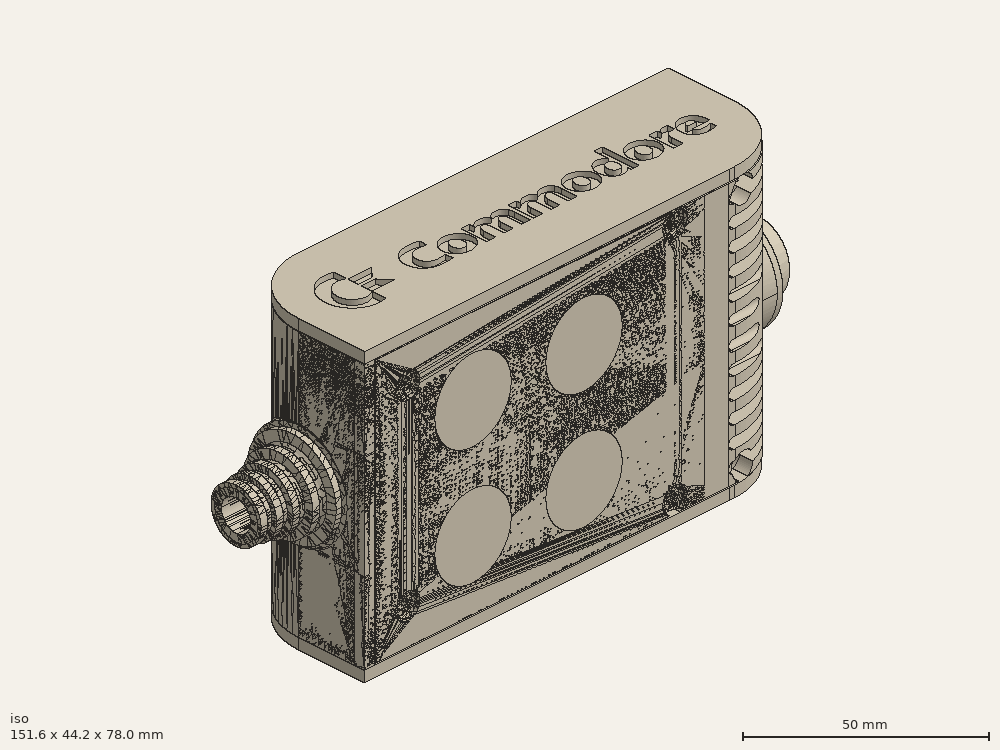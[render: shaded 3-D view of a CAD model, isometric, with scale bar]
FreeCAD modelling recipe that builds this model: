
FCSTD DOCUMENT  (FreeCAD 0.19R0.19.2)
Label: enclosure_220FCStd
License: All rights reserved
LicenseURL: http://en.wikipedia.org/wiki/All_rights_reserved
objects: Part::Revolution×152, Part::MultiFuse×146, Part::Feature×146, Sketcher::SketchObject×90, Part::Extrusion×74, Part::Cut×72, Part::Cylinder×70, Part::Fillet×58, Part::Box×36, App::MeasureDistance×4, Part::Chamfer×4, Part::FeaturePython×2, Image::ImagePlane×1, PartDesign::Body×1, Part::Mirroring×1
note: 852 computed .brp shape members not serialized (recipe doc carries the construction recipe); baked Part::Feature solids carry a one-line shape summary decoded from their .brp

FEATURE [Sketcher::SketchObject] Sketch  label="topSketch"
  FullyConstrained = true
  sketch-geometry (20):
    g0: LineSegment StartX=5.21097e-06 StartY=3 StartZ=0 EndX=5.21097e-06 EndY=19 EndZ=0
    g1: ArcOfCircle CenterX=19 CenterY=19 CenterZ=0 NormalX=0 NormalY=0 NormalZ=1 AngleXU=0 Radius=19 StartAngle=1.5708 EndAngle=3.14159
    g2: ArcOfCircle CenterX=19 CenterY=19 CenterZ=0 NormalX=0 NormalY=0 NormalZ=1 AngleXU=0 Radius=16 StartAngle=1.5708 EndAngle=3.14159
    g3: LineSegment StartX=114 StartY=35 StartZ=0 EndX=19 EndY=35 EndZ=0
    g4: LineSegment StartX=5.21097e-06 StartY=3 StartZ=0 EndX=5.21097e-06 EndY=0 EndZ=0
    g5: LineSegment StartX=3 StartY=0 StartZ=0 EndX=5.21097e-06 EndY=0 EndZ=0
    g6: LineSegment StartX=3 StartY=19 StartZ=0 EndX=3 EndY=0 EndZ=0
    g7: LineSegment StartX=19 StartY=38 StartZ=0 EndX=124 EndY=38 EndZ=0
    g8: Circle CenterX=119 CenterY=35 CenterZ=0 NormalX=0 NormalY=0 NormalZ=1 AngleXU=0 Radius=1
    g9: Circle CenterX=121 CenterY=35 CenterZ=0 NormalX=0 NormalY=0 NormalZ=1 AngleXU=0 Radius=1
    g10: Circle CenterX=121 CenterY=33 CenterZ=0 NormalX=0 NormalY=0 NormalZ=1 AngleXU=0 Radius=1
    g11: BSplineCurve PolesCount=3 KnotsCount=2 Degree=2 IsPeriodic=0
    g12: GeomPoint X=119 Y=35 Z=0
    g13: GeomPoint X=121 Y=33 Z=0
    g14: LineSegment StartX=119 StartY=35 StartZ=0 EndX=114 EndY=35 EndZ=0
    g15: ArcOfCircle CenterX=105 CenterY=19 CenterZ=0 NormalX=0 NormalY=0 NormalZ=1 AngleXU=0 Radius=19 StartAngle=5.7297 EndAngle=6.28319
    g16: ArcOfCircle CenterX=105 CenterY=19 CenterZ=0 NormalX=0 NormalY=0 NormalZ=1 AngleXU=0 Radius=16 StartAngle=5.60905 EndAngle=6.28319
    g17: LineSegment StartX=121 StartY=33 StartZ=0 EndX=121 EndY=19 EndZ=0
    g18: LineSegment StartX=124 StartY=38 StartZ=0 EndX=124 EndY=19 EndZ=0
    g19: LineSegment StartX=117.5 StartY=9.01251 StartZ=0 EndX=121.163 EndY=9.0125 EndZ=0
  constraints (46):
    c: Vertical(g0)
    c: Block(g0)
    c: Coincident(g1,g0)
    c: Block(g1)
    c: Coincident(g2,g1)
    c: Block(g2)
    c: Coincident(g3,g2)
    c: Horizontal(g3)
    c: Tangent(g3,g2)
    c: Coincident(g4,g0)
    c: Distance(g4) = 3
    c: Vertical(g4)
    c: Coincident(g5,g4)
    c: Horizontal(g5)
    c: Coincident(g6,g2)
    c: Coincident(g6,g5)
    c: Vertical(g6)
    c: Horizontal(g7)
    c: Distance(g7) = 105
    c: Coincident(g7,g1)
    c: Block(g3)
    c: Weight(g8) = 1
    c: Equal(g8,g9)
    c: Equal(g8,g10)
    c: InternalAlignment(g8,g11)
    c: InternalAlignment(g9,g11)
    c: InternalAlignment(g10,g11)
    c: InternalAlignment(g12,g11)
    c: InternalAlignment(g13,g11)
    c: Block(g11)
    c: Coincident(g14,g11)
    c: Coincident(g14,g3)
    c: Horizontal(g14)
    c: Block(g15)
    c: Coincident(g16,g15)
    c: Block(g16)
    c: Coincident(g17,g11)
    c: Coincident(g17,g16)
    c: Vertical(g17)
    c: Distance(g17) = 14
    c: Coincident(g18,g7)
    c: Coincident(g18,g15)
    c: Vertical(g18)
    c: Distance(g18) = 19
    c: Coincident(g19,g16)
    c: Coincident(g19,g15)
FEATURE [Sketcher::SketchObject] Sketch001  label="bottomSketch"
  FullyConstrained = true
  sketch-geometry (32):
    g0: LineSegment StartX=3.3 StartY=-6.03275e-07 StartZ=0 EndX=98 EndY=-6.03275e-07 EndZ=0
    g1: ArcOfCircle CenterX=98 CenterY=19 CenterZ=0 NormalX=0 NormalY=0 NormalZ=1 AngleXU=0 Radius=19 StartAngle=4.71239 EndAngle=5.71103
    g2: LineSegment StartX=6.3 StartY=8 StartZ=0 EndX=3.3 EndY=8 EndZ=0
    g3: LineSegment StartX=3.3 StartY=8 StartZ=0 EndX=3.3 EndY=-6.03275e-07 EndZ=0
    g4: ArcOfCircle CenterX=8.3 CenterY=5 CenterZ=0 NormalX=0 NormalY=0 NormalZ=1 AngleXU=0 Radius=2 StartAngle=3.14159 EndAngle=4.71239
    g5: LineSegment StartX=6.3 StartY=8 StartZ=0 EndX=6.3 EndY=5 EndZ=0
    g6: ArcOfCircle CenterX=98 CenterY=19 CenterZ=0 NormalX=0 NormalY=0 NormalZ=1 AngleXU=0 Radius=12.7 StartAngle=4.71239 EndAngle=6.28319
    g7: LineSegment StartX=94.7 StartY=3 StartZ=0 EndX=8.3 EndY=3 EndZ=0
    g8-g12: Circle x5 (B-spline internal-alignment scaffolding for g13; pole/knot coordinates omitted)
    g13: BSplineCurve PolesCount=5 KnotsCount=3 Degree=3 IsPeriodic=0
    g14: GeomPoint X=98 Y=6.3 Z=0
    g15: GeomPoint X=96.3938 Y=4.71946 Z=0
    g16: GeomPoint X=94.7 Y=3 Z=0
    g17-g23: Circle x7 (B-spline internal-alignment scaffolding for g24; pole/knot coordinates omitted)
    g24: BSplineCurve PolesCount=7 KnotsCount=5 Degree=3 IsPeriodic=0
    g25-g29: GeomPoint x5 (B-spline internal-alignment scaffolding for g24; pole/knot coordinates omitted)
    g30: ArcOfCircle CenterX=98 CenterY=19 CenterZ=0 NormalX=0 NormalY=0 NormalZ=1 AngleXU=0 Radius=15.7 StartAngle=5.81226 EndAngle=6.28319
    g31: LineSegment StartX=110.7 StartY=19 StartZ=0 EndX=113.7 EndY=19 EndZ=0
  constraints (41):
    c: Horizontal(g0)
    c: Coincident(g1,g0)
    c: Block(g1)
    c: Horizontal(g2)
    c: Distance(g2) = 3
    c: Coincident(g3,g2)
    c: Vertical(g3)
    c: Coincident(g3,g0)
    c: Block(g4)
    c: Block(g2)
    c: Coincident(g5,g2)
    c: Coincident(g5,g4)
    c: Vertical(g5)
    c: Coincident(g6,g1)
    c: Block(g6)
    c: Coincident(g7,g4)
    c: Horizontal(g7)
    c: Block(g0)
    c: Block(g7)
    c: Block(g3)
    c: Coincident(g13,g6)
    c: Weight(g8) = 1
    c: Equal(g8, g9-g12) x4
    c: Coincident(g13,g7)
    c: InternalAlignment(g8-g12 -> g13) x5
    c: InternalAlignment(g14,g13)
    c: InternalAlignment(g15,g13)
    c: InternalAlignment(g16,g13)
    c: Block(g13)
    c: Weight(g17) = 1
    c: Equal(g17, g18-g23) x6
    c: Coincident(g24,g1)
    c: InternalAlignment(g17-g23 -> g24) x7
    c: InternalAlignment(g25-g29 -> g24) x5
    c: Block(g24)
    c: Coincident(g30,g24)
    c: Coincident(g31,g6)
    c: Coincident(g31,g30)
    c: Horizontal(g31)
    c: Block(g31)
    c: Block(g30)
FEATURE [Part::Extrusion] Extrude  label="top"
  Base = -> Sketch
  Dir = (0,0,1)
  DirMode = 2
  FaceMakerClass = Part::FaceMakerBullseye
  LengthFwd = 72
  LengthRev = 0
  Solid = true
  Symmetric = false
FEATURE [Part::Extrusion] Extrude001  label="bottom"
  Base = -> Sketch001
  Dir = (0,0,1)
  DirMode = 2
  FaceMakerClass = Part::FaceMakerBullseye
  LengthFwd = 71.4
  LengthRev = 0
  Placement = pos=(0,0,0.3) rot=(0,0,1;0rad)
  Solid = true
  Symmetric = false
FEATURE [Sketcher::SketchObject] Sketch002  label="topSketch001"
  FullyConstrained = true
  sketch-geometry (8):
    g0: ArcOfCircle CenterX=19 CenterY=19.0975 CenterZ=0 NormalX=0 NormalY=0 NormalZ=1 AngleXU=0 Radius=18.9025 StartAngle=1.5708 EndAngle=3.14674
    g1: LineSegment StartX=0.0977805 StartY=19.0003 StartZ=0 EndX=0.0977805 EndY=0.000251602 EndZ=0
    g2: LineSegment StartX=19 StartY=38 StartZ=0 EndX=124 EndY=38 EndZ=0
    g3: LineSegment StartX=0.0977805 StartY=0.000251602 StartZ=0 EndX=105.098 EndY=0.000251602 EndZ=0
    g4: LineSegment StartX=124 StartY=38 StartZ=0 EndX=125.616 EndY=38 EndZ=0
    g5: LineSegment StartX=105.098 StartY=0.000251602 StartZ=0 EndX=106.713 EndY=0.000251602 EndZ=0
    g6: ArcOfCircle CenterX=106.616 CenterY=19 CenterZ=0 NormalX=0 NormalY=0 NormalZ=1 AngleXU=0 Radius=19 StartAngle=4.71754 EndAngle=6.28319
    g7: LineSegment StartX=125.616 StartY=38 StartZ=0 EndX=125.616 EndY=19 EndZ=0
  constraints (21):
    c: Block(g0)
    c: Coincident(g1,g0)
    c: Vertical(g1)
    c: Horizontal(g2)
    c: Distance(g2) = 105
    c: Coincident(g2,g0)
    c: Distance(g1) = 19
    c: Coincident(g3,g1)
    c: Horizontal(g3)
    c: Distance(g3) = 105
    c: Coincident(g4,g2)
    c: Horizontal(g4)
    c: Distance(g4) = 1.61553
    c: Horizontal(g5)
    c: Equal(g4,g5) = 1.61553
    c: Coincident(g5,g3)
    c: Block(g6)
    c: Coincident(g6,g5)
    c: Coincident(g7,g4)
    c: Coincident(g7,g6)
    c: Vertical(g7)
FEATURE [Part::Extrusion] Extrude002  label="sideA"
  Base = -> Sketch002
  Dir = (0,0,1)
  DirMode = 2
  FaceMakerClass = Part::FaceMakerBullseye
  LengthFwd = 3
  LengthRev = 0
  Placement = pos=(0,0,-3) rot=(0,0,1;0rad)
  Solid = true
  Symmetric = false
FEATURE [Sketcher::SketchObject] Sketch003  label="topSketch002"
  FullyConstrained = true
  sketch-geometry (6):
    g0: LineSegment StartX=19 StartY=38 StartZ=0 EndX=117 EndY=38 EndZ=0
    g1: ArcOfCircle CenterX=19 CenterY=19 CenterZ=0 NormalX=0 NormalY=0 NormalZ=1 AngleXU=0 Radius=19 StartAngle=1.5708 EndAngle=3.14159
    g2: LineSegment StartX=117 StartY=38 StartZ=0 EndX=117 EndY=19 EndZ=0
    g3: LineSegment StartX=98 StartY=1.0161e-12 StartZ=0 EndX=5.22862e-06 EndY=1.0161e-12 EndZ=0
    g4: LineSegment StartX=5.22862e-06 StartY=19 StartZ=0 EndX=5.22862e-06 EndY=1.0161e-12 EndZ=0
    g5: ArcOfCircle CenterX=98 CenterY=19 CenterZ=0 NormalX=0 NormalY=0 NormalZ=1 AngleXU=0 Radius=19 StartAngle=4.71239 EndAngle=6.28319
  constraints (16):
    c: Horizontal(g0)
    c: Distance(g0) = 98
    c: Coincident(g1,g0)
    c: Block(g1)
    c: Coincident(g2,g0)
    c: Vertical(g2)
    c: Distance(g2) = 19
    c: Horizontal(g3)
    c: Coincident(g4,g1)
    c: Vertical(g4)
    c: Coincident(g3,g4)
    c: Block(g3)
    c: Coincident(g5,g2)
    c: Coincident(g5,g3)
    c: Block(g0)
    c: Block(g5)
FEATURE [Sketcher::SketchObject] Sketch004
  FullyConstrained = true
  MapMode = 3
  Placement = pos=(0,0,0) rot=(1,0,0;1.5708rad)
  Support = -> [Extrude]
  sketch-geometry (8):
    g0: Circle CenterX=80.351 CenterY=-67.6202 CenterZ=0 NormalX=0 NormalY=0 NormalZ=1 AngleXU=0 Radius=2
    g1: Circle CenterX=80.351 CenterY=-67.6202 CenterZ=0 NormalX=0 NormalY=0 NormalZ=1 AngleXU=0 Radius=3
    g2: Circle CenterX=80.351 CenterY=-4.92017 CenterZ=0 NormalX=0 NormalY=0 NormalZ=1 AngleXU=0 Radius=2
    g3: Circle CenterX=80.351 CenterY=-4.92017 CenterZ=0 NormalX=0 NormalY=0 NormalZ=1 AngleXU=0 Radius=3
    g4: Circle CenterX=23.851 CenterY=-4.92017 CenterZ=0 NormalX=0 NormalY=0 NormalZ=1 AngleXU=0 Radius=2
    g5: Circle CenterX=23.851 CenterY=-4.92017 CenterZ=0 NormalX=0 NormalY=0 NormalZ=1 AngleXU=0 Radius=3
    g6: Circle CenterX=23.851 CenterY=-67.6202 CenterZ=0 NormalX=0 NormalY=0 NormalZ=1 AngleXU=0 Radius=2
    g7: Circle CenterX=23.851 CenterY=-67.6202 CenterZ=0 NormalX=0 NormalY=0 NormalZ=1 AngleXU=0 Radius=3
  constraints (8):
    c: Block(g3)
    c: Block(g2)
    c: Block(g1)
    c: Block(g0)
    c: Block(g6)
    c: Block(g7)
    c: Block(g4)
    c: Block(g5)
FEATURE [Part::Extrusion] Extrude004
  Base = -> Sketch004
  Dir = (0,-1,2e-16)
  DirMode = 2
  FaceMakerClass = Part::FaceMakerBullseye
  LengthFwd = 6
  LengthRev = 0
  Placement = pos=(0,9,0) rot=(0,0,1;0rad)
  Solid = true
  Symmetric = false
FEATURE [Sketcher::SketchObject] Sketch005
  FullyConstrained = true
  MapMode = 3
  Placement = pos=(0,0,0) rot=(1,0,0;1.5708rad)
  Support = -> [Extrude]
  sketch-geometry (8):
    g0: Circle CenterX=80.351 CenterY=-67.6202 CenterZ=0 NormalX=0 NormalY=0 NormalZ=1 AngleXU=0 Radius=3
    g1: Circle CenterX=80.351 CenterY=-4.92017 CenterZ=0 NormalX=0 NormalY=0 NormalZ=1 AngleXU=0 Radius=3
    g2: Circle CenterX=23.851 CenterY=-4.92017 CenterZ=0 NormalX=0 NormalY=0 NormalZ=1 AngleXU=0 Radius=3
    g3: Circle CenterX=23.851 CenterY=-67.6202 CenterZ=0 NormalX=0 NormalY=0 NormalZ=1 AngleXU=0 Radius=3
    g4: Circle CenterX=23.851 CenterY=-67.6202 CenterZ=0 NormalX=0 NormalY=0 NormalZ=1 AngleXU=0 Radius=5
    g5: Circle CenterX=80.351 CenterY=-67.6202 CenterZ=0 NormalX=0 NormalY=0 NormalZ=1 AngleXU=0 Radius=5
    g6: Circle CenterX=23.851 CenterY=-4.92017 CenterZ=0 NormalX=0 NormalY=0 NormalZ=1 AngleXU=0 Radius=5
    g7: Circle CenterX=80.351 CenterY=-4.92017 CenterZ=0 NormalX=0 NormalY=0 NormalZ=1 AngleXU=0 Radius=5
  constraints (8):
    c: Block(g1)
    c: Block(g0)
    c: Block(g3)
    c: Block(g2)
    c: Block(g5)
    c: Block(g4)
    c: Block(g6)
    c: Block(g7)
FEATURE [Part::Extrusion] Extrude005
  Base = -> Sketch005
  Dir = (0,-1,2e-16)
  DirMode = 2
  FaceMakerClass = Part::FaceMakerBullseye
  LengthFwd = 2
  LengthRev = 0
  Solid = true
  Symmetric = false
FEATURE [Sketcher::SketchObject] Sketch006
  FullyConstrained = true
  MapMode = 3
  Placement = pos=(0,0,0) rot=(1,0,0;1.5708rad)
  sketch-geometry (8):
    g0: Circle CenterX=80.351 CenterY=-67.6202 CenterZ=0 NormalX=0 NormalY=0 NormalZ=1 AngleXU=0 Radius=3
    g1: Circle CenterX=80.351 CenterY=-4.92017 CenterZ=0 NormalX=0 NormalY=0 NormalZ=1 AngleXU=0 Radius=3
    g2: Circle CenterX=23.851 CenterY=-4.92017 CenterZ=0 NormalX=0 NormalY=0 NormalZ=1 AngleXU=0 Radius=3
    g3: Circle CenterX=23.851 CenterY=-67.6202 CenterZ=0 NormalX=0 NormalY=0 NormalZ=1 AngleXU=0 Radius=3
    g4: Circle CenterX=23.851 CenterY=-67.6202 CenterZ=0 NormalX=0 NormalY=0 NormalZ=1 AngleXU=0 Radius=5
    g5: Circle CenterX=80.351 CenterY=-67.6202 CenterZ=0 NormalX=0 NormalY=0 NormalZ=1 AngleXU=0 Radius=5
    g6: Circle CenterX=23.851 CenterY=-4.92017 CenterZ=0 NormalX=0 NormalY=0 NormalZ=1 AngleXU=0 Radius=5
    g7: Circle CenterX=80.351 CenterY=-4.92017 CenterZ=0 NormalX=0 NormalY=0 NormalZ=1 AngleXU=0 Radius=5
  constraints (8):
    c: Block(g1)
    c: Block(g0)
    c: Block(g3)
    c: Block(g2)
    c: Block(g5)
    c: Block(g4)
    c: Block(g6)
    c: Block(g7)
FEATURE [Part::Extrusion] Extrude007
  Base = -> Sketch006
  Dir = (0,-1,2e-16)
  DirMode = 2
  FaceMakerClass = Part::FaceMakerBullseye
  LengthFwd = 2
  LengthRev = 0
  Solid = true
  Symmetric = false
FEATURE [Part::Fillet] Fillet
  Base = -> Extrude007
  Edges = 4 edges r=1.99: [Edge6,Edge12,Edge18,Edge24]
FEATURE [Part::Cut] Cut
  Base = -> Extrude005
  Placement = pos=(0,5,0) rot=(0,0,1;0rad)
  Tool = -> Fillet
FEATURE [Part::MultiFuse] Fusion  label="pCBScrews"
  Placement = pos=(-2.5,0,72.3) rot=(0,0,1;0rad)
  Shapes = -> [Extrude004,Cut]
FEATURE [App::MeasureDistance] Distance  label="Distance: 0.69 mm"
  Distance = 0.685967
  P1 = (24.0138,2.9647,0.3)
  P2 = (23.8901,3,-0.373787)
FEATURE [App::MeasureDistance] Distance001  label="Distance: 0.53 mm"
  Distance = 0.533607
  P1 = (80.2939,3,72.2334)
  P2 = (80.281,2.99661,71.7)
FEATURE [Part::Fillet] Fillet001
  Base = -> Extrude001
  Edges = 1 edges r=2.4: [Edge17]
FEATURE [Part::Fillet] Fillet002  label="bottom001"
  Base = -> Fillet001
  Edges = 1 edges r=2.4: [Edge36]
FEATURE [Part::Fillet] Fillet003  label="top001"
  Base = -> Extrude
  Edges = 1 edges r=2: [Edge1]
FEATURE [Sketcher::SketchObject] Sketch007
  FullyConstrained = true
  sketch-geometry (16):
    g0: LineSegment StartX=4 StartY=0 StartZ=0 EndX=4 EndY=2.4 EndZ=0
    g1: LineSegment StartX=4 StartY=2.4 StartZ=0 EndX=7 EndY=2.4 EndZ=0
    g2: LineSegment StartX=4 StartY=0 StartZ=0 EndX=5.7 EndY=0 EndZ=0
    g3: LineSegment StartX=5.7 StartY=0 StartZ=0 EndX=5.7 EndY=-5.6 EndZ=0
    g4-g8: Circle x5 (B-spline internal-alignment scaffolding for g9; pole/knot coordinates omitted)
    g9: BSplineCurve PolesCount=5 KnotsCount=3 Degree=3 IsPeriodic=0
    g10: GeomPoint X=7 Y=2.4 Z=0
    g11: GeomPoint X=10.4582 Y=-1.55472 Z=0
    g12: GeomPoint X=14 Y=-5.6 Z=0
    g13: LineSegment StartX=14 StartY=-5.6 StartZ=0 EndX=14 EndY=-14.1 EndZ=0
    g14: LineSegment StartX=14 StartY=-14.1 StartZ=0 EndX=6.5 EndY=-14.1 EndZ=0
    g15: LineSegment StartX=5.7 StartY=-5.6 StartZ=0 EndX=6.5 EndY=-14.1 EndZ=0
  constraints (28):
    c: Distance(g0) = 2.4
    c: Vertical(g0)
    c: Block(g0)
    c: Coincident(g1,g0)
    c: Horizontal(g1)
    c: Distance(g1) = 3
    c: Coincident(g2,g0)
    c: Horizontal(g2)
    c: Distance(g2) = 1.7
    c: Coincident(g3,g2)
    c: Vertical(g3)
    c: Distance(g3) = 5.6
    c: Coincident(g9,g1)
    c: Weight(g4) = 1
    c: Equal(g4, g5-g8) x4
    c: InternalAlignment(g4-g8 -> g9) x5
    c: InternalAlignment(g10,g9)
    c: InternalAlignment(g11,g9)
    c: InternalAlignment(g12,g9)
    c: Block(g9)
    c: Coincident(g13,g9)
    c: Vertical(g13)
    c: Distance(g13) = 8.5
    c: Coincident(g14,g13)
    c: Horizontal(g14)
    c: Distance(g14) = 7.5
    c: Coincident(g15,g3)
    c: Coincident(g15,g14)
FEATURE [Part::Feature] Face
  shape: bbox 10 x 16.5 x 2e-07 mm, 1 faces, 0 solids (baked)
FEATURE [Part::Revolution] Revolve  label="plugHousing"
  Angle = 360
  Axis = (0,1,0)
  Base = (0,0,0)
  FaceMakerClass = Part::FaceMakerBullseye
  Placement = pos=(0,0,36.15) rot=(0,0,1;0rad)
  Solid = false
  Source = -> Face
  Symmetric = false
FEATURE [Part::Feature] Face001
  shape: bbox 10 x 16.5 x 2e-07 mm, 1 faces, 0 solids (baked)
FEATURE [Part::Revolution] Revolve001  label="plugHousing001"
  Angle = 360
  Axis = (0,1,0)
  Base = (0,0,0)
  FaceMakerClass = Part::FaceMakerBullseye
  Placement = pos=(0,0,36.15) rot=(0,0,1;0rad)
  Solid = false
  Source = -> Face001
  Symmetric = false
FEATURE [Part::MultiFuse] Fusion001  label="plugHousing002"
  Placement = pos=(0,0,0) rot=(0,0,1;1.5708rad)
  Shapes = -> [Revolve001,Revolve]
FEATURE [Part::Feature] Face002
  shape: bbox 10 x 16.5 x 2e-07 mm, 1 faces, 0 solids (baked)
FEATURE [Part::Revolution] Revolve003  label="plugHousing005"
  Angle = 360
  Axis = (0,1,0)
  Base = (0,0,0)
  FaceMakerClass = Part::FaceMakerBullseye
  Placement = pos=(0,0,36.15) rot=(0,0,1;0rad)
  Solid = false
  Source = -> Face002
  Symmetric = false
FEATURE [Part::Feature] Face003
  shape: bbox 10 x 16.5 x 2e-07 mm, 1 faces, 0 solids (baked)
FEATURE [Part::Revolution] Revolve002  label="plugHousing003"
  Angle = 360
  Axis = (0,1,0)
  Base = (0,0,0)
  FaceMakerClass = Part::FaceMakerBullseye
  Placement = pos=(0,0,36.15) rot=(0,0,1;0rad)
  Solid = false
  Source = -> Face003
  Symmetric = false
FEATURE [Part::MultiFuse] Fusion002  label="plugHousing004"
  Placement = pos=(0,0,0) rot=(0,0,1;1.5708rad)
  Shapes = -> [Revolve002,Revolve003]
FEATURE [Part::MultiFuse] Fusion003  label="plugHousing006"
  Placement = pos=(0,19,0) rot=(0,0,1;3.14159rad)
  Shapes = -> [Fusion002,Fusion001]
FEATURE [Part::Feature] Face004
  shape: bbox 10 x 16.5 x 2e-07 mm, 1 faces, 0 solids (baked)
FEATURE [Part::Revolution] Revolve006  label="plugHousing010"
  Angle = 360
  Axis = (0,1,0)
  Base = (0,0,0)
  FaceMakerClass = Part::FaceMakerBullseye
  Placement = pos=(0,0,36.15) rot=(0,0,1;0rad)
  Solid = false
  Source = -> Face004
  Symmetric = false
FEATURE [Part::Feature] Face005
  shape: bbox 10 x 16.5 x 2e-07 mm, 1 faces, 0 solids (baked)
FEATURE [Part::Revolution] Revolve007  label="plugHousing011"
  Angle = 360
  Axis = (0,1,0)
  Base = (0,0,0)
  FaceMakerClass = Part::FaceMakerBullseye
  Placement = pos=(0,0,36.15) rot=(0,0,1;0rad)
  Solid = false
  Source = -> Face005
  Symmetric = false
FEATURE [Part::Feature] Face006
  shape: bbox 10 x 16.5 x 2e-07 mm, 1 faces, 0 solids (baked)
FEATURE [Part::Revolution] Revolve004  label="plugHousing007"
  Angle = 360
  Axis = (0,1,0)
  Base = (0,0,0)
  FaceMakerClass = Part::FaceMakerBullseye
  Placement = pos=(0,0,36.15) rot=(0,0,1;0rad)
  Solid = false
  Source = -> Face006
  Symmetric = false
FEATURE [Part::MultiFuse] Fusion004  label="plugHousing009"
  Placement = pos=(0,0,0) rot=(0,0,1;1.5708rad)
  Shapes = -> [Revolve004,Revolve007]
FEATURE [Part::Feature] Face007
  shape: bbox 10 x 16.5 x 2e-07 mm, 1 faces, 0 solids (baked)
FEATURE [Part::Revolution] Revolve005  label="plugHousing008"
  Angle = 360
  Axis = (0,1,0)
  Base = (0,0,0)
  FaceMakerClass = Part::FaceMakerBullseye
  Placement = pos=(0,0,36.15) rot=(0,0,1;0rad)
  Solid = false
  Source = -> Face007
  Symmetric = false
FEATURE [Part::MultiFuse] Fusion005  label="plugHousing012"
  Placement = pos=(0,0,0) rot=(0,0,1;1.5708rad)
  Shapes = -> [Revolve006,Revolve005]
FEATURE [Part::MultiFuse] Fusion006  label="plugHousing013"
  Placement = pos=(0,19,0) rot=(0,0,1;3.14159rad)
  Shapes = -> [Fusion005,Fusion004]
FEATURE [Part::MultiFuse] Fusion007  label="plugHousing014"
  Placement = pos=(122.621,0,-0.15) rot=(0,0,1;0rad)
  Shapes = -> [Fusion003,Fusion006]
FEATURE [Part::Cylinder] Cylinder002
  Angle = 360
  AttacherType = Attacher::AttachEngine3D
  Height = 20
  Placement = pos=(0,0,36.15) rot=(0,0,1;0rad)
  Radius = 4
FEATURE [Part::Cylinder] Cylinder003
  Angle = 360
  AttacherType = Attacher::AttachEngine3D
  Height = 10
  Placement = pos=(0,0,36.15) rot=(0,0,1;0rad)
  Radius = 4
FEATURE [Part::MultiFuse] Fusion009  label="removeToCreateHoleForPlugHousing"
  Placement = pos=(70,19,36.15) rot=(0,1,0;1.5708rad)
  Shapes = -> [Cylinder002,Cylinder003]
FEATURE [Part::Cylinder] Cylinder004
  Angle = 360
  AttacherType = Attacher::AttachEngine3D
  Height = 20
  Placement = pos=(0,0,36.15) rot=(0,0,1;0rad)
  Radius = 4
FEATURE [Part::Cylinder] Cylinder005
  Angle = 360
  AttacherType = Attacher::AttachEngine3D
  Height = 10
  Placement = pos=(0,0,36.15) rot=(0,0,1;0rad)
  Radius = 4
FEATURE [Part::MultiFuse] Fusion010  label="removeToCreateHoleForPlugHousing001"
  Placement = pos=(70,19,36.15) rot=(0,1,0;1.5708rad)
  Shapes = -> [Cylinder004,Cylinder005]
FEATURE [Part::Cut] Cut001
  Base = -> Fillet003
  Tool = -> Fusion010
FEATURE [Part::Cut] Cut002  label="Bottom"
  Base = -> Fillet002
  Tool = -> Fusion009
FEATURE [Part::Feature] Face008
  shape: bbox 10 x 16.5 x 2e-07 mm, 1 faces, 0 solids (baked)
FEATURE [Part::Revolution] Revolve011  label="plugHousing021"
  Angle = 360
  Axis = (0,1,0)
  Base = (0,0,0)
  FaceMakerClass = Part::FaceMakerBullseye
  Placement = pos=(0,0,36.15) rot=(0,0,1;0rad)
  Solid = false
  Source = -> Face008
  Symmetric = false
FEATURE [Part::Feature] Face009
  shape: bbox 10 x 16.5 x 2e-07 mm, 1 faces, 0 solids (baked)
FEATURE [Part::Revolution] Revolve012  label="plugHousing022"
  Angle = 360
  Axis = (0,1,0)
  Base = (0,0,0)
  FaceMakerClass = Part::FaceMakerBullseye
  Placement = pos=(0,0,36.15) rot=(0,0,1;0rad)
  Solid = false
  Source = -> Face009
  Symmetric = false
FEATURE [Part::Feature] Face010 .. Face013  x4 (patterned run collapsed; names and placements below)
  shape: bbox 10 x 16.5 x 2e-07 mm, 1 faces, 0 solids (baked)
FEATURE [Part::Revolution] Revolve015  label="plugHousing027"
  Angle = 360
  Axis = (0,1,0)
  Base = (0,0,0)
  FaceMakerClass = Part::FaceMakerBullseye
  Placement = pos=(0,0,36.15) rot=(0,0,1;0rad)
  Solid = false
  Source = -> Face013
  Symmetric = false
FEATURE [Part::Feature] Face014
  shape: bbox 10 x 16.5 x 2e-07 mm, 1 faces, 0 solids (baked)
FEATURE [Part::Feature] Face015
  shape: bbox 10 x 16.5 x 2e-07 mm, 1 faces, 0 solids (baked)
FEATURE [Part::Feature] Face016
  shape: bbox 10 x 16.5 x 2e-07 mm, 1 faces, 0 solids (baked)
FEATURE [Part::Revolution] Revolve019  label="plugHousing033"
  Angle = 360
  Axis = (0,1,0)
  Base = (0,0,0)
  FaceMakerClass = Part::FaceMakerBullseye
  Placement = pos=(0,0,36.15) rot=(0,0,1;0rad)
  Solid = false
  Source = -> Face016
  Symmetric = false
FEATURE [Part::Feature] Face017
  shape: bbox 10 x 16.5 x 2e-07 mm, 1 faces, 0 solids (baked)
FEATURE [Part::Revolution] Revolve020  label="plugHousing034"
  Angle = 360
  Axis = (0,1,0)
  Base = (0,0,0)
  FaceMakerClass = Part::FaceMakerBullseye
  Placement = pos=(0,0,36.15) rot=(0,0,1;0rad)
  Solid = false
  Source = -> Face017
  Symmetric = false
FEATURE [Part::Feature] Face018
  shape: bbox 10 x 16.5 x 2e-07 mm, 1 faces, 0 solids (baked)
FEATURE [Part::Revolution] Revolve016  label="plugHousing030"
  Angle = 360
  Axis = (0,1,0)
  Base = (0,0,0)
  FaceMakerClass = Part::FaceMakerBullseye
  Placement = pos=(0,0,36.15) rot=(0,0,1;0rad)
  Solid = false
  Source = -> Face018
  Symmetric = false
FEATURE [Part::MultiFuse] Fusion020  label="plugHousing038"
  Placement = pos=(0,0,0) rot=(0,0,1;1.5708rad)
  Shapes = -> [Revolve016,Revolve020]
FEATURE [Part::Feature] Face019
  shape: bbox 10 x 16.5 x 2e-07 mm, 1 faces, 0 solids (baked)
FEATURE [Part::Feature] Face020
  shape: bbox 10 x 16.5 x 2e-07 mm, 1 faces, 0 solids (baked)
FEATURE [Part::Revolution] Revolve017  label="plugHousing031"
  Angle = 360
  Axis = (0,1,0)
  Base = (0,0,0)
  FaceMakerClass = Part::FaceMakerBullseye
  Placement = pos=(0,0,36.15) rot=(0,0,1;0rad)
  Solid = false
  Source = -> Face020
  Symmetric = false
FEATURE [Part::MultiFuse] Fusion021  label="plugHousing039"
  Placement = pos=(0,0,0) rot=(0,0,1;1.5708rad)
  Shapes = -> [Revolve019,Revolve017]
FEATURE [Part::MultiFuse] Fusion023  label="plugHousing041"
  Placement = pos=(0,19,0) rot=(0,0,1;3.14159rad)
  Shapes = -> [Fusion021,Fusion020]
FEATURE [Part::Revolution] Revolve022  label="plugHousing043"
  Angle = 360
  Axis = (0,1,0)
  Base = (0,0,0)
  FaceMakerClass = Part::FaceMakerBullseye
  Placement = pos=(0,0,36.15) rot=(0,0,1;0rad)
  Solid = false
  Source = -> Face019
  Symmetric = false
FEATURE [Part::Feature] Face021
  shape: bbox 10 x 16.5 x 2e-07 mm, 1 faces, 0 solids (baked)
FEATURE [Part::Revolution] Revolve023  label="plugHousing044"
  Angle = 360
  Axis = (0,1,0)
  Base = (0,0,0)
  FaceMakerClass = Part::FaceMakerBullseye
  Placement = pos=(0,0,36.15) rot=(0,0,1;0rad)
  Solid = false
  Source = -> Face021
  Symmetric = false
FEATURE [Part::Feature] Face022
  shape: bbox 10 x 16.5 x 2e-07 mm, 1 faces, 0 solids (baked)
FEATURE [Part::Revolution] Revolve018  label="plugHousing032"
  Angle = 360
  Axis = (0,1,0)
  Base = (0,0,0)
  FaceMakerClass = Part::FaceMakerBullseye
  Placement = pos=(0,0,36.15) rot=(0,0,1;0rad)
  Solid = false
  Source = -> Face022
  Symmetric = false
FEATURE [Part::MultiFuse] Fusion022  label="plugHousing040"
  Placement = pos=(0,0,0) rot=(0,0,1;1.5708rad)
  Shapes = -> [Revolve018,Revolve023]
FEATURE [Part::Feature] Face023
  shape: bbox 10 x 16.5 x 2e-07 mm, 1 faces, 0 solids (baked)
FEATURE [Part::Revolution] Revolve021  label="plugHousing035"
  Angle = 360
  Axis = (0,1,0)
  Base = (0,0,0)
  FaceMakerClass = Part::FaceMakerBullseye
  Placement = pos=(0,0,36.15) rot=(0,0,1;0rad)
  Solid = false
  Source = -> Face023
  Symmetric = false
FEATURE [Part::MultiFuse] Fusion018  label="plugHousing036"
  Placement = pos=(0,0,0) rot=(0,0,1;1.5708rad)
  Shapes = -> [Revolve022,Revolve021]
FEATURE [Part::MultiFuse] Fusion019  label="plugHousing037"
  Placement = pos=(0,19,0) rot=(0,0,1;3.14159rad)
  Shapes = -> [Fusion018,Fusion022]
FEATURE [Part::MultiFuse] Fusion024  label="plugHousing042"
  Placement = pos=(122.621,0,-0.15) rot=(0,0,1;0rad)
  Shapes = -> [Fusion023,Fusion019]
FEATURE [Part::Cylinder] Cylinder006
  Angle = 360
  AttacherType = Attacher::AttachEngine3D
  Height = 20
  Placement = pos=(0,0,36.15) rot=(0,0,1;0rad)
  Radius = 14.3
FEATURE [Part::Cylinder] Cylinder007
  Angle = 360
  AttacherType = Attacher::AttachEngine3D
  Height = 10
  Placement = pos=(0,0,36.15) rot=(0,0,1;0rad)
  Radius = 4
FEATURE [Part::MultiFuse] Fusion026  label="removeToCreteHoleForPlugHousing"
  Placement = pos=(70,19,36) rot=(0,1,0;1.5708rad)
  Shapes = -> [Cylinder006,Cylinder007]
FEATURE [Part::Box] Box001  label="Cube001"
  AttacherType = Attacher::AttachEngine3D
  Height = 28
  Length = 3
  Placement = pos=(110.7,19,22) rot=(0,0,1;0rad)
  Width = 15.7
FEATURE [Part::Cut] Cut003  label="top002"
  Base = -> Cut001
  Tool = -> Fusion007
FEATURE [Part::Revolution] Revolve008  label="plugHousing015"
  Angle = 360
  Axis = (0,1,0)
  Base = (0,0,0)
  FaceMakerClass = Part::FaceMakerBullseye
  Placement = pos=(0,0,36.15) rot=(0,0,1;0rad)
  Solid = false
  Source = -> Face010
  Symmetric = false
FEATURE [Part::MultiFuse] Fusion013  label="plugHousing020"
  Placement = pos=(0,0,0) rot=(0,0,1;1.5708rad)
  Shapes = -> [Revolve008,Revolve012]
FEATURE [Part::Cut] Cut004  label="top003"
  Base = -> Cut003
  Placement = pos=(1,0,0) rot=(0,0,1;0rad)
  Tool = -> Fusion026
FEATURE [Part::Cylinder] Cylinder008
  Angle = 360
  AttacherType = Attacher::AttachEngine3D
  Height = 20
  Placement = pos=(0,0,36.15) rot=(0,0,1;0rad)
  Radius = 10.3
FEATURE [Part::Cylinder] Cylinder009
  Angle = 360
  AttacherType = Attacher::AttachEngine3D
  Height = 10
  Placement = pos=(0,0,36.15) rot=(0,0,1;0rad)
  Radius = 4
FEATURE [Part::MultiFuse] Fusion027  label="removeToCreteHoleForPlugHousing001"
  Placement = pos=(70,19,36) rot=(0,1,0;1.5708rad)
  Shapes = -> [Cylinder008,Cylinder009]
FEATURE [Part::Cut] Cut005  label="plugHousingTab"
  Base = -> Box001
  Tool = -> Fusion027
FEATURE [Part::MultiFuse] Fusion028  label="plugHousing045"
  Shapes = -> [Fusion024,Cut005]
FEATURE [Part::Box] Box002  label="Cube002"
  AttacherType = Attacher::AttachEngine3D
  Height = 28.8
  Length = 3
  Placement = pos=(107.3,28,21.6) rot=(0,0,1;0rad)
  Width = 7
FEATURE [Part::Box] Box003  label="Cube003"
  AttacherType = Attacher::AttachEngine3D
  Height = 3
  Length = 6.4
  Placement = pos=(107.3,28,18.6) rot=(0,0,1;0rad)
  Width = 7
FEATURE [Part::Box] Box004  label="Cube004"
  AttacherType = Attacher::AttachEngine3D
  Height = 3
  Length = 6.4
  Placement = pos=(107.3,28,50.4) rot=(0,0,1;0rad)
  Width = 7
FEATURE [Part::MultiFuse] Fusion029  label="plugHousingBracketHolder"
  Shapes = -> [Box004,Box002,Box003]
FEATURE [Part::Cylinder] Cylinder010
  Angle = 360
  AttacherType = Attacher::AttachEngine3D
  Height = 20
  Placement = pos=(0,0,36.15) rot=(0,0,1;0rad)
  Radius = 14.3
FEATURE [Part::Cylinder] Cylinder011
  Angle = 360
  AttacherType = Attacher::AttachEngine3D
  Height = 10
  Placement = pos=(0,0,36.15) rot=(0,0,1;0rad)
  Radius = 4
FEATURE [Part::MultiFuse] Fusion030  label="removeToCreteHoleForPlugHousing002"
  Placement = pos=(70,19,36) rot=(0,1,0;1.5708rad)
  Shapes = -> [Cylinder010,Cylinder011]
FEATURE [Part::Cut] Cut006  label="plugHousingBracketHolder001"
  Base = -> Fusion029
  Tool = -> Fusion030
FEATURE [Part::Cylinder] Cylinder012
  Angle = 360
  AttacherType = Attacher::AttachEngine3D
  Height = 20
  Placement = pos=(0,0,36.15) rot=(0,0,1;0rad)
  Radius = 7
FEATURE [Part::Cylinder] Cylinder013
  Angle = 360
  AttacherType = Attacher::AttachEngine3D
  Height = 10
  Placement = pos=(0,0,36.15) rot=(0,0,1;0rad)
  Radius = 4
FEATURE [Part::MultiFuse] Fusion032  label="removeToCreteHoleForPlugHousing003"
  Placement = pos=(70,19,36) rot=(0,1,0;1.5708rad)
  Shapes = -> [Cylinder012,Cylinder013]
FEATURE [Part::Cut] Cut007  label="bottom002"
  Base = -> Cut002
  Tool = -> Fusion032
FEATURE [Sketcher::SketchObject] Sketch008
  FullyConstrained = true
  sketch-geometry (54):
    g0: LineSegment StartX=-4.2 StartY=0 StartZ=0 EndX=-6.2 EndY=0 EndZ=0
    g1: LineSegment StartX=-14 StartY=-18 StartZ=0 EndX=-14 EndY=-26.5 EndZ=0
    g2: LineSegment StartX=-4.2 StartY=0 StartZ=0 EndX=-4.2 EndY=-13.4877 EndZ=0
    g3: Circle CenterX=-4.2 CenterY=-13.4877 CenterZ=0 NormalX=0 NormalY=0 NormalZ=1 AngleXU=0 Radius=1
    g4: Circle CenterX=-4.2 CenterY=-26.5 CenterZ=0 NormalX=0 NormalY=0 NormalZ=1 AngleXU=0 Radius=1
    g5: Circle CenterX=-8.2 CenterY=-26.5 CenterZ=0 NormalX=0 NormalY=0 NormalZ=1 AngleXU=0 Radius=1
    g6: BSplineCurve PolesCount=3 KnotsCount=2 Degree=2 IsPeriodic=0
    g7: GeomPoint X=-4.2 Y=-13.4877 Z=0
    g8: GeomPoint X=-8.2 Y=-26.5 Z=0
    g9: LineSegment StartX=-14 StartY=-26.5 StartZ=0 EndX=-8.2 EndY=-26.5 EndZ=0
    g10: LineSegment StartX=-10.15 StartY=-12 StartZ=0 EndX=-10.15 EndY=-14 EndZ=0
    g11: LineSegment StartX=-12.8401 StartY=-16 StartZ=0 EndX=-10.1571 EndY=-16 EndZ=0
    g12: LineSegment StartX=-10.15 StartY=-14 StartZ=0 EndX=-8.70761 EndY=-14 EndZ=0
    g13: LineSegment StartX=-12.8401 StartY=-16 StartZ=0 EndX=-12.8401 EndY=-17.6958 EndZ=0
    g14: LineSegment StartX=-10.15 StartY=-12 StartZ=0 EndX=-7.79258 EndY=-12 EndZ=0
    g15: Circle CenterX=-6.2215 CenterY=-2 CenterZ=0 NormalX=0 NormalY=0 NormalZ=1 AngleXU=0 Radius=1
    g16: Circle CenterX=-6.22762 CenterY=-2.58724 CenterZ=0 NormalX=0 NormalY=0 NormalZ=1 AngleXU=0 Radius=1
    g17: Circle CenterX=-6.32538 CenterY=-4 CenterZ=0 NormalX=0 NormalY=0 NormalZ=1 AngleXU=0 Radius=1
    g18: BSplineCurve PolesCount=3 KnotsCount=2 Degree=2 IsPeriodic=0
    g19: GeomPoint X=-6.2215 Y=-2 Z=0
    g20: GeomPoint X=-6.32538 Y=-4 Z=0
    g21: Circle CenterX=-6.48644 CenterY=-5.99526 CenterZ=0 NormalX=0 NormalY=0 NormalZ=1 AngleXU=0 Radius=1
    g22: Circle CenterX=-6.58486 CenterY=-6.99526 CenterZ=0 NormalX=0 NormalY=0 NormalZ=1 AngleXU=0 Radius=1
    g23: Circle CenterX=-6.77343 CenterY=-8 CenterZ=0 NormalX=0 NormalY=0 NormalZ=1 AngleXU=0 Radius=1
    g24: BSplineCurve PolesCount=3 KnotsCount=2 Degree=2 IsPeriodic=0
    g25: GeomPoint X=-6.48644 Y=-5.99526 Z=0
    g26: GeomPoint X=-6.77343 Y=-8 Z=0
    g27: Circle CenterX=-7.19003 CenterY=-10 CenterZ=0 NormalX=0 NormalY=0 NormalZ=1 AngleXU=0 Radius=1
    g28: Circle CenterX=-7.44407 CenterY=-11.0915 CenterZ=0 NormalX=0 NormalY=0 NormalZ=1 AngleXU=0 Radius=1
    g29: Circle CenterX=-7.79258 CenterY=-12 CenterZ=0 NormalX=0 NormalY=0 NormalZ=1 AngleXU=0 Radius=1
    g30: BSplineCurve PolesCount=3 KnotsCount=2 Degree=2 IsPeriodic=0
    g31: GeomPoint X=-7.19003 Y=-10 Z=0
    g32: GeomPoint X=-7.79258 Y=-12 Z=0
    g33: Circle CenterX=-8.70761 CenterY=-14 CenterZ=0 NormalX=0 NormalY=0 NormalZ=1 AngleXU=0 Radius=1
    g34: Circle CenterX=-9.33087 CenterY=-15.1837 CenterZ=0 NormalX=0 NormalY=0 NormalZ=1 AngleXU=0 Radius=1
    g35: Circle CenterX=-10.1571 CenterY=-16 CenterZ=0 NormalX=0 NormalY=0 NormalZ=1 AngleXU=0 Radius=1
    g36: BSplineCurve PolesCount=3 KnotsCount=2 Degree=2 IsPeriodic=0
    g37: GeomPoint X=-8.70761 Y=-14 Z=0
    g38: GeomPoint X=-10.1571 Y=-16 Z=0
    g39: Circle CenterX=-12.8401 CenterY=-17.6958 CenterZ=0 NormalX=0 NormalY=0 NormalZ=1 AngleXU=0 Radius=1
    g40: Circle CenterX=-13.3521 CenterY=-17.9027 CenterZ=0 NormalX=0 NormalY=0 NormalZ=1 AngleXU=0 Radius=1
    g41: Circle CenterX=-14 CenterY=-18 CenterZ=0 NormalX=0 NormalY=0 NormalZ=1 AngleXU=0 Radius=1
    g42: BSplineCurve PolesCount=3 KnotsCount=2 Degree=2 IsPeriodic=0
    g43: GeomPoint X=-12.8401 Y=-17.6958 Z=0
    g44: GeomPoint X=-14 Y=-18 Z=0
    g45: LineSegment StartX=-6.2 StartY=0 StartZ=0 EndX=-7.2 EndY=0 EndZ=0
    g46: LineSegment StartX=-7.2 StartY=0 StartZ=0 EndX=-7.2 EndY=-2 EndZ=0
    g47: LineSegment StartX=-7.2 StartY=-2 StartZ=0 EndX=-6.2215 EndY=-2 EndZ=0
    g48: LineSegment StartX=-6.32538 StartY=-4 StartZ=0 EndX=-7.65538 EndY=-4 EndZ=0
    g49: LineSegment StartX=-7.65538 StartY=-4 StartZ=0 EndX=-7.65538 EndY=-5.99526 EndZ=0
    g50: LineSegment StartX=-7.65538 StartY=-5.99526 StartZ=0 EndX=-6.48644 EndY=-5.99526 EndZ=0
    g51: LineSegment StartX=-6.77343 StartY=-8 StartZ=0 EndX=-8.43343 EndY=-8 EndZ=0
    g52: LineSegment StartX=-8.43343 StartY=-8 StartZ=0 EndX=-8.43343 EndY=-10 EndZ=0
    g53: LineSegment StartX=-8.43343 StartY=-10 StartZ=0 EndX=-7.19003 EndY=-10 EndZ=0
  constraints (112):
    c: Horizontal(g0)
    c: Distance(g0) = 2
    c: Block(g0)
    c: Vertical(g1)
    c: Coincident(g2,g0)
    c: Vertical(g2)
    c: Block(g2)
    c: Coincident(g6,g2)
    c: Weight(g3) = 1
    c: Equal(g3,g4)
    c: Equal(g3,g5)
    c: InternalAlignment(g3,g6)
    c: InternalAlignment(g4,g6)
    c: InternalAlignment(g5,g6)
    c: InternalAlignment(g7,g6)
    c: InternalAlignment(g8,g6)
    c: Block(g6)
    c: Coincident(g9,g1)
    c: Coincident(g9,g6)
    c: Horizontal(g9)
    c: Vertical(g10)
    c: Block(g10)
    c: Horizontal(g11)
    c: Block(g11)
    c: Coincident(g12,g10)
    c: Horizontal(g12)
    c: Block(g12)
    c: Coincident(g13,g11)
    c: Vertical(g13)
    c: Block(g13)
    c: Coincident(g14,g10)
    c: Horizontal(g14)
    c: Block(g14)
    c: Block(g9)
    c: Block(g1)
    c: Weight(g15) = 1
    c: Equal(g15,g16)
    c: Equal(g15,g17)
    c: InternalAlignment(g15,g18)
    c: InternalAlignment(g16,g18)
    c: InternalAlignment(g17,g18)
    c: InternalAlignment(g19,g18)
    c: InternalAlignment(g20,g18)
    c: Weight(g21) = 1
    c: Equal(g21,g22)
    c: Equal(g21,g23)
    c: InternalAlignment(g21,g24)
    c: InternalAlignment(g22,g24)
    c: InternalAlignment(g23,g24)
    c: InternalAlignment(g25,g24)
    c: InternalAlignment(g26,g24)
    c: Weight(g27) = 1
    c: Equal(g27,g28)
    c: Equal(g27,g29)
    c: Coincident(g30,g14)
    c: InternalAlignment(g27,g30)
    c: InternalAlignment(g28,g30)
    c: InternalAlignment(g29,g30)
    c: InternalAlignment(g31,g30)
    c: InternalAlignment(g32,g30)
    c: Coincident(g36,g12)
    c: Weight(g33) = 1
    c: Equal(g33,g34)
    c: Equal(g33,g35)
    c: Coincident(g36,g11)
    c: InternalAlignment(g33,g36)
    c: InternalAlignment(g34,g36)
    c: InternalAlignment(g35,g36)
    c: InternalAlignment(g37,g36)
    c: InternalAlignment(g38,g36)
    c: Coincident(g42,g13)
    c: Weight(g39) = 1
    c: Equal(g39,g40)
    c: Equal(g39,g41)
    c: Coincident(g42,g1)
    c: InternalAlignment(g39,g42)
    c: InternalAlignment(g40,g42)
    c: InternalAlignment(g41,g42)
    c: InternalAlignment(g43,g42)
    c: InternalAlignment(g44,g42)
    c: Block(g18)
    c: Block(g24)
    c: Block(g30)
    c: Block(g36)
    c: Block(g42)
    c: Horizontal(g45)
    c: Coincident(g45,g0)
    c: Vertical(g46)
    c: Coincident(g46,g45)
    c: Coincident(g47,g46)
    c: Coincident(g47,g18)
    c: Horizontal(g47)
    c: Block(g46)
    c: Coincident(g48,g18)
    c: Horizontal(g48)
    c: Distance(g48) = 1.33
    c: Vertical(g49)
    c: Coincident(g49,g48)
    c: Coincident(g50,g49)
    c: Coincident(g50,g24)
    c: Horizontal(g50)
    c: Tangent(g50,g22)
    c: Horizontal(g51)
    c: Coincident(g51,g24)
    c: Block(g51)
    c: Vertical(g52)
    c: Block(g52)
    c: Coincident(g52,g51)
    c: Coincident(g53,g52)
    c: Coincident(g53,g30)
    c: Horizontal(g53)
    c: Distance(g1) = 8.5
FEATURE [Part::Feature] Face024
  shape: bbox 9.8 x 26.5 x 2e-07 mm, 1 faces, 0 solids (baked)
FEATURE [Part::Revolution] Revolve024
  Angle = 360
  Axis = (0,1,0)
  Base = (0,0,0)
  FaceMakerClass = Part::FaceMakerBullseye
  Placement = pos=(0,0,0) rot=(0,0,1;1.5708rad)
  Solid = false
  Source = -> Face024
  Symmetric = false
FEATURE [Part::Feature] Face025
  shape: bbox 9.8 x 26.5 x 2e-07 mm, 1 faces, 0 solids (baked)
FEATURE [Part::Revolution] Revolve025
  Angle = 360
  Axis = (0,1,0)
  Base = (0,0,0)
  FaceMakerClass = Part::FaceMakerBullseye
  Placement = pos=(0,0,0) rot=(0,0,1;1.5708rad)
  Solid = false
  Source = -> Face025
  Symmetric = false
FEATURE [Part::MultiFuse] Fusion033
  Placement = pos=(-18,19,36) rot=(0,0,1;0rad)
  Shapes = -> [Revolve025,Revolve024]
FEATURE [Part::Cylinder] Cylinder014
  Angle = 360
  AttacherType = Attacher::AttachEngine3D
  Height = 20
  Placement = pos=(0,0,36.15) rot=(0,0,1;0rad)
  Radius = 14.3
FEATURE [Part::Cylinder] Cylinder015
  Angle = 360
  AttacherType = Attacher::AttachEngine3D
  Height = 10
  Placement = pos=(0,0,36.15) rot=(0,0,1;0rad)
  Radius = 4
FEATURE [Part::MultiFuse] Fusion034  label="removeToCreteHoleForPlugHousing004"
  Placement = pos=(-42,19,36) rot=(0,1,0;1.5708rad)
  Shapes = -> [Cylinder014,Cylinder015]
FEATURE [Part::Cut] Cut008  label="top004"
  Base = -> Cut004
  Placement = pos=(-1,0,0) rot=(0,0,1;0rad)
  Tool = -> Fusion034
FEATURE [Part::Box] Box005  label="Cube005"
  AttacherType = Attacher::AttachEngine3D
  Height = 28
  Length = 3
  Placement = pos=(110.7,19,22) rot=(0,0,1;0rad)
  Width = 15.7
FEATURE [Part::Cylinder] Cylinder016
  Angle = 360
  AttacherType = Attacher::AttachEngine3D
  Height = 10
  Placement = pos=(0,0,36.15) rot=(0,0,1;0rad)
  Radius = 4
FEATURE [Part::Cylinder] Cylinder017
  Angle = 360
  AttacherType = Attacher::AttachEngine3D
  Height = 20
  Placement = pos=(0,0,36.15) rot=(0,0,1;0rad)
  Radius = 10.3
FEATURE [Part::MultiFuse] Fusion035  label="removeToCreteHoleForPlugHousing005"
  Placement = pos=(70,19,36) rot=(0,1,0;1.5708rad)
  Shapes = -> [Cylinder017,Cylinder016]
FEATURE [Part::Cut] Cut009  label="plugHousingTab001"
  Base = -> Box005
  Placement = pos=(-107.4,-14,0) rot=(0,0,1;0rad)
  Tool = -> Fusion035
FEATURE [Part::Box] Box006  label="Cube006"
  AttacherType = Attacher::AttachEngine3D
  Height = 28
  Length = 3
  Placement = pos=(110.7,19,22) rot=(0,0,1;0rad)
  Width = 15.7
FEATURE [Part::Cylinder] Cylinder018
  Angle = 360
  AttacherType = Attacher::AttachEngine3D
  Height = 10
  Placement = pos=(0,0,36.15) rot=(0,0,1;0rad)
  Radius = 4
FEATURE [Part::Cylinder] Cylinder019
  Angle = 360
  AttacherType = Attacher::AttachEngine3D
  Height = 20
  Placement = pos=(0,0,36.15) rot=(0,0,1;0rad)
  Radius = 10.3
FEATURE [Part::MultiFuse] Fusion036  label="removeToCreteHoleForPlugHousing006"
  Placement = pos=(70,19,36) rot=(0,1,0;1.5708rad)
  Shapes = -> [Cylinder019,Cylinder018]
FEATURE [Part::Cut] Cut010  label="plugHousingTab002"
  Base = -> Box006
  Placement = pos=(-107.4,-14,0) rot=(0,0,1;0rad)
  Tool = -> Fusion036
FEATURE [Part::MultiFuse] Fusion037
  Placement = pos=(9.6,23,0) rot=(0,0,1;3.14159rad)
  Shapes = -> [Cut009,Cut010]
FEATURE [Part::Box] Box  label="Cube"
  AttacherType = Attacher::AttachEngine3D
  Height = 10
  Length = 3
  Placement = pos=(3.3,4,12) rot=(0,0,1;0rad)
  Width = 10
FEATURE [Part::Fillet] Fillet004
  Base = -> Fusion028
  Edges = 1 edges r=2: [Edge25]
FEATURE [Part::Fillet] Fillet005  label="plugHousing046"
  Base = -> Fillet004
  Edges = 1 edges r=2: [Edge8]
FEATURE [Part::Fillet] Fillet006
  Base = -> Box
  Edges = 1 edges r=2: [Edge11]
FEATURE [Part::Box] Box007  label="Cube007"
  AttacherType = Attacher::AttachEngine3D
  Height = 10
  Length = 3
  Placement = pos=(3.3,4,50) rot=(0,0,1;0rad)
  Width = 10
FEATURE [Part::Fillet] Fillet007
  Base = -> Box007
  Edges = 1 edges r=2: [Edge12]
FEATURE [Part::Box] Box008  label="Cube008"
  AttacherType = Attacher::AttachEngine3D
  Height = 28
  Length = 4
  Placement = pos=(5,0,22) rot=(0,0,1;0rad)
  Width = 10
FEATURE [Part::Fillet] Fillet008
  Base = -> Box008
  Edges = 1 edges r=1: [Edge7]
FEATURE [Part::Fillet] Fillet009
  Base = -> Fillet008
  Edges = 1 edges r=2: [Edge5]
FEATURE [Part::Fillet] Fillet010
  Base = -> Fillet009
  Edges = 1 edges r=2: [Edge2]
FEATURE [Sketcher::SketchObject] Sketch009  label="topSketch003"
  FullyConstrained = true
  sketch-geometry (4):
    g0: LineSegment StartX=16.8446 StartY=31.512 StartZ=0 EndX=16.3251 EndY=34.4666 EndZ=0
    g1: ArcOfCircle CenterX=19 CenterY=19.2524 CenterZ=0 NormalX=0 NormalY=0 NormalZ=1 AngleXU=0 Radius=15.4476 StartAngle=1.74483 EndAngle=2.72717
    g2: ArcOfCircle CenterX=19 CenterY=19.2524 CenterZ=0 NormalX=0 NormalY=0 NormalZ=1 AngleXU=0 Radius=12.4476 StartAngle=1.74483 EndAngle=2.73189
    g3: LineSegment StartX=4.86004 StartY=25.4725 StartZ=0 EndX=7.58253 EndY=24.2107 EndZ=0
  constraints (7):
    c: Block(g0)
    c: Coincident(g1,g0)
    c: Coincident(g2,g0)
    c: Coincident(g3,g1)
    c: Coincident(g3,g2)
    c: Block(g1)
    c: Block(g2)
FEATURE [Part::Extrusion] Extrude008
  Base = -> Sketch009
  Dir = (0,0,1)
  DirMode = 2
  FaceMakerClass = Part::FaceMakerBullseye
  LengthFwd = 10
  LengthRev = 0
  Placement = pos=(0,0,31) rot=(0,0,1;0rad)
  Solid = true
  Symmetric = false
FEATURE [Part::Cylinder] Cylinder020
  Angle = 360
  AttacherType = Attacher::AttachEngine3D
  Height = 20
  Placement = pos=(0,0,36.15) rot=(0,0,1;0rad)
  Radius = 8.2
FEATURE [Part::Cylinder] Cylinder021
  Angle = 360
  AttacherType = Attacher::AttachEngine3D
  Height = 10
  Placement = pos=(0,0,36.15) rot=(0,0,1;0rad)
  Radius = 4
FEATURE [Part::MultiFuse] Fusion038  label="removeToCreteHoleForPlugHousing007"
  Placement = pos=(-42,19,36) rot=(0,1,0;1.5708rad)
  Shapes = -> [Cylinder020,Cylinder021]
FEATURE [Part::Cut] Cut011
  Base = -> Extrude008
  Tool = -> Fusion038
FEATURE [Part::Fillet] Fillet011
  Base = -> Cut011
  Edges = 1 edges r=2: [Edge1]
FEATURE [Part::Fillet] Fillet012
  Base = -> Fillet011
  Edges = 1 edges r=2.5: [Edge1]
FEATURE [Part::Fillet] Fillet013
  Base = -> Fillet012
  Edges = 1 edges r=2.5: [Edge2]
FEATURE [Part::Box] Box010  label="Cube010"
  AttacherType = Attacher::AttachEngine3D
  Height = 16
  Length = 8
  Placement = pos=(12.7,31.52,28) rot=(0,0,1;0rad)
  Width = 4
FEATURE [Sketcher::SketchObject] Sketch010  label="topSketch004"
  FullyConstrained = true
  sketch-geometry (4):
    g0: LineSegment StartX=16.8446 StartY=31.512 StartZ=0 EndX=16.3251 EndY=34.4666 EndZ=0
    g1: ArcOfCircle CenterX=19 CenterY=19.2524 CenterZ=0 NormalX=0 NormalY=0 NormalZ=1 AngleXU=0 Radius=15.4476 StartAngle=1.74483 EndAngle=2.72717
    g2: ArcOfCircle CenterX=19 CenterY=19.2524 CenterZ=0 NormalX=0 NormalY=0 NormalZ=1 AngleXU=0 Radius=12.4476 StartAngle=1.74483 EndAngle=2.73189
    g3: LineSegment StartX=4.86004 StartY=25.4725 StartZ=0 EndX=7.58253 EndY=24.2107 EndZ=0
  constraints (7):
    c: Block(g0)
    c: Coincident(g1,g0)
    c: Coincident(g2,g0)
    c: Coincident(g3,g1)
    c: Coincident(g3,g2)
    c: Block(g1)
    c: Block(g2)
FEATURE [Part::Cylinder] Cylinder022
  Angle = 360
  AttacherType = Attacher::AttachEngine3D
  Height = 10
  Placement = pos=(0,0,36.15) rot=(0,0,1;0rad)
  Radius = 4
FEATURE [Sketcher::SketchObject] Sketch011  label="topSketch005"
  FullyConstrained = true
  sketch-geometry (4):
    g0: LineSegment StartX=16.8446 StartY=31.512 StartZ=0 EndX=16.3251 EndY=34.4666 EndZ=0
    g1: ArcOfCircle CenterX=19 CenterY=19.2524 CenterZ=0 NormalX=0 NormalY=0 NormalZ=1 AngleXU=0 Radius=15.4476 StartAngle=1.74483 EndAngle=2.72717
    g2: ArcOfCircle CenterX=19 CenterY=19.2524 CenterZ=0 NormalX=0 NormalY=0 NormalZ=1 AngleXU=0 Radius=12.4476 StartAngle=1.74483 EndAngle=2.73189
    g3: LineSegment StartX=4.86004 StartY=25.4725 StartZ=0 EndX=7.58253 EndY=24.2107 EndZ=0
  constraints (7):
    c: Block(g0)
    c: Coincident(g1,g0)
    c: Coincident(g2,g0)
    c: Coincident(g3,g1)
    c: Coincident(g3,g2)
    c: Block(g1)
    c: Block(g2)
FEATURE [Part::Extrusion] Extrude010
  Base = -> Sketch011
  Dir = (0,0,1)
  DirMode = 2
  FaceMakerClass = Part::FaceMakerBullseye
  LengthFwd = 10.6
  LengthRev = 0
  Placement = pos=(0,0,31) rot=(0,0,1;0rad)
  Solid = true
  Symmetric = false
FEATURE [Part::Cylinder] Cylinder023
  Angle = 360
  AttacherType = Attacher::AttachEngine3D
  Height = 20
  Placement = pos=(0,0,36.15) rot=(0,0,1;0rad)
  Radius = 8.2
FEATURE [Part::MultiFuse] Fusion039  label="removeToCreteHoleForPlugHousing008"
  Placement = pos=(-42,19,36) rot=(0,1,0;1.5708rad)
  Shapes = -> [Cylinder023,Cylinder022]
FEATURE [Part::Cut] Cut012
  Base = -> Extrude010
  Placement = pos=(0,0,-0.3) rot=(0,0,1;0rad)
  Tool = -> Fusion039
FEATURE [Part::Cut] Cut013
  Base = -> Box010
  Tool = -> Cut012
FEATURE [Part::Fillet] Fillet014
  Base = -> Cut013
  Edges = 1 edges r=0.7: [Edge13]
FEATURE [Part::Fillet] Fillet015
  Base = -> Fillet014
  Edges = 1 edges r=0.7: [Edge13]
FEATURE [Part::Fillet] Fillet016
  Base = -> Fillet015
  Edges = 1 edges r=0.7: [Edge16]
FEATURE [Part::Fillet] Fillet017
  Base = -> Fillet016
  Edges = 1 edges r=0.7: [Edge11]
FEATURE [Part::Fillet] Fillet018
  Base = -> Fillet017
  Edges = 1 edges r=0.7: [Edge10]
FEATURE [Part::Fillet] Fillet019
  Base = -> Fillet018
  Edges = 1 edges r=1.2: [Edge5]
FEATURE [Part::Fillet] Fillet020
  Base = -> Fillet019
  Edges = 1 edges r=1.2: [Edge12]
FEATURE [Part::Fillet] Fillet021
  Base = -> Fillet020
  Edges = 1 edges r=2: [Edge1]
  Placement = pos=(0.3,0,0) rot=(0,0,1;0rad)
FEATURE [Part::MultiFuse] Fusion040  label="top005"
  Shapes = -> [Cut008,Fillet021]
FEATURE [Part::MultiFuse] Fusion041  label="wireHolder"
  Shapes = -> [Fusion033,Fillet013]
FEATURE [Part::MultiFuse] Fusion042
  Shapes = -> [Fillet007,Fusion041]
FEATURE [Part::MultiFuse] Fusion043  label="wireHolder001"
  Shapes = -> [Fusion042,Fillet010]
FEATURE [Part::MultiFuse] Fusion044  label="wireHolder002"
  Shapes = -> [Fillet006,Fusion037,Fusion043]
FEATURE [Part::Feature] Face026
  shape: bbox 11 x 6 x 2e-07 mm, 1 faces, 0 solids (baked)
FEATURE [Part::Revolution] Revolve026
  Angle = 360
  Axis = (0,1,0)
  Base = (0,0,0)
  FaceMakerClass = Part::FaceMakerBullseye
  Placement = pos=(30.3,-1,19.7) rot=(0,0,1;0rad)
  Solid = false
  Source = -> Face026
  Symmetric = false
FEATURE [Sketcher::SketchObject] Sketch013  label="topSketch006"
  FullyConstrained = true
  sketch-geometry (13):
    g0: LineSegment StartX=117 StartY=19 StartZ=0 EndX=117 EndY=38 EndZ=0
    g1: ArcOfCircle CenterX=98 CenterY=19 CenterZ=0 NormalX=0 NormalY=0 NormalZ=1 AngleXU=0 Radius=19 StartAngle=5.7297 EndAngle=6.28319
    g2: LineSegment StartX=0 StartY=3 StartZ=0 EndX=0 EndY=19 EndZ=0
    g3: LineSegment StartX=19 StartY=38 StartZ=0 EndX=117 EndY=38 EndZ=0
    g4: ArcOfCircle CenterX=19 CenterY=19 CenterZ=0 NormalX=0 NormalY=0 NormalZ=1 AngleXU=0 Radius=19 StartAngle=1.5708 EndAngle=3.14159
    g5: ArcOfCircle CenterX=19 CenterY=19 CenterZ=0 NormalX=0 NormalY=0 NormalZ=1 AngleXU=0 Radius=16 StartAngle=1.5708 EndAngle=3.14159
    g6: ArcOfCircle CenterX=98 CenterY=19 CenterZ=0 NormalX=0 NormalY=0 NormalZ=1 AngleXU=0 Radius=16 StartAngle=5.60905 EndAngle=6.28319
    g7: LineSegment StartX=114 StartY=19 StartZ=0 EndX=114 EndY=35 EndZ=0
    g8: LineSegment StartX=110.5 StartY=9.01251 StartZ=0 EndX=114.163 EndY=9.01251 EndZ=0
    g9: LineSegment StartX=114 StartY=35 StartZ=0 EndX=19 EndY=35 EndZ=0
    g10: LineSegment StartX=0 StartY=3 StartZ=0 EndX=0 EndY=0 EndZ=0
    g11: LineSegment StartX=3 StartY=0 StartZ=0 EndX=0 EndY=0 EndZ=0
    g12: LineSegment StartX=3 StartY=19 StartZ=0 EndX=3 EndY=0 EndZ=0
  constraints (33):
    c: Vertical(g0)
    c: Distance(g0) = 19
    c: Block(g0)
    c: Coincident(g1,g0)
    c: Block(g1)
    c: Vertical(g2)
    c: Block(g2)
    c: Coincident(g3,g0)
    c: Horizontal(g3)
    c: Distance(g3) = 98
    c: Coincident(g4,g3)
    c: Coincident(g4,g2)
    c: Block(g4)
    c: Coincident(g5,g4)
    c: Coincident(g6,g1)
    c: Block(g6)
    c: Block(g5)
    c: Coincident(g7,g6)
    c: Vertical(g7)
    c: Coincident(g8,g6)
    c: Coincident(g8,g1)
    c: Coincident(g9,g7)
    c: Coincident(g9,g5)
    c: Horizontal(g9)
    c: Tangent(g9,g5)
    c: Coincident(g10,g2)
    c: Distance(g10) = 3
    c: Vertical(g10)
    c: Coincident(g11,g10)
    c: Horizontal(g11)
    c: Coincident(g12,g5)
    c: Coincident(g12,g11)
    c: Vertical(g12)
FEATURE [Part::Extrusion] Extrude011  label="top006"
  Base = -> Sketch013
  Dir = (0,0,1)
  DirMode = 2
  FaceMakerClass = Part::FaceMakerBullseye
  LengthFwd = 72
  LengthRev = 0
  Solid = true
  Symmetric = false
FEATURE [Sketcher::SketchObject] Sketch014
  FullyConstrained = true
  MapMode = 3
  Placement = pos=(0,0,0) rot=(1,0,0;1.5708rad)
  Support = -> [Extrude011]
  sketch-geometry (8):
    g0: Circle CenterX=80.351 CenterY=-67.6202 CenterZ=0 NormalX=0 NormalY=0 NormalZ=1 AngleXU=0 Radius=2
    g1: Circle CenterX=80.351 CenterY=-67.6202 CenterZ=0 NormalX=0 NormalY=0 NormalZ=1 AngleXU=0 Radius=3
    g2: Circle CenterX=80.351 CenterY=-4.92017 CenterZ=0 NormalX=0 NormalY=0 NormalZ=1 AngleXU=0 Radius=2
    g3: Circle CenterX=80.351 CenterY=-4.92017 CenterZ=0 NormalX=0 NormalY=0 NormalZ=1 AngleXU=0 Radius=3
    g4: Circle CenterX=23.851 CenterY=-4.92017 CenterZ=0 NormalX=0 NormalY=0 NormalZ=1 AngleXU=0 Radius=2
    g5: Circle CenterX=23.851 CenterY=-4.92017 CenterZ=0 NormalX=0 NormalY=0 NormalZ=1 AngleXU=0 Radius=3
    g6: Circle CenterX=23.851 CenterY=-67.6202 CenterZ=0 NormalX=0 NormalY=0 NormalZ=1 AngleXU=0 Radius=2
    g7: Circle CenterX=23.851 CenterY=-67.6202 CenterZ=0 NormalX=0 NormalY=0 NormalZ=1 AngleXU=0 Radius=3
  constraints (8):
    c: Block(g3)
    c: Block(g2)
    c: Block(g1)
    c: Block(g0)
    c: Block(g6)
    c: Block(g7)
    c: Block(g4)
    c: Block(g5)
FEATURE [Part::Feature] Face027
  shape: bbox 11 x 6 x 2e-07 mm, 1 faces, 0 solids (baked)
FEATURE [Part::Revolution] Revolve027
  Angle = 360
  Axis = (0,1,0)
  Base = (0,0,0)
  FaceMakerClass = Part::FaceMakerBullseye
  Placement = pos=(30.3,-1,51.7) rot=(0,0,1;0rad)
  Solid = false
  Source = -> Face027
  Symmetric = false
FEATURE [Part::Feature] Face028
  shape: bbox 11 x 6 x 2e-07 mm, 1 faces, 0 solids (baked)
FEATURE [Part::Revolution] Revolve028
  Angle = 360
  Axis = (0,1,0)
  Base = (0,0,0)
  FaceMakerClass = Part::FaceMakerBullseye
  Placement = pos=(62.3,-1,19.7) rot=(0,0,1;0rad)
  Solid = false
  Source = -> Face028
  Symmetric = false
FEATURE [Part::Feature] Face029
  shape: bbox 11 x 6 x 2e-07 mm, 1 faces, 0 solids (baked)
FEATURE [Part::Revolution] Revolve029
  Angle = 360
  Axis = (0,1,0)
  Base = (0,0,0)
  FaceMakerClass = Part::FaceMakerBullseye
  Placement = pos=(62.3,-1,51.7) rot=(0,0,1;0rad)
  Solid = false
  Source = -> Face029
  Symmetric = false
FEATURE [Part::Feature] Wire
  shape: bbox 11 x 5.2 x 2e-07 mm, 0 faces, 0 solids (baked)
FEATURE [Part::Revolution] Revolve030
  Angle = 360
  Axis = (0,1,0)
  Base = (0,0,0)
  FaceMakerClass = Part::FaceMakerBullseye
  Placement = pos=(30.3,38,19.7) rot=(0,0,1;0rad)
  Solid = true
  Source = -> Wire
  Symmetric = false
FEATURE [Part::Feature] Wire001
  shape: bbox 11 x 5.2 x 2e-07 mm, 0 faces, 0 solids (baked)
FEATURE [Part::Revolution] Revolve031
  Angle = 360
  Axis = (0,1,0)
  Base = (0,0,0)
  FaceMakerClass = Part::FaceMakerBullseye
  Placement = pos=(30.3,38,51.7) rot=(0,0,1;0rad)
  Solid = true
  Source = -> Wire001
  Symmetric = false
FEATURE [Part::Feature] Wire002
  shape: bbox 11 x 5.2 x 2e-07 mm, 0 faces, 0 solids (baked)
FEATURE [Part::Revolution] Revolve032
  Angle = 360
  Axis = (0,1,0)
  Base = (0,0,0)
  FaceMakerClass = Part::FaceMakerBullseye
  Placement = pos=(62.3,38,51.7) rot=(0,0,1;0rad)
  Solid = true
  Source = -> Wire002
  Symmetric = false
FEATURE [Part::Feature] Wire003
  shape: bbox 11 x 5.2 x 2e-07 mm, 0 faces, 0 solids (baked)
FEATURE [Part::Revolution] Revolve033
  Angle = 360
  Axis = (0,1,0)
  Base = (0,0,0)
  FaceMakerClass = Part::FaceMakerBullseye
  Placement = pos=(62.3,38,19.7) rot=(0,0,1;0rad)
  Solid = true
  Source = -> Wire003
  Symmetric = false
FEATURE [Part::MultiFuse] Fusion045  label="altRandScrewHousing"
  Shapes = -> [Revolve029,Revolve027,Revolve028,Revolve026]
FEATURE [Part::MultiFuse] Fusion046  label="fanScrewHousing"
  Shapes = -> [Revolve033,Revolve032,Revolve031,Revolve030]
FEATURE [Sketcher::SketchObject] Sketch015
  FullyConstrained = true
  sketch-geometry (17):
    g0: Circle CenterX=-3.5 CenterY=23.5 CenterZ=0 NormalX=0 NormalY=0 NormalZ=1 AngleXU=0 Radius=1
    g1: Circle CenterX=-1 CenterY=15.25 CenterZ=0 NormalX=0 NormalY=0 NormalZ=1 AngleXU=0 Radius=1
    g2: Circle CenterX=-3.5 CenterY=7 CenterZ=0 NormalX=0 NormalY=0 NormalZ=1 AngleXU=0 Radius=1
    g3: BSplineCurve PolesCount=3 KnotsCount=2 Degree=2 IsPeriodic=0
    g4: GeomPoint X=-3.5 Y=23.5 Z=0
    g5: GeomPoint X=-3.5 Y=7 Z=0
    g6: Circle CenterX=-4.8 CenterY=30.5 CenterZ=0 NormalX=0 NormalY=0 NormalZ=1 AngleXU=0 Radius=1
    g7: Circle CenterX=-3.5 CenterY=30.5 CenterZ=0 NormalX=0 NormalY=0 NormalZ=1 AngleXU=0 Radius=1
    g8: Circle CenterX=-3.5 CenterY=29.2 CenterZ=0 NormalX=0 NormalY=0 NormalZ=1 AngleXU=0 Radius=1
    g9: BSplineCurve PolesCount=3 KnotsCount=2 Degree=2 IsPeriodic=0
    g10: GeomPoint X=-4.8 Y=30.5 Z=0
    g11: GeomPoint X=-3.5 Y=29.2 Z=0
    g12: LineSegment StartX=-3.5 StartY=29.2 StartZ=0 EndX=-3.5 EndY=23.5 EndZ=0
    g13: LineSegment StartX=-4.8 StartY=30.5 StartZ=0 EndX=0 EndY=30.5 EndZ=0
    g14: LineSegment StartX=-3.5 StartY=0.3 StartZ=0 EndX=0 EndY=0.3 EndZ=0
    g15: LineSegment StartX=-3.5 StartY=0.3 StartZ=0 EndX=-3.5 EndY=7 EndZ=0
    g16: LineSegment StartX=0 StartY=0.3 StartZ=0 EndX=0 EndY=30.5 EndZ=0
  constraints (34):
    c: Weight(g0) = 1
    c: Equal(g0,g1)
    c: Equal(g0,g2)
    c: InternalAlignment(g0,g3)
    c: InternalAlignment(g1,g3)
    c: InternalAlignment(g2,g3)
    c: InternalAlignment(g4,g3)
    c: InternalAlignment(g5,g3)
    c: Block(g3)
    c: Weight(g6) = 1
    c: Equal(g6,g7)
    c: Equal(g6,g8)
    c: InternalAlignment(g6,g9)
    c: InternalAlignment(g7,g9)
    c: InternalAlignment(g8,g9)
    c: InternalAlignment(g10,g9)
    c: InternalAlignment(g11,g9)
    c: Block(g9)
    c: Coincident(g12,g9)
    c: Coincident(g12,g3)
    c: Vertical(g12)
    c: Coincident(g13,g9)
    c: Horizontal(g13)
    c: Distance(g13) = 4.8
    c: Horizontal(g14)
    c: Block(g14)
    c: Coincident(g15,g14)
    c: Coincident(g15,g3)
    c: Vertical(g15)
    c: Coincident(g16,g14)
    c: Coincident(g16,g13)
    c: Vertical(g16)
    c: Tangent(g16,g1)
    c: Distance(g14) = 3.5
FEATURE [Sketcher::SketchObject] Sketch016
  FullyConstrained = true
  sketch-geometry (16):
    g0: Circle CenterX=-3.5 CenterY=23.5 CenterZ=0 NormalX=0 NormalY=0 NormalZ=1 AngleXU=0 Radius=1
    g1: Circle CenterX=-1 CenterY=15.25 CenterZ=0 NormalX=0 NormalY=0 NormalZ=1 AngleXU=0 Radius=1
    g2: Circle CenterX=-3.5 CenterY=7 CenterZ=0 NormalX=0 NormalY=0 NormalZ=1 AngleXU=0 Radius=1
    g3: BSplineCurve PolesCount=3 KnotsCount=2 Degree=2 IsPeriodic=0
    g4: GeomPoint X=-3.5 Y=23.5 Z=0
    g5: GeomPoint X=-3.5 Y=7 Z=0
    g6: LineSegment StartX=-3.5 StartY=28.2 StartZ=0 EndX=-3.5 EndY=23.5 EndZ=0
    g7: LineSegment StartX=0 StartY=29.5 StartZ=0 EndX=0 EndY=30 EndZ=0
    g8: LineSegment StartX=-3.5 StartY=28.2 StartZ=0 EndX=-3.5 EndY=30 EndZ=0
    g9: LineSegment StartX=0 StartY=30 StartZ=0 EndX=0 EndY=30.5 EndZ=0
    g10: LineSegment StartX=0 StartY=30.5 StartZ=0 EndX=-3.5 EndY=30.5 EndZ=0
    g11: LineSegment StartX=-3.5 StartY=30.5 StartZ=0 EndX=-3.5 EndY=30 EndZ=0
    g12: LineSegment StartX=0 StartY=29.5 StartZ=0 EndX=0 EndY=5 EndZ=0
    g13: LineSegment StartX=-3.5 StartY=0.3 StartZ=0 EndX=-3.5 EndY=7 EndZ=0
    g14: LineSegment StartX=-3.5 StartY=0.3 StartZ=0 EndX=0 EndY=0.3 EndZ=0
    g15: LineSegment StartX=0 StartY=5 StartZ=0 EndX=0 EndY=0.3 EndZ=0
  constraints (39):
    c: Weight(g0) = 1
    c: Equal(g0,g1)
    c: Equal(g0,g2)
    c: InternalAlignment(g0,g3)
    c: InternalAlignment(g1,g3)
    c: InternalAlignment(g2,g3)
    c: InternalAlignment(g4,g3)
    c: InternalAlignment(g5,g3)
    c: Block(g3)
    c: Coincident(g6,g3)
    c: Vertical(g6)
    c: Vertical(g7)
    c: Distance(g7) = 0.5
    c: Coincident(g8,g6)
    c: Vertical(g8)
    c: Block(g6)
    c: Block(g7)
    c: Vertical(g9)
    c: Equal(g7,g9) = 0.5
    c: Block(g9)
    c: Coincident(g9,g7)
    c: Horizontal(g10)
    c: Coincident(g10,g9)
    c: Coincident(g11,g10)
    c: Coincident(g11,g8)
    c: Vertical(g11)
    c: Block(g11)
    c: Coincident(g12,g7)
    c: Vertical(g12)
    c: Coincident(g13,g3)
    c: Vertical(g13)
    c: Distance(g13) = 6.7
    c: Coincident(g14,g13)
    c: Horizontal(g14)
    c: Block(g14)
    c: Coincident(g15,g12)
    c: Coincident(g15,g14)
    c: Vertical(g15)
    c: Block(g15)
FEATURE [Sketcher::SketchObject] Sketch017
  FullyConstrained = true
  sketch-geometry (11):
    g0: LineSegment StartX=-3.5 StartY=1e-16 StartZ=0 EndX=-1.6 EndY=1e-16 EndZ=0
    g1: LineSegment StartX=-1.6 StartY=1e-16 StartZ=0 EndX=-1.6 EndY=1.5 EndZ=0
    g2: LineSegment StartX=-3.5 StartY=1.5 StartZ=0 EndX=-1.6 EndY=1.5 EndZ=0
    g3: LineSegment StartX=-3.5 StartY=1e-16 StartZ=0 EndX=-4.8 EndY=1e-16 EndZ=0
    g4: Circle CenterX=-3.5 CenterY=1.3 CenterZ=0 NormalX=0 NormalY=0 NormalZ=1 AngleXU=0 Radius=1
    g5: Circle CenterX=-3.5 CenterY=1e-16 CenterZ=0 NormalX=0 NormalY=0 NormalZ=1 AngleXU=0 Radius=1
    g6: Circle CenterX=-4.8 CenterY=1e-16 CenterZ=0 NormalX=0 NormalY=0 NormalZ=1 AngleXU=0 Radius=1
    g7: BSplineCurve PolesCount=3 KnotsCount=2 Degree=2 IsPeriodic=0
    g8: GeomPoint X=-3.5 Y=1.3 Z=0
    g9: GeomPoint X=-4.8 Y=1e-16 Z=0
    g10: LineSegment StartX=-3.5 StartY=1.3 StartZ=0 EndX=-3.5 EndY=1.5 EndZ=0
  constraints (24):
    c: Horizontal(g0)
    c: Distance(g0) = 1.9
    c: Block(g0)
    c: Coincident(g1,g0)
    c: Vertical(g1)
    c: Coincident(g2,g1)
    c: Horizontal(g2)
    c: Coincident(g3,g0)
    c: Horizontal(g3)
    c: Distance(g3) = 1.3
    c: Weight(g4) = 1
    c: Equal(g4,g5)
    c: Coincident(g5,g0)
    c: Equal(g4,g6)
    c: Coincident(g7,g3)
    c: InternalAlignment(g4,g7)
    c: InternalAlignment(g5,g7)
    c: InternalAlignment(g6,g7)
    c: InternalAlignment(g8,g7)
    c: InternalAlignment(g9,g7)
    c: Coincident(g10,g7)
    c: Coincident(g10,g2)
    c: Vertical(g10)
    c: Block(g10)
FEATURE [Part::Feature] Face035
  shape: bbox 3.2 x 1.5 x 2e-07 mm, 1 faces, 0 solids (baked)
FEATURE [Part::Revolution] Revolve039  label="backCaseScrewRetainer"
  Angle = 360
  Axis = (0,1,0)
  Base = (0,0,0)
  FaceMakerClass = Part::FaceMakerBullseye
  Placement = pos=(12.5,3,62) rot=(0,0,1;0rad)
  Solid = false
  Source = -> Face035
  Symmetric = false
FEATURE [Part::Feature] Face036
  shape: bbox 3.2 x 1.5 x 2e-07 mm, 1 faces, 0 solids (baked)
FEATURE [Part::Feature] Face039
  shape: bbox 4.8 x 30.2 x 2e-07 mm, 1 faces, 0 solids (baked)
FEATURE [Part::Revolution] Revolve043  label="frontCaseScrewPost002"
  Angle = 360
  Axis = (0,1,0)
  Base = (0,0,0)
  FaceMakerClass = Part::FaceMakerBullseye
  Placement = pos=(89.5,4.5,3.5) rot=(0,0,1;0rad)
  Solid = false
  Source = -> Face039
  Symmetric = false
FEATURE [Part::Feature] Face042
  shape: bbox 4.8 x 30.2 x 2e-07 mm, 1 faces, 0 solids (baked)
FEATURE [Part::Revolution] Revolve046  label="frontCaseScrewPost003"
  Angle = 360
  Axis = (0,1,0)
  Base = (0,0,0)
  FaceMakerClass = Part::FaceMakerBullseye
  Placement = pos=(89.5,4.5,68.5) rot=(0,0,1;0rad)
  Solid = false
  Source = -> Face042
  Symmetric = false
FEATURE [Part::Feature] Face043
  shape: bbox 3.2 x 1.5 x 2e-07 mm, 1 faces, 0 solids (baked)
FEATURE [Part::Revolution] Revolve047  label="frontCaseScrewRetainer002"
  Angle = 360
  Axis = (0,1,0)
  Base = (0,0,0)
  FaceMakerClass = Part::FaceMakerBullseye
  Placement = pos=(89.5,3,68.5) rot=(0,0,1;0rad)
  Solid = false
  Source = -> Face043
  Symmetric = false
FEATURE [Part::Feature] Face044
  shape: bbox 3.2 x 1.5 x 2e-07 mm, 1 faces, 0 solids (baked)
FEATURE [Part::Revolution] Revolve048  label="frontCaseScrewRetainer003"
  Angle = 360
  Axis = (0,1,0)
  Base = (0,0,0)
  FaceMakerClass = Part::FaceMakerBullseye
  Placement = pos=(89.5,3,3.5) rot=(0,0,1;0rad)
  Solid = false
  Source = -> Face044
  Symmetric = false
FEATURE [App::MeasureDistance] Distance002  label="Distance: 1.67 mm"
  Distance = 1.66921
  P1 = (99.2361,4.7524,71.7)
  P2 = (99.2347,6.42161,71.7)
FEATURE [Sketcher::SketchObject] Sketch018
  FullyConstrained = true
  sketch-geometry (7):
    g0: LineSegment StartX=0 StartY=0 StartZ=0 EndX=0 EndY=6 EndZ=0
    g1: Circle CenterX=0 CenterY=0 CenterZ=0 NormalX=0 NormalY=0 NormalZ=1 AngleXU=0 Radius=1
    g2: Circle CenterX=8 CenterY=6 CenterZ=0 NormalX=0 NormalY=0 NormalZ=1 AngleXU=0 Radius=1
    g3: BSplineCurve PolesCount=3 KnotsCount=2 Degree=2 IsPeriodic=0
    g4: GeomPoint X=0 Y=0 Z=0
    g5: GeomPoint X=8 Y=6 Z=0
    g6: LineSegment StartX=0 StartY=6 StartZ=0 EndX=8 EndY=6 EndZ=0
  constraints (14):
    c: Coincident(g0,g-1)
    c: Distance(g0) = 6
    c: Vertical(g0)
    c: Coincident(g3,g0)
    c: Weight(g1) = 1
    c: Equal(g1,g2)
    c: InternalAlignment(g1,g3)
    c: InternalAlignment(g2,g3)
    c: InternalAlignment(g4,g3)
    c: InternalAlignment(g5,g3)
    c: Block(g3)
    c: Coincident(g6,g0)
    c: Coincident(g6,g3)
    c: Horizontal(g6)
FEATURE [Part::Extrusion] Extrude012  label="caseScrewPillarBracket"
  Base = -> Sketch018
  Dir = (0,0,1)
  DirMode = 2
  FaceMakerClass = Part::FaceMakerBullseye
  LengthFwd = 2.4
  LengthRev = 0
  Placement = pos=(15.76,29,8.8) rot=(0,1,0;0rad)
  Solid = true
  Symmetric = false
FEATURE [Sketcher::SketchObject] Sketch019
  FullyConstrained = true
  sketch-geometry (7):
    g0: LineSegment StartX=0 StartY=0 StartZ=0 EndX=0 EndY=6 EndZ=0
    g1: Circle CenterX=0 CenterY=0 CenterZ=0 NormalX=0 NormalY=0 NormalZ=1 AngleXU=0 Radius=1
    g2: Circle CenterX=8 CenterY=6 CenterZ=0 NormalX=0 NormalY=0 NormalZ=1 AngleXU=0 Radius=1
    g3: BSplineCurve PolesCount=3 KnotsCount=2 Degree=2 IsPeriodic=0
    g4: GeomPoint X=0 Y=0 Z=0
    g5: GeomPoint X=8 Y=6 Z=0
    g6: LineSegment StartX=0 StartY=6 StartZ=0 EndX=8 EndY=6 EndZ=0
  constraints (14):
    c: Coincident(g0,g-1)
    c: Distance(g0) = 6
    c: Vertical(g0)
    c: Coincident(g3,g0)
    c: Weight(g1) = 1
    c: Equal(g1,g2)
    c: InternalAlignment(g1,g3)
    c: InternalAlignment(g2,g3)
    c: InternalAlignment(g4,g3)
    c: InternalAlignment(g5,g3)
    c: Block(g3)
    c: Coincident(g6,g0)
    c: Coincident(g6,g3)
    c: Horizontal(g6)
FEATURE [Part::Extrusion] Extrude013  label="caseScrewPillarBracket001"
  Base = -> Sketch019
  Dir = (0,0,1)
  DirMode = 2
  FaceMakerClass = Part::FaceMakerBullseye
  LengthFwd = 2.4
  LengthRev = 0
  Placement = pos=(15.76,29,60.8) rot=(0,0,1;0rad)
  Solid = true
  Symmetric = false
FEATURE [Sketcher::SketchObject] Sketch020
  FullyConstrained = true
  sketch-geometry (7):
    g0: LineSegment StartX=0 StartY=0 StartZ=0 EndX=0 EndY=6 EndZ=0
    g1: Circle CenterX=0 CenterY=0 CenterZ=0 NormalX=0 NormalY=0 NormalZ=1 AngleXU=0 Radius=1
    g2: Circle CenterX=8 CenterY=6 CenterZ=0 NormalX=0 NormalY=0 NormalZ=1 AngleXU=0 Radius=1
    g3: BSplineCurve PolesCount=3 KnotsCount=2 Degree=2 IsPeriodic=0
    g4: GeomPoint X=0 Y=0 Z=0
    g5: GeomPoint X=8 Y=6 Z=0
    g6: LineSegment StartX=0 StartY=6 StartZ=0 EndX=8 EndY=6 EndZ=0
  constraints (14):
    c: Coincident(g0,g-1)
    c: Distance(g0) = 6
    c: Vertical(g0)
    c: Coincident(g3,g0)
    c: Weight(g1) = 1
    c: Equal(g1,g2)
    c: InternalAlignment(g1,g3)
    c: InternalAlignment(g2,g3)
    c: InternalAlignment(g4,g3)
    c: InternalAlignment(g5,g3)
    c: Block(g3)
    c: Coincident(g6,g0)
    c: Coincident(g6,g3)
    c: Horizontal(g6)
FEATURE [Part::Extrusion] Extrude014  label="caseScrewPillarBracket002"
  Base = -> Sketch020
  Dir = (0,0,1)
  DirMode = 2
  FaceMakerClass = Part::FaceMakerBullseye
  LengthFwd = 2.4
  LengthRev = 0
  Placement = pos=(13.7,29,13.26) rot=(0,-1,0;1.5708rad)
  Solid = true
  Symmetric = false
FEATURE [Sketcher::SketchObject] Sketch021
  FullyConstrained = true
  sketch-geometry (7):
    g0: LineSegment StartX=0 StartY=0 StartZ=0 EndX=0 EndY=6 EndZ=0
    g1: Circle CenterX=0 CenterY=0 CenterZ=0 NormalX=0 NormalY=0 NormalZ=1 AngleXU=0 Radius=1
    g2: Circle CenterX=8 CenterY=6 CenterZ=0 NormalX=0 NormalY=0 NormalZ=1 AngleXU=0 Radius=1
    g3: BSplineCurve PolesCount=3 KnotsCount=2 Degree=2 IsPeriodic=0
    g4: GeomPoint X=0 Y=0 Z=0
    g5: GeomPoint X=8 Y=6 Z=0
    g6: LineSegment StartX=0 StartY=6 StartZ=0 EndX=8 EndY=6 EndZ=0
  constraints (14):
    c: Coincident(g0,g-1)
    c: Distance(g0) = 6
    c: Vertical(g0)
    c: Coincident(g3,g0)
    c: Weight(g1) = 1
    c: Equal(g1,g2)
    c: InternalAlignment(g1,g3)
    c: InternalAlignment(g2,g3)
    c: InternalAlignment(g4,g3)
    c: InternalAlignment(g5,g3)
    c: Block(g3)
    c: Coincident(g6,g0)
    c: Coincident(g6,g3)
    c: Horizontal(g6)
FEATURE [Part::Extrusion] Extrude015  label="caseScrewPillarBracket003"
  Base = -> Sketch021
  Dir = (0,0,1)
  DirMode = 2
  FaceMakerClass = Part::FaceMakerBullseye
  LengthFwd = 2.4
  LengthRev = 0
  Placement = pos=(11.3,29,58.74) rot=(0,1,0;1.5708rad)
  Solid = true
  Symmetric = false
FEATURE [Sketcher::SketchObject] Sketch022
  FullyConstrained = true
  sketch-geometry (7):
    g0: LineSegment StartX=0 StartY=0 StartZ=0 EndX=0 EndY=6 EndZ=0
    g1: Circle CenterX=0 CenterY=0 CenterZ=0 NormalX=0 NormalY=0 NormalZ=1 AngleXU=0 Radius=1
    g2: Circle CenterX=8 CenterY=6 CenterZ=0 NormalX=0 NormalY=0 NormalZ=1 AngleXU=0 Radius=1
    g3: BSplineCurve PolesCount=3 KnotsCount=2 Degree=2 IsPeriodic=0
    g4: GeomPoint X=0 Y=0 Z=0
    g5: GeomPoint X=8 Y=6 Z=0
    g6: LineSegment StartX=0 StartY=6 StartZ=0 EndX=8 EndY=6 EndZ=0
  constraints (14):
    c: Coincident(g0,g-1)
    c: Distance(g0) = 6
    c: Vertical(g0)
    c: Coincident(g3,g0)
    c: Weight(g1) = 1
    c: Equal(g1,g2)
    c: InternalAlignment(g1,g3)
    c: InternalAlignment(g2,g3)
    c: InternalAlignment(g4,g3)
    c: InternalAlignment(g5,g3)
    c: Block(g3)
    c: Coincident(g6,g0)
    c: Coincident(g6,g3)
    c: Horizontal(g6)
FEATURE [Part::Extrusion] Extrude016  label="caseScrewPillarBracket004"
  Base = -> Sketch022
  Dir = (0,0,1)
  DirMode = 2
  FaceMakerClass = Part::FaceMakerBullseye
  LengthFwd = 2.4
  LengthRev = 0
  Placement = pos=(88.3,29,65.23) rot=(0,1,0;1.5708rad)
  Solid = true
  Symmetric = false
FEATURE [Sketcher::SketchObject] Sketch023
  FullyConstrained = true
  sketch-geometry (7):
    g0: LineSegment StartX=0 StartY=0 StartZ=0 EndX=0 EndY=6 EndZ=0
    g1: Circle CenterX=0 CenterY=0 CenterZ=0 NormalX=0 NormalY=0 NormalZ=1 AngleXU=0 Radius=1
    g2: Circle CenterX=8 CenterY=6 CenterZ=0 NormalX=0 NormalY=0 NormalZ=1 AngleXU=0 Radius=1
    g3: BSplineCurve PolesCount=3 KnotsCount=2 Degree=2 IsPeriodic=0
    g4: GeomPoint X=0 Y=0 Z=0
    g5: GeomPoint X=8 Y=6 Z=0
    g6: LineSegment StartX=0 StartY=6 StartZ=0 EndX=8 EndY=6 EndZ=0
  constraints (14):
    c: Coincident(g0,g-1)
    c: Distance(g0) = 6
    c: Vertical(g0)
    c: Coincident(g3,g0)
    c: Weight(g1) = 1
    c: Equal(g1,g2)
    c: InternalAlignment(g1,g3)
    c: InternalAlignment(g2,g3)
    c: InternalAlignment(g4,g3)
    c: InternalAlignment(g5,g3)
    c: Block(g3)
    c: Coincident(g6,g0)
    c: Coincident(g6,g3)
    c: Horizontal(g6)
FEATURE [Part::Extrusion] Extrude017  label="caseScrewPillarBracket005"
  Base = -> Sketch023
  Dir = (0,0,1)
  DirMode = 2
  FaceMakerClass = Part::FaceMakerBullseye
  LengthFwd = 2.4
  LengthRev = 0
  Placement = pos=(90.7,29,6.77) rot=(0,-1,0;1.5708rad)
  Solid = true
  Symmetric = false
FEATURE [Sketcher::SketchObject] Sketch024
  FullyConstrained = true
  sketch-geometry (7):
    g0: LineSegment StartX=0 StartY=0 StartZ=0 EndX=0 EndY=6 EndZ=0
    g1: Circle CenterX=0 CenterY=0 CenterZ=0 NormalX=0 NormalY=0 NormalZ=1 AngleXU=0 Radius=1
    g2: Circle CenterX=8 CenterY=6 CenterZ=0 NormalX=0 NormalY=0 NormalZ=1 AngleXU=0 Radius=1
    g3: BSplineCurve PolesCount=3 KnotsCount=2 Degree=2 IsPeriodic=0
    g4: GeomPoint X=0 Y=0 Z=0
    g5: GeomPoint X=8 Y=6 Z=0
    g6: LineSegment StartX=0 StartY=6 StartZ=0 EndX=8 EndY=6 EndZ=0
  constraints (14):
    c: Coincident(g0,g-1)
    c: Distance(g0) = 6
    c: Vertical(g0)
    c: Coincident(g3,g0)
    c: Weight(g1) = 1
    c: Equal(g1,g2)
    c: InternalAlignment(g1,g3)
    c: InternalAlignment(g2,g3)
    c: InternalAlignment(g4,g3)
    c: InternalAlignment(g5,g3)
    c: Block(g3)
    c: Coincident(g6,g0)
    c: Coincident(g6,g3)
    c: Horizontal(g6)
FEATURE [Part::Extrusion] Extrude018  label="caseScrewPillarBracket006"
  Base = -> Sketch024
  Dir = (0,0,1)
  DirMode = 2
  FaceMakerClass = Part::FaceMakerBullseye
  LengthFwd = 2.4
  LengthRev = 0
  Placement = pos=(103.7,29,6.77) rot=(0,-1,0;1.5708rad)
  Solid = true
  Symmetric = false
FEATURE [Sketcher::SketchObject] Sketch025
  FullyConstrained = true
  sketch-geometry (7):
    g0: LineSegment StartX=0 StartY=0 StartZ=0 EndX=0 EndY=6 EndZ=0
    g1: Circle CenterX=0 CenterY=0 CenterZ=0 NormalX=0 NormalY=0 NormalZ=1 AngleXU=0 Radius=1
    g2: Circle CenterX=8 CenterY=6 CenterZ=0 NormalX=0 NormalY=0 NormalZ=1 AngleXU=0 Radius=1
    g3: BSplineCurve PolesCount=3 KnotsCount=2 Degree=2 IsPeriodic=0
    g4: GeomPoint X=0 Y=0 Z=0
    g5: GeomPoint X=8 Y=6 Z=0
    g6: LineSegment StartX=0 StartY=6 StartZ=0 EndX=8 EndY=6 EndZ=0
  constraints (14):
    c: Coincident(g0,g-1)
    c: Distance(g0) = 6
    c: Vertical(g0)
    c: Coincident(g3,g0)
    c: Weight(g1) = 1
    c: Equal(g1,g2)
    c: InternalAlignment(g1,g3)
    c: InternalAlignment(g2,g3)
    c: InternalAlignment(g4,g3)
    c: InternalAlignment(g5,g3)
    c: Block(g3)
    c: Coincident(g6,g0)
    c: Coincident(g6,g3)
    c: Horizontal(g6)
FEATURE [Part::Extrusion] Extrude019  label="caseScrewPillarBracket007"
  Base = -> Sketch025
  Dir = (0,0,1)
  DirMode = 2
  FaceMakerClass = Part::FaceMakerBullseye
  LengthFwd = 2.4
  LengthRev = 0
  Placement = pos=(101.3,29,65.23) rot=(0,1,0;1.5708rad)
  Solid = true
  Symmetric = false
FEATURE [Part::Box] Box011  label="frontCaseScrewPillarBracket"
  AttacherType = Attacher::AttachEngine3D
  Height = 2.4
  Length = 16
  Placement = pos=(87,28,2.3) rot=(0,0,1;0rad)
  Width = 7
FEATURE [Part::Box] Box012  label="frontCaseScrewPillarBracket001"
  AttacherType = Attacher::AttachEngine3D
  Height = 2.4
  Length = 16
  Placement = pos=(87,28,67.3) rot=(0,0,1;0rad)
  Width = 7
FEATURE [Sketcher::SketchObject] Sketch026
  FullyConstrained = true
  sketch-geometry (17):
    g0: Circle CenterX=-3.5 CenterY=23.5 CenterZ=0 NormalX=0 NormalY=0 NormalZ=1 AngleXU=0 Radius=1
    g1: Circle CenterX=-1 CenterY=15.25 CenterZ=0 NormalX=0 NormalY=0 NormalZ=1 AngleXU=0 Radius=1
    g2: Circle CenterX=-3.5 CenterY=7 CenterZ=0 NormalX=0 NormalY=0 NormalZ=1 AngleXU=0 Radius=1
    g3: BSplineCurve PolesCount=3 KnotsCount=2 Degree=2 IsPeriodic=0
    g4: GeomPoint X=-3.5 Y=23.5 Z=0
    g5: GeomPoint X=-3.5 Y=7 Z=0
    g6: Circle CenterX=-4.8 CenterY=30.5 CenterZ=0 NormalX=0 NormalY=0 NormalZ=1 AngleXU=0 Radius=1
    g7: Circle CenterX=-3.5 CenterY=30.5 CenterZ=0 NormalX=0 NormalY=0 NormalZ=1 AngleXU=0 Radius=1
    g8: Circle CenterX=-3.5 CenterY=29.2 CenterZ=0 NormalX=0 NormalY=0 NormalZ=1 AngleXU=0 Radius=1
    g9: BSplineCurve PolesCount=3 KnotsCount=2 Degree=2 IsPeriodic=0
    g10: GeomPoint X=-4.8 Y=30.5 Z=0
    g11: GeomPoint X=-3.5 Y=29.2 Z=0
    g12: LineSegment StartX=-3.5 StartY=29.2 StartZ=0 EndX=-3.5 EndY=23.5 EndZ=0
    g13: LineSegment StartX=-4.8 StartY=30.5 StartZ=0 EndX=0 EndY=30.5 EndZ=0
    g14: LineSegment StartX=-3.5 StartY=5 StartZ=0 EndX=-3.5 EndY=7 EndZ=0
    g15: LineSegment StartX=0 StartY=5 StartZ=0 EndX=0 EndY=30.5 EndZ=0
    g16: LineSegment StartX=-3.5 StartY=5 StartZ=0 EndX=0 EndY=5 EndZ=0
  constraints (33):
    c: Weight(g0) = 1
    c: Equal(g0,g1)
    c: Equal(g0,g2)
    c: InternalAlignment(g0,g3)
    c: InternalAlignment(g1,g3)
    c: InternalAlignment(g2,g3)
    c: InternalAlignment(g4,g3)
    c: InternalAlignment(g5,g3)
    c: Block(g3)
    c: Weight(g6) = 1
    c: Equal(g6,g7)
    c: Equal(g6,g8)
    c: InternalAlignment(g6,g9)
    c: InternalAlignment(g7,g9)
    c: InternalAlignment(g8,g9)
    c: InternalAlignment(g10,g9)
    c: InternalAlignment(g11,g9)
    c: Block(g9)
    c: Coincident(g12,g9)
    c: Coincident(g12,g3)
    c: Vertical(g12)
    c: Coincident(g13,g9)
    c: Horizontal(g13)
    c: Distance(g13) = 4.8
    c: Coincident(g14,g3)
    c: Vertical(g14)
    c: Coincident(g15,g13)
    c: Vertical(g15)
    c: Tangent(g15,g1)
    c: Distance(g14) = 2
    c: Coincident(g16,g14)
    c: Horizontal(g16)
    c: Coincident(g15,g16)
FEATURE [Part::Feature] Face050
  shape: bbox 4.8 x 25.5 x 2e-07 mm, 1 faces, 0 solids (baked)
FEATURE [Part::Revolution] Revolve054  label="moreFrontCaseScrewPost001"
  Angle = 360
  Axis = (0,1,0)
  Base = (0,0,0)
  FaceMakerClass = Part::FaceMakerBullseye
  Placement = pos=(102.5,4.5,3.5) rot=(0,0,1;0rad)
  Solid = false
  Source = -> Face050
  Symmetric = false
FEATURE [Part::Feature] Face051
  shape: bbox 4.8 x 25.5 x 2e-07 mm, 1 faces, 0 solids (baked)
FEATURE [Part::Revolution] Revolve055  label="moreFrontCaseScrewPost002"
  Angle = 360
  Axis = (0,1,0)
  Base = (0,0,0)
  FaceMakerClass = Part::FaceMakerBullseye
  Placement = pos=(102.5,4.5,68.5) rot=(0,0,1;0rad)
  Solid = false
  Source = -> Face051
  Symmetric = false
FEATURE [Sketcher::SketchObject] Sketch027
  FullyConstrained = true
  sketch-geometry (10):
    g0: LineSegment StartX=-1.6 StartY=4.7 StartZ=0 EndX=-1.6 EndY=1.7 EndZ=0
    g1: LineSegment StartX=-3.5 StartY=4.7 StartZ=0 EndX=-1.6 EndY=4.7 EndZ=0
    g2: LineSegment StartX=-1.6 StartY=1.7 StartZ=0 EndX=-1.6 EndY=1.5 EndZ=0
    g3: LineSegment StartX=-1.6 StartY=1.5 StartZ=0 EndX=-5.2 EndY=1.5 EndZ=0
    g4: Circle CenterX=-3.5 CenterY=4.7 CenterZ=0 NormalX=0 NormalY=0 NormalZ=1 AngleXU=0 Radius=1
    g5: Circle CenterX=-3.59627 CenterY=2.99743 CenterZ=0 NormalX=0 NormalY=0 NormalZ=1 AngleXU=0 Radius=1
    g6: Circle CenterX=-5.2 CenterY=1.5 CenterZ=0 NormalX=0 NormalY=0 NormalZ=1 AngleXU=0 Radius=1
    g7: BSplineCurve PolesCount=3 KnotsCount=2 Degree=2 IsPeriodic=0
    g8: GeomPoint X=-3.5 Y=4.7 Z=0
    g9: GeomPoint X=-5.2 Y=1.5 Z=0
  constraints (23):
    c: Vertical(g0)
    c: Distance(g0) = 3
    c: Coincident(g1,g0)
    c: Horizontal(g1)
    c: Block(g0)
    c: Block(g1)
    c: Coincident(g2,g0)
    c: Vertical(g2)
    c: Distance(g2) = 0.2
    c: Coincident(g3,g2)
    c: Horizontal(g3)
    c: Block(g3)
    c: Coincident(g7,g1)
    c: Weight(g4) = 1
    c: Equal(g4,g5)
    c: Equal(g4,g6)
    c: Coincident(g7,g3)
    c: InternalAlignment(g4,g7)
    c: InternalAlignment(g5,g7)
    c: InternalAlignment(g6,g7)
    c: InternalAlignment(g8,g7)
    c: InternalAlignment(g9,g7)
    c: Block(g7)
FEATURE [Sketcher::SketchObject] Sketch028
  FullyConstrained = true
  sketch-geometry (18):
    g0: LineSegment StartX=0 StartY=3e-16 StartZ=0 EndX=0 EndY=1.7 EndZ=0
    g1: LineSegment StartX=-3.5 StartY=0 StartZ=0 EndX=-3.5 EndY=0.9 EndZ=0
    g2: Circle CenterX=-2.7 CenterY=1.7 CenterZ=0 NormalX=0 NormalY=0 NormalZ=1 AngleXU=0 Radius=1
    g3: Circle CenterX=-3.5 CenterY=1.7 CenterZ=0 NormalX=0 NormalY=0 NormalZ=1 AngleXU=0 Radius=1
    g4: Circle CenterX=-3.5 CenterY=0.9 CenterZ=0 NormalX=0 NormalY=0 NormalZ=1 AngleXU=0 Radius=1
    g5: BSplineCurve PolesCount=3 KnotsCount=2 Degree=2 IsPeriodic=0
    g6: GeomPoint X=-2.7 Y=1.7 Z=0
    g7: GeomPoint X=-3.5 Y=0.9 Z=0
    g8: LineSegment StartX=-3.5 StartY=0 StartZ=0 EndX=-3.5 EndY=-7 EndZ=0
    g9: LineSegment StartX=0 StartY=3e-16 StartZ=0 EndX=0 EndY=-7 EndZ=0
    g10: LineSegment StartX=-3.5 StartY=-7 StartZ=0 EndX=0 EndY=-7 EndZ=0
    g11: LineSegment StartX=-2.7 StartY=1.7 StartZ=0 EndX=-1.6 EndY=1.7 EndZ=0
    g12: LineSegment StartX=0 StartY=1.7 StartZ=0 EndX=0 EndY=4.5 EndZ=0
    g13: LineSegment StartX=0 StartY=4.5 StartZ=0 EndX=0 EndY=10.8 EndZ=0
    g14: LineSegment StartX=0 StartY=10.8 StartZ=0 EndX=-2 EndY=10.8 EndZ=0
    g15: LineSegment StartX=-1.6 StartY=4.7 StartZ=0 EndX=-1.6 EndY=1.7 EndZ=0
    g16: LineSegment StartX=-1.6 StartY=4.7 StartZ=0 EndX=-2 EndY=4.7 EndZ=0
    g17: LineSegment StartX=-2 StartY=4.7 StartZ=0 EndX=-2 EndY=10.8 EndZ=0
  constraints (44):
    c: Vertical(g0)
    c: Vertical(g1)
    c: Distance(g1) = 0.9
    c: Block(g0)
    c: Distance(g0) = 1.7
    c: Weight(g2) = 1
    c: Equal(g2,g3)
    c: Equal(g2,g4)
    c: Coincident(g5,g1)
    c: InternalAlignment(g2,g5)
    c: InternalAlignment(g3,g5)
    c: InternalAlignment(g4,g5)
    c: InternalAlignment(g6,g5)
    c: InternalAlignment(g7,g5)
    c: Block(g5)
    c: Coincident(g8,g1)
    c: Vertical(g8)
    c: Distance(g8) = 7
    c: Vertical(g9)
    c: Equal(g8,g9) = 7
    c: Coincident(g9,g0)
    c: Coincident(g10,g8)
    c: Coincident(g10,g9)
    c: Horizontal(g10)
    c: Coincident(g11,g5)
    c: Horizontal(g11)
    c: Coincident(g12,g0)
    c: Vertical(g12)
    c: Distance(g12) = 2.8
    c: Coincident(g13,g12)
    c: Vertical(g13)
    c: Distance(g13) = 6.3
    c: Coincident(g14,g13)
    c: Horizontal(g14)
    c: Distance(g14) = 2
    c: Vertical(g15)
    c: Distance(g15) = 3
    c: Block(g11)
    c: Coincident(g15,g11)
    c: Coincident(g16,g15)
    c: Horizontal(g16)
    c: Coincident(g17,g16)
    c: Coincident(g17,g14)
    c: Vertical(g17)
FEATURE [Part::Revolution] Revolve040  label="backCaseScrewRetainer001"
  Angle = 360
  Axis = (0,1,0)
  Base = (0,0,0)
  FaceMakerClass = Part::FaceMakerBullseye
  Placement = pos=(12.5,3,10) rot=(0,0,1;0rad)
  Solid = false
  Source = -> Face036
  Symmetric = false
FEATURE [Part::Feature] Face055
  shape: bbox 3.5 x 30.2 x 2e-07 mm, 1 faces, 0 solids (baked)
FEATURE [Part::Revolution] Revolve059  label="backCaseScrewPost"
  Angle = 360
  Axis = (0,1,0)
  Base = (0,0,0)
  FaceMakerClass = Part::FaceMakerBullseye
  Placement = pos=(12.5,4.5,10) rot=(0,0,1;0rad)
  Solid = false
  Source = -> Face055
  Symmetric = false
FEATURE [Part::Feature] Face056
  shape: bbox 3.5 x 30.2 x 2e-07 mm, 1 faces, 0 solids (baked)
FEATURE [Part::Revolution] Revolve060  label="backCaseScrewPost001"
  Angle = 360
  Axis = (0,1,0)
  Base = (0,0,0)
  FaceMakerClass = Part::FaceMakerBullseye
  Placement = pos=(12.5,4.5,62) rot=(0,0,1;0rad)
  Solid = false
  Source = -> Face056
  Symmetric = false
FEATURE [Part::Feature] Face057
  shape: bbox 3.5 x 17.8 x 2e-07 mm, 1 faces, 0 solids (baked)
FEATURE [Part::Revolution] Revolve061  label="removeToCreateScrewAndThreadedInsertHole"
  Angle = 360
  Axis = (0,1,0)
  Base = (0,0,0)
  FaceMakerClass = Part::FaceMakerBullseye
  Placement = pos=(12.5,0,10) rot=(0,0,1;0rad)
  Solid = false
  Source = -> Face057
  Symmetric = false
FEATURE [Part::Feature] Face058
  shape: bbox 3.5 x 17.8 x 2e-07 mm, 1 faces, 0 solids (baked)
FEATURE [Part::Revolution] Revolve062  label="removeToCreateScrewAndThreadedInsertHole001"
  Angle = 360
  Axis = (0,1,0)
  Base = (0,0,0)
  FaceMakerClass = Part::FaceMakerBullseye
  Placement = pos=(12.5,0,62) rot=(0,0,1;0rad)
  Solid = false
  Source = -> Face058
  Symmetric = false
FEATURE [Part::Feature] Face059
  shape: bbox 3.5 x 17.8 x 2e-07 mm, 1 faces, 0 solids (baked)
FEATURE [Part::Revolution] Revolve063  label="removeToCreateScrewAndThreadedInsertHole002"
  Angle = 360
  Axis = (0,1,0)
  Base = (0,0,0)
  FaceMakerClass = Part::FaceMakerBullseye
  Placement = pos=(89.5,0,68.5) rot=(0,0,1;0rad)
  Solid = false
  Source = -> Face059
  Symmetric = false
FEATURE [Part::Feature] Face060
  shape: bbox 3.5 x 17.8 x 2e-07 mm, 1 faces, 0 solids (baked)
FEATURE [Part::Revolution] Revolve064  label="removeToCreateScrewAndThreadedInsertHole003"
  Angle = 360
  Axis = (0,1,0)
  Base = (0,0,0)
  FaceMakerClass = Part::FaceMakerBullseye
  Placement = pos=(89.5,0,3.5) rot=(0,0,1;0rad)
  Solid = false
  Source = -> Face060
  Symmetric = false
FEATURE [Part::Feature] Face061
  shape: bbox 3.5 x 17.8 x 2e-07 mm, 1 faces, 0 solids (baked)
FEATURE [Part::Revolution] Revolve065  label="removeToCreateScrewAndThreadedInsertHole004"
  Angle = 360
  Axis = (0,1,0)
  Base = (0,0,0)
  FaceMakerClass = Part::FaceMakerBullseye
  Placement = pos=(102.5,4.7,3.5) rot=(0,0,1;0rad)
  Solid = false
  Source = -> Face061
  Symmetric = false
FEATURE [Part::Feature] Face062
  shape: bbox 3.5 x 17.8 x 2e-07 mm, 1 faces, 0 solids (baked)
FEATURE [Part::Revolution] Revolve066  label="removeToCreateScrewAndThreadedInsertHole005"
  Angle = 360
  Axis = (0,1,0)
  Base = (0,0,0)
  FaceMakerClass = Part::FaceMakerBullseye
  Placement = pos=(102.5,4.7,68.5) rot=(0,0,1;0rad)
  Solid = false
  Source = -> Face062
  Symmetric = false
FEATURE [Part::MultiFuse] Fusion047  label="makeHoles"
  Shapes = -> [Revolve066,Revolve065,Revolve064,Revolve063,Revolve062,Revolve061]
FEATURE [Part::Feature] Face063
  shape: bbox 3.6 x 3.2 x 2e-07 mm, 1 faces, 0 solids (baked)
FEATURE [Part::Revolution] Revolve067  label="moreFrontCaseScrewRetainer002"
  Angle = 360
  Axis = (0,1,0)
  Base = (0,0,0)
  FaceMakerClass = Part::FaceMakerBullseye
  Placement = pos=(102.5,4.5,68.5) rot=(0,0,1;0rad)
  Solid = false
  Source = -> Face063
  Symmetric = false
FEATURE [Part::Feature] Face064
  shape: bbox 3.6 x 3.2 x 2e-07 mm, 1 faces, 0 solids (baked)
FEATURE [Part::Revolution] Revolve068  label="moreFrontCaseScrewRetainer003"
  Angle = 360
  Axis = (0,1,0)
  Base = (0,0,0)
  FaceMakerClass = Part::FaceMakerBullseye
  Placement = pos=(102.5,4.5,3.5) rot=(0,0,1;0rad)
  Solid = false
  Source = -> Face064
  Symmetric = false
FEATURE [Part::Feature] Face065
  shape: bbox 3.5 x 17.8 x 2e-07 mm, 1 faces, 0 solids (baked)
FEATURE [Part::Revolution] Revolve069  label="removeToCreateScrewAndThreadedInsertHole006"
  Angle = 360
  Axis = (0,1,0)
  Base = (0,0,0)
  FaceMakerClass = Part::FaceMakerBullseye
  Placement = pos=(12.5,0,10) rot=(0,0,1;0rad)
  Solid = false
  Source = -> Face065
  Symmetric = false
FEATURE [Part::Feature] Face066
  shape: bbox 3.5 x 17.8 x 2e-07 mm, 1 faces, 0 solids (baked)
FEATURE [Part::Revolution] Revolve070  label="removeToCreateScrewAndThreadedInsertHole007"
  Angle = 360
  Axis = (0,1,0)
  Base = (0,0,0)
  FaceMakerClass = Part::FaceMakerBullseye
  Placement = pos=(12.5,0,62) rot=(0,0,1;0rad)
  Solid = false
  Source = -> Face066
  Symmetric = false
FEATURE [Part::Feature] Face067
  shape: bbox 3.5 x 17.8 x 2e-07 mm, 1 faces, 0 solids (baked)
FEATURE [Part::Revolution] Revolve071  label="removeToCreateScrewAndThreadedInsertHole008"
  Angle = 360
  Axis = (0,1,0)
  Base = (0,0,0)
  FaceMakerClass = Part::FaceMakerBullseye
  Placement = pos=(89.5,0,68.5) rot=(0,0,1;0rad)
  Solid = false
  Source = -> Face067
  Symmetric = false
FEATURE [Part::Feature] Face068
  shape: bbox 3.5 x 17.8 x 2e-07 mm, 1 faces, 0 solids (baked)
FEATURE [Part::Revolution] Revolve072  label="removeToCreateScrewAndThreadedInsertHole009"
  Angle = 360
  Axis = (0,1,0)
  Base = (0,0,0)
  FaceMakerClass = Part::FaceMakerBullseye
  Placement = pos=(89.5,0,3.5) rot=(0,0,1;0rad)
  Solid = false
  Source = -> Face068
  Symmetric = false
FEATURE [Part::Feature] Face069
  shape: bbox 3.5 x 17.8 x 2e-07 mm, 1 faces, 0 solids (baked)
FEATURE [Part::Feature] Face070
  shape: bbox 3.5 x 17.8 x 2e-07 mm, 1 faces, 0 solids (baked)
FEATURE [Part::Revolution] Revolve073  label="removeToCreateScrewAndThreadedInsertHole010"
  Angle = 360
  Axis = (0,1,0)
  Base = (0,0,0)
  FaceMakerClass = Part::FaceMakerBullseye
  Placement = pos=(102.5,4.7,3.5) rot=(0,0,1;0rad)
  Solid = false
  Source = -> Face069
  Symmetric = false
FEATURE [Part::Revolution] Revolve074  label="removeToCreateScrewAndThreadedInsertHole011"
  Angle = 360
  Axis = (0,1,0)
  Base = (0,0,0)
  FaceMakerClass = Part::FaceMakerBullseye
  Placement = pos=(102.5,4.7,68.5) rot=(0,0,1;0rad)
  Solid = false
  Source = -> Face070
  Symmetric = false
FEATURE [Part::MultiFuse] Fusion048  label="makeHoles001"
  Shapes = -> [Revolve074,Revolve073,Revolve072,Revolve071,Revolve070,Revolve069]
FEATURE [Part::MultiFuse] Fusion049  label="caseScrewRetainers"
  Shapes = -> [Revolve067,Revolve068,Revolve048,Revolve047,Revolve039,Revolve040]
FEATURE [Part::Cut] Cut015  label="caseScrewRetainers001"
  Base = -> Fusion049
  Tool = -> Fusion048
FEATURE [Part::MultiFuse] Fusion050  label="casePillars"
  Shapes = -> [Revolve055,Revolve054,Revolve043,Revolve046,Revolve059,Revolve060]
FEATURE [Part::Feature] Face071 .. Face076  x6 (patterned run collapsed; names and placements below)
  shape: bbox 3.5 x 17.8 x 2e-07 mm, 1 faces, 0 solids (baked)
FEATURE [Part::Revolution] Revolve075  label="removeToCreateScrewAndThreadedInsertHole012"
  Angle = 360
  Axis = (0,1,0)
  Base = (0,0,0)
  FaceMakerClass = Part::FaceMakerBullseye
  Placement = pos=(12.5,0,10) rot=(0,0,1;0rad)
  Solid = false
  Source = -> Face071
  Symmetric = false
FEATURE [Part::Revolution] Revolve076  label="removeToCreateScrewAndThreadedInsertHole013"
  Angle = 360
  Axis = (0,1,0)
  Base = (0,0,0)
  FaceMakerClass = Part::FaceMakerBullseye
  Placement = pos=(12.5,0,62) rot=(0,0,1;0rad)
  Solid = false
  Source = -> Face072
  Symmetric = false
FEATURE [Part::Revolution] Revolve077  label="removeToCreateScrewAndThreadedInsertHole014"
  Angle = 360
  Axis = (0,1,0)
  Base = (0,0,0)
  FaceMakerClass = Part::FaceMakerBullseye
  Placement = pos=(89.5,0,68.5) rot=(0,0,1;0rad)
  Solid = false
  Source = -> Face073
  Symmetric = false
FEATURE [Part::Revolution] Revolve078  label="removeToCreateScrewAndThreadedInsertHole015"
  Angle = 360
  Axis = (0,1,0)
  Base = (0,0,0)
  FaceMakerClass = Part::FaceMakerBullseye
  Placement = pos=(89.5,0,3.5) rot=(0,0,1;0rad)
  Solid = false
  Source = -> Face074
  Symmetric = false
FEATURE [Part::Revolution] Revolve079  label="removeToCreateScrewAndThreadedInsertHole016"
  Angle = 360
  Axis = (0,1,0)
  Base = (0,0,0)
  FaceMakerClass = Part::FaceMakerBullseye
  Placement = pos=(102.5,4.7,3.5) rot=(0,0,1;0rad)
  Solid = false
  Source = -> Face075
  Symmetric = false
FEATURE [Part::Revolution] Revolve080  label="removeToCreateScrewAndThreadedInsertHole017"
  Angle = 360
  Axis = (0,1,0)
  Base = (0,0,0)
  FaceMakerClass = Part::FaceMakerBullseye
  Placement = pos=(102.5,4.7,68.5) rot=(0,0,1;0rad)
  Solid = false
  Source = -> Face076
  Symmetric = false
FEATURE [Part::MultiFuse] Fusion051  label="makeHoles002"
  Shapes = -> [Revolve080,Revolve079,Revolve078,Revolve077,Revolve076,Revolve075]
FEATURE [Part::Cut] Cut016  label="caesPillars"
  Base = -> Fusion050
  Tool = -> Fusion051
FEATURE [Part::Revolution] Revolve009  label="plugHousing016"
  Angle = 360
  Axis = (0,1,0)
  Base = (0,0,0)
  FaceMakerClass = Part::FaceMakerBullseye
  Placement = pos=(0,0,36.15) rot=(0,0,1;0rad)
  Solid = false
  Source = -> Face012
  Symmetric = false
FEATURE [Part::MultiFuse] Fusion014  label="plugHousing023"
  Placement = pos=(0,0,0) rot=(0,0,1;1.5708rad)
  Shapes = -> [Revolve011,Revolve009]
FEATURE [Part::Revolution] Revolve010  label="plugHousing017"
  Angle = 360
  Axis = (0,1,0)
  Base = (0,0,0)
  FaceMakerClass = Part::FaceMakerBullseye
  Placement = pos=(0,0,36.15) rot=(0,0,1;0rad)
  Solid = false
  Source = -> Face014
  Symmetric = false
FEATURE [Part::MultiFuse] Fusion015  label="plugHousing024"
  Placement = pos=(0,0,0) rot=(0,0,1;1.5708rad)
  Shapes = -> [Revolve010,Revolve015]
FEATURE [Part::Revolution] Revolve014  label="plugHousing026"
  Angle = 360
  Axis = (0,1,0)
  Base = (0,0,0)
  FaceMakerClass = Part::FaceMakerBullseye
  Placement = pos=(0,0,36.15) rot=(0,0,1;0rad)
  Solid = false
  Source = -> Face011
  Symmetric = false
FEATURE [Part::Revolution] Revolve013  label="plugHousing025"
  Angle = 360
  Axis = (0,1,0)
  Base = (0,0,0)
  FaceMakerClass = Part::FaceMakerBullseye
  Placement = pos=(0,0,36.15) rot=(0,0,1;0rad)
  Solid = false
  Source = -> Face015
  Symmetric = false
FEATURE [Part::MultiFuse] Fusion016  label="plugHousing028"
  Placement = pos=(0,19,0) rot=(0,0,1;3.14159rad)
  Shapes = -> [Fusion014,Fusion013]
FEATURE [Part::MultiFuse] Fusion011  label="plugHousing018"
  Placement = pos=(0,0,0) rot=(0,0,1;1.5708rad)
  Shapes = -> [Revolve014,Revolve013]
FEATURE [Part::MultiFuse] Fusion012  label="plugHousing019"
  Placement = pos=(0,19,0) rot=(0,0,1;3.14159rad)
  Shapes = -> [Fusion011,Fusion015]
FEATURE [Part::MultiFuse] Fusion017  label="plugHousing029"
  Placement = pos=(122.621,0,-0.15) rot=(0,0,1;0rad)
  Shapes = -> [Fusion016,Fusion012]
FEATURE [Part::MultiFuse] Fusion052  label="casePillarRetainers"
  Shapes = -> [Extrude012,Extrude013,Extrude014,Extrude015,Extrude016,Extrude017,Extrude018,Extrude019,Box011,Box012]
FEATURE [Part::Feature] Face077
  shape: bbox 3.5 x 17.8 x 2e-07 mm, 1 faces, 0 solids (baked)
FEATURE [Part::Revolution] Revolve081  label="removeToCreateScrewAndThreadedInsertHole018"
  Angle = 360
  Axis = (0,1,0)
  Base = (0,0,0)
  FaceMakerClass = Part::FaceMakerBullseye
  Placement = pos=(62.3,30.3,19.7) rot=(0,0,1;0rad)
  Solid = false
  Source = -> Face077
  Symmetric = false
FEATURE [Part::Feature] Face078
  shape: bbox 3.5 x 17.8 x 2e-07 mm, 1 faces, 0 solids (baked)
FEATURE [Part::Revolution] Revolve082  label="removeToCreateScrewAndThreadedInsertHole019"
  Angle = 360
  Axis = (0,1,0)
  Base = (0,0,0)
  FaceMakerClass = Part::FaceMakerBullseye
  Placement = pos=(62.3,30.3,51.7) rot=(0,0,1;0rad)
  Solid = false
  Source = -> Face078
  Symmetric = false
FEATURE [Part::Feature] Face079
  shape: bbox 3.5 x 17.8 x 2e-07 mm, 1 faces, 0 solids (baked)
FEATURE [Part::Revolution] Revolve083  label="removeToCreateScrewAndThreadedInsertHole020"
  Angle = 360
  Axis = (0,1,0)
  Base = (0,0,0)
  FaceMakerClass = Part::FaceMakerBullseye
  Placement = pos=(30.3,30.3,19.7) rot=(0,0,1;0rad)
  Solid = false
  Source = -> Face079
  Symmetric = false
FEATURE [Part::Feature] Face080
  shape: bbox 3.5 x 17.8 x 2e-07 mm, 1 faces, 0 solids (baked)
FEATURE [Part::Revolution] Revolve084  label="removeToCreateScrewAndThreadedInsertHole021"
  Angle = 360
  Axis = (0,1,0)
  Base = (0,0,0)
  FaceMakerClass = Part::FaceMakerBullseye
  Placement = pos=(30.3,30.3,51.7) rot=(0,0,1;0rad)
  Solid = false
  Source = -> Face080
  Symmetric = false
FEATURE [Part::MultiFuse] Fusion053  label="createThreadedInsertHolesForFan"
  Shapes = -> [Revolve081,Revolve082,Revolve083,Revolve084]
FEATURE [Part::Cut] Cut017  label="fanScrewHousing001"
  Base = -> Fusion046
  Tool = -> Fusion053
FEATURE [Part::Feature] Face081
  shape: bbox 3.5 x 17.8 x 2e-07 mm, 1 faces, 0 solids (baked)
FEATURE [Part::Revolution] Revolve085  label="removeToCreateScrewAndThreadedInsertHole022"
  Angle = 360
  Axis = (0,1,0)
  Base = (0,0,0)
  FaceMakerClass = Part::FaceMakerBullseye
  Placement = pos=(62.3,30.3,19.7) rot=(0,0,1;0rad)
  Solid = false
  Source = -> Face081
  Symmetric = false
FEATURE [Part::Feature] Face082
  shape: bbox 3.5 x 17.8 x 2e-07 mm, 1 faces, 0 solids (baked)
FEATURE [Part::Revolution] Revolve086  label="removeToCreateScrewAndThreadedInsertHole023"
  Angle = 360
  Axis = (0,1,0)
  Base = (0,0,0)
  FaceMakerClass = Part::FaceMakerBullseye
  Placement = pos=(62.3,30.3,51.7) rot=(0,0,1;0rad)
  Solid = false
  Source = -> Face082
  Symmetric = false
FEATURE [Part::Feature] Face083
  shape: bbox 3.5 x 17.8 x 2e-07 mm, 1 faces, 0 solids (baked)
FEATURE [Part::Revolution] Revolve087  label="removeToCreateScrewAndThreadedInsertHole024"
  Angle = 360
  Axis = (0,1,0)
  Base = (0,0,0)
  FaceMakerClass = Part::FaceMakerBullseye
  Placement = pos=(30.3,30.3,19.7) rot=(0,0,1;0rad)
  Solid = false
  Source = -> Face083
  Symmetric = false
FEATURE [Part::Feature] Face084
  shape: bbox 3.5 x 17.8 x 2e-07 mm, 1 faces, 0 solids (baked)
FEATURE [Part::Revolution] Revolve088  label="removeToCreateScrewAndThreadedInsertHole025"
  Angle = 360
  Axis = (0,1,0)
  Base = (0,0,0)
  FaceMakerClass = Part::FaceMakerBullseye
  Placement = pos=(30.3,30.3,51.7) rot=(0,0,1;0rad)
  Solid = false
  Source = -> Face084
  Symmetric = false
FEATURE [Part::MultiFuse] Fusion054  label="createThreadedInsertHolesForFan001"
  Shapes = -> [Revolve085,Revolve086,Revolve087,Revolve088]
FEATURE [Part::Cut] Cut018  label="top007"
  Base = -> Fusion040
  Tool = -> Fusion054
FEATURE [Sketcher::SketchObject] Sketch029
  FullyConstrained = false
  Placement = pos=(0,0,0) rot=(1,0,0;1.5708rad)
  sketch-geometry (24):
    g0: ArcOfCircle CenterX=-4 CenterY=-10.5 CenterZ=0 NormalX=0 NormalY=0 NormalZ=1 AngleXU=0 Radius=1.5 StartAngle=6e-16 EndAngle=3.14159
    g1: ArcOfCircle CenterX=-34.2 CenterY=-10.5 CenterZ=0 NormalX=0 NormalY=0 NormalZ=1 AngleXU=0 Radius=1.5 StartAngle=0 EndAngle=3.14159
    g2: ArcOfCircle CenterX=-34.2 CenterY=-27.7 CenterZ=0 NormalX=0 NormalY=0 NormalZ=1 AngleXU=0 Radius=1.5 StartAngle=3.14159 EndAngle=6.28319
    g3: ArcOfCircle CenterX=-4 CenterY=-27.7 CenterZ=0 NormalX=0 NormalY=0 NormalZ=1 AngleXU=0 Radius=1.5 StartAngle=3.1416 EndAngle=6.28319
    g4: ArcOfCircle CenterX=-10 CenterY=-4.3 CenterZ=0 NormalX=0 NormalY=0 NormalZ=1 AngleXU=0 Radius=1.5 StartAngle=2e-16 EndAngle=3.14159
    g5: ArcOfCircle CenterX=-16.1 CenterY=-1.8 CenterZ=0 NormalX=0 NormalY=0 NormalZ=1 AngleXU=0 Radius=1.5 StartAngle=5e-16 EndAngle=3.14159
    g6: ArcOfCircle CenterX=-22.1 CenterY=-1.8 CenterZ=0 NormalX=0 NormalY=0 NormalZ=1 AngleXU=0 Radius=1.5 StartAngle=5e-16 EndAngle=3.14159
    g7: ArcOfCircle CenterX=-28.2 CenterY=-4.3 CenterZ=0 NormalX=0 NormalY=0 NormalZ=1 AngleXU=0 Radius=1.5 StartAngle=2e-16 EndAngle=3.14159
    g8: ArcOfCircle CenterX=-10 CenterY=-33.9 CenterZ=0 NormalX=0 NormalY=0 NormalZ=1 AngleXU=0 Radius=1.5 StartAngle=3.14159 EndAngle=6.28319
    g9: ArcOfCircle CenterX=-16.1 CenterY=-36.4 CenterZ=0 NormalX=0 NormalY=0 NormalZ=1 AngleXU=0 Radius=1.5 StartAngle=3.14159 EndAngle=6.28319
    g10: ArcOfCircle CenterX=-22.1 CenterY=-36.4 CenterZ=0 NormalX=0 NormalY=0 NormalZ=1 AngleXU=0 Radius=1.5 StartAngle=3.14159 EndAngle=6.28319
    g11: ArcOfCircle CenterX=-28.2 CenterY=-33.9 CenterZ=0 NormalX=0 NormalY=0 NormalZ=1 AngleXU=0 Radius=1.5 StartAngle=3.14159 EndAngle=6.28319
    g12: LineSegment StartX=-35.7 StartY=-10.5 StartZ=0 EndX=-35.7 EndY=-27.7 EndZ=0
    g13: LineSegment StartX=-32.7 StartY=-10.5 StartZ=0 EndX=-32.7 EndY=-27.7 EndZ=0
    g14: LineSegment StartX=-29.7 StartY=-33.9 StartZ=0 EndX=-29.7 EndY=-4.3 EndZ=0
    g15: LineSegment StartX=-26.7 StartY=-33.9 StartZ=0 EndX=-26.7 EndY=-4.3 EndZ=0
    g16: LineSegment StartX=-2.5 StartY=-10.5 StartZ=0 EndX=-2.5 EndY=-27.7 EndZ=0
    g17: LineSegment StartX=-8.5 StartY=-4.3 StartZ=0 EndX=-8.5 EndY=-33.9 EndZ=0
    g18: LineSegment StartX=-5.5 StartY=-10.5 StartZ=0 EndX=-5.5 EndY=-27.7 EndZ=0
    g19: LineSegment StartX=-11.5 StartY=-4.3 StartZ=0 EndX=-11.5 EndY=-33.9 EndZ=0
    g20: LineSegment StartX=-14.6 StartY=-1.8 StartZ=0 EndX=-14.6 EndY=-36.4 EndZ=0
    g21: LineSegment StartX=-17.6 StartY=-1.8 StartZ=0 EndX=-17.6 EndY=-36.4 EndZ=0
    g22: LineSegment StartX=-20.6 StartY=-36.4 StartZ=0 EndX=-20.6 EndY=-1.8 EndZ=0
    g23: LineSegment StartX=-23.6 StartY=-1.8 StartZ=0 EndX=-23.6 EndY=-36.4 EndZ=0
  constraints (48):
    c: Block(g0)
    c: Block(g1)
    c: Block(g2)
    c: Block(g3)
    c: Block(g4)
    c: Block(g5)
    c: Block(g6)
    c: Block(g7)
    c: Block(g8)
    c: Block(g9)
    c: Block(g10)
    c: Block(g11)
    c: Coincident(g12,g1)
    c: Coincident(g12,g2)
    c: Vertical(g12)
    c: Coincident(g13,g1)
    c: Coincident(g13,g2)
    c: Vertical(g13)
    c: Coincident(g14,g11)
    c: Coincident(g14,g7)
    c: Vertical(g14)
    c: Coincident(g15,g11)
    c: Coincident(g15,g7)
    c: Vertical(g15)
    c: Coincident(g16,g0)
    c: Coincident(g16,g3)
    c: Vertical(g16)
    c: Coincident(g17,g4)
    c: Coincident(g17,g8)
    c: Vertical(g17)
    c: Coincident(g18,g0)
    c: Coincident(g18,g3)
    c: Vertical(g18)
    c: Coincident(g19,g4)
    c: Coincident(g19,g8)
    c: Vertical(g19)
    c: Coincident(g20,g5)
    c: Coincident(g20,g9)
    c: Vertical(g20)
    c: Coincident(g21,g5)
    c: Coincident(g21,g9)
    c: Vertical(g21)
    c: Coincident(g22,g10)
    c: Coincident(g22,g6)
    c: Vertical(g22)
    c: Coincident(g23,g6)
    c: Coincident(g23,g10)
    c: Vertical(g23)
FEATURE [Part::Extrusion] Extrude020  label="removeToCreateFanGrillHoles"
  Base = -> Sketch029
  Dir = (0,-1,6e-16)
  DirMode = 2
  FaceMakerClass = Part::FaceMakerBullseye
  LengthFwd = 10
  LengthRev = 0
  Placement = pos=(65.4,44,54.82) rot=(0,0,1;0rad)
  Solid = true
  Symmetric = false
FEATURE [Part::MultiFuse] Fusion055  label="top008"
  Shapes = -> [Cut017,Cut018]
FEATURE [Part::Cut] Cut019  label="top009"
  Base = -> Fusion055
  Tool = -> Extrude020
FEATURE [App::MeasureDistance] Distance003  label="Distance: 71.95 mm"
  Distance = 71.9513
  P1 = (117,38,72)
  P2 = (117,38,0.0487319)
FEATURE [Sketcher::SketchObject] Sketch030
  FullyConstrained = true
  Placement = pos=(117,19,0) rot=(0.57735,0.57735,0.57735;2.0944rad)
  sketch-geometry (48):
    g0: LineSegment StartX=-49.19 StartY=69.25 StartZ=0 EndX=-49.19 EndY=66.25 EndZ=0
    g1: LineSegment StartX=-49.19 StartY=63.5 StartZ=0 EndX=-49.19 EndY=60.5 EndZ=0
    g2: LineSegment StartX=-49.19 StartY=57.75 StartZ=0 EndX=-49.19 EndY=54.75 EndZ=0
    g3: LineSegment StartX=-49.19 StartY=52 StartZ=0 EndX=-49.19 EndY=49 EndZ=0
    g4: LineSegment StartX=-49.19 StartY=46.25 StartZ=0 EndX=-49.19 EndY=43.25 EndZ=0
    g5: LineSegment StartX=-49.19 StartY=40.5 StartZ=0 EndX=-49.19 EndY=37.5 EndZ=0
    g6: LineSegment StartX=-49.19 StartY=34.5 StartZ=0 EndX=-49.19 EndY=31.5 EndZ=0
    g7: LineSegment StartX=-49.19 StartY=28.75 StartZ=0 EndX=-49.19 EndY=25.75 EndZ=0
    g8: LineSegment StartX=-49.19 StartY=23 StartZ=0 EndX=-49.19 EndY=20 EndZ=0
    g9: LineSegment StartX=-49.19 StartY=17.25 StartZ=0 EndX=-49.19 EndY=14.25 EndZ=0
    g10: LineSegment StartX=-49.19 StartY=11.5 StartZ=0 EndX=-49.19 EndY=8.5 EndZ=0
    g11: LineSegment StartX=-49.19 StartY=5.75 StartZ=0 EndX=-49.19 EndY=2.75 EndZ=0
    g12: ArcOfCircle CenterX=-1.5 CenterY=67.75 CenterZ=0 NormalX=0 NormalY=0 NormalZ=1 AngleXU=0 Radius=1.5 StartAngle=4.71239 EndAngle=7.85398
    g13: ArcOfCircle CenterX=-1.5 CenterY=62 CenterZ=0 NormalX=0 NormalY=0 NormalZ=1 AngleXU=0 Radius=1.5 StartAngle=4.71239 EndAngle=7.85398
    g14: ArcOfCircle CenterX=-1.5 CenterY=56.25 CenterZ=0 NormalX=0 NormalY=0 NormalZ=1 AngleXU=0 Radius=1.5 StartAngle=4.71239 EndAngle=7.85398
    g15: ArcOfCircle CenterX=-11.49 CenterY=50.5 CenterZ=0 NormalX=0 NormalY=0 NormalZ=1 AngleXU=0 Radius=1.5 StartAngle=4.71239 EndAngle=7.85398
    g16: ArcOfCircle CenterX=-16.28 CenterY=44.75 CenterZ=0 NormalX=0 NormalY=0 NormalZ=1 AngleXU=0 Radius=1.5 StartAngle=4.71239 EndAngle=7.85398
    g17: ArcOfCircle CenterX=-18.2337 CenterY=39 CenterZ=0 NormalX=0 NormalY=0 NormalZ=1 AngleXU=0 Radius=1.5 StartAngle=4.71485 EndAngle=7.85398
    g18: ArcOfCircle CenterX=-16.2837 CenterY=27.25 CenterZ=0 NormalX=0 NormalY=0 NormalZ=1 AngleXU=0 Radius=1.5 StartAngle=4.71485 EndAngle=7.85398
    g19: ArcOfCircle CenterX=-18.2337 CenterY=33 CenterZ=0 NormalX=0 NormalY=0 NormalZ=1 AngleXU=0 Radius=1.5 StartAngle=4.71485 EndAngle=7.85398
    g20: ArcOfCircle CenterX=-11.49 CenterY=21.5 CenterZ=0 NormalX=0 NormalY=0 NormalZ=1 AngleXU=0 Radius=1.5 StartAngle=4.71239 EndAngle=7.85398
    g21: ArcOfCircle CenterX=-1.5 CenterY=4.25 CenterZ=0 NormalX=0 NormalY=0 NormalZ=1 AngleXU=0 Radius=1.5 StartAngle=4.71239 EndAngle=7.85398
    g22: ArcOfCircle CenterX=-1.5 CenterY=10 CenterZ=0 NormalX=0 NormalY=0 NormalZ=1 AngleXU=0 Radius=1.5 StartAngle=4.71239 EndAngle=7.85398
    g23: ArcOfCircle CenterX=-1.5 CenterY=15.75 CenterZ=0 NormalX=0 NormalY=0 NormalZ=1 AngleXU=0 Radius=1.5 StartAngle=4.71239 EndAngle=7.85398
    g24: LineSegment StartX=-49.19 StartY=69.25 StartZ=0 EndX=-1.5 EndY=69.25 EndZ=0
    g25: LineSegment StartX=-49.19 StartY=66.25 StartZ=0 EndX=-1.5 EndY=66.25 EndZ=0
    g26: LineSegment StartX=-49.19 StartY=63.5 StartZ=0 EndX=-1.5 EndY=63.5 EndZ=0
    g27: LineSegment StartX=-49.19 StartY=60.5 StartZ=0 EndX=-1.5 EndY=60.5 EndZ=0
    g28: LineSegment StartX=-49.19 StartY=57.75 StartZ=0 EndX=-1.5 EndY=57.75 EndZ=0
    g29: LineSegment StartX=-49.19 StartY=54.75 StartZ=0 EndX=-1.5 EndY=54.75 EndZ=0
    g30: LineSegment StartX=-49.19 StartY=52 StartZ=0 EndX=-11.49 EndY=52 EndZ=0
    g31: LineSegment StartX=-49.19 StartY=49 StartZ=0 EndX=-11.49 EndY=49 EndZ=0
    g32: LineSegment StartX=-49.19 StartY=46.25 StartZ=0 EndX=-16.28 EndY=46.25 EndZ=0
    g33: LineSegment StartX=-49.19 StartY=43.25 StartZ=0 EndX=-16.28 EndY=43.25 EndZ=0
    g34: LineSegment StartX=-49.19 StartY=40.5 StartZ=0 EndX=-18.2337 EndY=40.5 EndZ=0
    g35: LineSegment StartX=-49.19 StartY=37.5 StartZ=0 EndX=-18.23 EndY=37.5 EndZ=0
    g36: LineSegment StartX=-49.19 StartY=34.5 StartZ=0 EndX=-18.2337 EndY=34.5 EndZ=0
    g37: LineSegment StartX=-49.19 StartY=31.5 StartZ=0 EndX=-18.23 EndY=31.5 EndZ=0
    g38: LineSegment StartX=-49.19 StartY=28.75 StartZ=0 EndX=-16.2837 EndY=28.75 EndZ=0
    g39: LineSegment StartX=-49.19 StartY=25.75 StartZ=0 EndX=-16.28 EndY=25.75 EndZ=0
    g40: LineSegment StartX=-49.19 StartY=23 StartZ=0 EndX=-11.49 EndY=23 EndZ=0
    g41: LineSegment StartX=-49.19 StartY=20 StartZ=0 EndX=-11.49 EndY=20 EndZ=0
    g42: LineSegment StartX=-49.19 StartY=17.25 StartZ=0 EndX=-1.5 EndY=17.25 EndZ=0
    g43: LineSegment StartX=-49.19 StartY=14.25 StartZ=0 EndX=-1.5 EndY=14.25 EndZ=0
    g44: LineSegment StartX=-49.19 StartY=11.5 StartZ=0 EndX=-1.5 EndY=11.5 EndZ=0
    g45: LineSegment StartX=-49.19 StartY=8.5 StartZ=0 EndX=-1.5 EndY=8.5 EndZ=0
    g46: LineSegment StartX=-49.19 StartY=5.75 StartZ=0 EndX=-1.5 EndY=5.75 EndZ=0
    g47: LineSegment StartX=-49.19 StartY=2.75 StartZ=0 EndX=-1.5 EndY=2.75 EndZ=0
  constraints (120):
    c: Vertical(g0)
    c: Distance(g0) = 3
    c: Block(g0)
    c: Vertical(g1)
    c: Distance(g1) = 3
    c: Vertical(g2)
    c: Equal(g0,g2) = 3
    c: Block(g2)
    c: Vertical(g3)
    c: Equal(g1,g3) = 3
    c: Vertical(g4)
    c: Equal(g0,g4) = 3
    c: Block(g4)
    c: Vertical(g5)
    c: Equal(g1,g5) = 3
    c: Vertical(g6)
    c: Equal(g0,g6) = 3
    c: Block(g6)
    c: Vertical(g7)
    c: Equal(g1,g7) = 3
    c: Vertical(g8)
    c: Equal(g0,g8) = 3
    c: Block(g8)
    c: Vertical(g9)
    c: Equal(g1,g9) = 3
    c: Vertical(g10)
    c: Equal(g0,g10) = 3
    c: Block(g10)
    c: Vertical(g11)
    c: Equal(g1,g11) = 3
    c: Block(g12)
    c: Block(g13)
    c: Block(g14)
    c: Block(g15)
    c: Block(g16)
    c: Block(g17)
    c: Block(g18)
    c: Block(g19)
    c: Block(g20)
    c: Block(g21)
    c: Block(g22)
    c: Block(g23)
    c: Block(g11)
    c: Block(g9)
    c: Block(g7)
    c: Block(g5)
    c: Block(g3)
    c: Block(g1)
    c: Coincident(g24,g0)
    c: Coincident(g24,g12)
    c: Horizontal(g24)
    c: Coincident(g25,g0)
    c: Coincident(g25,g12)
    c: Horizontal(g25)
    c: Coincident(g26,g1)
    c: Coincident(g26,g13)
    c: Horizontal(g26)
    c: Coincident(g27,g1)
    c: Coincident(g27,g13)
    c: Horizontal(g27)
    c: Coincident(g28,g2)
    c: Coincident(g28,g14)
    c: Horizontal(g28)
    c: Coincident(g29,g2)
    c: Coincident(g29,g14)
    c: Horizontal(g29)
    c: Coincident(g30,g3)
    c: Coincident(g30,g15)
    c: Horizontal(g30)
    c: Coincident(g31,g3)
    c: Coincident(g31,g15)
    c: Horizontal(g31)
    c: Coincident(g32,g4)
    c: Coincident(g32,g16)
    c: Horizontal(g32)
    c: Coincident(g33,g4)
    c: Coincident(g33,g16)
    c: Horizontal(g33)
    c: Coincident(g34,g5)
    c: Coincident(g34,g17)
    c: Horizontal(g34)
    c: Coincident(g35,g5)
    c: Coincident(g35,g17)
    c: Horizontal(g35)
    c: Coincident(g36,g6)
    c: Coincident(g36,g19)
    c: Horizontal(g36)
    c: Coincident(g37,g6)
    c: Coincident(g37,g19)
    c: Horizontal(g37)
    c: Coincident(g38,g7)
    c: Coincident(g38,g18)
    c: Horizontal(g38)
    c: Coincident(g39,g7)
    c: Coincident(g39,g18)
    c: Horizontal(g39)
    c: Coincident(g40,g8)
    c: Coincident(g40,g20)
    c: Horizontal(g40)
    c: Coincident(g41,g8)
    c: Coincident(g41,g20)
    c: Horizontal(g41)
    c: Coincident(g42,g9)
    c: Coincident(g42,g23)
    c: Horizontal(g42)
    c: Coincident(g43,g9)
    c: Coincident(g43,g23)
    c: Horizontal(g43)
    c: Coincident(g44,g10)
    c: Coincident(g44,g22)
    c: Horizontal(g44)
    c: Coincident(g45,g10)
    c: Coincident(g45,g22)
    c: Horizontal(g45)
    c: Coincident(g46,g11)
    c: Coincident(g46,g21)
    c: Horizontal(g46)
    c: Coincident(g47,g11)
    c: Coincident(g47,g21)
    c: Horizontal(g47)
FEATURE [Sketcher::SketchObject] Sketch031
  FullyConstrained = true
  Placement = pos=(117,19,0) rot=(0.57735,0.57735,0.57735;2.0944rad)
  sketch-geometry (24):
    g0: ArcOfCircle CenterX=-49.19 CenterY=67.75 CenterZ=0 NormalX=0 NormalY=0 NormalZ=1 AngleXU=0 Radius=1.5 StartAngle=1.5708 EndAngle=4.71239
    g1: ArcOfCircle CenterX=-49.19 CenterY=62 CenterZ=0 NormalX=0 NormalY=0 NormalZ=1 AngleXU=0 Radius=1.5 StartAngle=1.5708 EndAngle=4.71239
    g2: ArcOfCircle CenterX=-49.19 CenterY=56.25 CenterZ=0 NormalX=0 NormalY=0 NormalZ=1 AngleXU=0 Radius=1.5 StartAngle=1.5708 EndAngle=4.71239
    g3: ArcOfCircle CenterX=-49.19 CenterY=50.5 CenterZ=0 NormalX=0 NormalY=0 NormalZ=1 AngleXU=0 Radius=1.5 StartAngle=1.5708 EndAngle=4.71239
    g4: ArcOfCircle CenterX=-49.19 CenterY=44.75 CenterZ=0 NormalX=0 NormalY=0 NormalZ=1 AngleXU=0 Radius=1.5 StartAngle=1.5708 EndAngle=4.71239
    g5: ArcOfCircle CenterX=-49.19 CenterY=39 CenterZ=0 NormalX=0 NormalY=0 NormalZ=1 AngleXU=0 Radius=1.5 StartAngle=1.5708 EndAngle=4.71239
    g6: ArcOfCircle CenterX=-49.19 CenterY=33 CenterZ=0 NormalX=0 NormalY=0 NormalZ=1 AngleXU=0 Radius=1.5 StartAngle=1.5708 EndAngle=4.71239
    g7: ArcOfCircle CenterX=-49.19 CenterY=27.25 CenterZ=0 NormalX=0 NormalY=0 NormalZ=1 AngleXU=0 Radius=1.5 StartAngle=1.5708 EndAngle=4.71239
    g8: ArcOfCircle CenterX=-49.19 CenterY=21.5 CenterZ=0 NormalX=0 NormalY=0 NormalZ=1 AngleXU=0 Radius=1.5 StartAngle=1.5708 EndAngle=4.71239
    g9: ArcOfCircle CenterX=-49.19 CenterY=15.75 CenterZ=0 NormalX=0 NormalY=0 NormalZ=1 AngleXU=0 Radius=1.5 StartAngle=1.5708 EndAngle=4.71239
    g10: ArcOfCircle CenterX=-49.19 CenterY=10 CenterZ=0 NormalX=0 NormalY=0 NormalZ=1 AngleXU=0 Radius=1.5 StartAngle=1.5708 EndAngle=4.71239
    g11: ArcOfCircle CenterX=-49.19 CenterY=4.25 CenterZ=0 NormalX=0 NormalY=0 NormalZ=1 AngleXU=0 Radius=1.5 StartAngle=1.5708 EndAngle=4.71239
    g12: LineSegment StartX=-49.19 StartY=69.25 StartZ=0 EndX=-49.19 EndY=66.25 EndZ=0
    g13: LineSegment StartX=-49.19 StartY=63.5 StartZ=0 EndX=-49.19 EndY=60.5 EndZ=0
    g14: LineSegment StartX=-49.19 StartY=57.75 StartZ=0 EndX=-49.19 EndY=54.75 EndZ=0
    g15: LineSegment StartX=-49.19 StartY=52 StartZ=0 EndX=-49.19 EndY=49 EndZ=0
    g16: LineSegment StartX=-49.19 StartY=46.25 StartZ=0 EndX=-49.19 EndY=43.25 EndZ=0
    g17: LineSegment StartX=-49.19 StartY=40.5 StartZ=0 EndX=-49.19 EndY=37.5 EndZ=0
    g18: LineSegment StartX=-49.19 StartY=34.5 StartZ=0 EndX=-49.19 EndY=31.5 EndZ=0
    g19: LineSegment StartX=-49.19 StartY=28.75 StartZ=0 EndX=-49.19 EndY=25.75 EndZ=0
    g20: LineSegment StartX=-49.19 StartY=23 StartZ=0 EndX=-49.19 EndY=20 EndZ=0
    g21: LineSegment StartX=-49.19 StartY=17.25 StartZ=0 EndX=-49.19 EndY=14.25 EndZ=0
    g22: LineSegment StartX=-49.19 StartY=11.5 StartZ=0 EndX=-49.19 EndY=8.5 EndZ=0
    g23: LineSegment StartX=-49.19 StartY=5.75 StartZ=0 EndX=-49.19 EndY=2.75 EndZ=0
  constraints (48):
    c: Block(g0)
    c: Block(g1)
    c: Block(g2)
    c: Block(g3)
    c: Block(g4)
    c: Block(g5)
    c: Block(g6)
    c: Block(g7)
    c: Block(g8)
    c: Block(g9)
    c: Block(g10)
    c: Block(g11)
    c: Coincident(g12,g0)
    c: Coincident(g12,g0)
    c: Vertical(g12)
    c: Vertical(g13)
    c: Coincident(g13,g1)
    c: Vertical(g14)
    c: Coincident(g14,g2)
    c: Vertical(g15)
    c: Coincident(g15,g3)
    c: Vertical(g16)
    c: Coincident(g16,g4)
    c: Vertical(g17)
    c: Coincident(g17,g5)
    c: Vertical(g18)
    c: Coincident(g18,g6)
    c: Vertical(g19)
    c: Coincident(g19,g7)
    c: Vertical(g20)
    c: Coincident(g20,g8)
    c: Vertical(g21)
    c: Coincident(g21,g9)
    c: Vertical(g22)
    c: Coincident(g22,g10)
    c: Vertical(g23)
    c: Coincident(g23,g11)
    c: Block(g23)
    c: Block(g22)
    c: Block(g21)
    c: Block(g20)
    c: Block(g13)
    c: Block(g14)
    c: Block(g15)
    c: Block(g16)
    c: Block(g17)
    c: Block(g18)
    c: Block(g19)
FEATURE [Part::Extrusion] Extrude022
  Base = -> Sketch030
  Dir = (1,-2e-16,2e-16)
  DirMode = 2
  FaceMakerClass = Part::FaceMakerBullseye
  LengthFwd = 19
  LengthRev = 0
  Placement = pos=(-19,0,0) rot=(0,0,1;0rad)
  Solid = true
  Symmetric = false
FEATURE [Part::Fillet] Fillet022
  Base = -> Extrude022
  Edges = 24 edges r=1.49: [Edge6,Edge11,Edge18,Edge23,Edge30,Edge35,Edge42,Edge47,Edge54,Edge59,Edge66,Edge71,Edge78,Edge83,Edge90,Edge95,Edge102,Edge107,Edge114,Edge119,Edge126,Edge131,Edge138,Edge143]
FEATURE [Part::Cut] Cut020  label="top010"
  Base = -> Cut019
  Tool = -> Fillet022
FEATURE [Sketcher::SketchObject] Sketch032
  FullyConstrained = true
  Placement = pos=(117,19,0) rot=(0.57735,0.57735,0.57735;2.0944rad)
  sketch-geometry (48):
    g0: LineSegment StartX=-49.19 StartY=69.25 StartZ=0 EndX=-49.19 EndY=66.25 EndZ=0
    g1: LineSegment StartX=-49.19 StartY=63.5 StartZ=0 EndX=-49.19 EndY=60.5 EndZ=0
    g2: LineSegment StartX=-49.19 StartY=57.75 StartZ=0 EndX=-49.19 EndY=54.75 EndZ=0
    g3: LineSegment StartX=-49.19 StartY=52 StartZ=0 EndX=-49.19 EndY=49 EndZ=0
    g4: LineSegment StartX=-49.19 StartY=46.25 StartZ=0 EndX=-49.19 EndY=43.25 EndZ=0
    g5: LineSegment StartX=-49.19 StartY=40.5 StartZ=0 EndX=-49.19 EndY=37.5 EndZ=0
    g6: LineSegment StartX=-49.19 StartY=34.5 StartZ=0 EndX=-49.19 EndY=31.5 EndZ=0
    g7: LineSegment StartX=-49.19 StartY=28.75 StartZ=0 EndX=-49.19 EndY=25.75 EndZ=0
    g8: LineSegment StartX=-49.19 StartY=23 StartZ=0 EndX=-49.19 EndY=20 EndZ=0
    g9: LineSegment StartX=-49.19 StartY=17.25 StartZ=0 EndX=-49.19 EndY=14.25 EndZ=0
    g10: LineSegment StartX=-49.19 StartY=11.5 StartZ=0 EndX=-49.19 EndY=8.5 EndZ=0
    g11: LineSegment StartX=-49.19 StartY=5.75 StartZ=0 EndX=-49.19 EndY=2.75 EndZ=0
    g12: ArcOfCircle CenterX=-1.5 CenterY=67.75 CenterZ=0 NormalX=0 NormalY=0 NormalZ=1 AngleXU=0 Radius=1.5 StartAngle=4.71239 EndAngle=7.85398
    g13: ArcOfCircle CenterX=-1.5 CenterY=62 CenterZ=0 NormalX=0 NormalY=0 NormalZ=1 AngleXU=0 Radius=1.5 StartAngle=4.71239 EndAngle=7.85398
    g14: ArcOfCircle CenterX=-1.5 CenterY=56.25 CenterZ=0 NormalX=0 NormalY=0 NormalZ=1 AngleXU=0 Radius=1.5 StartAngle=4.71239 EndAngle=7.85398
    g15: ArcOfCircle CenterX=-11.49 CenterY=50.5 CenterZ=0 NormalX=0 NormalY=0 NormalZ=1 AngleXU=0 Radius=1.5 StartAngle=4.71239 EndAngle=7.85398
    g16: ArcOfCircle CenterX=-16.28 CenterY=44.75 CenterZ=0 NormalX=0 NormalY=0 NormalZ=1 AngleXU=0 Radius=1.5 StartAngle=4.71239 EndAngle=7.85398
    g17: ArcOfCircle CenterX=-18.2337 CenterY=39 CenterZ=0 NormalX=0 NormalY=0 NormalZ=1 AngleXU=0 Radius=1.5 StartAngle=4.71485 EndAngle=7.85398
    g18: ArcOfCircle CenterX=-16.2837 CenterY=27.25 CenterZ=0 NormalX=0 NormalY=0 NormalZ=1 AngleXU=0 Radius=1.5 StartAngle=4.71485 EndAngle=7.85398
    g19: ArcOfCircle CenterX=-18.2337 CenterY=33 CenterZ=0 NormalX=0 NormalY=0 NormalZ=1 AngleXU=0 Radius=1.5 StartAngle=4.71485 EndAngle=7.85398
    g20: ArcOfCircle CenterX=-11.49 CenterY=21.5 CenterZ=0 NormalX=0 NormalY=0 NormalZ=1 AngleXU=0 Radius=1.5 StartAngle=4.71239 EndAngle=7.85398
    g21: ArcOfCircle CenterX=-1.5 CenterY=4.25 CenterZ=0 NormalX=0 NormalY=0 NormalZ=1 AngleXU=0 Radius=1.5 StartAngle=4.71239 EndAngle=7.85398
    g22: ArcOfCircle CenterX=-1.5 CenterY=10 CenterZ=0 NormalX=0 NormalY=0 NormalZ=1 AngleXU=0 Radius=1.5 StartAngle=4.71239 EndAngle=7.85398
    g23: ArcOfCircle CenterX=-1.5 CenterY=15.75 CenterZ=0 NormalX=0 NormalY=0 NormalZ=1 AngleXU=0 Radius=1.5 StartAngle=4.71239 EndAngle=7.85398
    g24: LineSegment StartX=-49.19 StartY=69.25 StartZ=0 EndX=-1.5 EndY=69.25 EndZ=0
    g25: LineSegment StartX=-49.19 StartY=66.25 StartZ=0 EndX=-1.5 EndY=66.25 EndZ=0
    g26: LineSegment StartX=-49.19 StartY=63.5 StartZ=0 EndX=-1.5 EndY=63.5 EndZ=0
    g27: LineSegment StartX=-49.19 StartY=60.5 StartZ=0 EndX=-1.5 EndY=60.5 EndZ=0
    g28: LineSegment StartX=-49.19 StartY=57.75 StartZ=0 EndX=-1.5 EndY=57.75 EndZ=0
    g29: LineSegment StartX=-49.19 StartY=54.75 StartZ=0 EndX=-1.5 EndY=54.75 EndZ=0
    g30: LineSegment StartX=-49.19 StartY=52 StartZ=0 EndX=-11.49 EndY=52 EndZ=0
    g31: LineSegment StartX=-49.19 StartY=49 StartZ=0 EndX=-11.49 EndY=49 EndZ=0
    g32: LineSegment StartX=-49.19 StartY=46.25 StartZ=0 EndX=-16.28 EndY=46.25 EndZ=0
    g33: LineSegment StartX=-49.19 StartY=43.25 StartZ=0 EndX=-16.28 EndY=43.25 EndZ=0
    g34: LineSegment StartX=-49.19 StartY=40.5 StartZ=0 EndX=-18.2337 EndY=40.5 EndZ=0
    g35: LineSegment StartX=-49.19 StartY=37.5 StartZ=0 EndX=-18.23 EndY=37.5 EndZ=0
    g36: LineSegment StartX=-49.19 StartY=34.5 StartZ=0 EndX=-18.2337 EndY=34.5 EndZ=0
    g37: LineSegment StartX=-49.19 StartY=31.5 StartZ=0 EndX=-18.23 EndY=31.5 EndZ=0
    g38: LineSegment StartX=-49.19 StartY=28.75 StartZ=0 EndX=-16.2837 EndY=28.75 EndZ=0
    g39: LineSegment StartX=-49.19 StartY=25.75 StartZ=0 EndX=-16.28 EndY=25.75 EndZ=0
    g40: LineSegment StartX=-49.19 StartY=23 StartZ=0 EndX=-11.49 EndY=23 EndZ=0
    g41: LineSegment StartX=-49.19 StartY=20 StartZ=0 EndX=-11.49 EndY=20 EndZ=0
    g42: LineSegment StartX=-49.19 StartY=17.25 StartZ=0 EndX=-1.5 EndY=17.25 EndZ=0
    g43: LineSegment StartX=-49.19 StartY=14.25 StartZ=0 EndX=-1.5 EndY=14.25 EndZ=0
    g44: LineSegment StartX=-49.19 StartY=11.5 StartZ=0 EndX=-1.5 EndY=11.5 EndZ=0
    g45: LineSegment StartX=-49.19 StartY=8.5 StartZ=0 EndX=-1.5 EndY=8.5 EndZ=0
    g46: LineSegment StartX=-49.19 StartY=5.75 StartZ=0 EndX=-1.5 EndY=5.75 EndZ=0
    g47: LineSegment StartX=-49.19 StartY=2.75 StartZ=0 EndX=-1.5 EndY=2.75 EndZ=0
  constraints (120):
    c: Vertical(g0)
    c: Distance(g0) = 3
    c: Block(g0)
    c: Vertical(g1)
    c: Distance(g1) = 3
    c: Vertical(g2)
    c: Equal(g0,g2) = 3
    c: Block(g2)
    c: Vertical(g3)
    c: Equal(g1,g3) = 3
    c: Vertical(g4)
    c: Equal(g0,g4) = 3
    c: Block(g4)
    c: Vertical(g5)
    c: Equal(g1,g5) = 3
    c: Vertical(g6)
    c: Equal(g0,g6) = 3
    c: Block(g6)
    c: Vertical(g7)
    c: Equal(g1,g7) = 3
    c: Vertical(g8)
    c: Equal(g0,g8) = 3
    c: Block(g8)
    c: Vertical(g9)
    c: Equal(g1,g9) = 3
    c: Vertical(g10)
    c: Equal(g0,g10) = 3
    c: Block(g10)
    c: Vertical(g11)
    c: Equal(g1,g11) = 3
    c: Block(g12)
    c: Block(g13)
    c: Block(g14)
    c: Block(g15)
    c: Block(g16)
    c: Block(g17)
    c: Block(g18)
    c: Block(g19)
    c: Block(g20)
    c: Block(g21)
    c: Block(g22)
    c: Block(g23)
    c: Block(g11)
    c: Block(g9)
    c: Block(g7)
    c: Block(g5)
    c: Block(g3)
    c: Block(g1)
    c: Coincident(g24,g0)
    c: Coincident(g24,g12)
    c: Horizontal(g24)
    c: Coincident(g25,g0)
    c: Coincident(g25,g12)
    c: Horizontal(g25)
    c: Coincident(g26,g1)
    c: Coincident(g26,g13)
    c: Horizontal(g26)
    c: Coincident(g27,g1)
    c: Coincident(g27,g13)
    c: Horizontal(g27)
    c: Coincident(g28,g2)
    c: Coincident(g28,g14)
    c: Horizontal(g28)
    c: Coincident(g29,g2)
    c: Coincident(g29,g14)
    c: Horizontal(g29)
    c: Coincident(g30,g3)
    c: Coincident(g30,g15)
    c: Horizontal(g30)
    c: Coincident(g31,g3)
    c: Coincident(g31,g15)
    c: Horizontal(g31)
    c: Coincident(g32,g4)
    c: Coincident(g32,g16)
    c: Horizontal(g32)
    c: Coincident(g33,g4)
    c: Coincident(g33,g16)
    c: Horizontal(g33)
    c: Coincident(g34,g5)
    c: Coincident(g34,g17)
    c: Horizontal(g34)
    c: Coincident(g35,g5)
    c: Coincident(g35,g17)
    c: Horizontal(g35)
    c: Coincident(g36,g6)
    c: Coincident(g36,g19)
    c: Horizontal(g36)
    c: Coincident(g37,g6)
    c: Coincident(g37,g19)
    c: Horizontal(g37)
    c: Coincident(g38,g7)
    c: Coincident(g38,g18)
    c: Horizontal(g38)
    c: Coincident(g39,g7)
    c: Coincident(g39,g18)
    c: Horizontal(g39)
    c: Coincident(g40,g8)
    c: Coincident(g40,g20)
    c: Horizontal(g40)
    c: Coincident(g41,g8)
    c: Coincident(g41,g20)
    c: Horizontal(g41)
    c: Coincident(g42,g9)
    c: Coincident(g42,g23)
    c: Horizontal(g42)
    c: Coincident(g43,g9)
    c: Coincident(g43,g23)
    c: Horizontal(g43)
    c: Coincident(g44,g10)
    c: Coincident(g44,g22)
    c: Horizontal(g44)
    c: Coincident(g45,g10)
    c: Coincident(g45,g22)
    c: Horizontal(g45)
    c: Coincident(g46,g11)
    c: Coincident(g46,g21)
    c: Horizontal(g46)
    c: Coincident(g47,g11)
    c: Coincident(g47,g21)
    c: Horizontal(g47)
FEATURE [Part::Extrusion] Extrude023
  Base = -> Sketch032
  Dir = (1,-2e-16,2e-16)
  DirMode = 2
  FaceMakerClass = Part::FaceMakerBullseye
  LengthFwd = 19
  LengthRev = 0
  Placement = pos=(-19,0,0) rot=(0,0,1;0rad)
  Solid = true
  Symmetric = false
FEATURE [Part::Fillet] Fillet023
  Base = -> Extrude023
  Edges = <same value as first occurrence — deduplicated (x6 in doc)>
  Placement = pos=(0,0.05,0) rot=(0,0,1;0rad)
FEATURE [Part::Cut] Cut014  label="bottom003"
  Base = -> Cut007
  Tool = -> Fusion047
FEATURE [Part::Cut] Cut021  label="bottom004"
  Base = -> Cut014
  Tool = -> Fillet023
FEATURE [Sketcher::SketchObject] Sketch033
  FullyConstrained = true
  Placement = pos=(117,19,0) rot=(0.57735,0.57735,0.57735;2.0944rad)
  sketch-geometry (8):
    g0: LineSegment StartX=-49.19 StartY=69.25 StartZ=0 EndX=-49.19 EndY=66.25 EndZ=0
    g1: LineSegment StartX=-49.19 StartY=5.75 StartZ=0 EndX=-49.19 EndY=2.75 EndZ=0
    g2: ArcOfCircle CenterX=-1.5 CenterY=67.75 CenterZ=0 NormalX=0 NormalY=0 NormalZ=1 AngleXU=0 Radius=1.5 StartAngle=4.71239 EndAngle=7.85398
    g3: ArcOfCircle CenterX=-1.5 CenterY=4.25 CenterZ=0 NormalX=0 NormalY=0 NormalZ=1 AngleXU=0 Radius=1.5 StartAngle=4.71239 EndAngle=7.85398
    g4: LineSegment StartX=-49.19 StartY=69.25 StartZ=0 EndX=-1.5 EndY=69.25 EndZ=0
    g5: LineSegment StartX=-49.19 StartY=66.25 StartZ=0 EndX=-1.5 EndY=66.25 EndZ=0
    g6: LineSegment StartX=-49.19 StartY=5.75 StartZ=0 EndX=-1.5 EndY=5.75 EndZ=0
    g7: LineSegment StartX=-49.19 StartY=2.75 StartZ=0 EndX=-1.5 EndY=2.75 EndZ=0
  constraints (19):
    c: Vertical(g0)
    c: Distance(g0) = 3
    c: Block(g0)
    c: Vertical(g1)
    c: Block(g2)
    c: Block(g3)
    c: Block(g1)
    c: Coincident(g4,g0)
    c: Coincident(g4,g2)
    c: Horizontal(g4)
    c: Coincident(g5,g0)
    c: Coincident(g5,g2)
    c: Horizontal(g5)
    c: Coincident(g6,g1)
    c: Coincident(g6,g3)
    c: Horizontal(g6)
    c: Coincident(g7,g1)
    c: Coincident(g7,g3)
    c: Horizontal(g7)
FEATURE [Sketcher::SketchObject] Sketch034
  FullyConstrained = true
  Placement = pos=(117,19,0) rot=(0.57735,0.57735,0.57735;2.0944rad)
  sketch-geometry (8):
    g0: LineSegment StartX=-49.19 StartY=63.5 StartZ=0 EndX=-49.19 EndY=60.5 EndZ=0
    g1: LineSegment StartX=-49.19 StartY=11.5 StartZ=0 EndX=-49.19 EndY=8.5 EndZ=0
    g2: ArcOfCircle CenterX=-1.5 CenterY=62 CenterZ=0 NormalX=0 NormalY=0 NormalZ=1 AngleXU=0 Radius=1.5 StartAngle=4.71239 EndAngle=7.85398
    g3: ArcOfCircle CenterX=-1.5 CenterY=10 CenterZ=0 NormalX=0 NormalY=0 NormalZ=1 AngleXU=0 Radius=1.5 StartAngle=4.71239 EndAngle=7.85398
    g4: LineSegment StartX=-49.19 StartY=63.5 StartZ=0 EndX=-1.5 EndY=63.5 EndZ=0
    g5: LineSegment StartX=-49.19 StartY=60.5 StartZ=0 EndX=-1.5 EndY=60.5 EndZ=0
    g6: LineSegment StartX=-49.19 StartY=11.5 StartZ=0 EndX=-1.5 EndY=11.5 EndZ=0
    g7: LineSegment StartX=-49.19 StartY=8.5 StartZ=0 EndX=-1.5 EndY=8.5 EndZ=0
  constraints (19):
    c: Vertical(g0)
    c: Distance(g0) = 3
    c: Vertical(g1)
    c: Block(g1)
    c: Block(g2)
    c: Block(g3)
    c: Block(g0)
    c: Coincident(g4,g0)
    c: Coincident(g4,g2)
    c: Horizontal(g4)
    c: Coincident(g5,g0)
    c: Coincident(g5,g2)
    c: Horizontal(g5)
    c: Coincident(g6,g1)
    c: Coincident(g6,g3)
    c: Horizontal(g6)
    c: Coincident(g7,g1)
    c: Coincident(g7,g3)
    c: Horizontal(g7)
FEATURE [Part::Extrusion] Extrude024
  Base = -> Sketch033
  Dir = (1,0,0)
  DirMode = 2
  FaceMakerClass = Part::FaceMakerBullseye
  LengthFwd = 10
  LengthRev = 0
  Solid = true
  Symmetric = false
FEATURE [Part::Extrusion] Extrude025
  Base = -> Sketch034
  Dir = (1,0,0)
  DirMode = 2
  FaceMakerClass = Part::FaceMakerBullseye
  LengthFwd = 10
  LengthRev = 0
  Solid = true
  Symmetric = false
FEATURE [Part::Fillet] Fillet024  label="removeFromtMoreFrontCaseScrewRetainers"
  Base = -> Extrude024
  Edges = 4 edges r=1.49: [Edge6,Edge11,Edge18,Edge23]
  Placement = pos=(-11,0,0) rot=(0,0,1;0rad)
FEATURE [Part::Fillet] Fillet025  label="removeFromtMoreFrontCaseScrewRetainers001"
  Base = -> Extrude025
  Edges = 4 edges r=1.49: [Edge6,Edge11,Edge18,Edge23]
  Placement = pos=(-19,0,0) rot=(0,0,1;0rad)
FEATURE [Part::Cut] Cut022
  Base = -> Cut015
  Tool = -> Fillet025
FEATURE [Part::Cut] Cut023  label="screwRetainers"
  Base = -> Cut022
  Tool = -> Fillet024
FEATURE [Part::MultiFuse] Fusion056  label="bottom005"
  Shapes = -> [Fusion044,Cut021]
FEATURE [Part::MultiFuse] Fusion057  label="casePillars001"
  Shapes = -> [Cut016,Fusion052]
FEATURE [Part::MultiFuse] Fusion058  label="bottom006"
  Shapes = -> [Fusion056,Cut023]
FEATURE [Part::MultiFuse] Fusion059  label="bottom007"
  Shapes = -> [Fusion058,Fillet005]
FEATURE [Part::MultiFuse] Fusion060  label="bottom008"
  Shapes = -> [Fusion059,Fusion]
FEATURE [Part::MultiFuse] Fusion061  label="top011"
  Shapes = -> [Cut006,Cut020]
FEATURE [Part::MultiFuse] Fusion062  label="top012"
  Shapes = -> [Fusion057,Fusion061]
FEATURE [Sketcher::SketchObject] Sketch035  label="topSketch007"
  FullyConstrained = true
  sketch-geometry (6):
    g0: LineSegment StartX=19 StartY=38 StartZ=0 EndX=117 EndY=38 EndZ=0
    g1: ArcOfCircle CenterX=19 CenterY=19 CenterZ=0 NormalX=0 NormalY=0 NormalZ=1 AngleXU=0 Radius=19 StartAngle=1.5708 EndAngle=3.14159
    g2: LineSegment StartX=117 StartY=38 StartZ=0 EndX=117 EndY=19 EndZ=0
    g3: LineSegment StartX=98 StartY=1.0161e-12 StartZ=0 EndX=5.22862e-06 EndY=1.0161e-12 EndZ=0
    g4: LineSegment StartX=5.22862e-06 StartY=19 StartZ=0 EndX=5.22862e-06 EndY=1.0161e-12 EndZ=0
    g5: ArcOfCircle CenterX=98 CenterY=19 CenterZ=0 NormalX=0 NormalY=0 NormalZ=1 AngleXU=0 Radius=19 StartAngle=4.71239 EndAngle=6.28319
  constraints (16):
    c: Horizontal(g0)
    c: Distance(g0) = 98
    c: Coincident(g1,g0)
    c: Block(g1)
    c: Coincident(g2,g0)
    c: Vertical(g2)
    c: Distance(g2) = 19
    c: Horizontal(g3)
    c: Coincident(g4,g1)
    c: Vertical(g4)
    c: Coincident(g3,g4)
    c: Block(g3)
    c: Coincident(g5,g2)
    c: Coincident(g5,g3)
    c: Block(g0)
    c: Block(g5)
FEATURE [Part::Extrusion] Extrude026  label="sideA001"
  Base = -> Sketch035
  Dir = (0,0,1)
  DirMode = 2
  FaceMakerClass = Part::FaceMakerBullseye
  LengthFwd = 3
  LengthRev = 0
  Placement = pos=(0,0,-2.7) rot=(0,0,1;0rad)
  Solid = true
  Symmetric = false
FEATURE [Sketcher::SketchObject] Sketch036  label="topSketch008"
  FullyConstrained = true
  sketch-geometry (6):
    g0: LineSegment StartX=19 StartY=38 StartZ=0 EndX=117 EndY=38 EndZ=0
    g1: ArcOfCircle CenterX=19 CenterY=19 CenterZ=0 NormalX=0 NormalY=0 NormalZ=1 AngleXU=0 Radius=19 StartAngle=1.5708 EndAngle=3.14159
    g2: LineSegment StartX=117 StartY=38 StartZ=0 EndX=117 EndY=19 EndZ=0
    g3: LineSegment StartX=98 StartY=1.0161e-12 StartZ=0 EndX=5.22862e-06 EndY=1.0161e-12 EndZ=0
    g4: LineSegment StartX=5.22862e-06 StartY=19 StartZ=0 EndX=5.22862e-06 EndY=1.0161e-12 EndZ=0
    g5: ArcOfCircle CenterX=98 CenterY=19 CenterZ=0 NormalX=0 NormalY=0 NormalZ=1 AngleXU=0 Radius=19 StartAngle=4.71239 EndAngle=6.28319
  constraints (16):
    c: Horizontal(g0)
    c: Distance(g0) = 98
    c: Coincident(g1,g0)
    c: Block(g1)
    c: Coincident(g2,g0)
    c: Vertical(g2)
    c: Distance(g2) = 19
    c: Horizontal(g3)
    c: Coincident(g4,g1)
    c: Vertical(g4)
    c: Coincident(g3,g4)
    c: Block(g3)
    c: Coincident(g5,g2)
    c: Coincident(g5,g3)
    c: Block(g0)
    c: Block(g5)
FEATURE [Part::Extrusion] Extrude027  label="sideB001"
  Base = -> Sketch036
  Dir = (0,0,1)
  DirMode = 2
  FaceMakerClass = Part::FaceMakerBullseye
  LengthFwd = 3
  LengthRev = 0
  Placement = pos=(0,0,71.7) rot=(0,0,1;0rad)
  Solid = true
  Symmetric = false
FEATURE [Part::MultiFuse] Fusion064  label="removeFromBottom"
  Shapes = -> [Extrude026,Extrude027]
FEATURE [Part::Cut] Cut024  label="bottom009"
  Base = -> Fusion060
  Tool = -> Fusion064
FEATURE [Sketcher::SketchObject] Sketch037  label="topSketch009"
  FullyConstrained = true
  sketch-geometry (8):
    g0: ArcOfCircle CenterX=19 CenterY=19.1201 CenterZ=0 NormalX=0 NormalY=0 NormalZ=1 AngleXU=0 Radius=18.8799 StartAngle=1.5708 EndAngle=3.14793
    g1: LineSegment StartX=0.120501 StartY=19.0004 StartZ=0 EndX=0.120501 EndY=0.000382114 EndZ=0
    g2: LineSegment StartX=19 StartY=38 StartZ=0 EndX=124 EndY=38 EndZ=0
    g3: LineSegment StartX=0.120501 StartY=0.000382114 StartZ=0 EndX=105.121 EndY=0.000382114 EndZ=0
    g4: LineSegment StartX=124 StartY=38 StartZ=0 EndX=125.616 EndY=38 EndZ=0
    g5: LineSegment StartX=105.121 StartY=0.000382114 StartZ=0 EndX=106.736 EndY=0.000382114 EndZ=0
    g6: ArcOfCircle CenterX=106.616 CenterY=19 CenterZ=0 NormalX=0 NormalY=0 NormalZ=1 AngleXU=0 Radius=19 StartAngle=4.71873 EndAngle=6.28319
    g7: LineSegment StartX=125.616 StartY=38 StartZ=0 EndX=125.616 EndY=19 EndZ=0
  constraints (21):
    c: Block(g0)
    c: Coincident(g1,g0)
    c: Vertical(g1)
    c: Horizontal(g2)
    c: Distance(g2) = 105
    c: Coincident(g2,g0)
    c: Distance(g1) = 19
    c: Coincident(g3,g1)
    c: Horizontal(g3)
    c: Distance(g3) = 105
    c: Coincident(g4,g2)
    c: Horizontal(g4)
    c: Distance(g4) = 1.61553
    c: Horizontal(g5)
    c: Equal(g4,g5) = 1.61553
    c: Coincident(g5,g3)
    c: Block(g6)
    c: Coincident(g6,g5)
    c: Coincident(g7,g4)
    c: Coincident(g7,g6)
    c: Vertical(g7)
FEATURE [Part::Extrusion] Extrude028  label="sideB"
  Base = -> Sketch037
  Dir = (0,0,1)
  DirMode = 2
  FaceMakerClass = Part::FaceMakerBullseye
  LengthFwd = 3
  LengthRev = 0
  Placement = pos=(0,0,72) rot=(0,0,1;0rad)
  Solid = true
  Symmetric = false
FEATURE [Sketcher::SketchObject] Sketch038  label="topSketch010"
  FullyConstrained = true
  sketch-geometry (22):
    g0: LineSegment StartX=5.21097e-06 StartY=3 StartZ=0 EndX=5.21097e-06 EndY=19 EndZ=0
    g1: ArcOfCircle CenterX=19 CenterY=19 CenterZ=0 NormalX=0 NormalY=0 NormalZ=1 AngleXU=0 Radius=19 StartAngle=1.5708 EndAngle=3.14159
    g2: ArcOfCircle CenterX=19 CenterY=19 CenterZ=0 NormalX=0 NormalY=0 NormalZ=1 AngleXU=0 Radius=16 StartAngle=1.5708 EndAngle=3.14159
    g3: LineSegment StartX=114 StartY=35 StartZ=0 EndX=19 EndY=35 EndZ=0
    g4: LineSegment StartX=5.21097e-06 StartY=3 StartZ=0 EndX=5.21097e-06 EndY=0 EndZ=0
    g5: LineSegment StartX=3 StartY=0 StartZ=0 EndX=5.21097e-06 EndY=0 EndZ=0
    g6: LineSegment StartX=3 StartY=19 StartZ=0 EndX=3 EndY=0 EndZ=0
    g7: LineSegment StartX=19 StartY=38 StartZ=0 EndX=124 EndY=38 EndZ=0
    g8: Circle CenterX=119 CenterY=35 CenterZ=0 NormalX=0 NormalY=0 NormalZ=1 AngleXU=0 Radius=1
    g9: Circle CenterX=121 CenterY=35 CenterZ=0 NormalX=0 NormalY=0 NormalZ=1 AngleXU=0 Radius=1
    g10: Circle CenterX=121 CenterY=33 CenterZ=0 NormalX=0 NormalY=0 NormalZ=1 AngleXU=0 Radius=1
    g11: BSplineCurve PolesCount=3 KnotsCount=2 Degree=2 IsPeriodic=0
    g12: GeomPoint X=119 Y=35 Z=0
    g13: GeomPoint X=121 Y=33 Z=0
    g14: LineSegment StartX=119 StartY=35 StartZ=0 EndX=114 EndY=35 EndZ=0
    g15: ArcOfCircle CenterX=105 CenterY=19 CenterZ=0 NormalX=0 NormalY=0 NormalZ=1 AngleXU=0 Radius=16 StartAngle=5.60905 EndAngle=6.28319
    g16: LineSegment StartX=121 StartY=33 StartZ=0 EndX=121 EndY=19 EndZ=0
    g17: LineSegment StartX=117.5 StartY=9.01251 StartZ=0 EndX=121.163 EndY=9.0125 EndZ=0
    g18: ArcOfCircle CenterX=105 CenterY=19 CenterZ=0 NormalX=0 NormalY=0 NormalZ=1 AngleXU=0 Radius=20.6155 StartAngle=5.7297 EndAngle=6.28319
    g19: LineSegment StartX=121.163 StartY=9.0125 StartZ=0 EndX=122.538 EndY=8.16329 EndZ=0
    g20: LineSegment StartX=124 StartY=38 StartZ=0 EndX=125.616 EndY=38 EndZ=0
    g21: LineSegment StartX=125.616 StartY=19 StartZ=0 EndX=125.616 EndY=38 EndZ=0
  constraints (49):
    c: Vertical(g0)
    c: Block(g0)
    c: Coincident(g1,g0)
    c: Block(g1)
    c: Coincident(g2,g1)
    c: Block(g2)
    c: Coincident(g3,g2)
    c: Horizontal(g3)
    c: Tangent(g3,g2)
    c: Coincident(g4,g0)
    c: Distance(g4) = 3
    c: Vertical(g4)
    c: Coincident(g5,g4)
    c: Horizontal(g5)
    c: Coincident(g6,g2)
    c: Coincident(g6,g5)
    c: Vertical(g6)
    c: Horizontal(g7)
    c: Distance(g7) = 105
    c: Coincident(g7,g1)
    c: Block(g3)
    c: Weight(g8) = 1
    c: Equal(g8,g9)
    c: Equal(g8,g10)
    c: InternalAlignment(g8,g11)
    c: InternalAlignment(g9,g11)
    c: InternalAlignment(g10,g11)
    c: InternalAlignment(g12,g11)
    c: InternalAlignment(g13,g11)
    c: Block(g11)
    c: Coincident(g14,g11)
    c: Coincident(g14,g3)
    c: Horizontal(g14)
    c: Block(g15)
    c: Coincident(g16,g11)
    c: Coincident(g16,g15)
    c: Vertical(g16)
    c: Distance(g16) = 14
    c: Coincident(g17,g15)
    c: Block(g18)
    c: Coincident(g19,g18)
    c: Coincident(g20,g7)
    c: Horizontal(g20)
    c: Vertical(g21)
    c: Coincident(g20,g21)
    c: Block(g20)
    c: Block(g21)
    c: Block(g19)
    c: Block(g17)
FEATURE [Part::Extrusion] Extrude029
  Base = -> Sketch038
  Dir = (0,0,1)
  DirMode = 2
  FaceMakerClass = Part::FaceMakerBullseye
  LengthFwd = 72
  LengthRev = 0
  Solid = true
  Symmetric = false
FEATURE [Part::Feature] Face085
  shape: bbox 4.8 x 25.5 x 2e-07 mm, 1 faces, 0 solids (baked)
FEATURE [Part::Revolution] Revolve089  label="moreFrontCaseScrewPost003"
  Angle = 360
  Axis = (0,1,0)
  Base = (0,0,0)
  FaceMakerClass = Part::FaceMakerBullseye
  Placement = pos=(109.5,4.5,3.5) rot=(0,0,1;0rad)
  Solid = false
  Source = -> Face085
  Symmetric = false
FEATURE [Part::Feature] Face086
  shape: bbox 4.8 x 25.5 x 2e-07 mm, 1 faces, 0 solids (baked)
FEATURE [Part::Revolution] Revolve090  label="moreFrontCaseScrewPost004"
  Angle = 360
  Axis = (0,1,0)
  Base = (0,0,0)
  FaceMakerClass = Part::FaceMakerBullseye
  Placement = pos=(109.5,4.5,68.5) rot=(0,0,1;0rad)
  Solid = false
  Source = -> Face086
  Symmetric = false
FEATURE [Part::Fillet] Fillet026  label="top013"
  Base = -> Extrude029
  Edges = 1 edges r=2: [Edge35]
FEATURE [Sketcher::SketchObject] Sketch039
  FullyConstrained = true
  sketch-geometry (7):
    g0: LineSegment StartX=0 StartY=0 StartZ=0 EndX=0 EndY=6 EndZ=0
    g1: Circle CenterX=0 CenterY=0 CenterZ=0 NormalX=0 NormalY=0 NormalZ=1 AngleXU=0 Radius=1
    g2: Circle CenterX=8 CenterY=6 CenterZ=0 NormalX=0 NormalY=0 NormalZ=1 AngleXU=0 Radius=1
    g3: BSplineCurve PolesCount=3 KnotsCount=2 Degree=2 IsPeriodic=0
    g4: GeomPoint X=0 Y=0 Z=0
    g5: GeomPoint X=8 Y=6 Z=0
    g6: LineSegment StartX=0 StartY=6 StartZ=0 EndX=8 EndY=6 EndZ=0
  constraints (14):
    c: Coincident(g0,g-1)
    c: Distance(g0) = 6
    c: Vertical(g0)
    c: Coincident(g3,g0)
    c: Weight(g1) = 1
    c: Equal(g1,g2)
    c: InternalAlignment(g1,g3)
    c: InternalAlignment(g2,g3)
    c: InternalAlignment(g4,g3)
    c: InternalAlignment(g5,g3)
    c: Block(g3)
    c: Coincident(g6,g0)
    c: Coincident(g6,g3)
    c: Horizontal(g6)
FEATURE [Sketcher::SketchObject] Sketch040
  FullyConstrained = true
  sketch-geometry (7):
    g0: LineSegment StartX=0 StartY=0 StartZ=0 EndX=0 EndY=6 EndZ=0
    g1: Circle CenterX=0 CenterY=0 CenterZ=0 NormalX=0 NormalY=0 NormalZ=1 AngleXU=0 Radius=1
    g2: Circle CenterX=8 CenterY=6 CenterZ=0 NormalX=0 NormalY=0 NormalZ=1 AngleXU=0 Radius=1
    g3: BSplineCurve PolesCount=3 KnotsCount=2 Degree=2 IsPeriodic=0
    g4: GeomPoint X=0 Y=0 Z=0
    g5: GeomPoint X=8 Y=6 Z=0
    g6: LineSegment StartX=0 StartY=6 StartZ=0 EndX=8 EndY=6 EndZ=0
  constraints (14):
    c: Coincident(g0,g-1)
    c: Distance(g0) = 6
    c: Vertical(g0)
    c: Coincident(g3,g0)
    c: Weight(g1) = 1
    c: Equal(g1,g2)
    c: InternalAlignment(g1,g3)
    c: InternalAlignment(g2,g3)
    c: InternalAlignment(g4,g3)
    c: InternalAlignment(g5,g3)
    c: Block(g3)
    c: Coincident(g6,g0)
    c: Coincident(g6,g3)
    c: Horizontal(g6)
FEATURE [Sketcher::SketchObject] Sketch041
  FullyConstrained = true
  sketch-geometry (7):
    g0: LineSegment StartX=0 StartY=0 StartZ=0 EndX=0 EndY=6 EndZ=0
    g1: Circle CenterX=0 CenterY=0 CenterZ=0 NormalX=0 NormalY=0 NormalZ=1 AngleXU=0 Radius=1
    g2: Circle CenterX=8 CenterY=6 CenterZ=0 NormalX=0 NormalY=0 NormalZ=1 AngleXU=0 Radius=1
    g3: BSplineCurve PolesCount=3 KnotsCount=2 Degree=2 IsPeriodic=0
    g4: GeomPoint X=0 Y=0 Z=0
    g5: GeomPoint X=8 Y=6 Z=0
    g6: LineSegment StartX=0 StartY=6 StartZ=0 EndX=8 EndY=6 EndZ=0
  constraints (14):
    c: Coincident(g0,g-1)
    c: Distance(g0) = 6
    c: Vertical(g0)
    c: Coincident(g3,g0)
    c: Weight(g1) = 1
    c: Equal(g1,g2)
    c: InternalAlignment(g1,g3)
    c: InternalAlignment(g2,g3)
    c: InternalAlignment(g4,g3)
    c: InternalAlignment(g5,g3)
    c: Block(g3)
    c: Coincident(g6,g0)
    c: Coincident(g6,g3)
    c: Horizontal(g6)
FEATURE [Sketcher::SketchObject] Sketch042
  FullyConstrained = true
  sketch-geometry (7):
    g0: LineSegment StartX=0 StartY=0 StartZ=0 EndX=0 EndY=6 EndZ=0
    g1: Circle CenterX=0 CenterY=0 CenterZ=0 NormalX=0 NormalY=0 NormalZ=1 AngleXU=0 Radius=1
    g2: Circle CenterX=8 CenterY=6 CenterZ=0 NormalX=0 NormalY=0 NormalZ=1 AngleXU=0 Radius=1
    g3: BSplineCurve PolesCount=3 KnotsCount=2 Degree=2 IsPeriodic=0
    g4: GeomPoint X=0 Y=0 Z=0
    g5: GeomPoint X=8 Y=6 Z=0
    g6: LineSegment StartX=0 StartY=6 StartZ=0 EndX=8 EndY=6 EndZ=0
  constraints (14):
    c: Coincident(g0,g-1)
    c: Distance(g0) = 6
    c: Vertical(g0)
    c: Coincident(g3,g0)
    c: Weight(g1) = 1
    c: Equal(g1,g2)
    c: InternalAlignment(g1,g3)
    c: InternalAlignment(g2,g3)
    c: InternalAlignment(g4,g3)
    c: InternalAlignment(g5,g3)
    c: Block(g3)
    c: Coincident(g6,g0)
    c: Coincident(g6,g3)
    c: Horizontal(g6)
FEATURE [Part::Extrusion] Extrude030  label="caseScrewPillarBracket008"
  Base = -> Sketch039
  Dir = (0,0,1)
  DirMode = 2
  FaceMakerClass = Part::FaceMakerBullseye
  LengthFwd = 2.4
  LengthRev = 0
  Placement = pos=(15.76,29,8.8) rot=(0,1,0;0rad)
  Solid = true
  Symmetric = false
FEATURE [Part::Extrusion] Extrude031  label="caseScrewPillarBracket009"
  Base = -> Sketch040
  Dir = (0,0,1)
  DirMode = 2
  FaceMakerClass = Part::FaceMakerBullseye
  LengthFwd = 2.4
  LengthRev = 0
  Placement = pos=(15.76,29,60.8) rot=(0,0,1;0rad)
  Solid = true
  Symmetric = false
FEATURE [Part::Extrusion] Extrude032  label="caseScrewPillarBracket010"
  Base = -> Sketch041
  Dir = (0,0,1)
  DirMode = 2
  FaceMakerClass = Part::FaceMakerBullseye
  LengthFwd = 2.4
  LengthRev = 0
  Placement = pos=(13.7,29,13.26) rot=(0,-1,0;1.5708rad)
  Solid = true
  Symmetric = false
FEATURE [Part::Extrusion] Extrude033  label="caseScrewPillarBracket011"
  Base = -> Sketch042
  Dir = (0,0,1)
  DirMode = 2
  FaceMakerClass = Part::FaceMakerBullseye
  LengthFwd = 2.4
  LengthRev = 0
  Placement = pos=(11.3,29,58.74) rot=(0,1,0;1.5708rad)
  Solid = true
  Symmetric = false
FEATURE [Sketcher::SketchObject] Sketch043
  FullyConstrained = true
  sketch-geometry (7):
    g0: LineSegment StartX=0 StartY=0 StartZ=0 EndX=0 EndY=6 EndZ=0
    g1: Circle CenterX=0 CenterY=0 CenterZ=0 NormalX=0 NormalY=0 NormalZ=1 AngleXU=0 Radius=1
    g2: Circle CenterX=8 CenterY=6 CenterZ=0 NormalX=0 NormalY=0 NormalZ=1 AngleXU=0 Radius=1
    g3: BSplineCurve PolesCount=3 KnotsCount=2 Degree=2 IsPeriodic=0
    g4: GeomPoint X=0 Y=0 Z=0
    g5: GeomPoint X=8 Y=6 Z=0
    g6: LineSegment StartX=0 StartY=6 StartZ=0 EndX=8 EndY=6 EndZ=0
  constraints (14):
    c: Coincident(g0,g-1)
    c: Distance(g0) = 6
    c: Vertical(g0)
    c: Coincident(g3,g0)
    c: Weight(g1) = 1
    c: Equal(g1,g2)
    c: InternalAlignment(g1,g3)
    c: InternalAlignment(g2,g3)
    c: InternalAlignment(g4,g3)
    c: InternalAlignment(g5,g3)
    c: Block(g3)
    c: Coincident(g6,g0)
    c: Coincident(g6,g3)
    c: Horizontal(g6)
FEATURE [Part::Extrusion] Extrude034  label="caseScrewPillarBracket012"
  Base = -> Sketch043
  Dir = (0,0,1)
  DirMode = 2
  FaceMakerClass = Part::FaceMakerBullseye
  LengthFwd = 2.4
  LengthRev = 0
  Placement = pos=(88.3,29,65.23) rot=(0,1,0;1.5708rad)
  Solid = true
  Symmetric = false
FEATURE [Sketcher::SketchObject] Sketch044
  FullyConstrained = true
  sketch-geometry (7):
    g0: LineSegment StartX=0 StartY=0 StartZ=0 EndX=0 EndY=6 EndZ=0
    g1: Circle CenterX=0 CenterY=0 CenterZ=0 NormalX=0 NormalY=0 NormalZ=1 AngleXU=0 Radius=1
    g2: Circle CenterX=8 CenterY=6 CenterZ=0 NormalX=0 NormalY=0 NormalZ=1 AngleXU=0 Radius=1
    g3: BSplineCurve PolesCount=3 KnotsCount=2 Degree=2 IsPeriodic=0
    g4: GeomPoint X=0 Y=0 Z=0
    g5: GeomPoint X=8 Y=6 Z=0
    g6: LineSegment StartX=0 StartY=6 StartZ=0 EndX=8 EndY=6 EndZ=0
  constraints (14):
    c: Coincident(g0,g-1)
    c: Distance(g0) = 6
    c: Vertical(g0)
    c: Coincident(g3,g0)
    c: Weight(g1) = 1
    c: Equal(g1,g2)
    c: InternalAlignment(g1,g3)
    c: InternalAlignment(g2,g3)
    c: InternalAlignment(g4,g3)
    c: InternalAlignment(g5,g3)
    c: Block(g3)
    c: Coincident(g6,g0)
    c: Coincident(g6,g3)
    c: Horizontal(g6)
FEATURE [Part::Extrusion] Extrude035  label="caseScrewPillarBracket013"
  Base = -> Sketch044
  Dir = (0,0,1)
  DirMode = 2
  FaceMakerClass = Part::FaceMakerBullseye
  LengthFwd = 2.4
  LengthRev = 0
  Placement = pos=(90.7,29,6.77) rot=(0,-1,0;1.5708rad)
  Solid = true
  Symmetric = false
FEATURE [Sketcher::SketchObject] Sketch045
  FullyConstrained = true
  sketch-geometry (7):
    g0: LineSegment StartX=0 StartY=0 StartZ=0 EndX=0 EndY=6 EndZ=0
    g1: Circle CenterX=0 CenterY=0 CenterZ=0 NormalX=0 NormalY=0 NormalZ=1 AngleXU=0 Radius=1
    g2: Circle CenterX=8 CenterY=6 CenterZ=0 NormalX=0 NormalY=0 NormalZ=1 AngleXU=0 Radius=1
    g3: BSplineCurve PolesCount=3 KnotsCount=2 Degree=2 IsPeriodic=0
    g4: GeomPoint X=0 Y=0 Z=0
    g5: GeomPoint X=8 Y=6 Z=0
    g6: LineSegment StartX=0 StartY=6 StartZ=0 EndX=8 EndY=6 EndZ=0
  constraints (14):
    c: Coincident(g0,g-1)
    c: Distance(g0) = 6
    c: Vertical(g0)
    c: Coincident(g3,g0)
    c: Weight(g1) = 1
    c: Equal(g1,g2)
    c: InternalAlignment(g1,g3)
    c: InternalAlignment(g2,g3)
    c: InternalAlignment(g4,g3)
    c: InternalAlignment(g5,g3)
    c: Block(g3)
    c: Coincident(g6,g0)
    c: Coincident(g6,g3)
    c: Horizontal(g6)
FEATURE [Sketcher::SketchObject] Sketch046
  FullyConstrained = true
  sketch-geometry (7):
    g0: LineSegment StartX=0 StartY=0 StartZ=0 EndX=0 EndY=6 EndZ=0
    g1: Circle CenterX=0 CenterY=0 CenterZ=0 NormalX=0 NormalY=0 NormalZ=1 AngleXU=0 Radius=1
    g2: Circle CenterX=8 CenterY=6 CenterZ=0 NormalX=0 NormalY=0 NormalZ=1 AngleXU=0 Radius=1
    g3: BSplineCurve PolesCount=3 KnotsCount=2 Degree=2 IsPeriodic=0
    g4: GeomPoint X=0 Y=0 Z=0
    g5: GeomPoint X=8 Y=6 Z=0
    g6: LineSegment StartX=0 StartY=6 StartZ=0 EndX=8 EndY=6 EndZ=0
  constraints (14):
    c: Coincident(g0,g-1)
    c: Distance(g0) = 6
    c: Vertical(g0)
    c: Coincident(g3,g0)
    c: Weight(g1) = 1
    c: Equal(g1,g2)
    c: InternalAlignment(g1,g3)
    c: InternalAlignment(g2,g3)
    c: InternalAlignment(g4,g3)
    c: InternalAlignment(g5,g3)
    c: Block(g3)
    c: Coincident(g6,g0)
    c: Coincident(g6,g3)
    c: Horizontal(g6)
FEATURE [Part::Extrusion] Extrude036  label="caseScrewPillarBracket014"
  Base = -> Sketch045
  Dir = (0,0,1)
  DirMode = 2
  FaceMakerClass = Part::FaceMakerBullseye
  LengthFwd = 2.4
  LengthRev = 0
  Placement = pos=(110.7,29,6.77) rot=(0,-1,0;1.5708rad)
  Solid = true
  Symmetric = false
FEATURE [Part::Extrusion] Extrude037  label="caseScrewPillarBracket015"
  Base = -> Sketch046
  Dir = (0,0,1)
  DirMode = 2
  FaceMakerClass = Part::FaceMakerBullseye
  LengthFwd = 2.4
  LengthRev = 0
  Placement = pos=(108.3,29,65.23) rot=(0,1,0;1.5708rad)
  Solid = true
  Symmetric = false
FEATURE [Part::Box] Box013  label="frontCaseScrewPillarBracket002"
  AttacherType = Attacher::AttachEngine3D
  Height = 2.4
  Length = 22
  Placement = pos=(87,28,2.3) rot=(0,0,1;0rad)
  Width = 7
FEATURE [Part::Box] Box014  label="frontCaseScrewPillarBracket003"
  AttacherType = Attacher::AttachEngine3D
  Height = 2.4
  Length = 22
  Placement = pos=(87,28,67.3) rot=(0,0,1;0rad)
  Width = 7
FEATURE [Part::Feature] Face087
  shape: bbox 4.8 x 30.2 x 2e-07 mm, 1 faces, 0 solids (baked)
FEATURE [Part::Revolution] Revolve091  label="frontCaseScrewPost004"
  Angle = 360
  Axis = (0,1,0)
  Base = (0,0,0)
  FaceMakerClass = Part::FaceMakerBullseye
  Placement = pos=(89.5,4.5,3.5) rot=(0,0,1;0rad)
  Solid = false
  Source = -> Face087
  Symmetric = false
FEATURE [Part::Feature] Face088
  shape: bbox 4.8 x 30.2 x 2e-07 mm, 1 faces, 0 solids (baked)
FEATURE [Part::Revolution] Revolve092  label="frontCaseScrewPost005"
  Angle = 360
  Axis = (0,1,0)
  Base = (0,0,0)
  FaceMakerClass = Part::FaceMakerBullseye
  Placement = pos=(89.5,4.5,68.5) rot=(0,0,1;0rad)
  Solid = false
  Source = -> Face088
  Symmetric = false
FEATURE [Part::Feature] Face089
  shape: bbox 3.5 x 30.2 x 2e-07 mm, 1 faces, 0 solids (baked)
FEATURE [Part::Revolution] Revolve093  label="backCaseScrewPost002"
  Angle = 360
  Axis = (0,1,0)
  Base = (0,0,0)
  FaceMakerClass = Part::FaceMakerBullseye
  Placement = pos=(12.5,4.5,10) rot=(0,0,1;0rad)
  Solid = false
  Source = -> Face089
  Symmetric = false
FEATURE [Part::Feature] Face090
  shape: bbox 3.5 x 30.2 x 2e-07 mm, 1 faces, 0 solids (baked)
FEATURE [Part::Revolution] Revolve094  label="backCaseScrewPost003"
  Angle = 360
  Axis = (0,1,0)
  Base = (0,0,0)
  FaceMakerClass = Part::FaceMakerBullseye
  Placement = pos=(12.5,4.5,62) rot=(0,0,1;0rad)
  Solid = false
  Source = -> Face090
  Symmetric = false
FEATURE [Part::Box] Box015  label="Cube011"
  AttacherType = Attacher::AttachEngine3D
  Height = 28.8
  Length = 3
  Placement = pos=(107.3,28,21.6) rot=(0,0,1;0rad)
  Width = 7
FEATURE [Part::Box] Box016  label="Cube012"
  AttacherType = Attacher::AttachEngine3D
  Height = 3
  Length = 7.4
  Placement = pos=(107.3,28,18.6) rot=(0,0,1;0rad)
  Width = 7
FEATURE [Part::Box] Box017  label="Cube013"
  AttacherType = Attacher::AttachEngine3D
  Height = 3
  Length = 7.4
  Placement = pos=(107.3,28,50.4) rot=(0,0,1;0rad)
  Width = 7
FEATURE [Part::Cylinder] Cylinder024
  Angle = 360
  AttacherType = Attacher::AttachEngine3D
  Height = 20
  Placement = pos=(0,0,36.15) rot=(0,0,1;0rad)
  Radius = 14.3
FEATURE [Part::Cylinder] Cylinder025
  Angle = 360
  AttacherType = Attacher::AttachEngine3D
  Height = 10
  Placement = pos=(0,0,36.15) rot=(0,0,1;0rad)
  Radius = 4
FEATURE [Part::MultiFuse] Fusion066  label="removeToCreteHoleForPlugHousing009"
  Placement = pos=(70,19,36) rot=(0,1,0;1.5708rad)
  Shapes = -> [Cylinder024,Cylinder025]
FEATURE [Part::MultiFuse] Fusion065  label="plugHousingBracketHolder002"
  Shapes = -> [Box017,Box015,Box016]
FEATURE [Part::Cut] Cut025  label="plugHousingBracketHolder003"
  Base = -> Fusion065
  Placement = pos=(7,0,0) rot=(0,0,1;0rad)
  Tool = -> Fusion066
FEATURE [Sketcher::SketchObject] Sketch047
  FullyConstrained = false
  Placement = pos=(0,0,0) rot=(1,0,0;1.5708rad)
  sketch-geometry (24):
    g0: ArcOfCircle CenterX=-4 CenterY=-10.5 CenterZ=0 NormalX=0 NormalY=0 NormalZ=1 AngleXU=0 Radius=1.5 StartAngle=6e-16 EndAngle=3.14159
    g1: ArcOfCircle CenterX=-34.2 CenterY=-10.5 CenterZ=0 NormalX=0 NormalY=0 NormalZ=1 AngleXU=0 Radius=1.5 StartAngle=0 EndAngle=3.14159
    g2: ArcOfCircle CenterX=-34.2 CenterY=-27.7 CenterZ=0 NormalX=0 NormalY=0 NormalZ=1 AngleXU=0 Radius=1.5 StartAngle=3.14159 EndAngle=6.28319
    g3: ArcOfCircle CenterX=-4 CenterY=-27.7 CenterZ=0 NormalX=0 NormalY=0 NormalZ=1 AngleXU=0 Radius=1.5 StartAngle=3.1416 EndAngle=6.28319
    g4: ArcOfCircle CenterX=-10 CenterY=-4.3 CenterZ=0 NormalX=0 NormalY=0 NormalZ=1 AngleXU=0 Radius=1.5 StartAngle=2e-16 EndAngle=3.14159
    g5: ArcOfCircle CenterX=-16.1 CenterY=-1.8 CenterZ=0 NormalX=0 NormalY=0 NormalZ=1 AngleXU=0 Radius=1.5 StartAngle=5e-16 EndAngle=3.14159
    g6: ArcOfCircle CenterX=-22.1 CenterY=-1.8 CenterZ=0 NormalX=0 NormalY=0 NormalZ=1 AngleXU=0 Radius=1.5 StartAngle=5e-16 EndAngle=3.14159
    g7: ArcOfCircle CenterX=-28.2 CenterY=-4.3 CenterZ=0 NormalX=0 NormalY=0 NormalZ=1 AngleXU=0 Radius=1.5 StartAngle=2e-16 EndAngle=3.14159
    g8: ArcOfCircle CenterX=-10 CenterY=-33.9 CenterZ=0 NormalX=0 NormalY=0 NormalZ=1 AngleXU=0 Radius=1.5 StartAngle=3.14159 EndAngle=6.28319
    g9: ArcOfCircle CenterX=-16.1 CenterY=-36.4 CenterZ=0 NormalX=0 NormalY=0 NormalZ=1 AngleXU=0 Radius=1.5 StartAngle=3.14159 EndAngle=6.28319
    g10: ArcOfCircle CenterX=-22.1 CenterY=-36.4 CenterZ=0 NormalX=0 NormalY=0 NormalZ=1 AngleXU=0 Radius=1.5 StartAngle=3.14159 EndAngle=6.28319
    g11: ArcOfCircle CenterX=-28.2 CenterY=-33.9 CenterZ=0 NormalX=0 NormalY=0 NormalZ=1 AngleXU=0 Radius=1.5 StartAngle=3.14159 EndAngle=6.28319
    g12: LineSegment StartX=-35.7 StartY=-10.5 StartZ=0 EndX=-35.7 EndY=-27.7 EndZ=0
    g13: LineSegment StartX=-32.7 StartY=-10.5 StartZ=0 EndX=-32.7 EndY=-27.7 EndZ=0
    g14: LineSegment StartX=-29.7 StartY=-33.9 StartZ=0 EndX=-29.7 EndY=-4.3 EndZ=0
    g15: LineSegment StartX=-26.7 StartY=-33.9 StartZ=0 EndX=-26.7 EndY=-4.3 EndZ=0
    g16: LineSegment StartX=-2.5 StartY=-10.5 StartZ=0 EndX=-2.5 EndY=-27.7 EndZ=0
    g17: LineSegment StartX=-8.5 StartY=-4.3 StartZ=0 EndX=-8.5 EndY=-33.9 EndZ=0
    g18: LineSegment StartX=-5.5 StartY=-10.5 StartZ=0 EndX=-5.5 EndY=-27.7 EndZ=0
    g19: LineSegment StartX=-11.5 StartY=-4.3 StartZ=0 EndX=-11.5 EndY=-33.9 EndZ=0
    g20: LineSegment StartX=-14.6 StartY=-1.8 StartZ=0 EndX=-14.6 EndY=-36.4 EndZ=0
    g21: LineSegment StartX=-17.6 StartY=-1.8 StartZ=0 EndX=-17.6 EndY=-36.4 EndZ=0
    g22: LineSegment StartX=-20.6 StartY=-36.4 StartZ=0 EndX=-20.6 EndY=-1.8 EndZ=0
    g23: LineSegment StartX=-23.6 StartY=-1.8 StartZ=0 EndX=-23.6 EndY=-36.4 EndZ=0
  constraints (48):
    c: Block(g0)
    c: Block(g1)
    c: Block(g2)
    c: Block(g3)
    c: Block(g4)
    c: Block(g5)
    c: Block(g6)
    c: Block(g7)
    c: Block(g8)
    c: Block(g9)
    c: Block(g10)
    c: Block(g11)
    c: Coincident(g12,g1)
    c: Coincident(g12,g2)
    c: Vertical(g12)
    c: Coincident(g13,g1)
    c: Coincident(g13,g2)
    c: Vertical(g13)
    c: Coincident(g14,g11)
    c: Coincident(g14,g7)
    c: Vertical(g14)
    c: Coincident(g15,g11)
    c: Coincident(g15,g7)
    c: Vertical(g15)
    c: Coincident(g16,g0)
    c: Coincident(g16,g3)
    c: Vertical(g16)
    c: Coincident(g17,g4)
    c: Coincident(g17,g8)
    c: Vertical(g17)
    c: Coincident(g18,g0)
    c: Coincident(g18,g3)
    c: Vertical(g18)
    c: Coincident(g19,g4)
    c: Coincident(g19,g8)
    c: Vertical(g19)
    c: Coincident(g20,g5)
    c: Coincident(g20,g9)
    c: Vertical(g20)
    c: Coincident(g21,g5)
    c: Coincident(g21,g9)
    c: Vertical(g21)
    c: Coincident(g22,g10)
    c: Coincident(g22,g6)
    c: Vertical(g22)
    c: Coincident(g23,g6)
    c: Coincident(g23,g10)
    c: Vertical(g23)
FEATURE [Part::Extrusion] Extrude038  label="removeToCreateFanGrillHoles001"
  Base = -> Sketch047
  Dir = (0,-1,6e-16)
  DirMode = 2
  FaceMakerClass = Part::FaceMakerBullseye
  LengthFwd = 10
  LengthRev = 0
  Placement = pos=(65.4,44,54.82) rot=(0,0,1;0rad)
  Solid = true
  Symmetric = false
FEATURE [Part::Feature] Wire004
  shape: bbox 11 x 5.2 x 2e-07 mm, 0 faces, 0 solids (baked)
FEATURE [Part::Revolution] Revolve095
  Angle = 360
  Axis = (0,1,0)
  Base = (0,0,0)
  FaceMakerClass = Part::FaceMakerBullseye
  Placement = pos=(30.3,38,19.7) rot=(0,0,1;0rad)
  Solid = true
  Source = -> Wire004
  Symmetric = false
FEATURE [Part::Feature] Wire005
  shape: bbox 11 x 5.2 x 2e-07 mm, 0 faces, 0 solids (baked)
FEATURE [Part::Revolution] Revolve096
  Angle = 360
  Axis = (0,1,0)
  Base = (0,0,0)
  FaceMakerClass = Part::FaceMakerBullseye
  Placement = pos=(30.3,38,51.7) rot=(0,0,1;0rad)
  Solid = true
  Source = -> Wire005
  Symmetric = false
FEATURE [Part::Feature] Wire006
  shape: bbox 11 x 5.2 x 2e-07 mm, 0 faces, 0 solids (baked)
FEATURE [Part::Revolution] Revolve097
  Angle = 360
  Axis = (0,1,0)
  Base = (0,0,0)
  FaceMakerClass = Part::FaceMakerBullseye
  Placement = pos=(62.3,38,51.7) rot=(0,0,1;0rad)
  Solid = true
  Source = -> Wire006
  Symmetric = false
FEATURE [Part::Feature] Wire007
  shape: bbox 11 x 5.2 x 2e-07 mm, 0 faces, 0 solids (baked)
FEATURE [Part::Revolution] Revolve098
  Angle = 360
  Axis = (0,1,0)
  Base = (0,0,0)
  FaceMakerClass = Part::FaceMakerBullseye
  Placement = pos=(62.3,38,19.7) rot=(0,0,1;0rad)
  Solid = true
  Source = -> Wire007
  Symmetric = false
FEATURE [Part::MultiFuse] Fusion067  label="fanScrewHousing002"
  Shapes = -> [Revolve098,Revolve097,Revolve096,Revolve095]
FEATURE [Part::Feature] Face091 .. Face094  x4 (patterned run collapsed; names and placements below)
  shape: bbox 3.5 x 17.8 x 2e-07 mm, 1 faces, 0 solids (baked)
FEATURE [Part::Revolution] Revolve099  label="removeToCreateScrewAndThreadedInsertHole026"
  Angle = 360
  Axis = (0,1,0)
  Base = (0,0,0)
  FaceMakerClass = Part::FaceMakerBullseye
  Placement = pos=(62.3,30.3,19.7) rot=(0,0,1;0rad)
  Solid = false
  Source = -> Face091
  Symmetric = false
FEATURE [Part::Revolution] Revolve100  label="removeToCreateScrewAndThreadedInsertHole027"
  Angle = 360
  Axis = (0,1,0)
  Base = (0,0,0)
  FaceMakerClass = Part::FaceMakerBullseye
  Placement = pos=(62.3,30.3,51.7) rot=(0,0,1;0rad)
  Solid = false
  Source = -> Face092
  Symmetric = false
FEATURE [Part::Revolution] Revolve101  label="removeToCreateScrewAndThreadedInsertHole028"
  Angle = 360
  Axis = (0,1,0)
  Base = (0,0,0)
  FaceMakerClass = Part::FaceMakerBullseye
  Placement = pos=(30.3,30.3,19.7) rot=(0,0,1;0rad)
  Solid = false
  Source = -> Face093
  Symmetric = false
FEATURE [Part::Revolution] Revolve102  label="removeToCreateScrewAndThreadedInsertHole029"
  Angle = 360
  Axis = (0,1,0)
  Base = (0,0,0)
  FaceMakerClass = Part::FaceMakerBullseye
  Placement = pos=(30.3,30.3,51.7) rot=(0,0,1;0rad)
  Solid = false
  Source = -> Face094
  Symmetric = false
FEATURE [Part::MultiFuse] Fusion068  label="createThreadedInsertHolesForFan002"
  Shapes = -> [Revolve099,Revolve100,Revolve101,Revolve102]
FEATURE [Part::Cut] Cut026  label="fanScrewHousing003"
  Base = -> Fusion067
  Tool = -> Fusion068
FEATURE [Sketcher::SketchObject] Sketch048
  FullyConstrained = false
  Placement = pos=(0,0,0) rot=(1,0,0;1.5708rad)
  sketch-geometry (24):
    g0: ArcOfCircle CenterX=-4 CenterY=-10.5 CenterZ=0 NormalX=0 NormalY=0 NormalZ=1 AngleXU=0 Radius=1.5 StartAngle=6e-16 EndAngle=3.14159
    g1: ArcOfCircle CenterX=-34.2 CenterY=-10.5 CenterZ=0 NormalX=0 NormalY=0 NormalZ=1 AngleXU=0 Radius=1.5 StartAngle=0 EndAngle=3.14159
    g2: ArcOfCircle CenterX=-34.2 CenterY=-27.7 CenterZ=0 NormalX=0 NormalY=0 NormalZ=1 AngleXU=0 Radius=1.5 StartAngle=3.14159 EndAngle=6.28319
    g3: ArcOfCircle CenterX=-4 CenterY=-27.7 CenterZ=0 NormalX=0 NormalY=0 NormalZ=1 AngleXU=0 Radius=1.5 StartAngle=3.1416 EndAngle=6.28319
    g4: ArcOfCircle CenterX=-10 CenterY=-4.3 CenterZ=0 NormalX=0 NormalY=0 NormalZ=1 AngleXU=0 Radius=1.5 StartAngle=2e-16 EndAngle=3.14159
    g5: ArcOfCircle CenterX=-16.1 CenterY=-1.8 CenterZ=0 NormalX=0 NormalY=0 NormalZ=1 AngleXU=0 Radius=1.5 StartAngle=5e-16 EndAngle=3.14159
    g6: ArcOfCircle CenterX=-22.1 CenterY=-1.8 CenterZ=0 NormalX=0 NormalY=0 NormalZ=1 AngleXU=0 Radius=1.5 StartAngle=5e-16 EndAngle=3.14159
    g7: ArcOfCircle CenterX=-28.2 CenterY=-4.3 CenterZ=0 NormalX=0 NormalY=0 NormalZ=1 AngleXU=0 Radius=1.5 StartAngle=2e-16 EndAngle=3.14159
    g8: ArcOfCircle CenterX=-10 CenterY=-33.9 CenterZ=0 NormalX=0 NormalY=0 NormalZ=1 AngleXU=0 Radius=1.5 StartAngle=3.14159 EndAngle=6.28319
    g9: ArcOfCircle CenterX=-16.1 CenterY=-36.4 CenterZ=0 NormalX=0 NormalY=0 NormalZ=1 AngleXU=0 Radius=1.5 StartAngle=3.14159 EndAngle=6.28319
    g10: ArcOfCircle CenterX=-22.1 CenterY=-36.4 CenterZ=0 NormalX=0 NormalY=0 NormalZ=1 AngleXU=0 Radius=1.5 StartAngle=3.14159 EndAngle=6.28319
    g11: ArcOfCircle CenterX=-28.2 CenterY=-33.9 CenterZ=0 NormalX=0 NormalY=0 NormalZ=1 AngleXU=0 Radius=1.5 StartAngle=3.14159 EndAngle=6.28319
    g12: LineSegment StartX=-35.7 StartY=-10.5 StartZ=0 EndX=-35.7 EndY=-27.7 EndZ=0
    g13: LineSegment StartX=-32.7 StartY=-10.5 StartZ=0 EndX=-32.7 EndY=-27.7 EndZ=0
    g14: LineSegment StartX=-29.7 StartY=-33.9 StartZ=0 EndX=-29.7 EndY=-4.3 EndZ=0
    g15: LineSegment StartX=-26.7 StartY=-33.9 StartZ=0 EndX=-26.7 EndY=-4.3 EndZ=0
    g16: LineSegment StartX=-2.5 StartY=-10.5 StartZ=0 EndX=-2.5 EndY=-27.7 EndZ=0
    g17: LineSegment StartX=-8.5 StartY=-4.3 StartZ=0 EndX=-8.5 EndY=-33.9 EndZ=0
    g18: LineSegment StartX=-5.5 StartY=-10.5 StartZ=0 EndX=-5.5 EndY=-27.7 EndZ=0
    g19: LineSegment StartX=-11.5 StartY=-4.3 StartZ=0 EndX=-11.5 EndY=-33.9 EndZ=0
    g20: LineSegment StartX=-14.6 StartY=-1.8 StartZ=0 EndX=-14.6 EndY=-36.4 EndZ=0
    g21: LineSegment StartX=-17.6 StartY=-1.8 StartZ=0 EndX=-17.6 EndY=-36.4 EndZ=0
    g22: LineSegment StartX=-20.6 StartY=-36.4 StartZ=0 EndX=-20.6 EndY=-1.8 EndZ=0
    g23: LineSegment StartX=-23.6 StartY=-1.8 StartZ=0 EndX=-23.6 EndY=-36.4 EndZ=0
  constraints (48):
    c: Block(g0)
    c: Block(g1)
    c: Block(g2)
    c: Block(g3)
    c: Block(g4)
    c: Block(g5)
    c: Block(g6)
    c: Block(g7)
    c: Block(g8)
    c: Block(g9)
    c: Block(g10)
    c: Block(g11)
    c: Coincident(g12,g1)
    c: Coincident(g12,g2)
    c: Vertical(g12)
    c: Coincident(g13,g1)
    c: Coincident(g13,g2)
    c: Vertical(g13)
    c: Coincident(g14,g11)
    c: Coincident(g14,g7)
    c: Vertical(g14)
    c: Coincident(g15,g11)
    c: Coincident(g15,g7)
    c: Vertical(g15)
    c: Coincident(g16,g0)
    c: Coincident(g16,g3)
    c: Vertical(g16)
    c: Coincident(g17,g4)
    c: Coincident(g17,g8)
    c: Vertical(g17)
    c: Coincident(g18,g0)
    c: Coincident(g18,g3)
    c: Vertical(g18)
    c: Coincident(g19,g4)
    c: Coincident(g19,g8)
    c: Vertical(g19)
    c: Coincident(g20,g5)
    c: Coincident(g20,g9)
    c: Vertical(g20)
    c: Coincident(g21,g5)
    c: Coincident(g21,g9)
    c: Vertical(g21)
    c: Coincident(g22,g10)
    c: Coincident(g22,g6)
    c: Vertical(g22)
    c: Coincident(g23,g6)
    c: Coincident(g23,g10)
    c: Vertical(g23)
FEATURE [Part::Extrusion] Extrude039  label="removeToCreateFanGrillHoles002"
  Base = -> Sketch048
  Dir = (0,-1,6e-16)
  DirMode = 2
  FaceMakerClass = Part::FaceMakerBullseye
  LengthFwd = 10
  LengthRev = 0
  Placement = pos=(65.4,44,54.82) rot=(0,0,1;0rad)
  Solid = true
  Symmetric = false
FEATURE [Part::Cut] Cut027  label="fanScrewHousing004"
  Base = -> Cut026
  Tool = -> Extrude038
FEATURE [Part::Cut] Cut028  label="top014"
  Base = -> Fillet026
  Tool = -> Extrude039
FEATURE [Part::Feature] Face095 .. Face098  x4 (patterned run collapsed; names and placements below)
  shape: bbox 3.5 x 17.8 x 2e-07 mm, 1 faces, 0 solids (baked)
FEATURE [Part::Revolution] Revolve103  label="removeToCreateScrewAndThreadedInsertHole030"
  Angle = 360
  Axis = (0,1,0)
  Base = (0,0,0)
  FaceMakerClass = Part::FaceMakerBullseye
  Placement = pos=(62.3,30.3,19.7) rot=(0,0,1;0rad)
  Solid = false
  Source = -> Face095
  Symmetric = false
FEATURE [Part::Revolution] Revolve104  label="removeToCreateScrewAndThreadedInsertHole031"
  Angle = 360
  Axis = (0,1,0)
  Base = (0,0,0)
  FaceMakerClass = Part::FaceMakerBullseye
  Placement = pos=(62.3,30.3,51.7) rot=(0,0,1;0rad)
  Solid = false
  Source = -> Face096
  Symmetric = false
FEATURE [Part::Revolution] Revolve105  label="removeToCreateScrewAndThreadedInsertHole032"
  Angle = 360
  Axis = (0,1,0)
  Base = (0,0,0)
  FaceMakerClass = Part::FaceMakerBullseye
  Placement = pos=(30.3,30.3,19.7) rot=(0,0,1;0rad)
  Solid = false
  Source = -> Face097
  Symmetric = false
FEATURE [Part::Revolution] Revolve106  label="removeToCreateScrewAndThreadedInsertHole033"
  Angle = 360
  Axis = (0,1,0)
  Base = (0,0,0)
  FaceMakerClass = Part::FaceMakerBullseye
  Placement = pos=(30.3,30.3,51.7) rot=(0,0,1;0rad)
  Solid = false
  Source = -> Face098
  Symmetric = false
FEATURE [Part::MultiFuse] Fusion069  label="createThreadedInsertHolesForFan003"
  Shapes = -> [Revolve103,Revolve104,Revolve105,Revolve106]
FEATURE [Part::Cut] Cut029  label="top015"
  Base = -> Cut028
  Tool = -> Fusion054
FEATURE [Part::Cut] Cut030  label="fanScrewHousing005"
  Base = -> Cut027
  Tool = -> Fusion069
FEATURE [Part::Cylinder] Cylinder026  label="removeToCreteHoleForPlugHousing010"
  Angle = 360
  AttacherType = Attacher::AttachEngine3D
  Height = 20
  Placement = pos=(-2,19,36) rot=(0,1,0;1.5708rad)
  Radius = 14.3
FEATURE [Part::Box] Box018  label="removeToCreteHoleForPlugHousing011"
  AttacherType = Attacher::AttachEngine3D
  Height = 28.6
  Length = 10
  Placement = pos=(-2,0,21.7) rot=(0,0,1;0rad)
  Width = 19
FEATURE [Part::Box] Box019  label="wireHolderBottomCaseBit"
  AttacherType = Attacher::AttachEngine3D
  Height = 28
  Length = 3
  Placement = pos=(0,0,22) rot=(0,0,1;0rad)
  Width = 21
FEATURE [Part::Cylinder] Cylinder027  label="removeToCreteHoleForPlugHousing012"
  Angle = 360
  AttacherType = Attacher::AttachEngine3D
  Height = 20
  Placement = pos=(-2,19,36) rot=(0,1,0;1.5708rad)
  Radius = 14.3
FEATURE [Part::Cut] Cut031  label="wireHolderBottomCaseBit001"
  Base = -> Box019
  Tool = -> Cylinder027
FEATURE [Part::MultiFuse] Fusion070  label="removeToCreteHoleForPlugHousing013"
  Shapes = -> [Box018,Cylinder026]
FEATURE [Part::Cut] Cut032  label="top016"
  Base = -> Cut029
  Tool = -> Fusion070
FEATURE [Part::Cylinder] Cylinder028
  Angle = 360
  AttacherType = Attacher::AttachEngine3D
  Height = 20
  Placement = pos=(0,0,36.15) rot=(0,0,1;0rad)
  Radius = 14.3
FEATURE [Part::Cylinder] Cylinder029
  Angle = 360
  AttacherType = Attacher::AttachEngine3D
  Height = 10
  Placement = pos=(0,0,36.15) rot=(0,0,1;0rad)
  Radius = 4
FEATURE [Part::MultiFuse] Fusion071  label="removeToCreteHoleForPlugHousing014"
  Placement = pos=(70,19,36) rot=(0,1,0;1.5708rad)
  Shapes = -> [Cylinder028,Cylinder029]
FEATURE [Sketcher::SketchObject] Sketch049  label="topSketch011"
  FullyConstrained = true
  sketch-geometry (4):
    g0: ArcOfCircle CenterX=105 CenterY=19 CenterZ=0 NormalX=0 NormalY=0 NormalZ=1 AngleXU=0 Radius=20.6155 StartAngle=5.54125 EndAngle=6.28319
    g1: ArcOfCircle CenterX=105 CenterY=19 CenterZ=0 NormalX=0 NormalY=0 NormalZ=1 AngleXU=0 Radius=13 StartAngle=5.54125 EndAngle=6.28319
    g2: LineSegment StartX=118 StartY=19 StartZ=0 EndX=125.616 EndY=19 EndZ=0
    g3: LineSegment StartX=114.583 StartY=10.2157 StartZ=0 EndX=120.197 EndY=5.06982 EndZ=0
  constraints (7):
    c: Block(g0)
    c: Block(g1)
    c: Coincident(g2,g1)
    c: Coincident(g2,g0)
    c: Horizontal(g2)
    c: Coincident(g3,g1)
    c: Coincident(g3,g0)
FEATURE [Part::Box] Box020  label="removeToCreteHoleForPlugHousing015"
  AttacherType = Attacher::AttachEngine3D
  Height = 28.6
  Length = 20
  Placement = pos=(106.15,0,21.7) rot=(0,0,1;0rad)
  Width = 19
FEATURE [Part::MultiFuse] Fusion072  label="removeToCreteHoleForPlugHousing016"
  Shapes = -> [Box020,Fusion071]
FEATURE [Part::Cut] Cut033  label="removeToCreteHoleForPlugHousing017"
  Base = -> Cut032
  Tool = -> Fusion072
FEATURE [Part::Cylinder] Cylinder030
  Angle = 360
  AttacherType = Attacher::AttachEngine3D
  Height = 20
  Placement = pos=(0,0,36.15) rot=(0,0,1;0rad)
  Radius = 14.3
FEATURE [Part::Cylinder] Cylinder031
  Angle = 360
  AttacherType = Attacher::AttachEngine3D
  Height = 10
  Placement = pos=(0,0,36.15) rot=(0,0,1;0rad)
  Radius = 4
FEATURE [Part::Box] Box021  label="removeToCreteHoleForPlugHousing019"
  AttacherType = Attacher::AttachEngine3D
  Height = 28.6
  Length = 20
  Placement = pos=(106.15,0,21.7) rot=(0,0,1;0rad)
  Width = 19
FEATURE [Part::MultiFuse] Fusion074  label="removeToCreteHoleForPlugHousing020"
  Placement = pos=(70,19,36) rot=(0,1,0;1.5708rad)
  Shapes = -> [Cylinder030,Cylinder031]
FEATURE [Part::MultiFuse] Fusion073  label="removeToCreteHoleForPlugHousing018"
  Placement = pos=(0,0,28.3) rot=(0,0,1;0rad)
  Shapes = -> [Box021,Fusion074]
FEATURE [Part::Cylinder] Cylinder032
  Angle = 360
  AttacherType = Attacher::AttachEngine3D
  Height = 20
  Placement = pos=(0,0,36.15) rot=(0,0,1;0rad)
  Radius = 14.3
FEATURE [Part::Cylinder] Cylinder033
  Angle = 360
  AttacherType = Attacher::AttachEngine3D
  Height = 10
  Placement = pos=(0,0,36.15) rot=(0,0,1;0rad)
  Radius = 4
FEATURE [Part::Box] Box022  label="removeToCreteHoleForPlugHousing021"
  AttacherType = Attacher::AttachEngine3D
  Height = 28.6
  Length = 20
  Placement = pos=(106.15,0,21.7) rot=(0,0,1;0rad)
  Width = 19
FEATURE [Part::MultiFuse] Fusion076  label="removeToCreteHoleForPlugHousing023"
  Placement = pos=(70,19,36) rot=(0,1,0;1.5708rad)
  Shapes = -> [Cylinder032,Cylinder033]
FEATURE [Part::MultiFuse] Fusion075  label="removeToCreteHoleForPlugHousing022"
  Placement = pos=(0,0,-28.3) rot=(0,0,1;0rad)
  Shapes = -> [Box022,Fusion076]
FEATURE [Part::MultiFuse] Fusion077  label="removeToCreatePlugHousingBottomBit"
  Shapes = -> [Fusion075,Fusion073]
FEATURE [Part::Cylinder] Cylinder034
  Angle = 360
  AttacherType = Attacher::AttachEngine3D
  Height = 20
  Placement = pos=(0,0,36.15) rot=(0,0,1;0rad)
  Radius = 14
FEATURE [Part::Cylinder] Cylinder035
  Angle = 360
  AttacherType = Attacher::AttachEngine3D
  Height = 10
  Placement = pos=(0,0,36.15) rot=(0,0,1;0rad)
  Radius = 4
FEATURE [Part::MultiFuse] Fusion078  label="removeToCreteHoleForPlugHousing024"
  Placement = pos=(70,19,36) rot=(0,1,0;1.5708rad)
  Shapes = -> [Cylinder034,Cylinder035]
FEATURE [Part::MultiFuse] Fusion079  label="removeToCreatePlugHousingBottomBit001"
  Shapes = -> [Fusion078,Fusion077]
FEATURE [Part::Extrusion] Extrude040  label="bottomPlugHousingBit"
  Base = -> Sketch049
  Dir = (0,0,1)
  DirMode = 2
  FaceMakerClass = Part::FaceMakerBullseye
  LengthFwd = 72
  LengthRev = 0
  Solid = true
  Symmetric = false
FEATURE [Part::Cut] Cut034  label="bottomPlugHousingBit001"
  Base = -> Extrude040
  Placement = pos=(-0.09,0,0) rot=(0,0,1;0rad)
  Tool = -> Fusion079
FEATURE [Part::Box] Box023  label="Cube014"
  AttacherType = Attacher::AttachEngine3D
  Height = 16
  Length = 8
  Placement = pos=(12.7,31.52,28) rot=(0,0,1;0rad)
  Width = 4
FEATURE [Part::Cylinder] Cylinder036
  Angle = 360
  AttacherType = Attacher::AttachEngine3D
  Height = 10
  Placement = pos=(0,0,36.15) rot=(0,0,1;0rad)
  Radius = 4
FEATURE [Part::Cylinder] Cylinder037
  Angle = 360
  AttacherType = Attacher::AttachEngine3D
  Height = 20
  Placement = pos=(0,0,36.15) rot=(0,0,1;0rad)
  Radius = 8.2
FEATURE [Part::MultiFuse] Fusion080  label="removeToCreteHoleForPlugHousing025"
  Placement = pos=(-42,19,36) rot=(0,1,0;1.5708rad)
  Shapes = -> [Cylinder037,Cylinder036]
FEATURE [Sketcher::SketchObject] Sketch050  label="topSketch012"
  FullyConstrained = true
  sketch-geometry (4):
    g0: LineSegment StartX=16.8446 StartY=31.512 StartZ=0 EndX=16.3251 EndY=34.4666 EndZ=0
    g1: ArcOfCircle CenterX=19 CenterY=19.2524 CenterZ=0 NormalX=0 NormalY=0 NormalZ=1 AngleXU=0 Radius=15.4476 StartAngle=1.74483 EndAngle=2.72717
    g2: ArcOfCircle CenterX=19 CenterY=19.2524 CenterZ=0 NormalX=0 NormalY=0 NormalZ=1 AngleXU=0 Radius=12.4476 StartAngle=1.74483 EndAngle=2.73189
    g3: LineSegment StartX=4.86004 StartY=25.4725 StartZ=0 EndX=7.58253 EndY=24.2107 EndZ=0
  constraints (7):
    c: Block(g0)
    c: Coincident(g1,g0)
    c: Coincident(g2,g0)
    c: Coincident(g3,g1)
    c: Coincident(g3,g2)
    c: Block(g1)
    c: Block(g2)
FEATURE [Part::Extrusion] Extrude041
  Base = -> Sketch050
  Dir = (0,0,1)
  DirMode = 2
  FaceMakerClass = Part::FaceMakerBullseye
  LengthFwd = 10.6
  LengthRev = 0
  Placement = pos=(0,0,31) rot=(0,0,1;0rad)
  Solid = true
  Symmetric = false
FEATURE [Part::Cut] Cut035
  Base = -> Extrude041
  Placement = pos=(0,0,-0.3) rot=(0,0,1;0rad)
  Tool = -> Fusion080
FEATURE [Part::Cut] Cut036
  Base = -> Box023
  Tool = -> Cut035
FEATURE [Part::Fillet] Fillet027
  Base = -> Cut036
  Edges = 1 edges r=0.7: [Edge13]
FEATURE [Part::Fillet] Fillet028
  Base = -> Fillet027
  Edges = 1 edges r=0.7: [Edge13]
FEATURE [Part::Fillet] Fillet029
  Base = -> Fillet028
  Edges = 1 edges r=0.7: [Edge16]
FEATURE [Part::Fillet] Fillet030
  Base = -> Fillet029
  Edges = 1 edges r=0.7: [Edge11]
FEATURE [Part::Fillet] Fillet031
  Base = -> Fillet030
  Edges = 1 edges r=0.7: [Edge10]
FEATURE [Part::Fillet] Fillet032
  Base = -> Fillet031
  Edges = 1 edges r=1.2: [Edge5]
FEATURE [Part::Fillet] Fillet033
  Base = -> Fillet032
  Edges = 1 edges r=1.2: [Edge12]
FEATURE [Part::Fillet] Fillet034  label="wireHousingRetainer"
  Base = -> Fillet033
  Edges = 1 edges r=2: [Edge1]
  Placement = pos=(0.3,0,0) rot=(0,0,1;0rad)
FEATURE [Part::Feature] Face099
  shape: bbox 3.5 x 17.8 x 2e-07 mm, 1 faces, 0 solids (baked)
FEATURE [Part::Revolution] Revolve107  label="removeToCreateScrewAndThreadedInsertHole034"
  Angle = 360
  Axis = (0,1,0)
  Base = (0,0,0)
  FaceMakerClass = Part::FaceMakerBullseye
  Placement = pos=(12.5,0,10) rot=(0,0,1;0rad)
  Solid = false
  Source = -> Face099
  Symmetric = false
FEATURE [Part::Feature] Face100
  shape: bbox 3.5 x 17.8 x 2e-07 mm, 1 faces, 0 solids (baked)
FEATURE [Part::Revolution] Revolve108  label="removeToCreateScrewAndThreadedInsertHole035"
  Angle = 360
  Axis = (0,1,0)
  Base = (0,0,0)
  FaceMakerClass = Part::FaceMakerBullseye
  Placement = pos=(12.5,0,62) rot=(0,0,1;0rad)
  Solid = false
  Source = -> Face100
  Symmetric = false
FEATURE [Part::Feature] Face101
  shape: bbox 3.5 x 17.8 x 2e-07 mm, 1 faces, 0 solids (baked)
FEATURE [Part::Revolution] Revolve109  label="removeToCreateScrewAndThreadedInsertHole036"
  Angle = 360
  Axis = (0,1,0)
  Base = (0,0,0)
  FaceMakerClass = Part::FaceMakerBullseye
  Placement = pos=(89.5,0,68.5) rot=(0,0,1;0rad)
  Solid = false
  Source = -> Face101
  Symmetric = false
FEATURE [Part::Feature] Face102
  shape: bbox 3.5 x 17.8 x 2e-07 mm, 1 faces, 0 solids (baked)
FEATURE [Part::Revolution] Revolve110  label="removeToCreateScrewAndThreadedInsertHole037"
  Angle = 360
  Axis = (0,1,0)
  Base = (0,0,0)
  FaceMakerClass = Part::FaceMakerBullseye
  Placement = pos=(89.5,0,3.5) rot=(0,0,1;0rad)
  Solid = false
  Source = -> Face102
  Symmetric = false
FEATURE [Part::Feature] Face103
  shape: bbox 3.5 x 17.8 x 2e-07 mm, 1 faces, 0 solids (baked)
FEATURE [Part::Revolution] Revolve111  label="removeToCreateScrewAndThreadedInsertHole038"
  Angle = 360
  Axis = (0,1,0)
  Base = (0,0,0)
  FaceMakerClass = Part::FaceMakerBullseye
  Placement = pos=(109.5,4.7,3.5) rot=(0,0,1;0rad)
  Solid = false
  Source = -> Face103
  Symmetric = false
FEATURE [Part::Feature] Face104
  shape: bbox 3.5 x 17.8 x 2e-07 mm, 1 faces, 0 solids (baked)
FEATURE [Part::Revolution] Revolve112  label="removeToCreateScrewAndThreadedInsertHole039"
  Angle = 360
  Axis = (0,1,0)
  Base = (0,0,0)
  FaceMakerClass = Part::FaceMakerBullseye
  Placement = pos=(109.5,4.7,68.5) rot=(0,0,1;0rad)
  Solid = false
  Source = -> Face104
  Symmetric = false
FEATURE [Part::MultiFuse] Fusion081  label="removeToCreateScrewAndThreadedInsertHole040"
  Shapes = -> [Revolve107,Revolve108,Revolve109,Revolve110,Revolve111,Revolve112]
FEATURE [Part::MultiFuse] Fusion082  label="casePillars002"
  Shapes = -> [Revolve094,Revolve092,Revolve090,Revolve089,Revolve091,Revolve093]
FEATURE [Part::Cut] Cut037  label="casePillars003"
  Base = -> Fusion082
  Tool = -> Fusion081
FEATURE [Sketcher::SketchObject] Sketch051
  FullyConstrained = true
  Placement = pos=(117,19,0) rot=(0.57735,0.57735,0.57735;2.0944rad)
  sketch-geometry (48):
    g0: LineSegment StartX=-49.19 StartY=69.25 StartZ=0 EndX=-49.19 EndY=66.25 EndZ=0
    g1: LineSegment StartX=-49.19 StartY=63.5 StartZ=0 EndX=-49.19 EndY=60.5 EndZ=0
    g2: LineSegment StartX=-49.19 StartY=57.75 StartZ=0 EndX=-49.19 EndY=54.75 EndZ=0
    g3: LineSegment StartX=-49.19 StartY=52 StartZ=0 EndX=-49.19 EndY=49 EndZ=0
    g4: LineSegment StartX=-49.19 StartY=46.25 StartZ=0 EndX=-49.19 EndY=43.25 EndZ=0
    g5: LineSegment StartX=-49.19 StartY=40.5 StartZ=0 EndX=-49.19 EndY=37.5 EndZ=0
    g6: LineSegment StartX=-49.19 StartY=34.5 StartZ=0 EndX=-49.19 EndY=31.5 EndZ=0
    g7: LineSegment StartX=-49.19 StartY=28.75 StartZ=0 EndX=-49.19 EndY=25.75 EndZ=0
    g8: LineSegment StartX=-49.19 StartY=23 StartZ=0 EndX=-49.19 EndY=20 EndZ=0
    g9: LineSegment StartX=-49.19 StartY=17.25 StartZ=0 EndX=-49.19 EndY=14.25 EndZ=0
    g10: LineSegment StartX=-49.19 StartY=11.5 StartZ=0 EndX=-49.19 EndY=8.5 EndZ=0
    g11: LineSegment StartX=-49.19 StartY=5.75 StartZ=0 EndX=-49.19 EndY=2.75 EndZ=0
    g12: ArcOfCircle CenterX=-1.5 CenterY=67.75 CenterZ=0 NormalX=0 NormalY=0 NormalZ=1 AngleXU=0 Radius=1.5 StartAngle=4.71239 EndAngle=7.85398
    g13: ArcOfCircle CenterX=-1.5 CenterY=62 CenterZ=0 NormalX=0 NormalY=0 NormalZ=1 AngleXU=0 Radius=1.5 StartAngle=4.71239 EndAngle=7.85398
    g14: ArcOfCircle CenterX=-1.5 CenterY=56.25 CenterZ=0 NormalX=0 NormalY=0 NormalZ=1 AngleXU=0 Radius=1.5 StartAngle=4.71239 EndAngle=7.85398
    g15: ArcOfCircle CenterX=-11.49 CenterY=50.5 CenterZ=0 NormalX=0 NormalY=0 NormalZ=1 AngleXU=0 Radius=1.5 StartAngle=4.71239 EndAngle=7.85398
    g16: ArcOfCircle CenterX=-16.28 CenterY=44.75 CenterZ=0 NormalX=0 NormalY=0 NormalZ=1 AngleXU=0 Radius=1.5 StartAngle=4.71239 EndAngle=7.85398
    g17: ArcOfCircle CenterX=-18.2337 CenterY=39 CenterZ=0 NormalX=0 NormalY=0 NormalZ=1 AngleXU=0 Radius=1.5 StartAngle=4.71485 EndAngle=7.85398
    g18: ArcOfCircle CenterX=-16.2837 CenterY=27.25 CenterZ=0 NormalX=0 NormalY=0 NormalZ=1 AngleXU=0 Radius=1.5 StartAngle=4.71485 EndAngle=7.85398
    g19: ArcOfCircle CenterX=-18.2337 CenterY=33 CenterZ=0 NormalX=0 NormalY=0 NormalZ=1 AngleXU=0 Radius=1.5 StartAngle=4.71485 EndAngle=7.85398
    g20: ArcOfCircle CenterX=-11.49 CenterY=21.5 CenterZ=0 NormalX=0 NormalY=0 NormalZ=1 AngleXU=0 Radius=1.5 StartAngle=4.71239 EndAngle=7.85398
    g21: ArcOfCircle CenterX=-1.5 CenterY=4.25 CenterZ=0 NormalX=0 NormalY=0 NormalZ=1 AngleXU=0 Radius=1.5 StartAngle=4.71239 EndAngle=7.85398
    g22: ArcOfCircle CenterX=-1.5 CenterY=10 CenterZ=0 NormalX=0 NormalY=0 NormalZ=1 AngleXU=0 Radius=1.5 StartAngle=4.71239 EndAngle=7.85398
    g23: ArcOfCircle CenterX=-1.5 CenterY=15.75 CenterZ=0 NormalX=0 NormalY=0 NormalZ=1 AngleXU=0 Radius=1.5 StartAngle=4.71239 EndAngle=7.85398
    g24: LineSegment StartX=-49.19 StartY=69.25 StartZ=0 EndX=-1.5 EndY=69.25 EndZ=0
    g25: LineSegment StartX=-49.19 StartY=66.25 StartZ=0 EndX=-1.5 EndY=66.25 EndZ=0
    g26: LineSegment StartX=-49.19 StartY=63.5 StartZ=0 EndX=-1.5 EndY=63.5 EndZ=0
    g27: LineSegment StartX=-49.19 StartY=60.5 StartZ=0 EndX=-1.5 EndY=60.5 EndZ=0
    g28: LineSegment StartX=-49.19 StartY=57.75 StartZ=0 EndX=-1.5 EndY=57.75 EndZ=0
    g29: LineSegment StartX=-49.19 StartY=54.75 StartZ=0 EndX=-1.5 EndY=54.75 EndZ=0
    g30: LineSegment StartX=-49.19 StartY=52 StartZ=0 EndX=-11.49 EndY=52 EndZ=0
    g31: LineSegment StartX=-49.19 StartY=49 StartZ=0 EndX=-11.49 EndY=49 EndZ=0
    g32: LineSegment StartX=-49.19 StartY=46.25 StartZ=0 EndX=-16.28 EndY=46.25 EndZ=0
    g33: LineSegment StartX=-49.19 StartY=43.25 StartZ=0 EndX=-16.28 EndY=43.25 EndZ=0
    g34: LineSegment StartX=-49.19 StartY=40.5 StartZ=0 EndX=-18.2337 EndY=40.5 EndZ=0
    g35: LineSegment StartX=-49.19 StartY=37.5 StartZ=0 EndX=-18.23 EndY=37.5 EndZ=0
    g36: LineSegment StartX=-49.19 StartY=34.5 StartZ=0 EndX=-18.2337 EndY=34.5 EndZ=0
    g37: LineSegment StartX=-49.19 StartY=31.5 StartZ=0 EndX=-18.23 EndY=31.5 EndZ=0
    g38: LineSegment StartX=-49.19 StartY=28.75 StartZ=0 EndX=-16.2837 EndY=28.75 EndZ=0
    g39: LineSegment StartX=-49.19 StartY=25.75 StartZ=0 EndX=-16.28 EndY=25.75 EndZ=0
    g40: LineSegment StartX=-49.19 StartY=23 StartZ=0 EndX=-11.49 EndY=23 EndZ=0
    g41: LineSegment StartX=-49.19 StartY=20 StartZ=0 EndX=-11.49 EndY=20 EndZ=0
    g42: LineSegment StartX=-49.19 StartY=17.25 StartZ=0 EndX=-1.5 EndY=17.25 EndZ=0
    g43: LineSegment StartX=-49.19 StartY=14.25 StartZ=0 EndX=-1.5 EndY=14.25 EndZ=0
    g44: LineSegment StartX=-49.19 StartY=11.5 StartZ=0 EndX=-1.5 EndY=11.5 EndZ=0
    g45: LineSegment StartX=-49.19 StartY=8.5 StartZ=0 EndX=-1.5 EndY=8.5 EndZ=0
    g46: LineSegment StartX=-49.19 StartY=5.75 StartZ=0 EndX=-1.5 EndY=5.75 EndZ=0
    g47: LineSegment StartX=-49.19 StartY=2.75 StartZ=0 EndX=-1.5 EndY=2.75 EndZ=0
  constraints (120):
    c: Vertical(g0)
    c: Distance(g0) = 3
    c: Block(g0)
    c: Vertical(g1)
    c: Distance(g1) = 3
    c: Vertical(g2)
    c: Equal(g0,g2) = 3
    c: Block(g2)
    c: Vertical(g3)
    c: Equal(g1,g3) = 3
    c: Vertical(g4)
    c: Equal(g0,g4) = 3
    c: Block(g4)
    c: Vertical(g5)
    c: Equal(g1,g5) = 3
    c: Vertical(g6)
    c: Equal(g0,g6) = 3
    c: Block(g6)
    c: Vertical(g7)
    c: Equal(g1,g7) = 3
    c: Vertical(g8)
    c: Equal(g0,g8) = 3
    c: Block(g8)
    c: Vertical(g9)
    c: Equal(g1,g9) = 3
    c: Vertical(g10)
    c: Equal(g0,g10) = 3
    c: Block(g10)
    c: Vertical(g11)
    c: Equal(g1,g11) = 3
    c: Block(g12)
    c: Block(g13)
    c: Block(g14)
    c: Block(g15)
    c: Block(g16)
    c: Block(g17)
    c: Block(g18)
    c: Block(g19)
    c: Block(g20)
    c: Block(g21)
    c: Block(g22)
    c: Block(g23)
    c: Block(g11)
    c: Block(g9)
    c: Block(g7)
    c: Block(g5)
    c: Block(g3)
    c: Block(g1)
    c: Coincident(g24,g0)
    c: Coincident(g24,g12)
    c: Horizontal(g24)
    c: Coincident(g25,g0)
    c: Coincident(g25,g12)
    c: Horizontal(g25)
    c: Coincident(g26,g1)
    c: Coincident(g26,g13)
    c: Horizontal(g26)
    c: Coincident(g27,g1)
    c: Coincident(g27,g13)
    c: Horizontal(g27)
    c: Coincident(g28,g2)
    c: Coincident(g28,g14)
    c: Horizontal(g28)
    c: Coincident(g29,g2)
    c: Coincident(g29,g14)
    c: Horizontal(g29)
    c: Coincident(g30,g3)
    c: Coincident(g30,g15)
    c: Horizontal(g30)
    c: Coincident(g31,g3)
    c: Coincident(g31,g15)
    c: Horizontal(g31)
    c: Coincident(g32,g4)
    c: Coincident(g32,g16)
    c: Horizontal(g32)
    c: Coincident(g33,g4)
    c: Coincident(g33,g16)
    c: Horizontal(g33)
    c: Coincident(g34,g5)
    c: Coincident(g34,g17)
    c: Horizontal(g34)
    c: Coincident(g35,g5)
    c: Coincident(g35,g17)
    c: Horizontal(g35)
    c: Coincident(g36,g6)
    c: Coincident(g36,g19)
    c: Horizontal(g36)
    c: Coincident(g37,g6)
    c: Coincident(g37,g19)
    c: Horizontal(g37)
    c: Coincident(g38,g7)
    c: Coincident(g38,g18)
    c: Horizontal(g38)
    c: Coincident(g39,g7)
    c: Coincident(g39,g18)
    c: Horizontal(g39)
    c: Coincident(g40,g8)
    c: Coincident(g40,g20)
    c: Horizontal(g40)
    c: Coincident(g41,g8)
    c: Coincident(g41,g20)
    c: Horizontal(g41)
    c: Coincident(g42,g9)
    c: Coincident(g42,g23)
    c: Horizontal(g42)
    c: Coincident(g43,g9)
    c: Coincident(g43,g23)
    c: Horizontal(g43)
    c: Coincident(g44,g10)
    c: Coincident(g44,g22)
    c: Horizontal(g44)
    c: Coincident(g45,g10)
    c: Coincident(g45,g22)
    c: Horizontal(g45)
    c: Coincident(g46,g11)
    c: Coincident(g46,g21)
    c: Horizontal(g46)
    c: Coincident(g47,g11)
    c: Coincident(g47,g21)
    c: Horizontal(g47)
FEATURE [Part::Extrusion] Extrude042
  Base = -> Sketch051
  Dir = (1,-2e-16,2e-16)
  DirMode = 2
  FaceMakerClass = Part::FaceMakerBullseye
  LengthFwd = 19
  LengthRev = 0
  Placement = pos=(-19,0,0) rot=(0,0,1;0rad)
  Solid = true
  Symmetric = false
FEATURE [Part::Fillet] Fillet035  label="removeToCreateVentalationHoles"
  Base = -> Extrude042
  Edges = <same value as first occurrence — deduplicated (x6 in doc)>
  Placement = pos=(7,0,0) rot=(0,0,1;0rad)
FEATURE [Part::Cut] Cut038  label="top017"
  Base = -> Cut033
  Tool = -> Fillet035
FEATURE [Sketcher::SketchObject] Sketch052  label="bottomSketch001"
  FullyConstrained = true
  sketch-geometry (45):
    g0: LineSegment StartX=6.29999 StartY=8 StartZ=0 EndX=3.29999 EndY=8 EndZ=0
    g1: LineSegment StartX=3.29999 StartY=8 StartZ=0 EndX=3.29999 EndY=-6.03275e-07 EndZ=0
    g2: ArcOfCircle CenterX=8.29999 CenterY=5 CenterZ=0 NormalX=0 NormalY=0 NormalZ=1 AngleXU=0 Radius=2 StartAngle=3.14159 EndAngle=4.71239
    g3: LineSegment StartX=6.29999 StartY=8 StartZ=0 EndX=6.29999 EndY=5 EndZ=0
    g4: ArcOfCircle CenterX=105 CenterY=19 CenterZ=0 NormalX=0 NormalY=0 NormalZ=1 AngleXU=0 Radius=12.7 StartAngle=4.71239 EndAngle=5.94289
    g5-g11: Circle x7 (B-spline internal-alignment scaffolding for g12; pole/knot coordinates omitted)
    g12: BSplineCurve PolesCount=7 KnotsCount=5 Degree=3 IsPeriodic=0
    g13-g17: GeomPoint x5 (B-spline internal-alignment scaffolding for g12; pole/knot coordinates omitted)
    g18: ArcOfCircle CenterX=105 CenterY=19 CenterZ=0 NormalX=0 NormalY=0 NormalZ=1 AngleXU=0 Radius=15.7 StartAngle=5.81226 EndAngle=6.28319
    g19: BSplineCurve PolesCount=5 KnotsCount=3 Degree=3 IsPeriodic=0
    g20: LineSegment StartX=8.29999 StartY=3 StartZ=0 EndX=101.7 EndY=3 EndZ=0
    g21: LineSegment StartX=3.29999 StartY=-6.03275e-07 StartZ=0 EndX=105 EndY=-6.03275e-07 EndZ=0
    g22: LineSegment StartX=120.974 StartY=8.71251 StartZ=0 EndX=122.332 EndY=7.83778 EndZ=0
    g23: LineSegment StartX=105 StartY=-6.03274e-07 StartZ=0 EndX=113 EndY=-6.03274e-07 EndZ=0
    g24: ArcOfCircle CenterX=105 CenterY=19 CenterZ=0 NormalX=0 NormalY=0 NormalZ=1 AngleXU=0 Radius=20.6155 StartAngle=5.11091 EndAngle=5.71103
    g25: ArcOfCircle CenterX=117.7 CenterY=19 CenterZ=0 NormalX=0 NormalY=0 NormalZ=1 AngleXU=0 Radius=3 StartAngle=1.2e-15 EndAngle=2.10468
    g26: Circle CenterX=116.345 CenterY=16.3232 CenterZ=0 NormalX=0 NormalY=0 NormalZ=1 AngleXU=0 Radius=1
    g27: Circle CenterX=117.24 CenterY=15.7584 CenterZ=0 NormalX=0 NormalY=0 NormalZ=1 AngleXU=0 Radius=1
    g28: Circle CenterX=116.972 CenterY=14.7612 CenterZ=0 NormalX=0 NormalY=0 NormalZ=1 AngleXU=0 Radius=1
    g29: BSplineCurve PolesCount=3 KnotsCount=2 Degree=2 IsPeriodic=0
    g30: GeomPoint X=116.345 Y=16.3232 Z=0
    g31: GeomPoint X=116.972 Y=14.7612 Z=0
    g32: Circle CenterX=115.828 CenterY=17.157 CenterZ=0 NormalX=0 NormalY=0 NormalZ=1 AngleXU=0 Radius=1
    g33: Circle CenterX=115.841 CenterY=16.639 CenterZ=0 NormalX=0 NormalY=0 NormalZ=1 AngleXU=0 Radius=1
    g34: Circle CenterX=116.345 CenterY=16.3232 CenterZ=0 NormalX=0 NormalY=0 NormalZ=1 AngleXU=0 Radius=1
    g35: BSplineCurve PolesCount=3 KnotsCount=2 Degree=2 IsPeriodic=0
    g36: GeomPoint X=115.828 Y=17.157 Z=0
    g37: GeomPoint X=116.345 Y=16.3232 Z=0
    g38: LineSegment StartX=115.828 StartY=17.157 StartZ=0 EndX=115.828 EndY=20.8307 EndZ=0
    g39: Circle CenterX=115.828 CenterY=20.8307 CenterZ=0 NormalX=0 NormalY=0 NormalZ=1 AngleXU=0 Radius=1
    g40: Circle CenterX=115.831 CenterY=21.3396 CenterZ=0 NormalX=0 NormalY=0 NormalZ=1 AngleXU=0 Radius=1
    g41: Circle CenterX=116.173 CenterY=21.5825 CenterZ=0 NormalX=0 NormalY=0 NormalZ=1 AngleXU=0 Radius=1
    g42: BSplineCurve PolesCount=3 KnotsCount=2 Degree=2 IsPeriodic=0
    g43: GeomPoint X=115.828 Y=20.8307 Z=0
    g44: GeomPoint X=116.173 Y=21.5825 Z=0
  constraints (70):
    c: Horizontal(g0)
    c: Distance(g0) = 3
    c: Coincident(g1,g0)
    c: Vertical(g1)
    c: Block(g2)
    c: Block(g0)
    c: Coincident(g3,g0)
    c: Coincident(g3,g2)
    c: Vertical(g3)
    c: Block(g1)
    c: Block(g4)
    c: Coincident(g19,g4)
    c: Block(g19)
    c: Equal(g5, g6-g11) x6
    c: InternalAlignment(g5-g11 -> g12) x7
    c: InternalAlignment(g13-g17 -> g12) x5
    c: Block(g12)
    c: Coincident(g18,g12)
    c: Block(g18)
    c: Coincident(g20,g2)
    c: Coincident(g20,g19)
    c: Horizontal(g20)
    c: Distance(g20) = 93.4
    c: Coincident(g21,g1)
    c: Horizontal(g21)
    c: Distance(g21) = 101.7
    c: Horizontal(g23)
    c: Distance(g23) = 8
    c: Coincident(g24,g23)
    c: Block(g23)
    c: Coincident(g22,g24)
    c: Block(g24)
    c: Block(g22)
    c: Distance(g22) = 1.61553
    c: Coincident(g25,g18)
    c: Block(g25)
    c: Weight(g26) = 1
    c: Equal(g26,g27)
    c: Equal(g26,g28)
    c: Coincident(g29,g4)
    c: InternalAlignment(g26,g29)
    c: InternalAlignment(g27,g29)
    c: InternalAlignment(g28,g29)
    c: InternalAlignment(g30,g29)
    c: InternalAlignment(g31,g29)
    c: Block(g29)
    c: Weight(g32) = 1
    c: Equal(g32,g33)
    c: Equal(g32,g34)
    c: Coincident(g35,g29)
    c: InternalAlignment(g32,g35)
    c: InternalAlignment(g33,g35)
    c: InternalAlignment(g34,g35)
    c: InternalAlignment(g36,g35)
    c: InternalAlignment(g37,g35)
    c: Block(g35)
    c: Coincident(g38,g35)
    c: Vertical(g38)
    c: Block(g38)
    c: Coincident(g42,g38)
    c: Weight(g39) = 1
    c: Equal(g39,g40)
    c: Equal(g39,g41)
    c: Coincident(g42,g25)
    c: InternalAlignment(g39,g42)
    c: InternalAlignment(g40,g42)
    c: InternalAlignment(g41,g42)
    c: InternalAlignment(g43,g42)
    c: InternalAlignment(g44,g42)
    c: Block(g42)
FEATURE [Part::Extrusion] Extrude043  label="bottom010"
  Base = -> Sketch052
  Dir = (0,0,1)
  DirMode = 2
  FaceMakerClass = Part::FaceMakerBullseye
  LengthFwd = 71.4
  LengthRev = 0
  Placement = pos=(0,0,0.3) rot=(0,0,1;0rad)
  Solid = true
  Symmetric = false
FEATURE [Sketcher::SketchObject] Sketch053  label="topSketch013"
  FullyConstrained = true
  sketch-geometry (22):
    g0: LineSegment StartX=5.21097e-06 StartY=3 StartZ=0 EndX=5.21097e-06 EndY=19 EndZ=0
    g1: ArcOfCircle CenterX=19 CenterY=19 CenterZ=0 NormalX=0 NormalY=0 NormalZ=1 AngleXU=0 Radius=19 StartAngle=1.5708 EndAngle=3.14159
    g2: ArcOfCircle CenterX=19 CenterY=19 CenterZ=0 NormalX=0 NormalY=0 NormalZ=1 AngleXU=0 Radius=16 StartAngle=1.5708 EndAngle=3.14159
    g3: LineSegment StartX=114 StartY=35 StartZ=0 EndX=19 EndY=35 EndZ=0
    g4: LineSegment StartX=5.21097e-06 StartY=3 StartZ=0 EndX=5.21097e-06 EndY=0 EndZ=0
    g5: LineSegment StartX=3 StartY=0 StartZ=0 EndX=5.21097e-06 EndY=0 EndZ=0
    g6: LineSegment StartX=3 StartY=19 StartZ=0 EndX=3 EndY=0 EndZ=0
    g7: LineSegment StartX=19 StartY=38 StartZ=0 EndX=124 EndY=38 EndZ=0
    g8: Circle CenterX=119 CenterY=35 CenterZ=0 NormalX=0 NormalY=0 NormalZ=1 AngleXU=0 Radius=1
    g9: Circle CenterX=121 CenterY=35 CenterZ=0 NormalX=0 NormalY=0 NormalZ=1 AngleXU=0 Radius=1
    g10: Circle CenterX=121 CenterY=33 CenterZ=0 NormalX=0 NormalY=0 NormalZ=1 AngleXU=0 Radius=1
    g11: BSplineCurve PolesCount=3 KnotsCount=2 Degree=2 IsPeriodic=0
    g12: GeomPoint X=119 Y=35 Z=0
    g13: GeomPoint X=121 Y=33 Z=0
    g14: LineSegment StartX=119 StartY=35 StartZ=0 EndX=114 EndY=35 EndZ=0
    g15: ArcOfCircle CenterX=105 CenterY=19 CenterZ=0 NormalX=0 NormalY=0 NormalZ=1 AngleXU=0 Radius=16 StartAngle=5.60905 EndAngle=6.28319
    g16: LineSegment StartX=121 StartY=33 StartZ=0 EndX=121 EndY=19 EndZ=0
    g17: LineSegment StartX=117.5 StartY=9.01251 StartZ=0 EndX=121.163 EndY=9.0125 EndZ=0
    g18: ArcOfCircle CenterX=105 CenterY=19 CenterZ=0 NormalX=0 NormalY=0 NormalZ=1 AngleXU=0 Radius=20.6155 StartAngle=5.7297 EndAngle=6.28319
    g19: LineSegment StartX=121.163 StartY=9.0125 StartZ=0 EndX=122.538 EndY=8.16329 EndZ=0
    g20: LineSegment StartX=124 StartY=38 StartZ=0 EndX=125.616 EndY=38 EndZ=0
    g21: LineSegment StartX=125.616 StartY=19 StartZ=0 EndX=125.616 EndY=38 EndZ=0
  constraints (50):
    c: Vertical(g0)
    c: Block(g0)
    c: Coincident(g1,g0)
    c: Block(g1)
    c: Coincident(g2,g1)
    c: Block(g2)
    c: Coincident(g3,g2)
    c: Horizontal(g3)
    c: Tangent(g3,g2)
    c: Coincident(g4,g0)
    c: Distance(g4) = 3
    c: Vertical(g4)
    c: Coincident(g5,g4)
    c: Horizontal(g5)
    c: Coincident(g6,g2)
    c: Coincident(g6,g5)
    c: Vertical(g6)
    c: Horizontal(g7)
    c: Distance(g7) = 105
    c: Coincident(g7,g1)
    c: Block(g3)
    c: Weight(g8) = 1
    c: Equal(g8,g9)
    c: Equal(g8,g10)
    c: InternalAlignment(g8,g11)
    c: InternalAlignment(g9,g11)
    c: InternalAlignment(g10,g11)
    c: InternalAlignment(g12,g11)
    c: InternalAlignment(g13,g11)
    c: Block(g11)
    c: Coincident(g14,g11)
    c: Coincident(g14,g3)
    c: Horizontal(g14)
    c: Block(g15)
    c: Coincident(g16,g11)
    c: Coincident(g16,g15)
    c: Vertical(g16)
    c: Distance(g16) = 14
    c: Coincident(g17,g15)
    c: Block(g18)
    c: Coincident(g19,g18)
    c: Coincident(g20,g7)
    c: Horizontal(g20)
    c: Vertical(g21)
    c: Coincident(g20,g21)
    c: Block(g20)
    c: Block(g21)
    c: Block(g19)
    c: Block(g17)
    c: Distance(g20) = 1.61553
FEATURE [Part::Extrusion] Extrude044
  Base = -> Sketch053
  Dir = (0,0,1)
  DirMode = 2
  FaceMakerClass = Part::FaceMakerBullseye
  LengthFwd = 72
  LengthRev = 0
  Solid = true
  Symmetric = false
FEATURE [Part::Fillet] Fillet036  label="top018"
  Base = -> Extrude044
  Edges = 1 edges r=2: [Edge41]
FEATURE [Sketcher::SketchObject] Sketch054
  FullyConstrained = false
  Placement = pos=(0,0,0) rot=(1,0,0;1.5708rad)
  sketch-geometry (24):
    g0: ArcOfCircle CenterX=-4 CenterY=-10.5 CenterZ=0 NormalX=0 NormalY=0 NormalZ=1 AngleXU=0 Radius=1.5 StartAngle=6e-16 EndAngle=3.14159
    g1: ArcOfCircle CenterX=-34.2 CenterY=-10.5 CenterZ=0 NormalX=0 NormalY=0 NormalZ=1 AngleXU=0 Radius=1.5 StartAngle=0 EndAngle=3.14159
    g2: ArcOfCircle CenterX=-34.2 CenterY=-27.7 CenterZ=0 NormalX=0 NormalY=0 NormalZ=1 AngleXU=0 Radius=1.5 StartAngle=3.14159 EndAngle=6.28319
    g3: ArcOfCircle CenterX=-4 CenterY=-27.7 CenterZ=0 NormalX=0 NormalY=0 NormalZ=1 AngleXU=0 Radius=1.5 StartAngle=3.1416 EndAngle=6.28319
    g4: ArcOfCircle CenterX=-10 CenterY=-4.3 CenterZ=0 NormalX=0 NormalY=0 NormalZ=1 AngleXU=0 Radius=1.5 StartAngle=2e-16 EndAngle=3.14159
    g5: ArcOfCircle CenterX=-16.1 CenterY=-1.8 CenterZ=0 NormalX=0 NormalY=0 NormalZ=1 AngleXU=0 Radius=1.5 StartAngle=5e-16 EndAngle=3.14159
    g6: ArcOfCircle CenterX=-22.1 CenterY=-1.8 CenterZ=0 NormalX=0 NormalY=0 NormalZ=1 AngleXU=0 Radius=1.5 StartAngle=5e-16 EndAngle=3.14159
    g7: ArcOfCircle CenterX=-28.2 CenterY=-4.3 CenterZ=0 NormalX=0 NormalY=0 NormalZ=1 AngleXU=0 Radius=1.5 StartAngle=2e-16 EndAngle=3.14159
    g8: ArcOfCircle CenterX=-10 CenterY=-33.9 CenterZ=0 NormalX=0 NormalY=0 NormalZ=1 AngleXU=0 Radius=1.5 StartAngle=3.14159 EndAngle=6.28319
    g9: ArcOfCircle CenterX=-16.1 CenterY=-36.4 CenterZ=0 NormalX=0 NormalY=0 NormalZ=1 AngleXU=0 Radius=1.5 StartAngle=3.14159 EndAngle=6.28319
    g10: ArcOfCircle CenterX=-22.1 CenterY=-36.4 CenterZ=0 NormalX=0 NormalY=0 NormalZ=1 AngleXU=0 Radius=1.5 StartAngle=3.14159 EndAngle=6.28319
    g11: ArcOfCircle CenterX=-28.2 CenterY=-33.9 CenterZ=0 NormalX=0 NormalY=0 NormalZ=1 AngleXU=0 Radius=1.5 StartAngle=3.14159 EndAngle=6.28319
    g12: LineSegment StartX=-35.7 StartY=-10.5 StartZ=0 EndX=-35.7 EndY=-27.7 EndZ=0
    g13: LineSegment StartX=-32.7 StartY=-10.5 StartZ=0 EndX=-32.7 EndY=-27.7 EndZ=0
    g14: LineSegment StartX=-29.7 StartY=-33.9 StartZ=0 EndX=-29.7 EndY=-4.3 EndZ=0
    g15: LineSegment StartX=-26.7 StartY=-33.9 StartZ=0 EndX=-26.7 EndY=-4.3 EndZ=0
    g16: LineSegment StartX=-2.5 StartY=-10.5 StartZ=0 EndX=-2.5 EndY=-27.7 EndZ=0
    g17: LineSegment StartX=-8.5 StartY=-4.3 StartZ=0 EndX=-8.5 EndY=-33.9 EndZ=0
    g18: LineSegment StartX=-5.5 StartY=-10.5 StartZ=0 EndX=-5.5 EndY=-27.7 EndZ=0
    g19: LineSegment StartX=-11.5 StartY=-4.3 StartZ=0 EndX=-11.5 EndY=-33.9 EndZ=0
    g20: LineSegment StartX=-14.6 StartY=-1.8 StartZ=0 EndX=-14.6 EndY=-36.4 EndZ=0
    g21: LineSegment StartX=-17.6 StartY=-1.8 StartZ=0 EndX=-17.6 EndY=-36.4 EndZ=0
    g22: LineSegment StartX=-20.6 StartY=-36.4 StartZ=0 EndX=-20.6 EndY=-1.8 EndZ=0
    g23: LineSegment StartX=-23.6 StartY=-1.8 StartZ=0 EndX=-23.6 EndY=-36.4 EndZ=0
  constraints (48):
    c: Block(g0)
    c: Block(g1)
    c: Block(g2)
    c: Block(g3)
    c: Block(g4)
    c: Block(g5)
    c: Block(g6)
    c: Block(g7)
    c: Block(g8)
    c: Block(g9)
    c: Block(g10)
    c: Block(g11)
    c: Coincident(g12,g1)
    c: Coincident(g12,g2)
    c: Vertical(g12)
    c: Coincident(g13,g1)
    c: Coincident(g13,g2)
    c: Vertical(g13)
    c: Coincident(g14,g11)
    c: Coincident(g14,g7)
    c: Vertical(g14)
    c: Coincident(g15,g11)
    c: Coincident(g15,g7)
    c: Vertical(g15)
    c: Coincident(g16,g0)
    c: Coincident(g16,g3)
    c: Vertical(g16)
    c: Coincident(g17,g4)
    c: Coincident(g17,g8)
    c: Vertical(g17)
    c: Coincident(g18,g0)
    c: Coincident(g18,g3)
    c: Vertical(g18)
    c: Coincident(g19,g4)
    c: Coincident(g19,g8)
    c: Vertical(g19)
    c: Coincident(g20,g5)
    c: Coincident(g20,g9)
    c: Vertical(g20)
    c: Coincident(g21,g5)
    c: Coincident(g21,g9)
    c: Vertical(g21)
    c: Coincident(g22,g10)
    c: Coincident(g22,g6)
    c: Vertical(g22)
    c: Coincident(g23,g6)
    c: Coincident(g23,g10)
    c: Vertical(g23)
FEATURE [Part::Extrusion] Extrude045  label="removeToCreateFanGrillHoles003"
  Base = -> Sketch054
  Dir = (0,-1,6e-16)
  DirMode = 2
  FaceMakerClass = Part::FaceMakerBullseye
  LengthFwd = 10
  LengthRev = 0
  Placement = pos=(65.4,44,54.82) rot=(0,0,1;0rad)
  Solid = true
  Symmetric = false
FEATURE [Part::Feature] Face105 .. Face108  x4 (patterned run collapsed; names and placements below)
  shape: bbox 3.5 x 17.8 x 2e-07 mm, 1 faces, 0 solids (baked)
FEATURE [Part::Revolution] Revolve113  label="removeToCreateScrewAndThreadedInsertHole041"
  Angle = 360
  Axis = (0,1,0)
  Base = (0,0,0)
  FaceMakerClass = Part::FaceMakerBullseye
  Placement = pos=(62.3,30.3,19.7) rot=(0,0,1;0rad)
  Solid = false
  Source = -> Face105
  Symmetric = false
FEATURE [Part::Revolution] Revolve114  label="removeToCreateScrewAndThreadedInsertHole042"
  Angle = 360
  Axis = (0,1,0)
  Base = (0,0,0)
  FaceMakerClass = Part::FaceMakerBullseye
  Placement = pos=(62.3,30.3,51.7) rot=(0,0,1;0rad)
  Solid = false
  Source = -> Face106
  Symmetric = false
FEATURE [Part::Revolution] Revolve115  label="removeToCreateScrewAndThreadedInsertHole043"
  Angle = 360
  Axis = (0,1,0)
  Base = (0,0,0)
  FaceMakerClass = Part::FaceMakerBullseye
  Placement = pos=(30.3,30.3,19.7) rot=(0,0,1;0rad)
  Solid = false
  Source = -> Face107
  Symmetric = false
FEATURE [Part::Revolution] Revolve116  label="removeToCreateScrewAndThreadedInsertHole044"
  Angle = 360
  Axis = (0,1,0)
  Base = (0,0,0)
  FaceMakerClass = Part::FaceMakerBullseye
  Placement = pos=(30.3,30.3,51.7) rot=(0,0,1;0rad)
  Solid = false
  Source = -> Face108
  Symmetric = false
FEATURE [Part::MultiFuse] Fusion083  label="createThreadedInsertHolesForFan004"
  Shapes = -> [Revolve113,Revolve114,Revolve115,Revolve116]
FEATURE [Part::Box] Box024  label="removeToCreteHoleForPlugHousing026"
  AttacherType = Attacher::AttachEngine3D
  Height = 28.6
  Length = 10
  Placement = pos=(-2,0,21.7) rot=(0,0,1;0rad)
  Width = 19
FEATURE [Part::Cylinder] Cylinder038  label="removeToCreteHoleForPlugHousing027"
  Angle = 360
  AttacherType = Attacher::AttachEngine3D
  Height = 20
  Placement = pos=(-2,19,36) rot=(0,1,0;1.5708rad)
  Radius = 14.3
FEATURE [Part::MultiFuse] Fusion084  label="removeToCreteHoleForPlugHousing028"
  Shapes = -> [Box024,Cylinder038]
FEATURE [Part::Cylinder] Cylinder039
  Angle = 360
  AttacherType = Attacher::AttachEngine3D
  Height = 20
  Placement = pos=(0,0,36.15) rot=(0,0,1;0rad)
  Radius = 14.3
FEATURE [Part::Cylinder] Cylinder040
  Angle = 360
  AttacherType = Attacher::AttachEngine3D
  Height = 10
  Placement = pos=(0,0,36.15) rot=(0,0,1;0rad)
  Radius = 4
FEATURE [Part::Box] Box025  label="removeToCreteHoleForPlugHousing030"
  AttacherType = Attacher::AttachEngine3D
  Height = 28.6
  Length = 20
  Placement = pos=(106.15,0,21.7) rot=(0,0,1;0rad)
  Width = 19
FEATURE [Part::MultiFuse] Fusion086  label="removeToCreteHoleForPlugHousing031"
  Placement = pos=(70,19,36) rot=(0,1,0;1.5708rad)
  Shapes = -> [Cylinder039,Cylinder040]
FEATURE [Part::MultiFuse] Fusion085  label="removeToCreteHoleForPlugHousing029"
  Shapes = -> [Box025,Fusion086]
FEATURE [Sketcher::SketchObject] Sketch055
  FullyConstrained = true
  Placement = pos=(117,19,0) rot=(0.57735,0.57735,0.57735;2.0944rad)
  sketch-geometry (48):
    g0: LineSegment StartX=-49.19 StartY=69.25 StartZ=0 EndX=-49.19 EndY=66.25 EndZ=0
    g1: LineSegment StartX=-49.19 StartY=63.5 StartZ=0 EndX=-49.19 EndY=60.5 EndZ=0
    g2: LineSegment StartX=-49.19 StartY=57.75 StartZ=0 EndX=-49.19 EndY=54.75 EndZ=0
    g3: LineSegment StartX=-49.19 StartY=52 StartZ=0 EndX=-49.19 EndY=49 EndZ=0
    g4: LineSegment StartX=-49.19 StartY=46.25 StartZ=0 EndX=-49.19 EndY=43.25 EndZ=0
    g5: LineSegment StartX=-49.19 StartY=40.5 StartZ=0 EndX=-49.19 EndY=37.5 EndZ=0
    g6: LineSegment StartX=-49.19 StartY=34.5 StartZ=0 EndX=-49.19 EndY=31.5 EndZ=0
    g7: LineSegment StartX=-49.19 StartY=28.75 StartZ=0 EndX=-49.19 EndY=25.75 EndZ=0
    g8: LineSegment StartX=-49.19 StartY=23 StartZ=0 EndX=-49.19 EndY=20 EndZ=0
    g9: LineSegment StartX=-49.19 StartY=17.25 StartZ=0 EndX=-49.19 EndY=14.25 EndZ=0
    g10: LineSegment StartX=-49.19 StartY=11.5 StartZ=0 EndX=-49.19 EndY=8.5 EndZ=0
    g11: LineSegment StartX=-49.19 StartY=5.75 StartZ=0 EndX=-49.19 EndY=2.75 EndZ=0
    g12: ArcOfCircle CenterX=-1.5 CenterY=67.75 CenterZ=0 NormalX=0 NormalY=0 NormalZ=1 AngleXU=0 Radius=1.5 StartAngle=4.71239 EndAngle=7.85398
    g13: ArcOfCircle CenterX=-1.5 CenterY=62 CenterZ=0 NormalX=0 NormalY=0 NormalZ=1 AngleXU=0 Radius=1.5 StartAngle=4.71239 EndAngle=7.85398
    g14: ArcOfCircle CenterX=-1.5 CenterY=56.25 CenterZ=0 NormalX=0 NormalY=0 NormalZ=1 AngleXU=0 Radius=1.5 StartAngle=4.71239 EndAngle=7.85398
    g15: ArcOfCircle CenterX=-11.49 CenterY=50.5 CenterZ=0 NormalX=0 NormalY=0 NormalZ=1 AngleXU=0 Radius=1.5 StartAngle=4.71239 EndAngle=7.85398
    g16: ArcOfCircle CenterX=-16.28 CenterY=44.75 CenterZ=0 NormalX=0 NormalY=0 NormalZ=1 AngleXU=0 Radius=1.5 StartAngle=4.71239 EndAngle=7.85398
    g17: ArcOfCircle CenterX=-18.2337 CenterY=39 CenterZ=0 NormalX=0 NormalY=0 NormalZ=1 AngleXU=0 Radius=1.5 StartAngle=4.71485 EndAngle=7.85398
    g18: ArcOfCircle CenterX=-16.2837 CenterY=27.25 CenterZ=0 NormalX=0 NormalY=0 NormalZ=1 AngleXU=0 Radius=1.5 StartAngle=4.71485 EndAngle=7.85398
    g19: ArcOfCircle CenterX=-18.2337 CenterY=33 CenterZ=0 NormalX=0 NormalY=0 NormalZ=1 AngleXU=0 Radius=1.5 StartAngle=4.71485 EndAngle=7.85398
    g20: ArcOfCircle CenterX=-11.49 CenterY=21.5 CenterZ=0 NormalX=0 NormalY=0 NormalZ=1 AngleXU=0 Radius=1.5 StartAngle=4.71239 EndAngle=7.85398
    g21: ArcOfCircle CenterX=-1.5 CenterY=4.25 CenterZ=0 NormalX=0 NormalY=0 NormalZ=1 AngleXU=0 Radius=1.5 StartAngle=4.71239 EndAngle=7.85398
    g22: ArcOfCircle CenterX=-1.5 CenterY=10 CenterZ=0 NormalX=0 NormalY=0 NormalZ=1 AngleXU=0 Radius=1.5 StartAngle=4.71239 EndAngle=7.85398
    g23: ArcOfCircle CenterX=-1.5 CenterY=15.75 CenterZ=0 NormalX=0 NormalY=0 NormalZ=1 AngleXU=0 Radius=1.5 StartAngle=4.71239 EndAngle=7.85398
    g24: LineSegment StartX=-49.19 StartY=69.25 StartZ=0 EndX=-1.5 EndY=69.25 EndZ=0
    g25: LineSegment StartX=-49.19 StartY=66.25 StartZ=0 EndX=-1.5 EndY=66.25 EndZ=0
    g26: LineSegment StartX=-49.19 StartY=63.5 StartZ=0 EndX=-1.5 EndY=63.5 EndZ=0
    g27: LineSegment StartX=-49.19 StartY=60.5 StartZ=0 EndX=-1.5 EndY=60.5 EndZ=0
    g28: LineSegment StartX=-49.19 StartY=57.75 StartZ=0 EndX=-1.5 EndY=57.75 EndZ=0
    g29: LineSegment StartX=-49.19 StartY=54.75 StartZ=0 EndX=-1.5 EndY=54.75 EndZ=0
    g30: LineSegment StartX=-49.19 StartY=52 StartZ=0 EndX=-11.49 EndY=52 EndZ=0
    g31: LineSegment StartX=-49.19 StartY=49 StartZ=0 EndX=-11.49 EndY=49 EndZ=0
    g32: LineSegment StartX=-49.19 StartY=46.25 StartZ=0 EndX=-16.28 EndY=46.25 EndZ=0
    g33: LineSegment StartX=-49.19 StartY=43.25 StartZ=0 EndX=-16.28 EndY=43.25 EndZ=0
    g34: LineSegment StartX=-49.19 StartY=40.5 StartZ=0 EndX=-18.2337 EndY=40.5 EndZ=0
    g35: LineSegment StartX=-49.19 StartY=37.5 StartZ=0 EndX=-18.23 EndY=37.5 EndZ=0
    g36: LineSegment StartX=-49.19 StartY=34.5 StartZ=0 EndX=-18.2337 EndY=34.5 EndZ=0
    g37: LineSegment StartX=-49.19 StartY=31.5 StartZ=0 EndX=-18.23 EndY=31.5 EndZ=0
    g38: LineSegment StartX=-49.19 StartY=28.75 StartZ=0 EndX=-16.2837 EndY=28.75 EndZ=0
    g39: LineSegment StartX=-49.19 StartY=25.75 StartZ=0 EndX=-16.28 EndY=25.75 EndZ=0
    g40: LineSegment StartX=-49.19 StartY=23 StartZ=0 EndX=-11.49 EndY=23 EndZ=0
    g41: LineSegment StartX=-49.19 StartY=20 StartZ=0 EndX=-11.49 EndY=20 EndZ=0
    g42: LineSegment StartX=-49.19 StartY=17.25 StartZ=0 EndX=-1.5 EndY=17.25 EndZ=0
    g43: LineSegment StartX=-49.19 StartY=14.25 StartZ=0 EndX=-1.5 EndY=14.25 EndZ=0
    g44: LineSegment StartX=-49.19 StartY=11.5 StartZ=0 EndX=-1.5 EndY=11.5 EndZ=0
    g45: LineSegment StartX=-49.19 StartY=8.5 StartZ=0 EndX=-1.5 EndY=8.5 EndZ=0
    g46: LineSegment StartX=-49.19 StartY=5.75 StartZ=0 EndX=-1.5 EndY=5.75 EndZ=0
    g47: LineSegment StartX=-49.19 StartY=2.75 StartZ=0 EndX=-1.5 EndY=2.75 EndZ=0
  constraints (120):
    c: Vertical(g0)
    c: Distance(g0) = 3
    c: Block(g0)
    c: Vertical(g1)
    c: Distance(g1) = 3
    c: Vertical(g2)
    c: Equal(g0,g2) = 3
    c: Block(g2)
    c: Vertical(g3)
    c: Equal(g1,g3) = 3
    c: Vertical(g4)
    c: Equal(g0,g4) = 3
    c: Block(g4)
    c: Vertical(g5)
    c: Equal(g1,g5) = 3
    c: Vertical(g6)
    c: Equal(g0,g6) = 3
    c: Block(g6)
    c: Vertical(g7)
    c: Equal(g1,g7) = 3
    c: Vertical(g8)
    c: Equal(g0,g8) = 3
    c: Block(g8)
    c: Vertical(g9)
    c: Equal(g1,g9) = 3
    c: Vertical(g10)
    c: Equal(g0,g10) = 3
    c: Block(g10)
    c: Vertical(g11)
    c: Equal(g1,g11) = 3
    c: Block(g12)
    c: Block(g13)
    c: Block(g14)
    c: Block(g15)
    c: Block(g16)
    c: Block(g17)
    c: Block(g18)
    c: Block(g19)
    c: Block(g20)
    c: Block(g21)
    c: Block(g22)
    c: Block(g23)
    c: Block(g11)
    c: Block(g9)
    c: Block(g7)
    c: Block(g5)
    c: Block(g3)
    c: Block(g1)
    c: Coincident(g24,g0)
    c: Coincident(g24,g12)
    c: Horizontal(g24)
    c: Coincident(g25,g0)
    c: Coincident(g25,g12)
    c: Horizontal(g25)
    c: Coincident(g26,g1)
    c: Coincident(g26,g13)
    c: Horizontal(g26)
    c: Coincident(g27,g1)
    c: Coincident(g27,g13)
    c: Horizontal(g27)
    c: Coincident(g28,g2)
    c: Coincident(g28,g14)
    c: Horizontal(g28)
    c: Coincident(g29,g2)
    c: Coincident(g29,g14)
    c: Horizontal(g29)
    c: Coincident(g30,g3)
    c: Coincident(g30,g15)
    c: Horizontal(g30)
    c: Coincident(g31,g3)
    c: Coincident(g31,g15)
    c: Horizontal(g31)
    c: Coincident(g32,g4)
    c: Coincident(g32,g16)
    c: Horizontal(g32)
    c: Coincident(g33,g4)
    c: Coincident(g33,g16)
    c: Horizontal(g33)
    c: Coincident(g34,g5)
    c: Coincident(g34,g17)
    c: Horizontal(g34)
    c: Coincident(g35,g5)
    c: Coincident(g35,g17)
    c: Horizontal(g35)
    c: Coincident(g36,g6)
    c: Coincident(g36,g19)
    c: Horizontal(g36)
    c: Coincident(g37,g6)
    c: Coincident(g37,g19)
    c: Horizontal(g37)
    c: Coincident(g38,g7)
    c: Coincident(g38,g18)
    c: Horizontal(g38)
    c: Coincident(g39,g7)
    c: Coincident(g39,g18)
    c: Horizontal(g39)
    c: Coincident(g40,g8)
    c: Coincident(g40,g20)
    c: Horizontal(g40)
    c: Coincident(g41,g8)
    c: Coincident(g41,g20)
    c: Horizontal(g41)
    c: Coincident(g42,g9)
    c: Coincident(g42,g23)
    c: Horizontal(g42)
    c: Coincident(g43,g9)
    c: Coincident(g43,g23)
    c: Horizontal(g43)
    c: Coincident(g44,g10)
    c: Coincident(g44,g22)
    c: Horizontal(g44)
    c: Coincident(g45,g10)
    c: Coincident(g45,g22)
    c: Horizontal(g45)
    c: Coincident(g46,g11)
    c: Coincident(g46,g21)
    c: Horizontal(g46)
    c: Coincident(g47,g11)
    c: Coincident(g47,g21)
    c: Horizontal(g47)
FEATURE [Part::Extrusion] Extrude046
  Base = -> Sketch055
  Dir = (1,0,0)
  DirMode = 2
  FaceMakerClass = Part::FaceMakerBullseye
  LengthFwd = 23
  LengthRev = 0
  Placement = pos=(-19,0,0) rot=(0,0,1;0rad)
  Solid = true
  Symmetric = false
FEATURE [Part::Fillet] Fillet038  label="removeToCreateVentalationHoles001"
  Base = -> Extrude046
  Edges = <same value as first occurrence — deduplicated (x6 in doc)>
  Placement = pos=(7,0,0) rot=(0,0,1;0rad)
FEATURE [Sketcher::SketchObject] Sketch056  label="topSketch014"
  FullyConstrained = true
  sketch-geometry (22):
    g0: LineSegment StartX=5.21097e-06 StartY=3 StartZ=0 EndX=5.21097e-06 EndY=19 EndZ=0
    g1: ArcOfCircle CenterX=19 CenterY=19 CenterZ=0 NormalX=0 NormalY=0 NormalZ=1 AngleXU=0 Radius=19 StartAngle=1.5708 EndAngle=3.14159
    g2: ArcOfCircle CenterX=19 CenterY=19 CenterZ=0 NormalX=0 NormalY=0 NormalZ=1 AngleXU=0 Radius=16 StartAngle=1.5708 EndAngle=3.14159
    g3: LineSegment StartX=114 StartY=35 StartZ=0 EndX=19 EndY=35 EndZ=0
    g4: LineSegment StartX=5.21097e-06 StartY=3 StartZ=0 EndX=5.21097e-06 EndY=0 EndZ=0
    g5: LineSegment StartX=3 StartY=0 StartZ=0 EndX=5.21097e-06 EndY=0 EndZ=0
    g6: LineSegment StartX=3 StartY=19 StartZ=0 EndX=3 EndY=0 EndZ=0
    g7: LineSegment StartX=19 StartY=38 StartZ=0 EndX=124 EndY=38 EndZ=0
    g8: Circle CenterX=119 CenterY=35 CenterZ=0 NormalX=0 NormalY=0 NormalZ=1 AngleXU=0 Radius=1
    g9: Circle CenterX=121 CenterY=35 CenterZ=0 NormalX=0 NormalY=0 NormalZ=1 AngleXU=0 Radius=1
    g10: Circle CenterX=121 CenterY=33 CenterZ=0 NormalX=0 NormalY=0 NormalZ=1 AngleXU=0 Radius=1
    g11: BSplineCurve PolesCount=3 KnotsCount=2 Degree=2 IsPeriodic=0
    g12: GeomPoint X=119 Y=35 Z=0
    g13: GeomPoint X=121 Y=33 Z=0
    g14: LineSegment StartX=119 StartY=35 StartZ=0 EndX=114 EndY=35 EndZ=0
    g15: ArcOfCircle CenterX=105 CenterY=19 CenterZ=0 NormalX=0 NormalY=0 NormalZ=1 AngleXU=0 Radius=16 StartAngle=5.60905 EndAngle=6.28319
    g16: LineSegment StartX=121 StartY=33 StartZ=0 EndX=121 EndY=19 EndZ=0
    g17: LineSegment StartX=117.5 StartY=9.01251 StartZ=0 EndX=121.163 EndY=9.0125 EndZ=0
    g18: ArcOfCircle CenterX=105 CenterY=19 CenterZ=0 NormalX=0 NormalY=0 NormalZ=1 AngleXU=0 Radius=20.6155 StartAngle=5.7297 EndAngle=6.28319
    g19: LineSegment StartX=121.163 StartY=9.0125 StartZ=0 EndX=122.538 EndY=8.16329 EndZ=0
    g20: LineSegment StartX=124 StartY=38 StartZ=0 EndX=125.616 EndY=38 EndZ=0
    g21: LineSegment StartX=125.616 StartY=19 StartZ=0 EndX=125.616 EndY=38 EndZ=0
  constraints (49):
    c: Vertical(g0)
    c: Block(g0)
    c: Coincident(g1,g0)
    c: Block(g1)
    c: Coincident(g2,g1)
    c: Block(g2)
    c: Coincident(g3,g2)
    c: Horizontal(g3)
    c: Tangent(g3,g2)
    c: Coincident(g4,g0)
    c: Distance(g4) = 3
    c: Vertical(g4)
    c: Coincident(g5,g4)
    c: Horizontal(g5)
    c: Coincident(g6,g2)
    c: Coincident(g6,g5)
    c: Vertical(g6)
    c: Horizontal(g7)
    c: Distance(g7) = 105
    c: Coincident(g7,g1)
    c: Block(g3)
    c: Weight(g8) = 1
    c: Equal(g8,g9)
    c: Equal(g8,g10)
    c: InternalAlignment(g8,g11)
    c: InternalAlignment(g9,g11)
    c: InternalAlignment(g10,g11)
    c: InternalAlignment(g12,g11)
    c: InternalAlignment(g13,g11)
    c: Block(g11)
    c: Coincident(g14,g11)
    c: Coincident(g14,g3)
    c: Horizontal(g14)
    c: Block(g15)
    c: Coincident(g16,g11)
    c: Coincident(g16,g15)
    c: Vertical(g16)
    c: Distance(g16) = 14
    c: Coincident(g17,g15)
    c: Block(g18)
    c: Coincident(g19,g18)
    c: Coincident(g20,g7)
    c: Horizontal(g20)
    c: Vertical(g21)
    c: Coincident(g20,g21)
    c: Block(g20)
    c: Block(g21)
    c: Block(g19)
    c: Block(g17)
FEATURE [Part::Box] Box026  label="removeToCreteHoleForPlugHousing032"
  AttacherType = Attacher::AttachEngine3D
  Height = 28.6
  Length = 10
  Placement = pos=(-2,0,21.7) rot=(0,0,1;0rad)
  Width = 19
FEATURE [Part::Feature] Face109 .. Face112  x4 (patterned run collapsed; names and placements below)
  shape: bbox 3.5 x 17.8 x 2e-07 mm, 1 faces, 0 solids (baked)
FEATURE [Part::Revolution] Revolve117  label="removeToCreateScrewAndThreadedInsertHole045"
  Angle = 360
  Axis = (0,1,0)
  Base = (0,0,0)
  FaceMakerClass = Part::FaceMakerBullseye
  Placement = pos=(62.3,30.3,19.7) rot=(0,0,1;0rad)
  Solid = false
  Source = -> Face109
  Symmetric = false
FEATURE [Part::Revolution] Revolve118  label="removeToCreateScrewAndThreadedInsertHole046"
  Angle = 360
  Axis = (0,1,0)
  Base = (0,0,0)
  FaceMakerClass = Part::FaceMakerBullseye
  Placement = pos=(62.3,30.3,51.7) rot=(0,0,1;0rad)
  Solid = false
  Source = -> Face110
  Symmetric = false
FEATURE [Part::Revolution] Revolve119  label="removeToCreateScrewAndThreadedInsertHole047"
  Angle = 360
  Axis = (0,1,0)
  Base = (0,0,0)
  FaceMakerClass = Part::FaceMakerBullseye
  Placement = pos=(30.3,30.3,19.7) rot=(0,0,1;0rad)
  Solid = false
  Source = -> Face111
  Symmetric = false
FEATURE [Part::Revolution] Revolve120  label="removeToCreateScrewAndThreadedInsertHole048"
  Angle = 360
  Axis = (0,1,0)
  Base = (0,0,0)
  FaceMakerClass = Part::FaceMakerBullseye
  Placement = pos=(30.3,30.3,51.7) rot=(0,0,1;0rad)
  Solid = false
  Source = -> Face112
  Symmetric = false
FEATURE [Part::MultiFuse] Fusion087  label="createThreadedInsertHolesForFan005"
  Shapes = -> [Revolve117,Revolve118,Revolve119,Revolve120]
FEATURE [Part::Extrusion] Extrude047
  Base = -> Sketch056
  Dir = (0,0,1)
  DirMode = 2
  FaceMakerClass = Part::FaceMakerBullseye
  LengthFwd = 72
  LengthRev = 0
  Solid = true
  Symmetric = false
FEATURE [Part::Fillet] Fillet039  label="top019"
  Base = -> Extrude047
  Edges = 1 edges r=2: [Edge35]
FEATURE [Sketcher::SketchObject] Sketch057
  FullyConstrained = false
  Placement = pos=(0,0,0) rot=(1,0,0;1.5708rad)
  sketch-geometry (24):
    g0: ArcOfCircle CenterX=-4 CenterY=-10.5 CenterZ=0 NormalX=0 NormalY=0 NormalZ=1 AngleXU=0 Radius=1.5 StartAngle=6e-16 EndAngle=3.14159
    g1: ArcOfCircle CenterX=-34.2 CenterY=-10.5 CenterZ=0 NormalX=0 NormalY=0 NormalZ=1 AngleXU=0 Radius=1.5 StartAngle=0 EndAngle=3.14159
    g2: ArcOfCircle CenterX=-34.2 CenterY=-27.7 CenterZ=0 NormalX=0 NormalY=0 NormalZ=1 AngleXU=0 Radius=1.5 StartAngle=3.14159 EndAngle=6.28319
    g3: ArcOfCircle CenterX=-4 CenterY=-27.7 CenterZ=0 NormalX=0 NormalY=0 NormalZ=1 AngleXU=0 Radius=1.5 StartAngle=3.1416 EndAngle=6.28319
    g4: ArcOfCircle CenterX=-10 CenterY=-4.3 CenterZ=0 NormalX=0 NormalY=0 NormalZ=1 AngleXU=0 Radius=1.5 StartAngle=2e-16 EndAngle=3.14159
    g5: ArcOfCircle CenterX=-16.1 CenterY=-1.8 CenterZ=0 NormalX=0 NormalY=0 NormalZ=1 AngleXU=0 Radius=1.5 StartAngle=5e-16 EndAngle=3.14159
    g6: ArcOfCircle CenterX=-22.1 CenterY=-1.8 CenterZ=0 NormalX=0 NormalY=0 NormalZ=1 AngleXU=0 Radius=1.5 StartAngle=5e-16 EndAngle=3.14159
    g7: ArcOfCircle CenterX=-28.2 CenterY=-4.3 CenterZ=0 NormalX=0 NormalY=0 NormalZ=1 AngleXU=0 Radius=1.5 StartAngle=2e-16 EndAngle=3.14159
    g8: ArcOfCircle CenterX=-10 CenterY=-33.9 CenterZ=0 NormalX=0 NormalY=0 NormalZ=1 AngleXU=0 Radius=1.5 StartAngle=3.14159 EndAngle=6.28319
    g9: ArcOfCircle CenterX=-16.1 CenterY=-36.4 CenterZ=0 NormalX=0 NormalY=0 NormalZ=1 AngleXU=0 Radius=1.5 StartAngle=3.14159 EndAngle=6.28319
    g10: ArcOfCircle CenterX=-22.1 CenterY=-36.4 CenterZ=0 NormalX=0 NormalY=0 NormalZ=1 AngleXU=0 Radius=1.5 StartAngle=3.14159 EndAngle=6.28319
    g11: ArcOfCircle CenterX=-28.2 CenterY=-33.9 CenterZ=0 NormalX=0 NormalY=0 NormalZ=1 AngleXU=0 Radius=1.5 StartAngle=3.14159 EndAngle=6.28319
    g12: LineSegment StartX=-35.7 StartY=-10.5 StartZ=0 EndX=-35.7 EndY=-27.7 EndZ=0
    g13: LineSegment StartX=-32.7 StartY=-10.5 StartZ=0 EndX=-32.7 EndY=-27.7 EndZ=0
    g14: LineSegment StartX=-29.7 StartY=-33.9 StartZ=0 EndX=-29.7 EndY=-4.3 EndZ=0
    g15: LineSegment StartX=-26.7 StartY=-33.9 StartZ=0 EndX=-26.7 EndY=-4.3 EndZ=0
    g16: LineSegment StartX=-2.5 StartY=-10.5 StartZ=0 EndX=-2.5 EndY=-27.7 EndZ=0
    g17: LineSegment StartX=-8.5 StartY=-4.3 StartZ=0 EndX=-8.5 EndY=-33.9 EndZ=0
    g18: LineSegment StartX=-5.5 StartY=-10.5 StartZ=0 EndX=-5.5 EndY=-27.7 EndZ=0
    g19: LineSegment StartX=-11.5 StartY=-4.3 StartZ=0 EndX=-11.5 EndY=-33.9 EndZ=0
    g20: LineSegment StartX=-14.6 StartY=-1.8 StartZ=0 EndX=-14.6 EndY=-36.4 EndZ=0
    g21: LineSegment StartX=-17.6 StartY=-1.8 StartZ=0 EndX=-17.6 EndY=-36.4 EndZ=0
    g22: LineSegment StartX=-20.6 StartY=-36.4 StartZ=0 EndX=-20.6 EndY=-1.8 EndZ=0
    g23: LineSegment StartX=-23.6 StartY=-1.8 StartZ=0 EndX=-23.6 EndY=-36.4 EndZ=0
  constraints (48):
    c: Block(g0)
    c: Block(g1)
    c: Block(g2)
    c: Block(g3)
    c: Block(g4)
    c: Block(g5)
    c: Block(g6)
    c: Block(g7)
    c: Block(g8)
    c: Block(g9)
    c: Block(g10)
    c: Block(g11)
    c: Coincident(g12,g1)
    c: Coincident(g12,g2)
    c: Vertical(g12)
    c: Coincident(g13,g1)
    c: Coincident(g13,g2)
    c: Vertical(g13)
    c: Coincident(g14,g11)
    c: Coincident(g14,g7)
    c: Vertical(g14)
    c: Coincident(g15,g11)
    c: Coincident(g15,g7)
    c: Vertical(g15)
    c: Coincident(g16,g0)
    c: Coincident(g16,g3)
    c: Vertical(g16)
    c: Coincident(g17,g4)
    c: Coincident(g17,g8)
    c: Vertical(g17)
    c: Coincident(g18,g0)
    c: Coincident(g18,g3)
    c: Vertical(g18)
    c: Coincident(g19,g4)
    c: Coincident(g19,g8)
    c: Vertical(g19)
    c: Coincident(g20,g5)
    c: Coincident(g20,g9)
    c: Vertical(g20)
    c: Coincident(g21,g5)
    c: Coincident(g21,g9)
    c: Vertical(g21)
    c: Coincident(g22,g10)
    c: Coincident(g22,g6)
    c: Vertical(g22)
    c: Coincident(g23,g6)
    c: Coincident(g23,g10)
    c: Vertical(g23)
FEATURE [Part::Extrusion] Extrude048  label="removeToCreateFanGrillHoles004"
  Base = -> Sketch057
  Dir = (0,-1,6e-16)
  DirMode = 2
  FaceMakerClass = Part::FaceMakerBullseye
  LengthFwd = 10
  LengthRev = 0
  Placement = pos=(65.4,44,54.82) rot=(0,0,1;0rad)
  Solid = true
  Symmetric = false
FEATURE [Part::Cut] Cut040  label="top021"
  Base = -> Fillet039
  Tool = -> Extrude048
FEATURE [Part::Cylinder] Cylinder041  label="removeToCreteHoleForPlugHousing034"
  Angle = 360
  AttacherType = Attacher::AttachEngine3D
  Height = 20
  Placement = pos=(-2,19,36) rot=(0,1,0;1.5708rad)
  Radius = 14.3
FEATURE [Part::MultiFuse] Fusion089  label="removeToCreteHoleForPlugHousing035"
  Shapes = -> [Box026,Cylinder041]
FEATURE [Part::Cylinder] Cylinder042
  Angle = 360
  AttacherType = Attacher::AttachEngine3D
  Height = 20
  Placement = pos=(0,0,36.15) rot=(0,0,1;0rad)
  Radius = 14.3
FEATURE [Part::Cylinder] Cylinder043
  Angle = 360
  AttacherType = Attacher::AttachEngine3D
  Height = 10
  Placement = pos=(0,0,36.15) rot=(0,0,1;0rad)
  Radius = 4
FEATURE [Part::Box] Box027  label="removeToCreteHoleForPlugHousing036"
  AttacherType = Attacher::AttachEngine3D
  Height = 28.6
  Length = 20
  Placement = pos=(106.15,0,21.7) rot=(0,0,1;0rad)
  Width = 19
FEATURE [Part::Cut] Cut041  label="top022"
  Base = -> Cut040
  Tool = -> Fusion087
FEATURE [Part::Cut] Cut039  label="top020"
  Base = -> Cut041
  Tool = -> Fusion089
FEATURE [Part::MultiFuse] Fusion090  label="removeToCreteHoleForPlugHousing037"
  Placement = pos=(70,19,36) rot=(0,1,0;1.5708rad)
  Shapes = -> [Cylinder042,Cylinder043]
FEATURE [Part::MultiFuse] Fusion088  label="removeToCreteHoleForPlugHousing033"
  Shapes = -> [Box027,Fusion090]
FEATURE [Part::Cut] Cut042  label="removeToCreteHoleForPlugHousing038"
  Base = -> Cut039
  Tool = -> Fusion088
FEATURE [Part::MultiFuse] Fusion091  label="removeFromTop"
  Shapes = -> [Fillet038,Fusion085,Fusion084,Fusion083,Extrude045]
FEATURE [Part::Cut] Cut043  label="REAL TOP ====="
  Base = -> Fillet036
  Tool = -> Fusion091
FEATURE [Part::MultiFuse] Fusion092  label="caseScrewPillarBracket016"
  Shapes = -> [Extrude030,Extrude031,Extrude032,Extrude033,Extrude034,Extrude035,Extrude036,Extrude037,Box013,Box014]
FEATURE [Sketcher::SketchObject] Sketch058  label="topSketch015"
  FullyConstrained = true
  sketch-geometry (20):
    g0: LineSegment StartX=5.21097e-06 StartY=3 StartZ=0 EndX=5.21097e-06 EndY=19 EndZ=0
    g1: ArcOfCircle CenterX=19 CenterY=19 CenterZ=0 NormalX=0 NormalY=0 NormalZ=1 AngleXU=0 Radius=19 StartAngle=1.5708 EndAngle=3.14159
    g2: ArcOfCircle CenterX=19 CenterY=19 CenterZ=0 NormalX=0 NormalY=0 NormalZ=1 AngleXU=0 Radius=16 StartAngle=1.5708 EndAngle=3.14159
    g3: LineSegment StartX=114 StartY=35 StartZ=0 EndX=19 EndY=35 EndZ=0
    g4: LineSegment StartX=5.21097e-06 StartY=3 StartZ=0 EndX=5.21097e-06 EndY=0 EndZ=0
    g5: LineSegment StartX=3 StartY=0 StartZ=0 EndX=5.21097e-06 EndY=0 EndZ=0
    g6: LineSegment StartX=3 StartY=19 StartZ=0 EndX=3 EndY=0 EndZ=0
    g7: LineSegment StartX=19 StartY=38 StartZ=0 EndX=124 EndY=38 EndZ=0
    g8: Circle CenterX=119 CenterY=35 CenterZ=0 NormalX=0 NormalY=0 NormalZ=1 AngleXU=0 Radius=1
    g9: Circle CenterX=121 CenterY=35 CenterZ=0 NormalX=0 NormalY=0 NormalZ=1 AngleXU=0 Radius=1
    g10: Circle CenterX=121 CenterY=33 CenterZ=0 NormalX=0 NormalY=0 NormalZ=1 AngleXU=0 Radius=1
    g11: BSplineCurve PolesCount=3 KnotsCount=2 Degree=2 IsPeriodic=0
    g12: GeomPoint X=119 Y=35 Z=0
    g13: GeomPoint X=121 Y=33 Z=0
    g14: LineSegment StartX=119 StartY=35 StartZ=0 EndX=114 EndY=35 EndZ=0
    g15: ArcOfCircle CenterX=105 CenterY=19 CenterZ=0 NormalX=0 NormalY=0 NormalZ=1 AngleXU=0 Radius=19 StartAngle=5.7297 EndAngle=6.28319
    g16: ArcOfCircle CenterX=105 CenterY=19 CenterZ=0 NormalX=0 NormalY=0 NormalZ=1 AngleXU=0 Radius=16 StartAngle=5.60905 EndAngle=6.28319
    g17: LineSegment StartX=121 StartY=33 StartZ=0 EndX=121 EndY=19 EndZ=0
    g18: LineSegment StartX=124 StartY=38 StartZ=0 EndX=124 EndY=19 EndZ=0
    g19: LineSegment StartX=117.5 StartY=9.01251 StartZ=0 EndX=121.163 EndY=9.0125 EndZ=0
  constraints (46):
    c: Vertical(g0)
    c: Block(g0)
    c: Coincident(g1,g0)
    c: Block(g1)
    c: Coincident(g2,g1)
    c: Block(g2)
    c: Coincident(g3,g2)
    c: Horizontal(g3)
    c: Tangent(g3,g2)
    c: Coincident(g4,g0)
    c: Distance(g4) = 3
    c: Vertical(g4)
    c: Coincident(g5,g4)
    c: Horizontal(g5)
    c: Coincident(g6,g2)
    c: Coincident(g6,g5)
    c: Vertical(g6)
    c: Horizontal(g7)
    c: Distance(g7) = 105
    c: Coincident(g7,g1)
    c: Block(g3)
    c: Weight(g8) = 1
    c: Equal(g8,g9)
    c: Equal(g8,g10)
    c: InternalAlignment(g8,g11)
    c: InternalAlignment(g9,g11)
    c: InternalAlignment(g10,g11)
    c: InternalAlignment(g12,g11)
    c: InternalAlignment(g13,g11)
    c: Block(g11)
    c: Coincident(g14,g11)
    c: Coincident(g14,g3)
    c: Horizontal(g14)
    c: Block(g15)
    c: Coincident(g16,g15)
    c: Block(g16)
    c: Coincident(g17,g11)
    c: Coincident(g17,g16)
    c: Vertical(g17)
    c: Distance(g17) = 14
    c: Coincident(g18,g7)
    c: Coincident(g18,g15)
    c: Vertical(g18)
    c: Distance(g18) = 19
    c: Coincident(g19,g16)
    c: Coincident(g19,g15)
FEATURE [Part::Extrusion] Extrude049  label="top023"
  Base = -> Sketch058
  Dir = (0,0,1)
  DirMode = 2
  FaceMakerClass = Part::FaceMakerBullseye
  LengthFwd = 72
  LengthRev = 0
  Solid = true
  Symmetric = false
FEATURE [Sketcher::SketchObject] Sketch059
  FullyConstrained = true
  MapMode = 3
  Placement = pos=(0,0,0) rot=(1,0,0;1.5708rad)
  Support = -> [Extrude049]
  sketch-geometry (8):
    g0: Circle CenterX=80.351 CenterY=-67.6202 CenterZ=0 NormalX=0 NormalY=0 NormalZ=1 AngleXU=0 Radius=2
    g1: Circle CenterX=80.351 CenterY=-67.6202 CenterZ=0 NormalX=0 NormalY=0 NormalZ=1 AngleXU=0 Radius=3
    g2: Circle CenterX=80.351 CenterY=-4.92017 CenterZ=0 NormalX=0 NormalY=0 NormalZ=1 AngleXU=0 Radius=2
    g3: Circle CenterX=80.351 CenterY=-4.92017 CenterZ=0 NormalX=0 NormalY=0 NormalZ=1 AngleXU=0 Radius=3
    g4: Circle CenterX=23.851 CenterY=-4.92017 CenterZ=0 NormalX=0 NormalY=0 NormalZ=1 AngleXU=0 Radius=2
    g5: Circle CenterX=23.851 CenterY=-4.92017 CenterZ=0 NormalX=0 NormalY=0 NormalZ=1 AngleXU=0 Radius=3
    g6: Circle CenterX=23.851 CenterY=-67.6202 CenterZ=0 NormalX=0 NormalY=0 NormalZ=1 AngleXU=0 Radius=2
    g7: Circle CenterX=23.851 CenterY=-67.6202 CenterZ=0 NormalX=0 NormalY=0 NormalZ=1 AngleXU=0 Radius=3
  constraints (8):
    c: Block(g3)
    c: Block(g2)
    c: Block(g1)
    c: Block(g0)
    c: Block(g6)
    c: Block(g7)
    c: Block(g4)
    c: Block(g5)
FEATURE [Sketcher::SketchObject] Sketch060
  FullyConstrained = true
  MapMode = 3
  Placement = pos=(0,0,0) rot=(1,0,0;1.5708rad)
  Support = -> [Extrude049]
  sketch-geometry (8):
    g0: Circle CenterX=80.351 CenterY=-67.6202 CenterZ=0 NormalX=0 NormalY=0 NormalZ=1 AngleXU=0 Radius=3
    g1: Circle CenterX=80.351 CenterY=-4.92017 CenterZ=0 NormalX=0 NormalY=0 NormalZ=1 AngleXU=0 Radius=3
    g2: Circle CenterX=23.851 CenterY=-4.92017 CenterZ=0 NormalX=0 NormalY=0 NormalZ=1 AngleXU=0 Radius=3
    g3: Circle CenterX=23.851 CenterY=-67.6202 CenterZ=0 NormalX=0 NormalY=0 NormalZ=1 AngleXU=0 Radius=3
    g4: Circle CenterX=23.851 CenterY=-67.6202 CenterZ=0 NormalX=0 NormalY=0 NormalZ=1 AngleXU=0 Radius=5
    g5: Circle CenterX=80.351 CenterY=-67.6202 CenterZ=0 NormalX=0 NormalY=0 NormalZ=1 AngleXU=0 Radius=5
    g6: Circle CenterX=23.851 CenterY=-4.92017 CenterZ=0 NormalX=0 NormalY=0 NormalZ=1 AngleXU=0 Radius=5
    g7: Circle CenterX=80.351 CenterY=-4.92017 CenterZ=0 NormalX=0 NormalY=0 NormalZ=1 AngleXU=0 Radius=5
  constraints (8):
    c: Block(g1)
    c: Block(g0)
    c: Block(g3)
    c: Block(g2)
    c: Block(g5)
    c: Block(g4)
    c: Block(g6)
    c: Block(g7)
FEATURE [Sketcher::SketchObject] Sketch061
  FullyConstrained = true
  MapMode = 3
  Placement = pos=(0,0,0) rot=(1,0,0;1.5708rad)
  sketch-geometry (8):
    g0: Circle CenterX=80.351 CenterY=-67.6202 CenterZ=0 NormalX=0 NormalY=0 NormalZ=1 AngleXU=0 Radius=3
    g1: Circle CenterX=80.351 CenterY=-4.92017 CenterZ=0 NormalX=0 NormalY=0 NormalZ=1 AngleXU=0 Radius=3
    g2: Circle CenterX=23.851 CenterY=-4.92017 CenterZ=0 NormalX=0 NormalY=0 NormalZ=1 AngleXU=0 Radius=3
    g3: Circle CenterX=23.851 CenterY=-67.6202 CenterZ=0 NormalX=0 NormalY=0 NormalZ=1 AngleXU=0 Radius=3
    g4: Circle CenterX=23.851 CenterY=-67.6202 CenterZ=0 NormalX=0 NormalY=0 NormalZ=1 AngleXU=0 Radius=5
    g5: Circle CenterX=80.351 CenterY=-67.6202 CenterZ=0 NormalX=0 NormalY=0 NormalZ=1 AngleXU=0 Radius=5
    g6: Circle CenterX=23.851 CenterY=-4.92017 CenterZ=0 NormalX=0 NormalY=0 NormalZ=1 AngleXU=0 Radius=5
    g7: Circle CenterX=80.351 CenterY=-4.92017 CenterZ=0 NormalX=0 NormalY=0 NormalZ=1 AngleXU=0 Radius=5
  constraints (8):
    c: Block(g1)
    c: Block(g0)
    c: Block(g3)
    c: Block(g2)
    c: Block(g5)
    c: Block(g4)
    c: Block(g6)
    c: Block(g7)
FEATURE [Sketcher::SketchObject] Sketch062  label="topSketch016"
  FullyConstrained = true
  sketch-geometry (20):
    g0: LineSegment StartX=5.21097e-06 StartY=3 StartZ=0 EndX=5.21097e-06 EndY=19 EndZ=0
    g1: ArcOfCircle CenterX=19 CenterY=19 CenterZ=0 NormalX=0 NormalY=0 NormalZ=1 AngleXU=0 Radius=19 StartAngle=1.5708 EndAngle=3.14159
    g2: ArcOfCircle CenterX=19 CenterY=19 CenterZ=0 NormalX=0 NormalY=0 NormalZ=1 AngleXU=0 Radius=16 StartAngle=1.5708 EndAngle=3.14159
    g3: LineSegment StartX=114 StartY=35 StartZ=0 EndX=19 EndY=35 EndZ=0
    g4: LineSegment StartX=5.21097e-06 StartY=3 StartZ=0 EndX=5.21097e-06 EndY=0 EndZ=0
    g5: LineSegment StartX=3 StartY=0 StartZ=0 EndX=5.21097e-06 EndY=0 EndZ=0
    g6: LineSegment StartX=3 StartY=19 StartZ=0 EndX=3 EndY=0 EndZ=0
    g7: LineSegment StartX=19 StartY=38 StartZ=0 EndX=124 EndY=38 EndZ=0
    g8: Circle CenterX=119 CenterY=35 CenterZ=0 NormalX=0 NormalY=0 NormalZ=1 AngleXU=0 Radius=1
    g9: Circle CenterX=121 CenterY=35 CenterZ=0 NormalX=0 NormalY=0 NormalZ=1 AngleXU=0 Radius=1
    g10: Circle CenterX=121 CenterY=33 CenterZ=0 NormalX=0 NormalY=0 NormalZ=1 AngleXU=0 Radius=1
    g11: BSplineCurve PolesCount=3 KnotsCount=2 Degree=2 IsPeriodic=0
    g12: GeomPoint X=119 Y=35 Z=0
    g13: GeomPoint X=121 Y=33 Z=0
    g14: LineSegment StartX=119 StartY=35 StartZ=0 EndX=114 EndY=35 EndZ=0
    g15: ArcOfCircle CenterX=105 CenterY=19 CenterZ=0 NormalX=0 NormalY=0 NormalZ=1 AngleXU=0 Radius=19 StartAngle=5.7297 EndAngle=6.28319
    g16: ArcOfCircle CenterX=105 CenterY=19 CenterZ=0 NormalX=0 NormalY=0 NormalZ=1 AngleXU=0 Radius=16 StartAngle=5.60905 EndAngle=6.28319
    g17: LineSegment StartX=121 StartY=33 StartZ=0 EndX=121 EndY=19 EndZ=0
    g18: LineSegment StartX=124 StartY=38 StartZ=0 EndX=124 EndY=19 EndZ=0
    g19: LineSegment StartX=117.5 StartY=9.01251 StartZ=0 EndX=121.163 EndY=9.0125 EndZ=0
  constraints (46):
    c: Vertical(g0)
    c: Block(g0)
    c: Coincident(g1,g0)
    c: Block(g1)
    c: Coincident(g2,g1)
    c: Block(g2)
    c: Coincident(g3,g2)
    c: Horizontal(g3)
    c: Tangent(g3,g2)
    c: Coincident(g4,g0)
    c: Distance(g4) = 3
    c: Vertical(g4)
    c: Coincident(g5,g4)
    c: Horizontal(g5)
    c: Coincident(g6,g2)
    c: Coincident(g6,g5)
    c: Vertical(g6)
    c: Horizontal(g7)
    c: Distance(g7) = 105
    c: Coincident(g7,g1)
    c: Block(g3)
    c: Weight(g8) = 1
    c: Equal(g8,g9)
    c: Equal(g8,g10)
    c: InternalAlignment(g8,g11)
    c: InternalAlignment(g9,g11)
    c: InternalAlignment(g10,g11)
    c: InternalAlignment(g12,g11)
    c: InternalAlignment(g13,g11)
    c: Block(g11)
    c: Coincident(g14,g11)
    c: Coincident(g14,g3)
    c: Horizontal(g14)
    c: Block(g15)
    c: Coincident(g16,g15)
    c: Block(g16)
    c: Coincident(g17,g11)
    c: Coincident(g17,g16)
    c: Vertical(g17)
    c: Distance(g17) = 14
    c: Coincident(g18,g7)
    c: Coincident(g18,g15)
    c: Vertical(g18)
    c: Distance(g18) = 19
    c: Coincident(g19,g16)
    c: Coincident(g19,g15)
FEATURE [Part::Extrusion] Extrude053  label="top024"
  Base = -> Sketch062
  Dir = (0,0,1)
  DirMode = 2
  FaceMakerClass = Part::FaceMakerBullseye
  LengthFwd = 72
  LengthRev = 0
  Solid = true
  Symmetric = false
FEATURE [Sketcher::SketchObject] Sketch063
  FullyConstrained = true
  MapMode = 3
  Placement = pos=(0,0,0) rot=(1,0,0;1.5708rad)
  Support = -> [Extrude053]
  sketch-geometry (8):
    g0: Circle CenterX=80.351 CenterY=-67.6202 CenterZ=0 NormalX=0 NormalY=0 NormalZ=1 AngleXU=0 Radius=2
    g1: Circle CenterX=80.351 CenterY=-67.6202 CenterZ=0 NormalX=0 NormalY=0 NormalZ=1 AngleXU=0 Radius=3
    g2: Circle CenterX=80.351 CenterY=-4.92017 CenterZ=0 NormalX=0 NormalY=0 NormalZ=1 AngleXU=0 Radius=2
    g3: Circle CenterX=80.351 CenterY=-4.92017 CenterZ=0 NormalX=0 NormalY=0 NormalZ=1 AngleXU=0 Radius=3
    g4: Circle CenterX=23.851 CenterY=-4.92017 CenterZ=0 NormalX=0 NormalY=0 NormalZ=1 AngleXU=0 Radius=2
    g5: Circle CenterX=23.851 CenterY=-4.92017 CenterZ=0 NormalX=0 NormalY=0 NormalZ=1 AngleXU=0 Radius=3
    g6: Circle CenterX=23.851 CenterY=-67.6202 CenterZ=0 NormalX=0 NormalY=0 NormalZ=1 AngleXU=0 Radius=2
    g7: Circle CenterX=23.851 CenterY=-67.6202 CenterZ=0 NormalX=0 NormalY=0 NormalZ=1 AngleXU=0 Radius=3
  constraints (8):
    c: Block(g3)
    c: Block(g2)
    c: Block(g1)
    c: Block(g0)
    c: Block(g6)
    c: Block(g7)
    c: Block(g4)
    c: Block(g5)
FEATURE [Part::Extrusion] Extrude054
  Base = -> Sketch063
  Dir = (0,-1,2e-16)
  DirMode = 2
  FaceMakerClass = Part::FaceMakerBullseye
  LengthFwd = 6
  LengthRev = 0
  Placement = pos=(0,9,0) rot=(0,0,1;0rad)
  Solid = true
  Symmetric = false
FEATURE [Sketcher::SketchObject] Sketch064  label="topSketch017"
  FullyConstrained = true
  sketch-geometry (20):
    g0: LineSegment StartX=5.21097e-06 StartY=3 StartZ=0 EndX=5.21097e-06 EndY=19 EndZ=0
    g1: ArcOfCircle CenterX=19 CenterY=19 CenterZ=0 NormalX=0 NormalY=0 NormalZ=1 AngleXU=0 Radius=19 StartAngle=1.5708 EndAngle=3.14159
    g2: ArcOfCircle CenterX=19 CenterY=19 CenterZ=0 NormalX=0 NormalY=0 NormalZ=1 AngleXU=0 Radius=16 StartAngle=1.5708 EndAngle=3.14159
    g3: LineSegment StartX=114 StartY=35 StartZ=0 EndX=19 EndY=35 EndZ=0
    g4: LineSegment StartX=5.21097e-06 StartY=3 StartZ=0 EndX=5.21097e-06 EndY=0 EndZ=0
    g5: LineSegment StartX=3 StartY=0 StartZ=0 EndX=5.21097e-06 EndY=0 EndZ=0
    g6: LineSegment StartX=3 StartY=19 StartZ=0 EndX=3 EndY=0 EndZ=0
    g7: LineSegment StartX=19 StartY=38 StartZ=0 EndX=124 EndY=38 EndZ=0
    g8: Circle CenterX=119 CenterY=35 CenterZ=0 NormalX=0 NormalY=0 NormalZ=1 AngleXU=0 Radius=1
    g9: Circle CenterX=121 CenterY=35 CenterZ=0 NormalX=0 NormalY=0 NormalZ=1 AngleXU=0 Radius=1
    g10: Circle CenterX=121 CenterY=33 CenterZ=0 NormalX=0 NormalY=0 NormalZ=1 AngleXU=0 Radius=1
    g11: BSplineCurve PolesCount=3 KnotsCount=2 Degree=2 IsPeriodic=0
    g12: GeomPoint X=119 Y=35 Z=0
    g13: GeomPoint X=121 Y=33 Z=0
    g14: LineSegment StartX=119 StartY=35 StartZ=0 EndX=114 EndY=35 EndZ=0
    g15: ArcOfCircle CenterX=105 CenterY=19 CenterZ=0 NormalX=0 NormalY=0 NormalZ=1 AngleXU=0 Radius=19 StartAngle=5.7297 EndAngle=6.28319
    g16: ArcOfCircle CenterX=105 CenterY=19 CenterZ=0 NormalX=0 NormalY=0 NormalZ=1 AngleXU=0 Radius=16 StartAngle=5.60905 EndAngle=6.28319
    g17: LineSegment StartX=121 StartY=33 StartZ=0 EndX=121 EndY=19 EndZ=0
    g18: LineSegment StartX=124 StartY=38 StartZ=0 EndX=124 EndY=19 EndZ=0
    g19: LineSegment StartX=117.5 StartY=9.01251 StartZ=0 EndX=121.163 EndY=9.0125 EndZ=0
  constraints (46):
    c: Vertical(g0)
    c: Block(g0)
    c: Coincident(g1,g0)
    c: Block(g1)
    c: Coincident(g2,g1)
    c: Block(g2)
    c: Coincident(g3,g2)
    c: Horizontal(g3)
    c: Tangent(g3,g2)
    c: Coincident(g4,g0)
    c: Distance(g4) = 3
    c: Vertical(g4)
    c: Coincident(g5,g4)
    c: Horizontal(g5)
    c: Coincident(g6,g2)
    c: Coincident(g6,g5)
    c: Vertical(g6)
    c: Horizontal(g7)
    c: Distance(g7) = 105
    c: Coincident(g7,g1)
    c: Block(g3)
    c: Weight(g8) = 1
    c: Equal(g8,g9)
    c: Equal(g8,g10)
    c: InternalAlignment(g8,g11)
    c: InternalAlignment(g9,g11)
    c: InternalAlignment(g10,g11)
    c: InternalAlignment(g12,g11)
    c: InternalAlignment(g13,g11)
    c: Block(g11)
    c: Coincident(g14,g11)
    c: Coincident(g14,g3)
    c: Horizontal(g14)
    c: Block(g15)
    c: Coincident(g16,g15)
    c: Block(g16)
    c: Coincident(g17,g11)
    c: Coincident(g17,g16)
    c: Vertical(g17)
    c: Distance(g17) = 14
    c: Coincident(g18,g7)
    c: Coincident(g18,g15)
    c: Vertical(g18)
    c: Distance(g18) = 19
    c: Coincident(g19,g16)
    c: Coincident(g19,g15)
FEATURE [Sketcher::SketchObject] Sketch065
  FullyConstrained = true
  MapMode = 3
  Placement = pos=(0,0,0) rot=(1,0,0;1.5708rad)
  sketch-geometry (8):
    g0: Circle CenterX=80.351 CenterY=-67.6202 CenterZ=0 NormalX=0 NormalY=0 NormalZ=1 AngleXU=0 Radius=3
    g1: Circle CenterX=80.351 CenterY=-4.92017 CenterZ=0 NormalX=0 NormalY=0 NormalZ=1 AngleXU=0 Radius=3
    g2: Circle CenterX=23.851 CenterY=-4.92017 CenterZ=0 NormalX=0 NormalY=0 NormalZ=1 AngleXU=0 Radius=3
    g3: Circle CenterX=23.851 CenterY=-67.6202 CenterZ=0 NormalX=0 NormalY=0 NormalZ=1 AngleXU=0 Radius=3
    g4: Circle CenterX=23.851 CenterY=-67.6202 CenterZ=0 NormalX=0 NormalY=0 NormalZ=1 AngleXU=0 Radius=5
    g5: Circle CenterX=80.351 CenterY=-67.6202 CenterZ=0 NormalX=0 NormalY=0 NormalZ=1 AngleXU=0 Radius=5
    g6: Circle CenterX=23.851 CenterY=-4.92017 CenterZ=0 NormalX=0 NormalY=0 NormalZ=1 AngleXU=0 Radius=5
    g7: Circle CenterX=80.351 CenterY=-4.92017 CenterZ=0 NormalX=0 NormalY=0 NormalZ=1 AngleXU=0 Radius=5
  constraints (8):
    c: Block(g1)
    c: Block(g0)
    c: Block(g3)
    c: Block(g2)
    c: Block(g5)
    c: Block(g4)
    c: Block(g6)
    c: Block(g7)
FEATURE [Part::Extrusion] Extrude056
  Base = -> Sketch065
  Dir = (0,-1,2e-16)
  DirMode = 2
  FaceMakerClass = Part::FaceMakerBullseye
  LengthFwd = 2
  LengthRev = 0
  Solid = true
  Symmetric = false
FEATURE [Part::Extrusion] Extrude057  label="top025"
  Base = -> Sketch064
  Dir = (0,0,1)
  DirMode = 2
  FaceMakerClass = Part::FaceMakerBullseye
  LengthFwd = 72
  LengthRev = 0
  Solid = true
  Symmetric = false
FEATURE [Sketcher::SketchObject] Sketch066
  FullyConstrained = true
  MapMode = 3
  Placement = pos=(0,0,0) rot=(1,0,0;1.5708rad)
  Support = -> [Extrude057]
  sketch-geometry (8):
    g0: Circle CenterX=80.351 CenterY=-67.6202 CenterZ=0 NormalX=0 NormalY=0 NormalZ=1 AngleXU=0 Radius=3
    g1: Circle CenterX=80.351 CenterY=-4.92017 CenterZ=0 NormalX=0 NormalY=0 NormalZ=1 AngleXU=0 Radius=3
    g2: Circle CenterX=23.851 CenterY=-4.92017 CenterZ=0 NormalX=0 NormalY=0 NormalZ=1 AngleXU=0 Radius=3
    g3: Circle CenterX=23.851 CenterY=-67.6202 CenterZ=0 NormalX=0 NormalY=0 NormalZ=1 AngleXU=0 Radius=3
    g4: Circle CenterX=23.851 CenterY=-67.6202 CenterZ=0 NormalX=0 NormalY=0 NormalZ=1 AngleXU=0 Radius=5
    g5: Circle CenterX=80.351 CenterY=-67.6202 CenterZ=0 NormalX=0 NormalY=0 NormalZ=1 AngleXU=0 Radius=5
    g6: Circle CenterX=23.851 CenterY=-4.92017 CenterZ=0 NormalX=0 NormalY=0 NormalZ=1 AngleXU=0 Radius=5
    g7: Circle CenterX=80.351 CenterY=-4.92017 CenterZ=0 NormalX=0 NormalY=0 NormalZ=1 AngleXU=0 Radius=5
  constraints (8):
    c: Block(g1)
    c: Block(g0)
    c: Block(g3)
    c: Block(g2)
    c: Block(g5)
    c: Block(g4)
    c: Block(g6)
    c: Block(g7)
FEATURE [Part::Extrusion] Extrude055
  Base = -> Sketch066
  Dir = (0,-1,2e-16)
  DirMode = 2
  FaceMakerClass = Part::FaceMakerBullseye
  LengthFwd = 2
  LengthRev = 0
  Solid = true
  Symmetric = false
FEATURE [Part::Fillet] Fillet041
  Base = -> Extrude056
  Edges = 4 edges r=1.99: [Edge6,Edge12,Edge18,Edge24]
FEATURE [Part::Cut] Cut045
  Base = -> Extrude055
  Placement = pos=(0,6,0) rot=(0,0,1;0rad)
  Tool = -> Fillet041
FEATURE [Part::MultiFuse] Fusion095  label="pcbScrewPillars"
  Placement = pos=(-3.2,-1,72.3) rot=(0,0,1;0rad)
  Shapes = -> [Cut045,Extrude054]
FEATURE [Part::Feature] Face113
  shape: bbox 3.2 x 1.5 x 2e-07 mm, 1 faces, 0 solids (baked)
FEATURE [Part::Revolution] Revolve121  label="backCaseScrewRetainer002"
  Angle = 360
  Axis = (0,1,0)
  Base = (0,0,0)
  FaceMakerClass = Part::FaceMakerBullseye
  Placement = pos=(12.5,3,62) rot=(0,0,1;0rad)
  Solid = false
  Source = -> Face113
  Symmetric = false
FEATURE [Part::Feature] Face114
  shape: bbox 3.2 x 1.5 x 2e-07 mm, 1 faces, 0 solids (baked)
FEATURE [Part::Feature] Face115
  shape: bbox 3.2 x 1.5 x 2e-07 mm, 1 faces, 0 solids (baked)
FEATURE [Part::Feature] Face116
  shape: bbox 3.2 x 1.5 x 2e-07 mm, 1 faces, 0 solids (baked)
FEATURE [Part::Revolution] Revolve122  label="frontCaseScrewRetainer004"
  Angle = 360
  Axis = (0,1,0)
  Base = (0,0,0)
  FaceMakerClass = Part::FaceMakerBullseye
  Placement = pos=(89.5,3,68.5) rot=(0,0,1;0rad)
  Solid = false
  Source = -> Face115
  Symmetric = false
FEATURE [Part::Revolution] Revolve123  label="frontCaseScrewRetainer005"
  Angle = 360
  Axis = (0,1,0)
  Base = (0,0,0)
  FaceMakerClass = Part::FaceMakerBullseye
  Placement = pos=(89.5,3,3.5) rot=(0,0,1;0rad)
  Solid = false
  Source = -> Face116
  Symmetric = false
FEATURE [Part::Revolution] Revolve124  label="backCaseScrewRetainer003"
  Angle = 360
  Axis = (0,1,0)
  Base = (0,0,0)
  FaceMakerClass = Part::FaceMakerBullseye
  Placement = pos=(12.5,3,10) rot=(0,0,1;0rad)
  Solid = false
  Source = -> Face114
  Symmetric = false
FEATURE [Part::Feature] Face117
  shape: bbox 3.6 x 3.2 x 2e-07 mm, 1 faces, 0 solids (baked)
FEATURE [Part::Revolution] Revolve125  label="moreFrontCaseScrewRetainer004"
  Angle = 360
  Axis = (0,1,0)
  Base = (0,0,0)
  FaceMakerClass = Part::FaceMakerBullseye
  Placement = pos=(109.5,4.5,68.5) rot=(0,0,1;0rad)
  Solid = false
  Source = -> Face117
  Symmetric = false
FEATURE [Part::Feature] Face118
  shape: bbox 3.6 x 3.2 x 2e-07 mm, 1 faces, 0 solids (baked)
FEATURE [Part::Revolution] Revolve126  label="moreFrontCaseScrewRetainer005"
  Angle = 360
  Axis = (0,1,0)
  Base = (0,0,0)
  FaceMakerClass = Part::FaceMakerBullseye
  Placement = pos=(109.5,4.5,3.5) rot=(0,0,1;0rad)
  Solid = false
  Source = -> Face118
  Symmetric = false
FEATURE [Part::MultiFuse] Fusion096  label="screwRetainers001"
  Shapes = -> [Revolve126,Revolve125,Revolve124,Revolve123,Revolve122,Revolve121]
FEATURE [Part::Feature] Face119
  shape: bbox 10 x 16.5 x 2e-07 mm, 1 faces, 0 solids (baked)
FEATURE [Part::Revolution] Revolve130  label="plugHousing050"
  Angle = 360
  Axis = (0,1,0)
  Base = (0,0,0)
  FaceMakerClass = Part::FaceMakerBullseye
  Placement = pos=(0,0,36.15) rot=(0,0,1;0rad)
  Solid = false
  Source = -> Face119
  Symmetric = false
FEATURE [Part::Feature] Face120
  shape: bbox 10 x 16.5 x 2e-07 mm, 1 faces, 0 solids (baked)
FEATURE [Part::Feature] Face121
  shape: bbox 10 x 16.5 x 2e-07 mm, 1 faces, 0 solids (baked)
FEATURE [Part::Revolution] Revolve127  label="plugHousing047"
  Angle = 360
  Axis = (0,1,0)
  Base = (0,0,0)
  FaceMakerClass = Part::FaceMakerBullseye
  Placement = pos=(0,0,36.15) rot=(0,0,1;0rad)
  Solid = false
  Source = -> Face121
  Symmetric = false
FEATURE [Part::Feature] Face122
  shape: bbox 10 x 16.5 x 2e-07 mm, 1 faces, 0 solids (baked)
FEATURE [Part::Feature] Face123
  shape: bbox 10 x 16.5 x 2e-07 mm, 1 faces, 0 solids (baked)
FEATURE [Part::Revolution] Revolve128  label="plugHousing048"
  Angle = 360
  Axis = (0,1,0)
  Base = (0,0,0)
  FaceMakerClass = Part::FaceMakerBullseye
  Placement = pos=(0,0,36.15) rot=(0,0,1;0rad)
  Solid = false
  Source = -> Face123
  Symmetric = false
FEATURE [Part::MultiFuse] Fusion100  label="plugHousing054"
  Placement = pos=(0,0,0) rot=(0,0,1;1.5708rad)
  Shapes = -> [Revolve130,Revolve128]
FEATURE [Part::Feature] Face124
  shape: bbox 10 x 16.5 x 2e-07 mm, 1 faces, 0 solids (baked)
FEATURE [Part::Feature] Face125
  shape: bbox 10 x 16.5 x 2e-07 mm, 1 faces, 0 solids (baked)
FEATURE [Part::Revolution] Revolve129  label="plugHousing049"
  Angle = 360
  Axis = (0,1,0)
  Base = (0,0,0)
  FaceMakerClass = Part::FaceMakerBullseye
  Placement = pos=(0,0,36.15) rot=(0,0,1;0rad)
  Solid = false
  Source = -> Face125
  Symmetric = false
FEATURE [Part::Feature] Face126
  shape: bbox 10 x 16.5 x 2e-07 mm, 1 faces, 0 solids (baked)
FEATURE [Part::Revolution] Revolve131  label="plugHousing058"
  Angle = 360
  Axis = (0,1,0)
  Base = (0,0,0)
  FaceMakerClass = Part::FaceMakerBullseye
  Placement = pos=(0,0,36.15) rot=(0,0,1;0rad)
  Solid = false
  Source = -> Face120
  Symmetric = false
FEATURE [Part::MultiFuse] Fusion099  label="plugHousing053"
  Placement = pos=(0,0,0) rot=(0,0,1;1.5708rad)
  Shapes = -> [Revolve127,Revolve131]
FEATURE [Part::MultiFuse] Fusion102  label="plugHousing056"
  Placement = pos=(0,19,0) rot=(0,0,1;3.14159rad)
  Shapes = -> [Fusion100,Fusion099]
FEATURE [Part::Revolution] Revolve132  label="plugHousing059"
  Angle = 360
  Axis = (0,1,0)
  Base = (0,0,0)
  FaceMakerClass = Part::FaceMakerBullseye
  Placement = pos=(0,0,36.15) rot=(0,0,1;0rad)
  Solid = false
  Source = -> Face126
  Symmetric = false
FEATURE [Part::Revolution] Revolve133  label="plugHousing060"
  Angle = 360
  Axis = (0,1,0)
  Base = (0,0,0)
  FaceMakerClass = Part::FaceMakerBullseye
  Placement = pos=(0,0,36.15) rot=(0,0,1;0rad)
  Solid = false
  Source = -> Face122
  Symmetric = false
FEATURE [Part::MultiFuse] Fusion097  label="plugHousing051"
  Placement = pos=(0,0,0) rot=(0,0,1;1.5708rad)
  Shapes = -> [Revolve133,Revolve132]
FEATURE [Part::Revolution] Revolve134  label="plugHousing061"
  Angle = 360
  Axis = (0,1,0)
  Base = (0,0,0)
  FaceMakerClass = Part::FaceMakerBullseye
  Placement = pos=(0,0,36.15) rot=(0,0,1;0rad)
  Solid = false
  Source = -> Face124
  Symmetric = false
FEATURE [Part::MultiFuse] Fusion101  label="plugHousing055"
  Placement = pos=(0,0,0) rot=(0,0,1;1.5708rad)
  Shapes = -> [Revolve129,Revolve134]
FEATURE [Part::MultiFuse] Fusion098  label="plugHousing052"
  Placement = pos=(0,19,0) rot=(0,0,1;3.14159rad)
  Shapes = -> [Fusion097,Fusion101]
FEATURE [Part::MultiFuse] Fusion103  label="plugHousing057"
  Placement = pos=(122.621,0,-0.15) rot=(0,0,1;0rad)
  Shapes = -> [Fusion102,Fusion098]
FEATURE [Part::Box] Box028  label="Cube015"
  AttacherType = Attacher::AttachEngine3D
  Height = 28
  Length = 3
  Placement = pos=(110.7,19,22) rot=(0,0,1;0rad)
  Width = 15.7
FEATURE [Part::Cylinder] Cylinder044
  Angle = 360
  AttacherType = Attacher::AttachEngine3D
  Height = 20
  Placement = pos=(0,0,36.15) rot=(0,0,1;0rad)
  Radius = 10.3
FEATURE [Part::Cylinder] Cylinder045
  Angle = 360
  AttacherType = Attacher::AttachEngine3D
  Height = 10
  Placement = pos=(0,0,36.15) rot=(0,0,1;0rad)
  Radius = 4
FEATURE [Part::MultiFuse] Fusion104  label="removeToCreteHoleForPlugHousing040"
  Placement = pos=(70,19,36) rot=(0,1,0;1.5708rad)
  Shapes = -> [Cylinder044,Cylinder045]
FEATURE [Part::Cut] Cut046  label="plugHousingTab003"
  Base = -> Box028
  Tool = -> Fusion104
FEATURE [Part::MultiFuse] Fusion105  label="plugHousing062"
  Shapes = -> [Fusion103,Cut046]
FEATURE [Part::Fillet] Fillet042
  Base = -> Fusion105
  Edges = 1 edges r=2: [Edge25]
FEATURE [Part::Fillet] Fillet043  label="plugHousing063"
  Base = -> Fillet042
  Edges = 1 edges r=2: [Edge8]
  Placement = pos=(7,0,0) rot=(0,0,1;0rad)
FEATURE [Part::Feature] Face127
  shape: bbox 10 x 16.5 x 2e-07 mm, 1 faces, 0 solids (baked)
FEATURE [Part::Feature] Face128
  shape: bbox 10 x 16.5 x 2e-07 mm, 1 faces, 0 solids (baked)
FEATURE [Part::Revolution] Revolve137  label="plugHousing070"
  Angle = 360
  Axis = (0,1,0)
  Base = (0,0,0)
  FaceMakerClass = Part::FaceMakerBullseye
  Placement = pos=(0,0,36.15) rot=(0,0,1;0rad)
  Solid = false
  Source = -> Face127
  Symmetric = false
FEATURE [Part::Revolution] Revolve140  label="plugHousing073"
  Angle = 360
  Axis = (0,1,0)
  Base = (0,0,0)
  FaceMakerClass = Part::FaceMakerBullseye
  Placement = pos=(0,0,36.15) rot=(0,0,1;0rad)
  Solid = false
  Source = -> Face128
  Symmetric = false
FEATURE [Part::Feature] Face129
  shape: bbox 10 x 16.5 x 2e-07 mm, 1 faces, 0 solids (baked)
FEATURE [Part::Revolution] Revolve138  label="plugHousing071"
  Angle = 360
  Axis = (0,1,0)
  Base = (0,0,0)
  FaceMakerClass = Part::FaceMakerBullseye
  Placement = pos=(0,0,36.15) rot=(0,0,1;0rad)
  Solid = false
  Source = -> Face129
  Symmetric = false
FEATURE [Part::Feature] Face130
  shape: bbox 10 x 16.5 x 2e-07 mm, 1 faces, 0 solids (baked)
FEATURE [Part::Revolution] Revolve139  label="plugHousing072"
  Angle = 360
  Axis = (0,1,0)
  Base = (0,0,0)
  FaceMakerClass = Part::FaceMakerBullseye
  Placement = pos=(0,0,36.15) rot=(0,0,1;0rad)
  Solid = false
  Source = -> Face130
  Symmetric = false
FEATURE [Part::Feature] Face131
  shape: bbox 10 x 16.5 x 2e-07 mm, 1 faces, 0 solids (baked)
FEATURE [Part::Revolution] Revolve135  label="plugHousing068"
  Angle = 360
  Axis = (0,1,0)
  Base = (0,0,0)
  FaceMakerClass = Part::FaceMakerBullseye
  Placement = pos=(0,0,36.15) rot=(0,0,1;0rad)
  Solid = false
  Source = -> Face131
  Symmetric = false
FEATURE [Part::MultiFuse] Fusion112  label="plugHousing078"
  Placement = pos=(0,0,0) rot=(0,0,1;1.5708rad)
  Shapes = -> [Revolve135,Revolve139]
FEATURE [Part::Feature] Face132
  shape: bbox 10 x 16.5 x 2e-07 mm, 1 faces, 0 solids (baked)
FEATURE [Part::Revolution] Revolve141  label="plugHousing074"
  Angle = 360
  Axis = (0,1,0)
  Base = (0,0,0)
  FaceMakerClass = Part::FaceMakerBullseye
  Placement = pos=(0,0,36.15) rot=(0,0,1;0rad)
  Solid = false
  Source = -> Face132
  Symmetric = false
FEATURE [Part::MultiFuse] Fusion110  label="plugHousing076"
  Placement = pos=(0,0,0) rot=(0,0,1;1.5708rad)
  Shapes = -> [Revolve141,Revolve140]
FEATURE [Part::Feature] Face133
  shape: bbox 10 x 16.5 x 2e-07 mm, 1 faces, 0 solids (baked)
FEATURE [Part::Revolution] Revolve136  label="plugHousing069"
  Angle = 360
  Axis = (0,1,0)
  Base = (0,0,0)
  FaceMakerClass = Part::FaceMakerBullseye
  Placement = pos=(0,0,36.15) rot=(0,0,1;0rad)
  Solid = false
  Source = -> Face133
  Symmetric = false
FEATURE [Part::MultiFuse] Fusion106  label="plugHousing064"
  Placement = pos=(0,0,0) rot=(0,0,1;1.5708rad)
  Shapes = -> [Revolve138,Revolve136]
FEATURE [Part::MultiFuse] Fusion108  label="plugHousing066"
  Placement = pos=(0,19,0) rot=(0,0,1;3.14159rad)
  Shapes = -> [Fusion106,Fusion112]
FEATURE [Part::Feature] Face134
  shape: bbox 10 x 16.5 x 2e-07 mm, 1 faces, 0 solids (baked)
FEATURE [Part::Revolution] Revolve142  label="plugHousing075"
  Angle = 360
  Axis = (0,1,0)
  Base = (0,0,0)
  FaceMakerClass = Part::FaceMakerBullseye
  Placement = pos=(0,0,36.15) rot=(0,0,1;0rad)
  Solid = false
  Source = -> Face134
  Symmetric = false
FEATURE [Part::MultiFuse] Fusion107  label="plugHousing065"
  Placement = pos=(0,0,0) rot=(0,0,1;1.5708rad)
  Shapes = -> [Revolve137,Revolve142]
FEATURE [Part::MultiFuse] Fusion111  label="plugHousing077"
  Placement = pos=(0,19,0) rot=(0,0,1;3.14159rad)
  Shapes = -> [Fusion110,Fusion107]
FEATURE [Part::MultiFuse] Fusion109  label="plugHousing067"
  Placement = pos=(131.236,0,-0.15) rot=(0,0,1;0rad)
  Shapes = -> [Fusion108,Fusion111]
FEATURE [Part::MultiFuse] Fusion113  label="plugHousing079"
  Shapes = -> [Fillet043,Fusion109]
FEATURE [Part::Feature] Face135
  shape: bbox 3.5 x 17.8 x 2e-07 mm, 1 faces, 0 solids (baked)
FEATURE [Part::Revolution] Revolve143  label="removeToCreateScrewAndThreadedInsertHole049"
  Angle = 360
  Axis = (0,1,0)
  Base = (0,0,0)
  FaceMakerClass = Part::FaceMakerBullseye
  Placement = pos=(12.5,0,10) rot=(0,0,1;0rad)
  Solid = false
  Source = -> Face135
  Symmetric = false
FEATURE [Part::Feature] Face136
  shape: bbox 3.5 x 17.8 x 2e-07 mm, 1 faces, 0 solids (baked)
FEATURE [Part::Revolution] Revolve144  label="removeToCreateScrewAndThreadedInsertHole050"
  Angle = 360
  Axis = (0,1,0)
  Base = (0,0,0)
  FaceMakerClass = Part::FaceMakerBullseye
  Placement = pos=(12.5,0,62) rot=(0,0,1;0rad)
  Solid = false
  Source = -> Face136
  Symmetric = false
FEATURE [Part::Feature] Face137
  shape: bbox 3.5 x 17.8 x 2e-07 mm, 1 faces, 0 solids (baked)
FEATURE [Part::Revolution] Revolve145  label="removeToCreateScrewAndThreadedInsertHole051"
  Angle = 360
  Axis = (0,1,0)
  Base = (0,0,0)
  FaceMakerClass = Part::FaceMakerBullseye
  Placement = pos=(89.5,0,68.5) rot=(0,0,1;0rad)
  Solid = false
  Source = -> Face137
  Symmetric = false
FEATURE [Part::Feature] Face138
  shape: bbox 3.5 x 17.8 x 2e-07 mm, 1 faces, 0 solids (baked)
FEATURE [Part::Revolution] Revolve146  label="removeToCreateScrewAndThreadedInsertHole052"
  Angle = 360
  Axis = (0,1,0)
  Base = (0,0,0)
  FaceMakerClass = Part::FaceMakerBullseye
  Placement = pos=(89.5,0,3.5) rot=(0,0,1;0rad)
  Solid = false
  Source = -> Face138
  Symmetric = false
FEATURE [Part::Feature] Face139
  shape: bbox 3.5 x 17.8 x 2e-07 mm, 1 faces, 0 solids (baked)
FEATURE [Part::Revolution] Revolve147  label="removeToCreateScrewAndThreadedInsertHole053"
  Angle = 360
  Axis = (0,1,0)
  Base = (0,0,0)
  FaceMakerClass = Part::FaceMakerBullseye
  Placement = pos=(109.5,4.7,3.5) rot=(0,0,1;0rad)
  Solid = false
  Source = -> Face139
  Symmetric = false
FEATURE [Part::Feature] Face140
  shape: bbox 3.5 x 17.8 x 2e-07 mm, 1 faces, 0 solids (baked)
FEATURE [Part::Revolution] Revolve148  label="removeToCreateScrewAndThreadedInsertHole054"
  Angle = 360
  Axis = (0,1,0)
  Base = (0,0,0)
  FaceMakerClass = Part::FaceMakerBullseye
  Placement = pos=(109.5,4.7,68.5) rot=(0,0,1;0rad)
  Solid = false
  Source = -> Face140
  Symmetric = false
FEATURE [Part::MultiFuse] Fusion114  label="removeToCreateScrewAndThreadedInsertHole055"
  Shapes = -> [Revolve148,Revolve147,Revolve146,Revolve145,Revolve144,Revolve143]
FEATURE [Part::Cut] Cut047  label="casePillars004"
  Base = -> Cut037
  Tool = -> Fusion114
FEATURE [Part::Feature] Face141
  shape: bbox 3.5 x 17.8 x 2e-07 mm, 1 faces, 0 solids (baked)
FEATURE [Part::Feature] Face142
  shape: bbox 3.5 x 17.8 x 2e-07 mm, 1 faces, 0 solids (baked)
FEATURE [Part::Feature] Face143
  shape: bbox 3.5 x 17.8 x 2e-07 mm, 1 faces, 0 solids (baked)
FEATURE [Part::Revolution] Revolve149  label="removeToCreateScrewAndThreadedInsertHole057"
  Angle = 360
  Axis = (0,1,0)
  Base = (0,0,0)
  FaceMakerClass = Part::FaceMakerBullseye
  Placement = pos=(12.5,0,10) rot=(0,0,1;0rad)
  Solid = false
  Source = -> Face141
  Symmetric = false
FEATURE [Part::Feature] Face144
  shape: bbox 3.5 x 17.8 x 2e-07 mm, 1 faces, 0 solids (baked)
FEATURE [Part::Feature] Face145
  shape: bbox 3.5 x 17.8 x 2e-07 mm, 1 faces, 0 solids (baked)
FEATURE [Part::Feature] Face146
  shape: bbox 3.5 x 17.8 x 2e-07 mm, 1 faces, 0 solids (baked)
FEATURE [Part::Revolution] Revolve150  label="removeToCreateScrewAndThreadedInsertHole058"
  Angle = 360
  Axis = (0,1,0)
  Base = (0,0,0)
  FaceMakerClass = Part::FaceMakerBullseye
  Placement = pos=(12.5,0,62) rot=(0,0,1;0rad)
  Solid = false
  Source = -> Face146
  Symmetric = false
FEATURE [Part::Revolution] Revolve151  label="removeToCreateScrewAndThreadedInsertHole059"
  Angle = 360
  Axis = (0,1,0)
  Base = (0,0,0)
  FaceMakerClass = Part::FaceMakerBullseye
  Placement = pos=(89.5,0,68.5) rot=(0,0,1;0rad)
  Solid = false
  Source = -> Face143
  Symmetric = false
FEATURE [Part::Revolution] Revolve152  label="removeToCreateScrewAndThreadedInsertHole060"
  Angle = 360
  Axis = (0,1,0)
  Base = (0,0,0)
  FaceMakerClass = Part::FaceMakerBullseye
  Placement = pos=(89.5,0,3.5) rot=(0,0,1;0rad)
  Solid = false
  Source = -> Face142
  Symmetric = false
FEATURE [Part::Revolution] Revolve153  label="removeToCreateScrewAndThreadedInsertHole061"
  Angle = 360
  Axis = (0,1,0)
  Base = (0,0,0)
  FaceMakerClass = Part::FaceMakerBullseye
  Placement = pos=(109.5,4.7,3.5) rot=(0,0,1;0rad)
  Solid = false
  Source = -> Face145
  Symmetric = false
FEATURE [Part::Revolution] Revolve154  label="removeToCreateScrewAndThreadedInsertHole062"
  Angle = 360
  Axis = (0,1,0)
  Base = (0,0,0)
  FaceMakerClass = Part::FaceMakerBullseye
  Placement = pos=(109.5,4.7,68.5) rot=(0,0,1;0rad)
  Solid = false
  Source = -> Face144
  Symmetric = false
FEATURE [Part::MultiFuse] Fusion115  label="removeToCreateScrewAndThreadedInsertHole056"
  Shapes = -> [Revolve154,Revolve153,Revolve152,Revolve151,Revolve150,Revolve149]
FEATURE [Part::Feature] Face147
  shape: bbox 9.8 x 26.5 x 2e-07 mm, 1 faces, 0 solids (baked)
FEATURE [Part::Revolution] Revolve155
  Angle = 360
  Axis = (0,1,0)
  Base = (0,0,0)
  FaceMakerClass = Part::FaceMakerBullseye
  Placement = pos=(0,0,0) rot=(0,0,1;1.5708rad)
  Solid = false
  Source = -> Face147
  Symmetric = false
FEATURE [Part::Feature] Face148
  shape: bbox 9.8 x 26.5 x 2e-07 mm, 1 faces, 0 solids (baked)
FEATURE [Part::Revolution] Revolve156
  Angle = 360
  Axis = (0,1,0)
  Base = (0,0,0)
  FaceMakerClass = Part::FaceMakerBullseye
  Placement = pos=(0,0,0) rot=(0,0,1;1.5708rad)
  Solid = false
  Source = -> Face148
  Symmetric = false
FEATURE [Part::MultiFuse] Fusion116
  Placement = pos=(-18,19,36) rot=(0,0,1;0rad)
  Shapes = -> [Revolve156,Revolve155]
FEATURE [Part::Box] Box029  label="Cube016"
  AttacherType = Attacher::AttachEngine3D
  Height = 28
  Length = 3
  Placement = pos=(110.7,19,22) rot=(0,0,1;0rad)
  Width = 15.7
FEATURE [Part::Cylinder] Cylinder046
  Angle = 360
  AttacherType = Attacher::AttachEngine3D
  Height = 10
  Placement = pos=(0,0,36.15) rot=(0,0,1;0rad)
  Radius = 4
FEATURE [Part::Cylinder] Cylinder047
  Angle = 360
  AttacherType = Attacher::AttachEngine3D
  Height = 20
  Placement = pos=(0,0,36.15) rot=(0,0,1;0rad)
  Radius = 10.3
FEATURE [Part::MultiFuse] Fusion117  label="removeToCreteHoleForPlugHousing041"
  Placement = pos=(70,19,36) rot=(0,1,0;1.5708rad)
  Shapes = -> [Cylinder047,Cylinder046]
FEATURE [Part::Cut] Cut049  label="plugHousingTab004"
  Base = -> Box029
  Placement = pos=(-107.4,-14,0) rot=(0,0,1;0rad)
  Tool = -> Fusion117
FEATURE [Part::Box] Box030  label="Cube017"
  AttacherType = Attacher::AttachEngine3D
  Height = 28
  Length = 3
  Placement = pos=(110.7,19,22) rot=(0,0,1;0rad)
  Width = 15.7
FEATURE [Part::Cylinder] Cylinder048
  Angle = 360
  AttacherType = Attacher::AttachEngine3D
  Height = 10
  Placement = pos=(0,0,36.15) rot=(0,0,1;0rad)
  Radius = 4
FEATURE [Part::Cylinder] Cylinder049
  Angle = 360
  AttacherType = Attacher::AttachEngine3D
  Height = 20
  Placement = pos=(0,0,36.15) rot=(0,0,1;0rad)
  Radius = 10.3
FEATURE [Part::MultiFuse] Fusion118  label="removeToCreteHoleForPlugHousing042"
  Placement = pos=(70,19,36) rot=(0,1,0;1.5708rad)
  Shapes = -> [Cylinder049,Cylinder048]
FEATURE [Part::Cut] Cut050  label="plugHousingTab005"
  Base = -> Box030
  Placement = pos=(-107.4,-14,0) rot=(0,0,1;0rad)
  Tool = -> Fusion118
FEATURE [Part::MultiFuse] Fusion119
  Placement = pos=(9.6,23,0) rot=(0,0,1;3.14159rad)
  Shapes = -> [Cut049,Cut050]
FEATURE [Part::Box] Box031  label="Cube018"
  AttacherType = Attacher::AttachEngine3D
  Height = 10
  Length = 3
  Placement = pos=(3.3,4,12) rot=(0,0,1;0rad)
  Width = 10
FEATURE [Part::Fillet] Fillet044
  Base = -> Box031
  Edges = 1 edges r=2: [Edge11]
FEATURE [Part::Box] Box032  label="Cube019"
  AttacherType = Attacher::AttachEngine3D
  Height = 10
  Length = 3
  Placement = pos=(3.3,4,50) rot=(0,0,1;0rad)
  Width = 10
FEATURE [Part::Fillet] Fillet045
  Base = -> Box032
  Edges = 1 edges r=2: [Edge12]
FEATURE [Part::Box] Box033  label="Cube020"
  AttacherType = Attacher::AttachEngine3D
  Height = 28
  Length = 4
  Placement = pos=(5,0,22) rot=(0,0,1;0rad)
  Width = 10
FEATURE [Part::Fillet] Fillet046
  Base = -> Box033
  Edges = 1 edges r=1: [Edge7]
FEATURE [Part::Fillet] Fillet047
  Base = -> Fillet046
  Edges = 1 edges r=2: [Edge5]
FEATURE [Part::Fillet] Fillet048
  Base = -> Fillet047
  Edges = 1 edges r=2: [Edge2]
FEATURE [Part::Cylinder] Cylinder050
  Angle = 360
  AttacherType = Attacher::AttachEngine3D
  Height = 20
  Placement = pos=(0,0,36.15) rot=(0,0,1;0rad)
  Radius = 8.2
FEATURE [Part::Cylinder] Cylinder051
  Angle = 360
  AttacherType = Attacher::AttachEngine3D
  Height = 10
  Placement = pos=(0,0,36.15) rot=(0,0,1;0rad)
  Radius = 4
FEATURE [Part::MultiFuse] Fusion120  label="removeToCreteHoleForPlugHousing043"
  Placement = pos=(-42,19,36) rot=(0,1,0;1.5708rad)
  Shapes = -> [Cylinder050,Cylinder051]
FEATURE [Sketcher::SketchObject] Sketch067  label="topSketch018"
  FullyConstrained = true
  sketch-geometry (4):
    g0: LineSegment StartX=16.8446 StartY=31.512 StartZ=0 EndX=16.3251 EndY=34.4666 EndZ=0
    g1: ArcOfCircle CenterX=19 CenterY=19.2524 CenterZ=0 NormalX=0 NormalY=0 NormalZ=1 AngleXU=0 Radius=15.4476 StartAngle=1.74483 EndAngle=2.72717
    g2: ArcOfCircle CenterX=19 CenterY=19.2524 CenterZ=0 NormalX=0 NormalY=0 NormalZ=1 AngleXU=0 Radius=12.4476 StartAngle=1.74483 EndAngle=2.73189
    g3: LineSegment StartX=4.86004 StartY=25.4725 StartZ=0 EndX=7.58253 EndY=24.2107 EndZ=0
  constraints (7):
    c: Block(g0)
    c: Coincident(g1,g0)
    c: Coincident(g2,g0)
    c: Coincident(g3,g1)
    c: Coincident(g3,g2)
    c: Block(g1)
    c: Block(g2)
FEATURE [Part::Extrusion] Extrude058
  Base = -> Sketch067
  Dir = (0,0,1)
  DirMode = 2
  FaceMakerClass = Part::FaceMakerBullseye
  LengthFwd = 10
  LengthRev = 0
  Placement = pos=(0,0,31) rot=(0,0,1;0rad)
  Solid = true
  Symmetric = false
FEATURE [Part::Cut] Cut051
  Base = -> Extrude058
  Tool = -> Fusion120
FEATURE [Part::Fillet] Fillet049
  Base = -> Cut051
  Edges = 1 edges r=2: [Edge1]
FEATURE [Part::Fillet] Fillet050
  Base = -> Fillet049
  Edges = 1 edges r=2.5: [Edge1]
FEATURE [Part::Fillet] Fillet051
  Base = -> Fillet050
  Edges = 1 edges r=2.5: [Edge2]
FEATURE [Part::MultiFuse] Fusion121  label="wireHolder003"
  Shapes = -> [Fusion116,Fillet051]
FEATURE [Part::MultiFuse] Fusion122
  Shapes = -> [Fillet045,Fusion121]
FEATURE [Part::MultiFuse] Fusion123  label="wireHolder004"
  Shapes = -> [Fusion122,Fillet048]
FEATURE [Part::MultiFuse] Fusion124  label="wireHolder005"
  Shapes = -> [Fillet044,Fusion119,Fusion123]
FEATURE [Sketcher::SketchObject] Sketch068  label="topSketch019"
  FullyConstrained = true
  sketch-geometry (6):
    g0: LineSegment StartX=19 StartY=38 StartZ=0 EndX=117 EndY=38 EndZ=0
    g1: ArcOfCircle CenterX=19 CenterY=19 CenterZ=0 NormalX=0 NormalY=0 NormalZ=1 AngleXU=0 Radius=19 StartAngle=1.5708 EndAngle=3.14159
    g2: LineSegment StartX=117 StartY=38 StartZ=0 EndX=117 EndY=19 EndZ=0
    g3: LineSegment StartX=98 StartY=1.0161e-12 StartZ=0 EndX=5.22862e-06 EndY=1.0161e-12 EndZ=0
    g4: LineSegment StartX=5.22862e-06 StartY=19 StartZ=0 EndX=5.22862e-06 EndY=1.0161e-12 EndZ=0
    g5: ArcOfCircle CenterX=98 CenterY=19 CenterZ=0 NormalX=0 NormalY=0 NormalZ=1 AngleXU=0 Radius=19 StartAngle=4.71239 EndAngle=6.28319
  constraints (16):
    c: Horizontal(g0)
    c: Distance(g0) = 98
    c: Coincident(g1,g0)
    c: Block(g1)
    c: Coincident(g2,g0)
    c: Vertical(g2)
    c: Distance(g2) = 19
    c: Horizontal(g3)
    c: Coincident(g4,g1)
    c: Vertical(g4)
    c: Coincident(g3,g4)
    c: Block(g3)
    c: Coincident(g5,g2)
    c: Coincident(g5,g3)
    c: Block(g0)
    c: Block(g5)
FEATURE [Part::Extrusion] Extrude059  label="sideA002"
  Base = -> Sketch068
  Dir = (0,0,1)
  DirMode = 2
  FaceMakerClass = Part::FaceMakerBullseye
  LengthFwd = 3
  LengthRev = 0
  Placement = pos=(0,0,-2.7) rot=(0,0,1;0rad)
  Solid = true
  Symmetric = false
FEATURE [Sketcher::SketchObject] Sketch069  label="topSketch020"
  FullyConstrained = true
  sketch-geometry (6):
    g0: LineSegment StartX=19 StartY=38 StartZ=0 EndX=117 EndY=38 EndZ=0
    g1: ArcOfCircle CenterX=19 CenterY=19 CenterZ=0 NormalX=0 NormalY=0 NormalZ=1 AngleXU=0 Radius=19 StartAngle=1.5708 EndAngle=3.14159
    g2: LineSegment StartX=117 StartY=38 StartZ=0 EndX=117 EndY=19 EndZ=0
    g3: LineSegment StartX=98 StartY=1.0161e-12 StartZ=0 EndX=5.22862e-06 EndY=1.0161e-12 EndZ=0
    g4: LineSegment StartX=5.22862e-06 StartY=19 StartZ=0 EndX=5.22862e-06 EndY=1.0161e-12 EndZ=0
    g5: ArcOfCircle CenterX=98 CenterY=19 CenterZ=0 NormalX=0 NormalY=0 NormalZ=1 AngleXU=0 Radius=19 StartAngle=4.71239 EndAngle=6.28319
  constraints (16):
    c: Horizontal(g0)
    c: Distance(g0) = 98
    c: Coincident(g1,g0)
    c: Block(g1)
    c: Coincident(g2,g0)
    c: Vertical(g2)
    c: Distance(g2) = 19
    c: Horizontal(g3)
    c: Coincident(g4,g1)
    c: Vertical(g4)
    c: Coincident(g3,g4)
    c: Block(g3)
    c: Coincident(g5,g2)
    c: Coincident(g5,g3)
    c: Block(g0)
    c: Block(g5)
FEATURE [Part::Extrusion] Extrude060  label="sideB002"
  Base = -> Sketch069
  Dir = (0,0,1)
  DirMode = 2
  FaceMakerClass = Part::FaceMakerBullseye
  LengthFwd = 3
  LengthRev = 0
  Placement = pos=(0,0,71.7) rot=(0,0,1;0rad)
  Solid = true
  Symmetric = false
FEATURE [Part::MultiFuse] Fusion127  label="removeFromBottom001"
  Placement = pos=(2,0,0) rot=(0,0,1;0rad)
  Shapes = -> [Extrude059,Extrude060]
FEATURE [Part::Cylinder] Cylinder052
  Angle = 360
  AttacherType = Attacher::AttachEngine3D
  Height = 20
  Placement = pos=(0,0,36.15) rot=(0,0,1;0rad)
  Radius = 14
FEATURE [Part::Cylinder] Cylinder053
  Angle = 360
  AttacherType = Attacher::AttachEngine3D
  Height = 10
  Placement = pos=(0,0,36.15) rot=(0,0,1;0rad)
  Radius = 4
FEATURE [Part::MultiFuse] Fusion128  label="removeToCreteHoleForPlugHousing044"
  Placement = pos=(70,19,36) rot=(0,1,0;1.5708rad)
  Shapes = -> [Cylinder052,Cylinder053]
FEATURE [Part::Cut] Cut052  label="bottom011"
  Base = -> Extrude043
  Tool = -> Fusion128
FEATURE [Part::Cut] Cut054  label="bottom012"
  Base = -> Cut052
  Tool = -> Fusion115
FEATURE [Sketcher::SketchObject] Sketch070
  FullyConstrained = true
  Placement = pos=(117,19,0) rot=(0.57735,0.57735,0.57735;2.0944rad)
  sketch-geometry (48):
    g0: LineSegment StartX=-49.19 StartY=69.25 StartZ=0 EndX=-49.19 EndY=66.25 EndZ=0
    g1: LineSegment StartX=-49.19 StartY=63.5 StartZ=0 EndX=-49.19 EndY=60.5 EndZ=0
    g2: LineSegment StartX=-49.19 StartY=57.75 StartZ=0 EndX=-49.19 EndY=54.75 EndZ=0
    g3: LineSegment StartX=-49.19 StartY=52 StartZ=0 EndX=-49.19 EndY=49 EndZ=0
    g4: LineSegment StartX=-49.19 StartY=46.25 StartZ=0 EndX=-49.19 EndY=43.25 EndZ=0
    g5: LineSegment StartX=-49.19 StartY=40.5 StartZ=0 EndX=-49.19 EndY=37.5 EndZ=0
    g6: LineSegment StartX=-49.19 StartY=34.5 StartZ=0 EndX=-49.19 EndY=31.5 EndZ=0
    g7: LineSegment StartX=-49.19 StartY=28.75 StartZ=0 EndX=-49.19 EndY=25.75 EndZ=0
    g8: LineSegment StartX=-49.19 StartY=23 StartZ=0 EndX=-49.19 EndY=20 EndZ=0
    g9: LineSegment StartX=-49.19 StartY=17.25 StartZ=0 EndX=-49.19 EndY=14.25 EndZ=0
    g10: LineSegment StartX=-49.19 StartY=11.5 StartZ=0 EndX=-49.19 EndY=8.5 EndZ=0
    g11: LineSegment StartX=-49.19 StartY=5.75 StartZ=0 EndX=-49.19 EndY=2.75 EndZ=0
    g12: ArcOfCircle CenterX=-1.5 CenterY=67.75 CenterZ=0 NormalX=0 NormalY=0 NormalZ=1 AngleXU=0 Radius=1.5 StartAngle=4.71239 EndAngle=7.85398
    g13: ArcOfCircle CenterX=-1.5 CenterY=62 CenterZ=0 NormalX=0 NormalY=0 NormalZ=1 AngleXU=0 Radius=1.5 StartAngle=4.71239 EndAngle=7.85398
    g14: ArcOfCircle CenterX=-1.5 CenterY=56.25 CenterZ=0 NormalX=0 NormalY=0 NormalZ=1 AngleXU=0 Radius=1.5 StartAngle=4.71239 EndAngle=7.85398
    g15: ArcOfCircle CenterX=-11.49 CenterY=50.5 CenterZ=0 NormalX=0 NormalY=0 NormalZ=1 AngleXU=0 Radius=1.5 StartAngle=4.71239 EndAngle=7.85398
    g16: ArcOfCircle CenterX=-16.28 CenterY=44.75 CenterZ=0 NormalX=0 NormalY=0 NormalZ=1 AngleXU=0 Radius=1.5 StartAngle=4.71239 EndAngle=7.85398
    g17: ArcOfCircle CenterX=-18.2337 CenterY=39 CenterZ=0 NormalX=0 NormalY=0 NormalZ=1 AngleXU=0 Radius=1.5 StartAngle=4.71485 EndAngle=7.85398
    g18: ArcOfCircle CenterX=-16.2837 CenterY=27.25 CenterZ=0 NormalX=0 NormalY=0 NormalZ=1 AngleXU=0 Radius=1.5 StartAngle=4.71485 EndAngle=7.85398
    g19: ArcOfCircle CenterX=-18.2337 CenterY=33 CenterZ=0 NormalX=0 NormalY=0 NormalZ=1 AngleXU=0 Radius=1.5 StartAngle=4.71485 EndAngle=7.85398
    g20: ArcOfCircle CenterX=-11.49 CenterY=21.5 CenterZ=0 NormalX=0 NormalY=0 NormalZ=1 AngleXU=0 Radius=1.5 StartAngle=4.71239 EndAngle=7.85398
    g21: ArcOfCircle CenterX=-1.5 CenterY=4.25 CenterZ=0 NormalX=0 NormalY=0 NormalZ=1 AngleXU=0 Radius=1.5 StartAngle=4.71239 EndAngle=7.85398
    g22: ArcOfCircle CenterX=-1.5 CenterY=10 CenterZ=0 NormalX=0 NormalY=0 NormalZ=1 AngleXU=0 Radius=1.5 StartAngle=4.71239 EndAngle=7.85398
    g23: ArcOfCircle CenterX=-1.5 CenterY=15.75 CenterZ=0 NormalX=0 NormalY=0 NormalZ=1 AngleXU=0 Radius=1.5 StartAngle=4.71239 EndAngle=7.85398
    g24: LineSegment StartX=-49.19 StartY=69.25 StartZ=0 EndX=-1.5 EndY=69.25 EndZ=0
    g25: LineSegment StartX=-49.19 StartY=66.25 StartZ=0 EndX=-1.5 EndY=66.25 EndZ=0
    g26: LineSegment StartX=-49.19 StartY=63.5 StartZ=0 EndX=-1.5 EndY=63.5 EndZ=0
    g27: LineSegment StartX=-49.19 StartY=60.5 StartZ=0 EndX=-1.5 EndY=60.5 EndZ=0
    g28: LineSegment StartX=-49.19 StartY=57.75 StartZ=0 EndX=-1.5 EndY=57.75 EndZ=0
    g29: LineSegment StartX=-49.19 StartY=54.75 StartZ=0 EndX=-1.5 EndY=54.75 EndZ=0
    g30: LineSegment StartX=-49.19 StartY=52 StartZ=0 EndX=-11.49 EndY=52 EndZ=0
    g31: LineSegment StartX=-49.19 StartY=49 StartZ=0 EndX=-11.49 EndY=49 EndZ=0
    g32: LineSegment StartX=-49.19 StartY=46.25 StartZ=0 EndX=-16.28 EndY=46.25 EndZ=0
    g33: LineSegment StartX=-49.19 StartY=43.25 StartZ=0 EndX=-16.28 EndY=43.25 EndZ=0
    g34: LineSegment StartX=-49.19 StartY=40.5 StartZ=0 EndX=-18.2337 EndY=40.5 EndZ=0
    g35: LineSegment StartX=-49.19 StartY=37.5 StartZ=0 EndX=-18.23 EndY=37.5 EndZ=0
    g36: LineSegment StartX=-49.19 StartY=34.5 StartZ=0 EndX=-18.2337 EndY=34.5 EndZ=0
    g37: LineSegment StartX=-49.19 StartY=31.5 StartZ=0 EndX=-18.23 EndY=31.5 EndZ=0
    g38: LineSegment StartX=-49.19 StartY=28.75 StartZ=0 EndX=-16.2837 EndY=28.75 EndZ=0
    g39: LineSegment StartX=-49.19 StartY=25.75 StartZ=0 EndX=-16.28 EndY=25.75 EndZ=0
    g40: LineSegment StartX=-49.19 StartY=23 StartZ=0 EndX=-11.49 EndY=23 EndZ=0
    g41: LineSegment StartX=-49.19 StartY=20 StartZ=0 EndX=-11.49 EndY=20 EndZ=0
    g42: LineSegment StartX=-49.19 StartY=17.25 StartZ=0 EndX=-1.5 EndY=17.25 EndZ=0
    g43: LineSegment StartX=-49.19 StartY=14.25 StartZ=0 EndX=-1.5 EndY=14.25 EndZ=0
    g44: LineSegment StartX=-49.19 StartY=11.5 StartZ=0 EndX=-1.5 EndY=11.5 EndZ=0
    g45: LineSegment StartX=-49.19 StartY=8.5 StartZ=0 EndX=-1.5 EndY=8.5 EndZ=0
    g46: LineSegment StartX=-49.19 StartY=5.75 StartZ=0 EndX=-1.5 EndY=5.75 EndZ=0
    g47: LineSegment StartX=-49.19 StartY=2.75 StartZ=0 EndX=-1.5 EndY=2.75 EndZ=0
  constraints (120):
    c: Vertical(g0)
    c: Distance(g0) = 3
    c: Block(g0)
    c: Vertical(g1)
    c: Distance(g1) = 3
    c: Vertical(g2)
    c: Equal(g0,g2) = 3
    c: Block(g2)
    c: Vertical(g3)
    c: Equal(g1,g3) = 3
    c: Vertical(g4)
    c: Equal(g0,g4) = 3
    c: Block(g4)
    c: Vertical(g5)
    c: Equal(g1,g5) = 3
    c: Vertical(g6)
    c: Equal(g0,g6) = 3
    c: Block(g6)
    c: Vertical(g7)
    c: Equal(g1,g7) = 3
    c: Vertical(g8)
    c: Equal(g0,g8) = 3
    c: Block(g8)
    c: Vertical(g9)
    c: Equal(g1,g9) = 3
    c: Vertical(g10)
    c: Equal(g0,g10) = 3
    c: Block(g10)
    c: Vertical(g11)
    c: Equal(g1,g11) = 3
    c: Block(g12)
    c: Block(g13)
    c: Block(g14)
    c: Block(g15)
    c: Block(g16)
    c: Block(g17)
    c: Block(g18)
    c: Block(g19)
    c: Block(g20)
    c: Block(g21)
    c: Block(g22)
    c: Block(g23)
    c: Block(g11)
    c: Block(g9)
    c: Block(g7)
    c: Block(g5)
    c: Block(g3)
    c: Block(g1)
    c: Coincident(g24,g0)
    c: Coincident(g24,g12)
    c: Horizontal(g24)
    c: Coincident(g25,g0)
    c: Coincident(g25,g12)
    c: Horizontal(g25)
    c: Coincident(g26,g1)
    c: Coincident(g26,g13)
    c: Horizontal(g26)
    c: Coincident(g27,g1)
    c: Coincident(g27,g13)
    c: Horizontal(g27)
    c: Coincident(g28,g2)
    c: Coincident(g28,g14)
    c: Horizontal(g28)
    c: Coincident(g29,g2)
    c: Coincident(g29,g14)
    c: Horizontal(g29)
    c: Coincident(g30,g3)
    c: Coincident(g30,g15)
    c: Horizontal(g30)
    c: Coincident(g31,g3)
    c: Coincident(g31,g15)
    c: Horizontal(g31)
    c: Coincident(g32,g4)
    c: Coincident(g32,g16)
    c: Horizontal(g32)
    c: Coincident(g33,g4)
    c: Coincident(g33,g16)
    c: Horizontal(g33)
    c: Coincident(g34,g5)
    c: Coincident(g34,g17)
    c: Horizontal(g34)
    c: Coincident(g35,g5)
    c: Coincident(g35,g17)
    c: Horizontal(g35)
    c: Coincident(g36,g6)
    c: Coincident(g36,g19)
    c: Horizontal(g36)
    c: Coincident(g37,g6)
    c: Coincident(g37,g19)
    c: Horizontal(g37)
    c: Coincident(g38,g7)
    c: Coincident(g38,g18)
    c: Horizontal(g38)
    c: Coincident(g39,g7)
    c: Coincident(g39,g18)
    c: Horizontal(g39)
    c: Coincident(g40,g8)
    c: Coincident(g40,g20)
    c: Horizontal(g40)
    c: Coincident(g41,g8)
    c: Coincident(g41,g20)
    c: Horizontal(g41)
    c: Coincident(g42,g9)
    c: Coincident(g42,g23)
    c: Horizontal(g42)
    c: Coincident(g43,g9)
    c: Coincident(g43,g23)
    c: Horizontal(g43)
    c: Coincident(g44,g10)
    c: Coincident(g44,g22)
    c: Horizontal(g44)
    c: Coincident(g45,g10)
    c: Coincident(g45,g22)
    c: Horizontal(g45)
    c: Coincident(g46,g11)
    c: Coincident(g46,g21)
    c: Horizontal(g46)
    c: Coincident(g47,g11)
    c: Coincident(g47,g21)
    c: Horizontal(g47)
FEATURE [Part::Extrusion] Extrude061
  Base = -> Sketch070
  Dir = (1,0,0)
  DirMode = 2
  FaceMakerClass = Part::FaceMakerBullseye
  LengthFwd = 23
  LengthRev = 0
  Placement = pos=(-19,0,0) rot=(0,0,1;0rad)
  Solid = true
  Symmetric = false
FEATURE [Part::Fillet] Fillet052  label="removeToCreateVentalationHoles002"
  Base = -> Extrude061
  Edges = <same value as first occurrence — deduplicated (x6 in doc)>
  Placement = pos=(7,0.02,0) rot=(0,0,1;0rad)
FEATURE [Part::MultiFuse] Fusion130  label="bottom013"
  Shapes = -> [Cut054,Cut034]
FEATURE [Part::Cut] Cut055
  Base = -> Fusion130
  Tool = -> Fillet052
FEATURE [Part::Cylinder] Cylinder054
  Angle = 360
  AttacherType = Attacher::AttachEngine3D
  Height = 20
  Placement = pos=(0,0,36.15) rot=(0,0,1;0rad)
  Radius = 4
FEATURE [Sketcher::SketchObject] Sketch071  label="bottomSketch002"
  FullyConstrained = true
  sketch-geometry (32):
    g0: LineSegment StartX=3.3 StartY=-6.03275e-07 StartZ=0 EndX=98 EndY=-6.03275e-07 EndZ=0
    g1: ArcOfCircle CenterX=98 CenterY=19 CenterZ=0 NormalX=0 NormalY=0 NormalZ=1 AngleXU=0 Radius=19 StartAngle=4.71239 EndAngle=5.71103
    g2: LineSegment StartX=6.3 StartY=8 StartZ=0 EndX=3.3 EndY=8 EndZ=0
    g3: LineSegment StartX=3.3 StartY=8 StartZ=0 EndX=3.3 EndY=-6.03275e-07 EndZ=0
    g4: ArcOfCircle CenterX=8.3 CenterY=5 CenterZ=0 NormalX=0 NormalY=0 NormalZ=1 AngleXU=0 Radius=2 StartAngle=3.14159 EndAngle=4.71239
    g5: LineSegment StartX=6.3 StartY=8 StartZ=0 EndX=6.3 EndY=5 EndZ=0
    g6: ArcOfCircle CenterX=98 CenterY=19 CenterZ=0 NormalX=0 NormalY=0 NormalZ=1 AngleXU=0 Radius=12.7 StartAngle=4.71239 EndAngle=6.28319
    g7: LineSegment StartX=94.7 StartY=3 StartZ=0 EndX=8.3 EndY=3 EndZ=0
    g8-g12: Circle x5 (B-spline internal-alignment scaffolding for g13; pole/knot coordinates omitted)
    g13: BSplineCurve PolesCount=5 KnotsCount=3 Degree=3 IsPeriodic=0
    g14: GeomPoint X=98 Y=6.3 Z=0
    g15: GeomPoint X=96.3938 Y=4.71946 Z=0
    g16: GeomPoint X=94.7 Y=3 Z=0
    g17-g23: Circle x7 (B-spline internal-alignment scaffolding for g24; pole/knot coordinates omitted)
    g24: BSplineCurve PolesCount=7 KnotsCount=5 Degree=3 IsPeriodic=0
    g25-g29: GeomPoint x5 (B-spline internal-alignment scaffolding for g24; pole/knot coordinates omitted)
    g30: ArcOfCircle CenterX=98 CenterY=19 CenterZ=0 NormalX=0 NormalY=0 NormalZ=1 AngleXU=0 Radius=15.7 StartAngle=5.81226 EndAngle=6.28319
    g31: LineSegment StartX=110.7 StartY=19 StartZ=0 EndX=113.7 EndY=19 EndZ=0
  constraints (41):
    c: Horizontal(g0)
    c: Coincident(g1,g0)
    c: Block(g1)
    c: Horizontal(g2)
    c: Distance(g2) = 3
    c: Coincident(g3,g2)
    c: Vertical(g3)
    c: Coincident(g3,g0)
    c: Block(g4)
    c: Block(g2)
    c: Coincident(g5,g2)
    c: Coincident(g5,g4)
    c: Vertical(g5)
    c: Coincident(g6,g1)
    c: Block(g6)
    c: Coincident(g7,g4)
    c: Horizontal(g7)
    c: Block(g0)
    c: Block(g7)
    c: Block(g3)
    c: Coincident(g13,g6)
    c: Weight(g8) = 1
    c: Equal(g8, g9-g12) x4
    c: Coincident(g13,g7)
    c: InternalAlignment(g8-g12 -> g13) x5
    c: InternalAlignment(g14,g13)
    c: InternalAlignment(g15,g13)
    c: InternalAlignment(g16,g13)
    c: Block(g13)
    c: Weight(g17) = 1
    c: Equal(g17, g18-g23) x6
    c: Coincident(g24,g1)
    c: InternalAlignment(g17-g23 -> g24) x7
    c: InternalAlignment(g25-g29 -> g24) x5
    c: Block(g24)
    c: Coincident(g30,g24)
    c: Coincident(g31,g6)
    c: Coincident(g31,g30)
    c: Horizontal(g31)
    c: Block(g31)
    c: Block(g30)
FEATURE [Part::Extrusion] Extrude062  label="bottom014"
  Base = -> Sketch071
  Dir = (0,0,1)
  DirMode = 2
  FaceMakerClass = Part::FaceMakerBullseye
  LengthFwd = 71.4
  LengthRev = 0
  Placement = pos=(0,0,0.3) rot=(0,0,1;0rad)
  Solid = true
  Symmetric = false
FEATURE [Part::Fillet] Fillet054
  Base = -> Extrude062
  Edges = 1 edges r=2.4: [Edge17]
FEATURE [Part::Fillet] Fillet055  label="bottom015"
  Base = -> Fillet054
  Edges = 1 edges r=2.4: [Edge36]
FEATURE [Part::Cylinder] Cylinder055
  Angle = 360
  AttacherType = Attacher::AttachEngine3D
  Height = 10
  Placement = pos=(0,0,36.15) rot=(0,0,1;0rad)
  Radius = 4
FEATURE [Part::MultiFuse] Fusion131  label="removeToCreateHoleForPlugHousing002"
  Placement = pos=(70,19,36.15) rot=(0,1,0;1.5708rad)
  Shapes = -> [Cylinder054,Cylinder055]
FEATURE [Part::Cut] Cut056  label="Bottom001"
  Base = -> Fillet055
  Placement = pos=(9,0,0) rot=(0,0,1;0rad)
  Tool = -> Fusion131
FEATURE [Part::Cut] Cut057
  Base = -> Cut055
  Tool = -> Cut056
FEATURE [Sketcher::SketchObject] Sketch072  label="topSketch021"
  FullyConstrained = true
  sketch-geometry (4):
    g0: ArcOfCircle CenterX=105 CenterY=19 CenterZ=0 NormalX=0 NormalY=0 NormalZ=1 AngleXU=0 Radius=20.6155 StartAngle=5.54125 EndAngle=6.28319
    g1: ArcOfCircle CenterX=105 CenterY=19 CenterZ=0 NormalX=0 NormalY=0 NormalZ=1 AngleXU=0 Radius=13 StartAngle=5.54125 EndAngle=6.28319
    g2: LineSegment StartX=118 StartY=19 StartZ=0 EndX=125.616 EndY=19 EndZ=0
    g3: LineSegment StartX=114.583 StartY=10.2157 StartZ=0 EndX=120.197 EndY=5.06982 EndZ=0
  constraints (7):
    c: Block(g0)
    c: Block(g1)
    c: Coincident(g2,g1)
    c: Coincident(g2,g0)
    c: Horizontal(g2)
    c: Coincident(g3,g1)
    c: Coincident(g3,g0)
FEATURE [Part::Extrusion] Extrude063  label="bottomPlugHousingBit003"
  Base = -> Sketch072
  Dir = (0,0,1)
  DirMode = 2
  FaceMakerClass = Part::FaceMakerBullseye
  LengthFwd = 72
  LengthRev = 0
  Solid = true
  Symmetric = false
FEATURE [Part::Cylinder] Cylinder056
  Angle = 360
  AttacherType = Attacher::AttachEngine3D
  Height = 20
  Placement = pos=(0,0,36.15) rot=(0,0,1;0rad)
  Radius = 14.3
FEATURE [Part::Cylinder] Cylinder057
  Angle = 360
  AttacherType = Attacher::AttachEngine3D
  Height = 10
  Placement = pos=(0,0,36.15) rot=(0,0,1;0rad)
  Radius = 4
FEATURE [Part::Box] Box034  label="removeToCreteHoleForPlugHousing047"
  AttacherType = Attacher::AttachEngine3D
  Height = 28.6
  Length = 20
  Placement = pos=(106.15,0,21.7) rot=(0,0,1;0rad)
  Width = 19
FEATURE [Part::Cylinder] Cylinder058
  Angle = 360
  AttacherType = Attacher::AttachEngine3D
  Height = 20
  Placement = pos=(0,0,36.15) rot=(0,0,1;0rad)
  Radius = 14.3
FEATURE [Part::Cylinder] Cylinder059
  Angle = 360
  AttacherType = Attacher::AttachEngine3D
  Height = 10
  Placement = pos=(0,0,36.15) rot=(0,0,1;0rad)
  Radius = 4
FEATURE [Part::MultiFuse] Fusion134  label="removeToCreteHoleForPlugHousing046"
  Placement = pos=(70,19,36) rot=(0,1,0;1.5708rad)
  Shapes = -> [Cylinder058,Cylinder059]
FEATURE [Part::Cylinder] Cylinder060
  Angle = 360
  AttacherType = Attacher::AttachEngine3D
  Height = 20
  Placement = pos=(0,0,36.15) rot=(0,0,1;0rad)
  Radius = 14
FEATURE [Part::Cylinder] Cylinder061
  Angle = 360
  AttacherType = Attacher::AttachEngine3D
  Height = 10
  Placement = pos=(0,0,36.15) rot=(0,0,1;0rad)
  Radius = 4
FEATURE [Part::MultiFuse] Fusion135  label="removeToCreteHoleForPlugHousing048"
  Placement = pos=(70,19,36) rot=(0,1,0;1.5708rad)
  Shapes = -> [Cylinder060,Cylinder061]
FEATURE [Part::Box] Box035  label="removeToCreteHoleForPlugHousing049"
  AttacherType = Attacher::AttachEngine3D
  Height = 28.6
  Length = 20
  Placement = pos=(106.15,0,21.7) rot=(0,0,1;0rad)
  Width = 19
FEATURE [Part::MultiFuse] Fusion133  label="removeToCreteHoleForPlugHousing045"
  Placement = pos=(0,0,-28.3) rot=(0,0,1;0rad)
  Shapes = -> [Box035,Fusion134]
FEATURE [Part::MultiFuse] Fusion138  label="removeToCreteHoleForPlugHousing051"
  Placement = pos=(70,19,36) rot=(0,1,0;1.5708rad)
  Shapes = -> [Cylinder056,Cylinder057]
FEATURE [Part::MultiFuse] Fusion137  label="removeToCreteHoleForPlugHousing050"
  Placement = pos=(0,0,28.3) rot=(0,0,1;0rad)
  Shapes = -> [Box034,Fusion138]
FEATURE [Part::MultiFuse] Fusion132  label="removeToCreatePlugHousingBottomBit002"
  Shapes = -> [Fusion133,Fusion137]
FEATURE [Part::MultiFuse] Fusion136  label="removeToCreatePlugHousingBottomBit003"
  Shapes = -> [Fusion135,Fusion132]
FEATURE [Part::Cut] Cut058  label="bottomPlugHousingBit002"
  Base = -> Extrude063
  Placement = pos=(-0.09,0,0) rot=(0,0,1;0rad)
  Tool = -> Fusion136
FEATURE [Sketcher::SketchObject] Sketch073  label="bottomSketch003"
  FullyConstrained = true
  sketch-geometry (45):
    g0: LineSegment StartX=6.29999 StartY=8 StartZ=0 EndX=3.29999 EndY=8 EndZ=0
    g1: LineSegment StartX=3.29999 StartY=8 StartZ=0 EndX=3.29999 EndY=-6.03275e-07 EndZ=0
    g2: ArcOfCircle CenterX=8.29999 CenterY=5 CenterZ=0 NormalX=0 NormalY=0 NormalZ=1 AngleXU=0 Radius=2 StartAngle=3.14159 EndAngle=4.71239
    g3: LineSegment StartX=6.29999 StartY=8 StartZ=0 EndX=6.29999 EndY=5 EndZ=0
    g4: ArcOfCircle CenterX=105 CenterY=19 CenterZ=0 NormalX=0 NormalY=0 NormalZ=1 AngleXU=0 Radius=12.7 StartAngle=4.71239 EndAngle=5.94289
    g5-g11: Circle x7 (B-spline internal-alignment scaffolding for g12; pole/knot coordinates omitted)
    g12: BSplineCurve PolesCount=7 KnotsCount=5 Degree=3 IsPeriodic=0
    g13-g17: GeomPoint x5 (B-spline internal-alignment scaffolding for g12; pole/knot coordinates omitted)
    g18: ArcOfCircle CenterX=105 CenterY=19 CenterZ=0 NormalX=0 NormalY=0 NormalZ=1 AngleXU=0 Radius=15.7 StartAngle=5.81226 EndAngle=6.28319
    g19: BSplineCurve PolesCount=5 KnotsCount=3 Degree=3 IsPeriodic=0
    g20: LineSegment StartX=8.29999 StartY=3 StartZ=0 EndX=101.7 EndY=3 EndZ=0
    g21: LineSegment StartX=3.29999 StartY=-6.03275e-07 StartZ=0 EndX=105 EndY=-6.03275e-07 EndZ=0
    g22: LineSegment StartX=120.974 StartY=8.71251 StartZ=0 EndX=122.332 EndY=7.83778 EndZ=0
    g23: LineSegment StartX=105 StartY=-6.03274e-07 StartZ=0 EndX=113 EndY=-6.03274e-07 EndZ=0
    g24: ArcOfCircle CenterX=105 CenterY=19 CenterZ=0 NormalX=0 NormalY=0 NormalZ=1 AngleXU=0 Radius=20.6155 StartAngle=5.11091 EndAngle=5.71103
    g25: ArcOfCircle CenterX=117.7 CenterY=19 CenterZ=0 NormalX=0 NormalY=0 NormalZ=1 AngleXU=0 Radius=3 StartAngle=1.2e-15 EndAngle=2.10468
    g26: Circle CenterX=116.345 CenterY=16.3232 CenterZ=0 NormalX=0 NormalY=0 NormalZ=1 AngleXU=0 Radius=1
    g27: Circle CenterX=117.24 CenterY=15.7584 CenterZ=0 NormalX=0 NormalY=0 NormalZ=1 AngleXU=0 Radius=1
    g28: Circle CenterX=116.972 CenterY=14.7612 CenterZ=0 NormalX=0 NormalY=0 NormalZ=1 AngleXU=0 Radius=1
    g29: BSplineCurve PolesCount=3 KnotsCount=2 Degree=2 IsPeriodic=0
    g30: GeomPoint X=116.345 Y=16.3232 Z=0
    g31: GeomPoint X=116.972 Y=14.7612 Z=0
    g32: Circle CenterX=115.828 CenterY=17.157 CenterZ=0 NormalX=0 NormalY=0 NormalZ=1 AngleXU=0 Radius=1
    g33: Circle CenterX=115.841 CenterY=16.639 CenterZ=0 NormalX=0 NormalY=0 NormalZ=1 AngleXU=0 Radius=1
    g34: Circle CenterX=116.345 CenterY=16.3232 CenterZ=0 NormalX=0 NormalY=0 NormalZ=1 AngleXU=0 Radius=1
    g35: BSplineCurve PolesCount=3 KnotsCount=2 Degree=2 IsPeriodic=0
    g36: GeomPoint X=115.828 Y=17.157 Z=0
    g37: GeomPoint X=116.345 Y=16.3232 Z=0
    g38: LineSegment StartX=115.828 StartY=17.157 StartZ=0 EndX=115.828 EndY=20.8307 EndZ=0
    g39: Circle CenterX=115.828 CenterY=20.8307 CenterZ=0 NormalX=0 NormalY=0 NormalZ=1 AngleXU=0 Radius=1
    g40: Circle CenterX=115.831 CenterY=21.3396 CenterZ=0 NormalX=0 NormalY=0 NormalZ=1 AngleXU=0 Radius=1
    g41: Circle CenterX=116.173 CenterY=21.5825 CenterZ=0 NormalX=0 NormalY=0 NormalZ=1 AngleXU=0 Radius=1
    g42: BSplineCurve PolesCount=3 KnotsCount=2 Degree=2 IsPeriodic=0
    g43: GeomPoint X=115.828 Y=20.8307 Z=0
    g44: GeomPoint X=116.173 Y=21.5825 Z=0
  constraints (70):
    c: Horizontal(g0)
    c: Distance(g0) = 3
    c: Coincident(g1,g0)
    c: Vertical(g1)
    c: Block(g2)
    c: Block(g0)
    c: Coincident(g3,g0)
    c: Coincident(g3,g2)
    c: Vertical(g3)
    c: Block(g1)
    c: Block(g4)
    c: Coincident(g19,g4)
    c: Block(g19)
    c: Equal(g5, g6-g11) x6
    c: InternalAlignment(g5-g11 -> g12) x7
    c: InternalAlignment(g13-g17 -> g12) x5
    c: Block(g12)
    c: Coincident(g18,g12)
    c: Block(g18)
    c: Coincident(g20,g2)
    c: Coincident(g20,g19)
    c: Horizontal(g20)
    c: Distance(g20) = 93.4
    c: Coincident(g21,g1)
    c: Horizontal(g21)
    c: Distance(g21) = 101.7
    c: Horizontal(g23)
    c: Distance(g23) = 8
    c: Coincident(g24,g23)
    c: Block(g23)
    c: Coincident(g22,g24)
    c: Block(g24)
    c: Block(g22)
    c: Distance(g22) = 1.61553
    c: Coincident(g25,g18)
    c: Block(g25)
    c: Weight(g26) = 1
    c: Equal(g26,g27)
    c: Equal(g26,g28)
    c: Coincident(g29,g4)
    c: InternalAlignment(g26,g29)
    c: InternalAlignment(g27,g29)
    c: InternalAlignment(g28,g29)
    c: InternalAlignment(g30,g29)
    c: InternalAlignment(g31,g29)
    c: Block(g29)
    c: Weight(g32) = 1
    c: Equal(g32,g33)
    c: Equal(g32,g34)
    c: Coincident(g35,g29)
    c: InternalAlignment(g32,g35)
    c: InternalAlignment(g33,g35)
    c: InternalAlignment(g34,g35)
    c: InternalAlignment(g36,g35)
    c: InternalAlignment(g37,g35)
    c: Block(g35)
    c: Coincident(g38,g35)
    c: Vertical(g38)
    c: Block(g38)
    c: Coincident(g42,g38)
    c: Weight(g39) = 1
    c: Equal(g39,g40)
    c: Equal(g39,g41)
    c: Coincident(g42,g25)
    c: InternalAlignment(g39,g42)
    c: InternalAlignment(g40,g42)
    c: InternalAlignment(g41,g42)
    c: InternalAlignment(g43,g42)
    c: InternalAlignment(g44,g42)
    c: Block(g42)
FEATURE [Part::Extrusion] Extrude064  label="bottom016"
  Base = -> Sketch073
  Dir = (0,0,1)
  DirMode = 2
  FaceMakerClass = Part::FaceMakerBullseye
  LengthFwd = 71.4
  LengthRev = 0
  Placement = pos=(0,0,0.3) rot=(0,0,1;0rad)
  Solid = true
  Symmetric = false
FEATURE [Part::Revolution] Revolve157  label="removeToCreateScrewAndThreadedInsertHole063"
  Angle = 360
  Axis = (0,1,0)
  Base = (0,0,0)
  FaceMakerClass = Part::FaceMakerBullseye
  Placement = pos=(12.5,0,10) rot=(0,0,1;0rad)
  Solid = false
  Source = -> Face141
  Symmetric = false
FEATURE [Sketcher::SketchObject] Sketch074
  FullyConstrained = true
  Placement = pos=(117,19,0) rot=(0.57735,0.57735,0.57735;2.0944rad)
  sketch-geometry (48):
    g0: LineSegment StartX=-49.19 StartY=69.25 StartZ=0 EndX=-49.19 EndY=66.25 EndZ=0
    g1: LineSegment StartX=-49.19 StartY=63.5 StartZ=0 EndX=-49.19 EndY=60.5 EndZ=0
    g2: LineSegment StartX=-49.19 StartY=57.75 StartZ=0 EndX=-49.19 EndY=54.75 EndZ=0
    g3: LineSegment StartX=-49.19 StartY=52 StartZ=0 EndX=-49.19 EndY=49 EndZ=0
    g4: LineSegment StartX=-49.19 StartY=46.25 StartZ=0 EndX=-49.19 EndY=43.25 EndZ=0
    g5: LineSegment StartX=-49.19 StartY=40.5 StartZ=0 EndX=-49.19 EndY=37.5 EndZ=0
    g6: LineSegment StartX=-49.19 StartY=34.5 StartZ=0 EndX=-49.19 EndY=31.5 EndZ=0
    g7: LineSegment StartX=-49.19 StartY=28.75 StartZ=0 EndX=-49.19 EndY=25.75 EndZ=0
    g8: LineSegment StartX=-49.19 StartY=23 StartZ=0 EndX=-49.19 EndY=20 EndZ=0
    g9: LineSegment StartX=-49.19 StartY=17.25 StartZ=0 EndX=-49.19 EndY=14.25 EndZ=0
    g10: LineSegment StartX=-49.19 StartY=11.5 StartZ=0 EndX=-49.19 EndY=8.5 EndZ=0
    g11: LineSegment StartX=-49.19 StartY=5.75 StartZ=0 EndX=-49.19 EndY=2.75 EndZ=0
    g12: ArcOfCircle CenterX=-1.5 CenterY=67.75 CenterZ=0 NormalX=0 NormalY=0 NormalZ=1 AngleXU=0 Radius=1.5 StartAngle=4.71239 EndAngle=7.85398
    g13: ArcOfCircle CenterX=-1.5 CenterY=62 CenterZ=0 NormalX=0 NormalY=0 NormalZ=1 AngleXU=0 Radius=1.5 StartAngle=4.71239 EndAngle=7.85398
    g14: ArcOfCircle CenterX=-1.5 CenterY=56.25 CenterZ=0 NormalX=0 NormalY=0 NormalZ=1 AngleXU=0 Radius=1.5 StartAngle=4.71239 EndAngle=7.85398
    g15: ArcOfCircle CenterX=-11.49 CenterY=50.5 CenterZ=0 NormalX=0 NormalY=0 NormalZ=1 AngleXU=0 Radius=1.5 StartAngle=4.71239 EndAngle=7.85398
    g16: ArcOfCircle CenterX=-16.28 CenterY=44.75 CenterZ=0 NormalX=0 NormalY=0 NormalZ=1 AngleXU=0 Radius=1.5 StartAngle=4.71239 EndAngle=7.85398
    g17: ArcOfCircle CenterX=-18.2337 CenterY=39 CenterZ=0 NormalX=0 NormalY=0 NormalZ=1 AngleXU=0 Radius=1.5 StartAngle=4.71485 EndAngle=7.85398
    g18: ArcOfCircle CenterX=-16.2837 CenterY=27.25 CenterZ=0 NormalX=0 NormalY=0 NormalZ=1 AngleXU=0 Radius=1.5 StartAngle=4.71485 EndAngle=7.85398
    g19: ArcOfCircle CenterX=-18.2337 CenterY=33 CenterZ=0 NormalX=0 NormalY=0 NormalZ=1 AngleXU=0 Radius=1.5 StartAngle=4.71485 EndAngle=7.85398
    g20: ArcOfCircle CenterX=-11.49 CenterY=21.5 CenterZ=0 NormalX=0 NormalY=0 NormalZ=1 AngleXU=0 Radius=1.5 StartAngle=4.71239 EndAngle=7.85398
    g21: ArcOfCircle CenterX=-1.5 CenterY=4.25 CenterZ=0 NormalX=0 NormalY=0 NormalZ=1 AngleXU=0 Radius=1.5 StartAngle=4.71239 EndAngle=7.85398
    g22: ArcOfCircle CenterX=-1.5 CenterY=10 CenterZ=0 NormalX=0 NormalY=0 NormalZ=1 AngleXU=0 Radius=1.5 StartAngle=4.71239 EndAngle=7.85398
    g23: ArcOfCircle CenterX=-1.5 CenterY=15.75 CenterZ=0 NormalX=0 NormalY=0 NormalZ=1 AngleXU=0 Radius=1.5 StartAngle=4.71239 EndAngle=7.85398
    g24: LineSegment StartX=-49.19 StartY=69.25 StartZ=0 EndX=-1.5 EndY=69.25 EndZ=0
    g25: LineSegment StartX=-49.19 StartY=66.25 StartZ=0 EndX=-1.5 EndY=66.25 EndZ=0
    g26: LineSegment StartX=-49.19 StartY=63.5 StartZ=0 EndX=-1.5 EndY=63.5 EndZ=0
    g27: LineSegment StartX=-49.19 StartY=60.5 StartZ=0 EndX=-1.5 EndY=60.5 EndZ=0
    g28: LineSegment StartX=-49.19 StartY=57.75 StartZ=0 EndX=-1.5 EndY=57.75 EndZ=0
    g29: LineSegment StartX=-49.19 StartY=54.75 StartZ=0 EndX=-1.5 EndY=54.75 EndZ=0
    g30: LineSegment StartX=-49.19 StartY=52 StartZ=0 EndX=-11.49 EndY=52 EndZ=0
    g31: LineSegment StartX=-49.19 StartY=49 StartZ=0 EndX=-11.49 EndY=49 EndZ=0
    g32: LineSegment StartX=-49.19 StartY=46.25 StartZ=0 EndX=-16.28 EndY=46.25 EndZ=0
    g33: LineSegment StartX=-49.19 StartY=43.25 StartZ=0 EndX=-16.28 EndY=43.25 EndZ=0
    g34: LineSegment StartX=-49.19 StartY=40.5 StartZ=0 EndX=-18.2337 EndY=40.5 EndZ=0
    g35: LineSegment StartX=-49.19 StartY=37.5 StartZ=0 EndX=-18.23 EndY=37.5 EndZ=0
    g36: LineSegment StartX=-49.19 StartY=34.5 StartZ=0 EndX=-18.2337 EndY=34.5 EndZ=0
    g37: LineSegment StartX=-49.19 StartY=31.5 StartZ=0 EndX=-18.23 EndY=31.5 EndZ=0
    g38: LineSegment StartX=-49.19 StartY=28.75 StartZ=0 EndX=-16.2837 EndY=28.75 EndZ=0
    g39: LineSegment StartX=-49.19 StartY=25.75 StartZ=0 EndX=-16.28 EndY=25.75 EndZ=0
    g40: LineSegment StartX=-49.19 StartY=23 StartZ=0 EndX=-11.49 EndY=23 EndZ=0
    g41: LineSegment StartX=-49.19 StartY=20 StartZ=0 EndX=-11.49 EndY=20 EndZ=0
    g42: LineSegment StartX=-49.19 StartY=17.25 StartZ=0 EndX=-1.5 EndY=17.25 EndZ=0
    g43: LineSegment StartX=-49.19 StartY=14.25 StartZ=0 EndX=-1.5 EndY=14.25 EndZ=0
    g44: LineSegment StartX=-49.19 StartY=11.5 StartZ=0 EndX=-1.5 EndY=11.5 EndZ=0
    g45: LineSegment StartX=-49.19 StartY=8.5 StartZ=0 EndX=-1.5 EndY=8.5 EndZ=0
    g46: LineSegment StartX=-49.19 StartY=5.75 StartZ=0 EndX=-1.5 EndY=5.75 EndZ=0
    g47: LineSegment StartX=-49.19 StartY=2.75 StartZ=0 EndX=-1.5 EndY=2.75 EndZ=0
  constraints (120):
    c: Vertical(g0)
    c: Distance(g0) = 3
    c: Block(g0)
    c: Vertical(g1)
    c: Distance(g1) = 3
    c: Vertical(g2)
    c: Equal(g0,g2) = 3
    c: Block(g2)
    c: Vertical(g3)
    c: Equal(g1,g3) = 3
    c: Vertical(g4)
    c: Equal(g0,g4) = 3
    c: Block(g4)
    c: Vertical(g5)
    c: Equal(g1,g5) = 3
    c: Vertical(g6)
    c: Equal(g0,g6) = 3
    c: Block(g6)
    c: Vertical(g7)
    c: Equal(g1,g7) = 3
    c: Vertical(g8)
    c: Equal(g0,g8) = 3
    c: Block(g8)
    c: Vertical(g9)
    c: Equal(g1,g9) = 3
    c: Vertical(g10)
    c: Equal(g0,g10) = 3
    c: Block(g10)
    c: Vertical(g11)
    c: Equal(g1,g11) = 3
    c: Block(g12)
    c: Block(g13)
    c: Block(g14)
    c: Block(g15)
    c: Block(g16)
    c: Block(g17)
    c: Block(g18)
    c: Block(g19)
    c: Block(g20)
    c: Block(g21)
    c: Block(g22)
    c: Block(g23)
    c: Block(g11)
    c: Block(g9)
    c: Block(g7)
    c: Block(g5)
    c: Block(g3)
    c: Block(g1)
    c: Coincident(g24,g0)
    c: Coincident(g24,g12)
    c: Horizontal(g24)
    c: Coincident(g25,g0)
    c: Coincident(g25,g12)
    c: Horizontal(g25)
    c: Coincident(g26,g1)
    c: Coincident(g26,g13)
    c: Horizontal(g26)
    c: Coincident(g27,g1)
    c: Coincident(g27,g13)
    c: Horizontal(g27)
    c: Coincident(g28,g2)
    c: Coincident(g28,g14)
    c: Horizontal(g28)
    c: Coincident(g29,g2)
    c: Coincident(g29,g14)
    c: Horizontal(g29)
    c: Coincident(g30,g3)
    c: Coincident(g30,g15)
    c: Horizontal(g30)
    c: Coincident(g31,g3)
    c: Coincident(g31,g15)
    c: Horizontal(g31)
    c: Coincident(g32,g4)
    c: Coincident(g32,g16)
    c: Horizontal(g32)
    c: Coincident(g33,g4)
    c: Coincident(g33,g16)
    c: Horizontal(g33)
    c: Coincident(g34,g5)
    c: Coincident(g34,g17)
    c: Horizontal(g34)
    c: Coincident(g35,g5)
    c: Coincident(g35,g17)
    c: Horizontal(g35)
    c: Coincident(g36,g6)
    c: Coincident(g36,g19)
    c: Horizontal(g36)
    c: Coincident(g37,g6)
    c: Coincident(g37,g19)
    c: Horizontal(g37)
    c: Coincident(g38,g7)
    c: Coincident(g38,g18)
    c: Horizontal(g38)
    c: Coincident(g39,g7)
    c: Coincident(g39,g18)
    c: Horizontal(g39)
    c: Coincident(g40,g8)
    c: Coincident(g40,g20)
    c: Horizontal(g40)
    c: Coincident(g41,g8)
    c: Coincident(g41,g20)
    c: Horizontal(g41)
    c: Coincident(g42,g9)
    c: Coincident(g42,g23)
    c: Horizontal(g42)
    c: Coincident(g43,g9)
    c: Coincident(g43,g23)
    c: Horizontal(g43)
    c: Coincident(g44,g10)
    c: Coincident(g44,g22)
    c: Horizontal(g44)
    c: Coincident(g45,g10)
    c: Coincident(g45,g22)
    c: Horizontal(g45)
    c: Coincident(g46,g11)
    c: Coincident(g46,g21)
    c: Horizontal(g46)
    c: Coincident(g47,g11)
    c: Coincident(g47,g21)
    c: Horizontal(g47)
FEATURE [Part::Extrusion] Extrude065
  Base = -> Sketch074
  Dir = (1,0,0)
  DirMode = 2
  FaceMakerClass = Part::FaceMakerBullseye
  LengthFwd = 23
  LengthRev = 0
  Placement = pos=(-19,0,0) rot=(0,0,1;0rad)
  Solid = true
  Symmetric = false
FEATURE [Part::Fillet] Fillet056  label="removeToCreateVentalationHoles003"
  Base = -> Extrude065
  Edges = <same value as first occurrence — deduplicated (x6 in doc)>
  Placement = pos=(7,0.02,0) rot=(0,0,1;0rad)
FEATURE [Part::Revolution] Revolve158  label="removeToCreateScrewAndThreadedInsertHole065"
  Angle = 360
  Axis = (0,1,0)
  Base = (0,0,0)
  FaceMakerClass = Part::FaceMakerBullseye
  Placement = pos=(12.5,0,62) rot=(0,0,1;0rad)
  Solid = false
  Source = -> Face146
  Symmetric = false
FEATURE [Part::Revolution] Revolve159  label="removeToCreateScrewAndThreadedInsertHole066"
  Angle = 360
  Axis = (0,1,0)
  Base = (0,0,0)
  FaceMakerClass = Part::FaceMakerBullseye
  Placement = pos=(89.5,0,68.5) rot=(0,0,1;0rad)
  Solid = false
  Source = -> Face143
  Symmetric = false
FEATURE [Part::Revolution] Revolve160  label="removeToCreateScrewAndThreadedInsertHole067"
  Angle = 360
  Axis = (0,1,0)
  Base = (0,0,0)
  FaceMakerClass = Part::FaceMakerBullseye
  Placement = pos=(89.5,0,3.5) rot=(0,0,1;0rad)
  Solid = false
  Source = -> Face142
  Symmetric = false
FEATURE [Part::Revolution] Revolve161  label="removeToCreateScrewAndThreadedInsertHole068"
  Angle = 360
  Axis = (0,1,0)
  Base = (0,0,0)
  FaceMakerClass = Part::FaceMakerBullseye
  Placement = pos=(109.5,4.7,3.5) rot=(0,0,1;0rad)
  Solid = false
  Source = -> Face145
  Symmetric = false
FEATURE [Part::Revolution] Revolve162  label="removeToCreateScrewAndThreadedInsertHole069"
  Angle = 360
  Axis = (0,1,0)
  Base = (0,0,0)
  FaceMakerClass = Part::FaceMakerBullseye
  Placement = pos=(109.5,4.7,68.5) rot=(0,0,1;0rad)
  Solid = false
  Source = -> Face144
  Symmetric = false
FEATURE [Part::MultiFuse] Fusion141  label="removeToCreateScrewAndThreadedInsertHole064"
  Shapes = -> [Revolve162,Revolve161,Revolve160,Revolve159,Revolve158,Revolve157]
FEATURE [Part::Cylinder] Cylinder062
  Angle = 360
  AttacherType = Attacher::AttachEngine3D
  Height = 20
  Placement = pos=(0,0,36.15) rot=(0,0,1;0rad)
  Radius = 14
FEATURE [Part::Cylinder] Cylinder063
  Angle = 360
  AttacherType = Attacher::AttachEngine3D
  Height = 10
  Placement = pos=(0,0,36.15) rot=(0,0,1;0rad)
  Radius = 4
FEATURE [Part::MultiFuse] Fusion139  label="removeToCreteHoleForPlugHousing052"
  Placement = pos=(70,19,36) rot=(0,1,0;1.5708rad)
  Shapes = -> [Cylinder062,Cylinder063]
FEATURE [Part::Cut] Cut060  label="bottom017"
  Base = -> Extrude064
  Tool = -> Fusion139
FEATURE [Part::Cut] Cut061  label="bottom019"
  Base = -> Cut060
  Tool = -> Fusion141
FEATURE [Part::MultiFuse] Fusion140  label="bottom018"
  Shapes = -> [Cut061,Cut058]
FEATURE [Part::Cut] Cut059  label="bottom020"
  Base = -> Fusion140
  Tool = -> Fillet056
FEATURE [Part::Box] Box036  label="Cube021"
  AttacherType = Attacher::AttachEngine3D
  Height = 80
  Length = 26
  Placement = pos=(0,-1,-5) rot=(0,0,1;0rad)
  Width = 11
FEATURE [Part::Cut] Cut062  label="removeFromBottom002"
  Base = -> Cut057
  Tool = -> Box036
FEATURE [Part::Cut] Cut063
  Base = -> Cut059
  Tool = -> Cut062
FEATURE [Part::Cut] Cut064  label="pcbStands"
  Base = -> Fusion095
  Tool = -> Fusion127
FEATURE [Sketcher::SketchObject] Sketch075  label="topSketch022"
  FullyConstrained = true
  sketch-geometry (6):
    g0: LineSegment StartX=19 StartY=38 StartZ=0 EndX=117 EndY=38 EndZ=0
    g1: ArcOfCircle CenterX=19 CenterY=19 CenterZ=0 NormalX=0 NormalY=0 NormalZ=1 AngleXU=0 Radius=19 StartAngle=1.5708 EndAngle=3.14159
    g2: LineSegment StartX=117 StartY=38 StartZ=0 EndX=117 EndY=19 EndZ=0
    g3: LineSegment StartX=98 StartY=1.0161e-12 StartZ=0 EndX=5.22862e-06 EndY=1.0161e-12 EndZ=0
    g4: LineSegment StartX=5.22862e-06 StartY=19 StartZ=0 EndX=5.22862e-06 EndY=1.0161e-12 EndZ=0
    g5: ArcOfCircle CenterX=98 CenterY=19 CenterZ=0 NormalX=0 NormalY=0 NormalZ=1 AngleXU=0 Radius=19 StartAngle=4.71239 EndAngle=6.28319
  constraints (16):
    c: Horizontal(g0)
    c: Distance(g0) = 98
    c: Coincident(g1,g0)
    c: Block(g1)
    c: Coincident(g2,g0)
    c: Vertical(g2)
    c: Distance(g2) = 19
    c: Horizontal(g3)
    c: Coincident(g4,g1)
    c: Vertical(g4)
    c: Coincident(g3,g4)
    c: Block(g3)
    c: Coincident(g5,g2)
    c: Coincident(g5,g3)
    c: Block(g0)
    c: Block(g5)
FEATURE [Part::Extrusion] Extrude067  label="sideB003"
  Base = -> Sketch075
  Dir = (0,0,1)
  DirMode = 2
  FaceMakerClass = Part::FaceMakerBullseye
  LengthFwd = 3
  LengthRev = 0
  Placement = pos=(0,0,71.7) rot=(0,0,1;0rad)
  Solid = true
  Symmetric = false
FEATURE [Sketcher::SketchObject] Sketch076  label="topSketch023"
  FullyConstrained = true
  sketch-geometry (6):
    g0: LineSegment StartX=19 StartY=38 StartZ=0 EndX=117 EndY=38 EndZ=0
    g1: ArcOfCircle CenterX=19 CenterY=19 CenterZ=0 NormalX=0 NormalY=0 NormalZ=1 AngleXU=0 Radius=19 StartAngle=1.5708 EndAngle=3.14159
    g2: LineSegment StartX=117 StartY=38 StartZ=0 EndX=117 EndY=19 EndZ=0
    g3: LineSegment StartX=98 StartY=1.0161e-12 StartZ=0 EndX=5.22862e-06 EndY=1.0161e-12 EndZ=0
    g4: LineSegment StartX=5.22862e-06 StartY=19 StartZ=0 EndX=5.22862e-06 EndY=1.0161e-12 EndZ=0
    g5: ArcOfCircle CenterX=98 CenterY=19 CenterZ=0 NormalX=0 NormalY=0 NormalZ=1 AngleXU=0 Radius=19 StartAngle=4.71239 EndAngle=6.28319
  constraints (16):
    c: Horizontal(g0)
    c: Distance(g0) = 98
    c: Coincident(g1,g0)
    c: Block(g1)
    c: Coincident(g2,g0)
    c: Vertical(g2)
    c: Distance(g2) = 19
    c: Horizontal(g3)
    c: Coincident(g4,g1)
    c: Vertical(g4)
    c: Coincident(g3,g4)
    c: Block(g3)
    c: Coincident(g5,g2)
    c: Coincident(g5,g3)
    c: Block(g0)
    c: Block(g5)
FEATURE [Part::Extrusion] Extrude066  label="sideA003"
  Base = -> Sketch076
  Dir = (0,0,1)
  DirMode = 2
  FaceMakerClass = Part::FaceMakerBullseye
  LengthFwd = 3
  LengthRev = 0
  Placement = pos=(0,0,-2.7) rot=(0,0,1;0rad)
  Solid = true
  Symmetric = false
FEATURE [Part::MultiFuse] Fusion142  label="removeFromBottom003"
  Placement = pos=(2,0,0) rot=(0,0,1;0rad)
  Shapes = -> [Extrude066,Extrude067]
FEATURE [Part::Cut] Cut065  label="screwRetainers002"
  Base = -> Fusion096
  Tool = -> Fusion142
FEATURE [Sketcher::SketchObject] Sketch077
  FullyConstrained = true
  Placement = pos=(117,19,0) rot=(0.57735,0.57735,0.57735;2.0944rad)
  sketch-geometry (8):
    g0: LineSegment StartX=-49.19 StartY=63.5 StartZ=0 EndX=-49.19 EndY=60.5 EndZ=0
    g1: LineSegment StartX=-49.19 StartY=11.5 StartZ=0 EndX=-49.19 EndY=8.5 EndZ=0
    g2: ArcOfCircle CenterX=-1.5 CenterY=62 CenterZ=0 NormalX=0 NormalY=0 NormalZ=1 AngleXU=0 Radius=1.5 StartAngle=4.71239 EndAngle=7.85398
    g3: ArcOfCircle CenterX=-1.5 CenterY=10 CenterZ=0 NormalX=0 NormalY=0 NormalZ=1 AngleXU=0 Radius=1.5 StartAngle=4.71239 EndAngle=7.85398
    g4: LineSegment StartX=-49.19 StartY=63.5 StartZ=0 EndX=-1.5 EndY=63.5 EndZ=0
    g5: LineSegment StartX=-49.19 StartY=60.5 StartZ=0 EndX=-1.5 EndY=60.5 EndZ=0
    g6: LineSegment StartX=-49.19 StartY=11.5 StartZ=0 EndX=-1.5 EndY=11.5 EndZ=0
    g7: LineSegment StartX=-49.19 StartY=8.5 StartZ=0 EndX=-1.5 EndY=8.5 EndZ=0
  constraints (19):
    c: Vertical(g0)
    c: Distance(g0) = 3
    c: Vertical(g1)
    c: Block(g1)
    c: Block(g2)
    c: Block(g3)
    c: Block(g0)
    c: Coincident(g4,g0)
    c: Coincident(g4,g2)
    c: Horizontal(g4)
    c: Coincident(g5,g0)
    c: Coincident(g5,g2)
    c: Horizontal(g5)
    c: Coincident(g6,g1)
    c: Coincident(g6,g3)
    c: Horizontal(g6)
    c: Coincident(g7,g1)
    c: Coincident(g7,g3)
    c: Horizontal(g7)
FEATURE [Part::Extrusion] Extrude068
  Base = -> Sketch077
  Dir = (1,0,0)
  DirMode = 2
  FaceMakerClass = Part::FaceMakerBullseye
  LengthFwd = 10
  LengthRev = 0
  Solid = true
  Symmetric = false
FEATURE [Part::Fillet] Fillet057  label="removeFromtMoreFrontCaseScrewRetainers002"
  Base = -> Extrude068
  Edges = 4 edges r=1.49: [Edge6,Edge11,Edge18,Edge23]
  Placement = pos=(-12,0,0) rot=(0,0,1;0rad)
FEATURE [Sketcher::SketchObject] Sketch078
  FullyConstrained = true
  Placement = pos=(117,19,0) rot=(0.57735,0.57735,0.57735;2.0944rad)
  sketch-geometry (8):
    g0: LineSegment StartX=-49.19 StartY=69.25 StartZ=0 EndX=-49.19 EndY=66.25 EndZ=0
    g1: LineSegment StartX=-49.19 StartY=5.75 StartZ=0 EndX=-49.19 EndY=2.75 EndZ=0
    g2: ArcOfCircle CenterX=-1.5 CenterY=67.75 CenterZ=0 NormalX=0 NormalY=0 NormalZ=1 AngleXU=0 Radius=1.5 StartAngle=4.71239 EndAngle=7.85398
    g3: ArcOfCircle CenterX=-1.5 CenterY=4.25 CenterZ=0 NormalX=0 NormalY=0 NormalZ=1 AngleXU=0 Radius=1.5 StartAngle=4.71239 EndAngle=7.85398
    g4: LineSegment StartX=-49.19 StartY=69.25 StartZ=0 EndX=-1.5 EndY=69.25 EndZ=0
    g5: LineSegment StartX=-49.19 StartY=66.25 StartZ=0 EndX=-1.5 EndY=66.25 EndZ=0
    g6: LineSegment StartX=-49.19 StartY=5.75 StartZ=0 EndX=-1.5 EndY=5.75 EndZ=0
    g7: LineSegment StartX=-49.19 StartY=2.75 StartZ=0 EndX=-1.5 EndY=2.75 EndZ=0
  constraints (19):
    c: Vertical(g0)
    c: Distance(g0) = 3
    c: Block(g0)
    c: Vertical(g1)
    c: Block(g2)
    c: Block(g3)
    c: Block(g1)
    c: Coincident(g4,g0)
    c: Coincident(g4,g2)
    c: Horizontal(g4)
    c: Coincident(g5,g0)
    c: Coincident(g5,g2)
    c: Horizontal(g5)
    c: Coincident(g6,g1)
    c: Coincident(g6,g3)
    c: Horizontal(g6)
    c: Coincident(g7,g1)
    c: Coincident(g7,g3)
    c: Horizontal(g7)
FEATURE [Part::Extrusion] Extrude069
  Base = -> Sketch078
  Dir = (1,0,0)
  DirMode = 2
  FaceMakerClass = Part::FaceMakerBullseye
  LengthFwd = 10
  LengthRev = 0
  Solid = true
  Symmetric = false
FEATURE [Part::Fillet] Fillet058  label="removeFromtMoreFrontCaseScrewRetainers003"
  Base = -> Extrude069
  Edges = 4 edges r=1.49: [Edge6,Edge11,Edge18,Edge23]
  Placement = pos=(-4,0,0) rot=(0,0,1;0rad)
FEATURE [Part::Cut] Cut066
  Base = -> Cut065
  Tool = -> Fillet058
FEATURE [Part::Cut] Cut067  label="screwPillars"
  Base = -> Cut066
  Tool = -> Fillet057
FEATURE [Part::MultiFuse] Fusion143  label="bottom021"
  Shapes = -> [Cut031,Cut063]
FEATURE [Part::Cylinder] Cylinder
  Angle = 360
  AttacherType = Attacher::AttachEngine3D
  Height = 10
  Placement = pos=(20.65,12,4.68) rot=(1,0,0;1.5708rad)
  Radius = 2
FEATURE [Part::Cylinder] Cylinder064
  Angle = 360
  AttacherType = Attacher::AttachEngine3D
  Height = 10
  Placement = pos=(20.65,12,67.38) rot=(1,0,0;1.5708rad)
  Radius = 2
FEATURE [Part::Cylinder] Cylinder065
  Angle = 360
  AttacherType = Attacher::AttachEngine3D
  Height = 10
  Placement = pos=(77.15,12,67.38) rot=(1,0,0;1.5708rad)
  Radius = 2
FEATURE [Part::Cylinder] Cylinder066
  Angle = 360
  AttacherType = Attacher::AttachEngine3D
  Height = 10
  Placement = pos=(77.15,12,4.68) rot=(1,0,0;1.5708rad)
  Radius = 2
FEATURE [Part::MultiFuse] Fusion144  label="removeFromThreadedInsertHousing"
  Shapes = -> [Cylinder065,Cylinder064,Cylinder,Cylinder066]
FEATURE [Part::Cut] Cut068  label="pcbStands001"
  Base = -> Cut064
  Tool = -> Fusion144
FEATURE [Part::MultiFuse] Fusion145
  Shapes = -> [Cut068,Fusion143]
FEATURE [Part::MultiFuse] Fusion146
  Shapes = -> [Fusion145]
FEATURE [Part::MultiFuse] Fusion147  label="bottom022"
  Shapes = -> [Cut067,Fusion146]
FEATURE [Part::MultiFuse] Fusion148  label="casePillars005"
  Shapes = -> [Cut047,Fusion092]
FEATURE [Part::MultiFuse] Fusion149  label="bottom023"
  Shapes = -> [Fusion124,Fusion113,Fusion147]
FEATURE [Part::MultiFuse] Fusion150  label="topBits"
  Shapes = -> [Cut025,Fusion148,Cut030,Fillet034]
FEATURE [Part::Feature] Face149 .. Face152  x4 (patterned run collapsed; names and placements below)
  shape: bbox 3.2 x 1.5 x 2e-07 mm, 1 faces, 0 solids (baked)
FEATURE [Part::Feature] Face153
  shape: bbox 3.6 x 3.2 x 2e-07 mm, 1 faces, 0 solids (baked)
FEATURE [Part::Feature] Face154
  shape: bbox 3.6 x 3.2 x 2e-07 mm, 1 faces, 0 solids (baked)
FEATURE [Sketcher::SketchObject] Sketch079  label="topSketch024"
  FullyConstrained = true
  sketch-geometry (6):
    g0: LineSegment StartX=19 StartY=38 StartZ=0 EndX=117 EndY=38 EndZ=0
    g1: ArcOfCircle CenterX=19 CenterY=19 CenterZ=0 NormalX=0 NormalY=0 NormalZ=1 AngleXU=0 Radius=19 StartAngle=1.5708 EndAngle=3.14159
    g2: LineSegment StartX=117 StartY=38 StartZ=0 EndX=117 EndY=19 EndZ=0
    g3: LineSegment StartX=98 StartY=1.0161e-12 StartZ=0 EndX=5.22862e-06 EndY=1.0161e-12 EndZ=0
    g4: LineSegment StartX=5.22862e-06 StartY=19 StartZ=0 EndX=5.22862e-06 EndY=1.0161e-12 EndZ=0
    g5: ArcOfCircle CenterX=98 CenterY=19 CenterZ=0 NormalX=0 NormalY=0 NormalZ=1 AngleXU=0 Radius=19 StartAngle=4.71239 EndAngle=6.28319
  constraints (16):
    c: Horizontal(g0)
    c: Distance(g0) = 98
    c: Coincident(g1,g0)
    c: Block(g1)
    c: Coincident(g2,g0)
    c: Vertical(g2)
    c: Distance(g2) = 19
    c: Horizontal(g3)
    c: Coincident(g4,g1)
    c: Vertical(g4)
    c: Coincident(g3,g4)
    c: Block(g3)
    c: Coincident(g5,g2)
    c: Coincident(g5,g3)
    c: Block(g0)
    c: Block(g5)
FEATURE [Sketcher::SketchObject] Sketch080  label="topSketch025"
  FullyConstrained = true
  sketch-geometry (6):
    g0: LineSegment StartX=19 StartY=38 StartZ=0 EndX=117 EndY=38 EndZ=0
    g1: ArcOfCircle CenterX=19 CenterY=19 CenterZ=0 NormalX=0 NormalY=0 NormalZ=1 AngleXU=0 Radius=19 StartAngle=1.5708 EndAngle=3.14159
    g2: LineSegment StartX=117 StartY=38 StartZ=0 EndX=117 EndY=19 EndZ=0
    g3: LineSegment StartX=98 StartY=1.0161e-12 StartZ=0 EndX=5.22862e-06 EndY=1.0161e-12 EndZ=0
    g4: LineSegment StartX=5.22862e-06 StartY=19 StartZ=0 EndX=5.22862e-06 EndY=1.0161e-12 EndZ=0
    g5: ArcOfCircle CenterX=98 CenterY=19 CenterZ=0 NormalX=0 NormalY=0 NormalZ=1 AngleXU=0 Radius=19 StartAngle=4.71239 EndAngle=6.28319
  constraints (16):
    c: Horizontal(g0)
    c: Distance(g0) = 98
    c: Coincident(g1,g0)
    c: Block(g1)
    c: Coincident(g2,g0)
    c: Vertical(g2)
    c: Distance(g2) = 19
    c: Horizontal(g3)
    c: Coincident(g4,g1)
    c: Vertical(g4)
    c: Coincident(g3,g4)
    c: Block(g3)
    c: Coincident(g5,g2)
    c: Coincident(g5,g3)
    c: Block(g0)
    c: Block(g5)
FEATURE [Part::Extrusion] Extrude070  label="sideA004"
  Base = -> Sketch080
  Dir = (0,0,1)
  DirMode = 2
  FaceMakerClass = Part::FaceMakerBullseye
  LengthFwd = 3
  LengthRev = 0
  Placement = pos=(0,0,-2.7) rot=(0,0,1;0rad)
  Solid = true
  Symmetric = false
FEATURE [Sketcher::SketchObject] Sketch081
  FullyConstrained = true
  Placement = pos=(117,19,0) rot=(0.57735,0.57735,0.57735;2.0944rad)
  sketch-geometry (8):
    g0: LineSegment StartX=-49.19 StartY=63.5 StartZ=0 EndX=-49.19 EndY=60.5 EndZ=0
    g1: LineSegment StartX=-49.19 StartY=11.5 StartZ=0 EndX=-49.19 EndY=8.5 EndZ=0
    g2: ArcOfCircle CenterX=-1.5 CenterY=62 CenterZ=0 NormalX=0 NormalY=0 NormalZ=1 AngleXU=0 Radius=1.5 StartAngle=4.71239 EndAngle=7.85398
    g3: ArcOfCircle CenterX=-1.5 CenterY=10 CenterZ=0 NormalX=0 NormalY=0 NormalZ=1 AngleXU=0 Radius=1.5 StartAngle=4.71239 EndAngle=7.85398
    g4: LineSegment StartX=-49.19 StartY=63.5 StartZ=0 EndX=-1.5 EndY=63.5 EndZ=0
    g5: LineSegment StartX=-49.19 StartY=60.5 StartZ=0 EndX=-1.5 EndY=60.5 EndZ=0
    g6: LineSegment StartX=-49.19 StartY=11.5 StartZ=0 EndX=-1.5 EndY=11.5 EndZ=0
    g7: LineSegment StartX=-49.19 StartY=8.5 StartZ=0 EndX=-1.5 EndY=8.5 EndZ=0
  constraints (19):
    c: Vertical(g0)
    c: Distance(g0) = 3
    c: Vertical(g1)
    c: Block(g1)
    c: Block(g2)
    c: Block(g3)
    c: Block(g0)
    c: Coincident(g4,g0)
    c: Coincident(g4,g2)
    c: Horizontal(g4)
    c: Coincident(g5,g0)
    c: Coincident(g5,g2)
    c: Horizontal(g5)
    c: Coincident(g6,g1)
    c: Coincident(g6,g3)
    c: Horizontal(g6)
    c: Coincident(g7,g1)
    c: Coincident(g7,g3)
    c: Horizontal(g7)
FEATURE [Part::Extrusion] Extrude071  label="sideB004"
  Base = -> Sketch079
  Dir = (0,0,1)
  DirMode = 2
  FaceMakerClass = Part::FaceMakerBullseye
  LengthFwd = 3
  LengthRev = 0
  Placement = pos=(0,0,71.7) rot=(0,0,1;0rad)
  Solid = true
  Symmetric = false
FEATURE [Part::MultiFuse] Fusion152  label="removeFromBottom004"
  Placement = pos=(2,0,0) rot=(0,0,1;0rad)
  Shapes = -> [Extrude070,Extrude071]
FEATURE [Part::Extrusion] Extrude072
  Base = -> Sketch081
  Dir = (1,0,0)
  DirMode = 2
  FaceMakerClass = Part::FaceMakerBullseye
  LengthFwd = 10
  LengthRev = 0
  Solid = true
  Symmetric = false
FEATURE [Part::Fillet] Fillet059  label="removeFromtMoreFrontCaseScrewRetainers004"
  Base = -> Extrude072
  Edges = 4 edges r=1.49: [Edge6,Edge11,Edge18,Edge23]
  Placement = pos=(-12,0,0) rot=(0,0,1;0rad)
FEATURE [Sketcher::SketchObject] Sketch082
  FullyConstrained = true
  Placement = pos=(117,19,0) rot=(0.57735,0.57735,0.57735;2.0944rad)
  sketch-geometry (8):
    g0: LineSegment StartX=-49.19 StartY=69.25 StartZ=0 EndX=-49.19 EndY=66.25 EndZ=0
    g1: LineSegment StartX=-49.19 StartY=5.75 StartZ=0 EndX=-49.19 EndY=2.75 EndZ=0
    g2: ArcOfCircle CenterX=-1.5 CenterY=67.75 CenterZ=0 NormalX=0 NormalY=0 NormalZ=1 AngleXU=0 Radius=1.5 StartAngle=4.71239 EndAngle=7.85398
    g3: ArcOfCircle CenterX=-1.5 CenterY=4.25 CenterZ=0 NormalX=0 NormalY=0 NormalZ=1 AngleXU=0 Radius=1.5 StartAngle=4.71239 EndAngle=7.85398
    g4: LineSegment StartX=-49.19 StartY=69.25 StartZ=0 EndX=-1.5 EndY=69.25 EndZ=0
    g5: LineSegment StartX=-49.19 StartY=66.25 StartZ=0 EndX=-1.5 EndY=66.25 EndZ=0
    g6: LineSegment StartX=-49.19 StartY=5.75 StartZ=0 EndX=-1.5 EndY=5.75 EndZ=0
    g7: LineSegment StartX=-49.19 StartY=2.75 StartZ=0 EndX=-1.5 EndY=2.75 EndZ=0
  constraints (19):
    c: Vertical(g0)
    c: Distance(g0) = 3
    c: Block(g0)
    c: Vertical(g1)
    c: Block(g2)
    c: Block(g3)
    c: Block(g1)
    c: Coincident(g4,g0)
    c: Coincident(g4,g2)
    c: Horizontal(g4)
    c: Coincident(g5,g0)
    c: Coincident(g5,g2)
    c: Horizontal(g5)
    c: Coincident(g6,g1)
    c: Coincident(g6,g3)
    c: Horizontal(g6)
    c: Coincident(g7,g1)
    c: Coincident(g7,g3)
    c: Horizontal(g7)
FEATURE [Part::Extrusion] Extrude073
  Base = -> Sketch082
  Dir = (1,0,0)
  DirMode = 2
  FaceMakerClass = Part::FaceMakerBullseye
  LengthFwd = 10
  LengthRev = 0
  Solid = true
  Symmetric = false
FEATURE [Part::Fillet] Fillet060  label="removeFromtMoreFrontCaseScrewRetainers005"
  Base = -> Extrude073
  Edges = 4 edges r=1.49: [Edge6,Edge11,Edge18,Edge23]
  Placement = pos=(-4,0,0) rot=(0,0,1;0rad)
FEATURE [Part::Revolution] Revolve163  label="backCaseScrewRetainer004"
  Angle = 360
  Axis = (0,1,0)
  Base = (0,0,0)
  FaceMakerClass = Part::FaceMakerBullseye
  Placement = pos=(12.5,3,62) rot=(0,0,1;0rad)
  Solid = false
  Source = -> Face149
  Symmetric = false
FEATURE [Part::Revolution] Revolve164  label="frontCaseScrewRetainer006"
  Angle = 360
  Axis = (0,1,0)
  Base = (0,0,0)
  FaceMakerClass = Part::FaceMakerBullseye
  Placement = pos=(89.5,3,68.5) rot=(0,0,1;0rad)
  Solid = false
  Source = -> Face151
  Symmetric = false
FEATURE [Part::Revolution] Revolve165  label="frontCaseScrewRetainer007"
  Angle = 360
  Axis = (0,1,0)
  Base = (0,0,0)
  FaceMakerClass = Part::FaceMakerBullseye
  Placement = pos=(89.5,3,3.5) rot=(0,0,1;0rad)
  Solid = false
  Source = -> Face152
  Symmetric = false
FEATURE [Part::Revolution] Revolve166  label="backCaseScrewRetainer005"
  Angle = 360
  Axis = (0,1,0)
  Base = (0,0,0)
  FaceMakerClass = Part::FaceMakerBullseye
  Placement = pos=(12.5,3,10) rot=(0,0,1;0rad)
  Solid = false
  Source = -> Face150
  Symmetric = false
FEATURE [Part::Revolution] Revolve167  label="moreFrontCaseScrewRetainer006"
  Angle = 360
  Axis = (0,1,0)
  Base = (0,0,0)
  FaceMakerClass = Part::FaceMakerBullseye
  Placement = pos=(109.5,4.5,68.5) rot=(0,0,1;0rad)
  Solid = false
  Source = -> Face153
  Symmetric = false
FEATURE [Part::Revolution] Revolve168  label="moreFrontCaseScrewRetainer007"
  Angle = 360
  Axis = (0,1,0)
  Base = (0,0,0)
  FaceMakerClass = Part::FaceMakerBullseye
  Placement = pos=(109.5,4.5,3.5) rot=(0,0,1;0rad)
  Solid = false
  Source = -> Face154
  Symmetric = false
FEATURE [Part::MultiFuse] Fusion151  label="screwRetainers003"
  Shapes = -> [Revolve168,Revolve167,Revolve166,Revolve165,Revolve164,Revolve163]
FEATURE [Part::Cut] Cut069  label="screwRetainers004"
  Base = -> Fusion151
  Tool = -> Fusion152
FEATURE [Part::Cut] Cut070
  Base = -> Cut069
  Tool = -> Fillet060
FEATURE [Part::Cut] Cut071  label="screwPillars001"
  Base = -> Cut070
  Tool = -> Fillet059
FEATURE [Part::MultiFuse] Fusion153  label="bottom024"
  Shapes = -> [Fusion149,Cut071]
FEATURE [Part::Cylinder] Cylinder067
  Angle = 360
  AttacherType = Attacher::AttachEngine3D
  Height = 10
  Placement = pos=(20.65,12,4.68) rot=(1,0,0;1.5708rad)
  Radius = 2
FEATURE [Part::Cylinder] Cylinder068
  Angle = 360
  AttacherType = Attacher::AttachEngine3D
  Height = 10
  Placement = pos=(20.65,12,67.38) rot=(1,0,0;1.5708rad)
  Radius = 2
FEATURE [Part::Cylinder] Cylinder069
  Angle = 360
  AttacherType = Attacher::AttachEngine3D
  Height = 10
  Placement = pos=(77.15,12,67.38) rot=(1,0,0;1.5708rad)
  Radius = 2
FEATURE [Part::Cylinder] Cylinder070
  Angle = 360
  AttacherType = Attacher::AttachEngine3D
  Height = 10
  Placement = pos=(77.15,12,4.68) rot=(1,0,0;1.5708rad)
  Radius = 2
FEATURE [Part::MultiFuse] Fusion154  label="removeFromThreadedInsertHousing001"
  Shapes = -> [Cylinder069,Cylinder068,Cylinder067,Cylinder070]
FEATURE [Part::Cut] Cut072  label="bottom025"
  Base = -> Fusion153
  Tool = -> Fusion154
FEATURE [Image::ImagePlane] ImagePlane
  XSize = 339
  YSize = 72
FEATURE [Sketcher::SketchObject] Sketch083
  FullyConstrained = true
  MapMode = 5
  Support = -> [XY_Plane]
  sketch-geometry (338):
    g0: LineSegment StartX=-151.619 StartY=28.8932 StartZ=0 EndX=-140.819 EndY=28.8932 EndZ=0
    g1: LineSegment StartX=-151.619 StartY=24.0313 StartZ=0 EndX=-151.619 EndY=28.8932 EndZ=0
    g2: LineSegment StartX=-140.819 StartY=17.7713 StartZ=0 EndX=-151.619 EndY=17.7713 EndZ=0
    g3: LineSegment StartX=-151.619 StartY=17.7713 StartZ=0 EndX=-151.619 EndY=22.6313 EndZ=0
    g4: LineSegment StartX=-151.619 StartY=22.6313 StartZ=0 EndX=-145.128 EndY=22.6313 EndZ=0
    g5: LineSegment StartX=-145.128 StartY=24.0313 StartZ=0 EndX=-140.819 EndY=28.8932 EndZ=0
    g6: LineSegment StartX=-145.128 StartY=22.6313 StartZ=0 EndX=-140.819 EndY=17.7713 EndZ=0
    g7: ArcOfCircle CenterX=-155.157 CenterY=23.3323 CenterZ=0 NormalX=0 NormalY=0 NormalZ=1 AngleXU=0 Radius=6.92354 StartAngle=1.03434 EndAngle=5.24885
    g8: ArcOfCircle CenterX=-155.157 CenterY=23.3323 CenterZ=0 NormalX=0 NormalY=0 NormalZ=1 AngleXU=0 Radius=12.6269 StartAngle=1.28675 EndAngle=4.99643
    g9: LineSegment StartX=-151.619 StartY=35.4532 StartZ=0 EndX=-151.619 EndY=29.2832 EndZ=0
    g10: LineSegment StartX=-151.619 StartY=17.3813 StartZ=0 EndX=-151.619 EndY=11.2113 EndZ=0
    g11-g21: Circle x11 (B-spline internal-alignment scaffolding for g22; pole/knot coordinates omitted)
    g22: BSplineCurve PolesCount=11 KnotsCount=9 Degree=3 IsPeriodic=0
    g23-g31: GeomPoint x9 (B-spline internal-alignment scaffolding for g22; pole/knot coordinates omitted)
    g32-g49: Circle x18 (B-spline internal-alignment scaffolding for g50; pole/knot coordinates omitted)
    g50: BSplineCurve PolesCount=18 KnotsCount=16 Degree=3 IsPeriodic=0
    g51-g66: GeomPoint x16 (B-spline internal-alignment scaffolding for g50; pole/knot coordinates omitted)
    g67: LineSegment StartX=-117.124 StartY=30.093 StartZ=0 EndX=-117.603 EndY=26.5272 EndZ=0
    g68: LineSegment StartX=-117.603 StartY=17.8472 StartZ=0 EndX=-117.124 EndY=14.2659 EndZ=0
    g69: Ellipse CenterX=-109.671 CenterY=20.025 CenterZ=0 NormalX=0 NormalY=0 NormalZ=1 MajorRadius=3.34798 MinorRadius=2.71052 AngleXU=-1.56793
    g70: GeomPoint X=-109.666 Y=18.0598 Z=0
    g71: GeomPoint X=-109.677 Y=21.9902 Z=0
    g72: Ellipse CenterX=-109.671 CenterY=20.0123 CenterZ=0 NormalX=0 NormalY=0 NormalZ=1 MajorRadius=6.93002 MinorRadius=6.36273 AngleXU=-3.13976
    g73: GeomPoint X=-112.417 Y=20.0073 Z=0
    g74: GeomPoint X=-106.925 Y=20.0173 Z=0
    g75: Ellipse CenterX=-51.7682 CenterY=20.1463 CenterZ=0 NormalX=0 NormalY=0 NormalZ=1 MajorRadius=3.19279 MinorRadius=2.71052 AngleXU=-1.52774
    g76: GeomPoint X=-51.6955 Y=18.4606 Z=0
    g77: GeomPoint X=-51.8408 Y=21.832 Z=0
    g78: GeomPoint X=-54.5142 Y=20.1413 Z=0
    g79: GeomPoint X=-49.0221 Y=20.1513 Z=0
    g80: Ellipse CenterX=-51.7682 CenterY=20.1463 CenterZ=0 NormalX=0 NormalY=0 NormalZ=1 MajorRadius=6.93002 MinorRadius=6.36273 AngleXU=-3.13976
    g81: Ellipse CenterX=-22.8436 CenterY=20.1783 CenterZ=0 NormalX=0 NormalY=0 NormalZ=1 MajorRadius=3.31512 MinorRadius=2.71052 AngleXU=-1.60214
    g82: GeomPoint X=-22.9034 Y=18.2706 Z=0
    g83: GeomPoint X=-22.7838 Y=22.0861 Z=0
    g84: GeomPoint X=-25.5897 Y=20.1733 Z=0
    g85: GeomPoint X=-20.0976 Y=20.1833 Z=0
    g86: Ellipse CenterX=-22.8436 CenterY=20.1783 CenterZ=0 NormalX=0 NormalY=0 NormalZ=1 MajorRadius=6.93002 MinorRadius=6.36273 AngleXU=-3.13976
    g87: LineSegment StartX=-101.889 StartY=14.1107 StartZ=0 EndX=-97.7455 EndY=14.1107 EndZ=0
    g88: LineSegment StartX=-93.8155 StartY=14.1107 StartZ=0 EndX=-89.6755 EndY=14.1107 EndZ=0
    g89: LineSegment StartX=-85.7455 StartY=14.1107 StartZ=0 EndX=-81.6055 EndY=14.1107 EndZ=0
    g90: LineSegment StartX=-101.889 StartY=14.1107 StartZ=0 EndX=-101.889 EndY=25.9907 EndZ=0
    g91: LineSegment StartX=-101.889 StartY=25.9907 StartZ=0 EndX=-97.8594 EndY=25.9907 EndZ=0
    g92: LineSegment StartX=-97.8594 StartY=25.9907 StartZ=0 EndX=-97.8594 EndY=24.0907 EndZ=0
    g93: LineSegment StartX=-97.7455 StartY=14.1107 StartZ=0 EndX=-97.7455 EndY=19.9107 EndZ=0
    g94: LineSegment StartX=-89.6755 StartY=14.1107 StartZ=0 EndX=-89.6755 EndY=19.9107 EndZ=0
    g95: LineSegment StartX=-93.8155 StartY=14.1107 StartZ=0 EndX=-93.8155 EndY=21.0107 EndZ=0
    g96-g106: Circle x11 (B-spline internal-alignment scaffolding for g107; pole/knot coordinates omitted)
    g107: BSplineCurve PolesCount=11 KnotsCount=9 Degree=3 IsPeriodic=0
    g108-g116: GeomPoint x9 (B-spline internal-alignment scaffolding for g107; pole/knot coordinates omitted)
    g117: BSplineCurve PolesCount=11 KnotsCount=9 Degree=3 IsPeriodic=0
    g118-g125: Circle x8 (B-spline internal-alignment scaffolding for g126; pole/knot coordinates omitted)
    g126: BSplineCurve PolesCount=8 KnotsCount=6 Degree=3 IsPeriodic=0
    g127-g132: GeomPoint x6 (B-spline internal-alignment scaffolding for g126; pole/knot coordinates omitted)
    g133: BSplineCurve PolesCount=8 KnotsCount=6 Degree=3 IsPeriodic=0
    g134: LineSegment StartX=-85.7455 StartY=21.0107 StartZ=0 EndX=-85.7455 EndY=14.1107 EndZ=0
    g135: LineSegment StartX=-80.0879 StartY=14.1107 StartZ=0 EndX=-75.944 EndY=14.1107 EndZ=0
    g136: LineSegment StartX=-72.014 StartY=14.1107 StartZ=0 EndX=-67.874 EndY=14.1107 EndZ=0
    g137: LineSegment StartX=-63.944 StartY=14.1107 StartZ=0 EndX=-59.804 EndY=14.1107 EndZ=0
    g138: LineSegment StartX=-80.0879 StartY=14.1107 StartZ=0 EndX=-80.0879 EndY=25.9907 EndZ=0
    g139: LineSegment StartX=-80.0879 StartY=25.9907 StartZ=0 EndX=-76.0579 EndY=25.9907 EndZ=0
    g140: LineSegment StartX=-76.0579 StartY=25.9907 StartZ=0 EndX=-76.0579 EndY=24.0907 EndZ=0
    g141: LineSegment StartX=-75.944 StartY=14.1107 StartZ=0 EndX=-75.944 EndY=19.9107 EndZ=0
    g142: LineSegment StartX=-67.874 StartY=14.1107 StartZ=0 EndX=-67.874 EndY=19.9107 EndZ=0
    g143: LineSegment StartX=-72.014 StartY=14.1107 StartZ=0 EndX=-72.014 EndY=21.0107 EndZ=0
    g144-g148: Circle x5 (B-spline internal-alignment scaffolding for g149; pole/knot coordinates omitted)
    g149: BSplineCurve PolesCount=11 KnotsCount=9 Degree=3 IsPeriodic=0
    g150-g158: GeomPoint x9 (B-spline internal-alignment scaffolding for g149; pole/knot coordinates omitted)
    g159: BSplineCurve PolesCount=11 KnotsCount=9 Degree=3 IsPeriodic=0
    g160-g167: Circle x8 (B-spline internal-alignment scaffolding for g168; pole/knot coordinates omitted)
    g168: BSplineCurve PolesCount=8 KnotsCount=6 Degree=3 IsPeriodic=0
    g169-g174: GeomPoint x6 (B-spline internal-alignment scaffolding for g168; pole/knot coordinates omitted)
    g175: BSplineCurve PolesCount=8 KnotsCount=6 Degree=3 IsPeriodic=0
    g176: LineSegment StartX=-63.944 StartY=21.0107 StartZ=0 EndX=-63.944 EndY=14.1107 EndZ=0
    g177: LineSegment StartX=-59.804 StartY=14.1107 StartZ=0 EndX=-59.804 EndY=21.5868 EndZ=0
    g178: BSplineCurve PolesCount=4 KnotsCount=2 Degree=3 IsPeriodic=0
    g179: GeomPoint X=-59.804 Y=21.5868 Z=0
    g180: GeomPoint X=-60.2379 Y=24.0907 Z=0
    g181: LineSegment StartX=-81.6055 StartY=14.1107 StartZ=0 EndX=-81.6055 EndY=21.5868 EndZ=0
    g182: LineSegment StartX=-151.619 StartY=24.0313 StartZ=0 EndX=-145.128 EndY=24.0313 EndZ=0
    g183: Circle CenterX=-82.0394 CenterY=24.0907 CenterZ=0 NormalX=0 NormalY=0 NormalZ=1 AngleXU=0 Radius=1
    g184: Circle CenterX=-81.7131 CenterY=23.2736 CenterZ=0 NormalX=0 NormalY=0 NormalZ=1 AngleXU=0 Radius=1
    g185: Circle CenterX=-81.6055 CenterY=21.5868 CenterZ=0 NormalX=0 NormalY=0 NormalZ=1 AngleXU=0 Radius=1
    g186: BSplineCurve PolesCount=3 KnotsCount=2 Degree=2 IsPeriodic=0
    g187: GeomPoint X=-82.0394 Y=24.0907 Z=0
    g188: GeomPoint X=-81.6055 Y=21.5868 Z=0
    g189: Ellipse CenterX=-37.3522 CenterY=19.9515 CenterZ=0 NormalX=0 NormalY=0 NormalZ=1 MajorRadius=2.99755 MinorRadius=2.49 AngleXU=1.5708
    g190: GeomPoint X=-37.3522 Y=21.6203 Z=0
    g191: GeomPoint X=-37.3522 Y=18.2826 Z=0
    g192: ArcOfEllipse CenterX=-38.7647 CenterY=20.06 CenterZ=0 NormalX=0 NormalY=0 NormalZ=1 MajorRadius=6.30025 MinorRadius=5.3849 AngleXU=1.57276 StartAngle=5.50632 EndAngle=10.3035
    g193: GeomPoint X=-38.7711 Y=23.3304 Z=0
    g194: GeomPoint X=-38.7583 Y=16.7895 Z=0
    g195: LineSegment StartX=-34.6109 StartY=14.1107 StartZ=0 EndX=-30.8984 EndY=14.1107 EndZ=0
    g196: LineSegment StartX=-30.8984 StartY=14.1107 StartZ=0 EndX=-30.8984 EndY=31.1784 EndZ=0
    g197: LineSegment StartX=-30.8984 StartY=31.1784 StartZ=0 EndX=-34.9984 EndY=31.1784 EndZ=0
    g198: LineSegment StartX=-34.9984 StartY=24.5602 StartZ=0 EndX=-34.9984 EndY=31.1784 EndZ=0
    g199: LineSegment StartX=-34.6109 StartY=16.0476 StartZ=0 EndX=-34.6109 EndY=14.1107 EndZ=0
    g200: LineSegment StartX=-14.8781 StartY=14.1107 StartZ=0 EndX=-10.5106 EndY=14.1107 EndZ=0
    g201: LineSegment StartX=-14.8781 StartY=14.1107 StartZ=0 EndX=-14.8781 EndY=25.8504 EndZ=0
    g202: LineSegment StartX=-14.8781 StartY=25.8504 StartZ=0 EndX=-10.8534 EndY=25.8504 EndZ=0
    g203: LineSegment StartX=-10.8534 StartY=25.8504 StartZ=0 EndX=-10.8534 EndY=24.0923 EndZ=0
    g204: LineSegment StartX=-10.5106 StartY=14.1107 StartZ=0 EndX=-10.5106 EndY=19.7752 EndZ=0
    g205: LineSegment StartX=-5.96397 StartY=25.9304 StartZ=0 EndX=-5.96397 EndY=22.574 EndZ=0
    g206-g214: Circle x9 (B-spline internal-alignment scaffolding for g215; pole/knot coordinates omitted)
    g215: BSplineCurve PolesCount=9 KnotsCount=7 Degree=3 IsPeriodic=0
    g216-g222: GeomPoint x7 (B-spline internal-alignment scaffolding for g215; pole/knot coordinates omitted)
    g223-g232: Circle x10 (B-spline internal-alignment scaffolding for g233; pole/knot coordinates omitted)
    g233: BSplineCurve PolesCount=10 KnotsCount=8 Degree=3 IsPeriodic=0
    g234-g241: GeomPoint x8 (B-spline internal-alignment scaffolding for g233; pole/knot coordinates omitted)
    g242: LineSegment StartX=-1.58923 StartY=21.0696 StartZ=0 EndX=2.62034 EndY=21.0696 EndZ=0
    g243: LineSegment StartX=-1.55856 StartY=18.7342 StartZ=0 EndX=6.45946 EndY=18.7342 EndZ=0
    g244: LineSegment StartX=5.29231 StartY=17.386 StartZ=0 EndX=5.29231 EndY=14.3674 EndZ=0
    g245-g269: Circle x25 (B-spline internal-alignment scaffolding for g270; pole/knot coordinates omitted)
    g270: BSplineCurve PolesCount=25 KnotsCount=23 Degree=3 IsPeriodic=0
    g271-g293: GeomPoint x23 (B-spline internal-alignment scaffolding for g270; pole/knot coordinates omitted)
    g294-g304: Circle x11 (B-spline internal-alignment scaffolding for g305; pole/knot coordinates omitted)
    g305: BSplineCurve PolesCount=11 KnotsCount=9 Degree=3 IsPeriodic=0
    g306-g314: GeomPoint x9 (B-spline internal-alignment scaffolding for g305; pole/knot coordinates omitted)
    g315-g326: Circle x12 (B-spline internal-alignment scaffolding for g327; pole/knot coordinates omitted)
    g327: BSplineCurve PolesCount=12 KnotsCount=10 Degree=3 IsPeriodic=0
    g328-g337: GeomPoint x10 (B-spline internal-alignment scaffolding for g327; pole/knot coordinates omitted)
  constraints (252):
    c: Coincident(g1,g0)
    c: Horizontal(g0)
    c: Vertical(g1)
    c: Coincident(g2,g3)
    c: Coincident(g3,g4)
    c: Horizontal(g4)
    c: Horizontal(g2)
    c: Vertical(g3)
    c: Block(g1)
    c: Distance(g3) = 4.86
    c: Block(g4)
    c: Distance(g0) = 10.8
    c: Distance(g2) = 10.8
    c: Coincident(g5,g0)
    c: Coincident(g6,g4)
    c: Coincident(g6,g2)
    c: Block(g8)
    c: Block(g7)
    c: Coincident(g9,g8)
    c: Coincident(g9,g7)
    c: Vertical(g9)
    c: Coincident(g10,g7)
    c: Coincident(g10,g8)
    c: Vertical(g10)
    c: Weight(g11) = 1
    c: Equal(g11, g12-g21) x10
    c: InternalAlignment(g11-g21 -> g22) x11
    c: InternalAlignment(g23-g31 -> g22) x9
    c: Block(g22)
    c: Weight(g32) = 1
    c: Equal(g32, g33-g49) x17
    c: InternalAlignment(g32-g49 -> g50) x18
    c: InternalAlignment(g51-g66 -> g50) x16
    c: Block(g50)
    c: Coincident(g67,g50)
    c: Coincident(g67,g22)
    c: Coincident(g68,g22)
    c: Coincident(g68,g50)
    c: InternalAlignment(g70,g69)
    c: InternalAlignment(g71,g69)
    c: Block(g69)
    c: InternalAlignment(g73,g72)
    c: InternalAlignment(g74,g72)
    c: Block(g72)
    c: InternalAlignment(g76,g75)
    c: InternalAlignment(g77,g75)
    c: InternalAlignment(g78,g80)
    c: InternalAlignment(g79,g80)
    c: Block(g80)
    c: Coincident(g75,g80)
    c: Block(g75)
    c: InternalAlignment(g82,g81)
    c: InternalAlignment(g83,g81)
    c: InternalAlignment(g84,g86)
    c: InternalAlignment(g85,g86)
    c: Block(g86)
    c: Coincident(g81,g86)
    c: Block(g81)
    c: Horizontal(g87)
    c: Block(g87)
    c: Horizontal(g88)
    c: Distance(g88) = 4.14
    c: Horizontal(g89)
    c: Equal(g88,g89) = 4.14
    c: Block(g89)
    c: Block(g88)
    c: Coincident(g90,g87)
    c: Vertical(g90)
    c: Distance(g90) = 11.88
    c: Coincident(g91,g90)
    c: Horizontal(g91)
    c: Coincident(g92,g91)
    c: Vertical(g92)
    c: Distance(g91) = 4.03
    c: Distance(g92) = 1.9
    c: Coincident(g93,g87)
    c: Vertical(g93)
    c: Vertical(g94)
    c: Coincident(g94,g88)
    c: Distance(g93) = 5.8
    c: Distance(g94) = 5.8
    c: Vertical(g95)
    c: Coincident(g95,g88)
    c: Distance(g95) = 6.9
    c: Coincident(g107,g92)
    c: Weight(g96) = 1
    c: Equal(g96, g97-g106) x10
    c: InternalAlignment(g96-g106 -> g107) x11
    c: InternalAlignment(g108-g116 -> g107) x9
    c: Block(g107)
    c: Block(g117)
    c: Coincident(g126,g93)
    c: Weight(g118) = 1
    c: Equal(g118, g119-g125) x7
    c: Coincident(g126,g95)
    c: InternalAlignment(g118-g125 -> g126) x8
    c: InternalAlignment(g127-g132 -> g126) x6
    c: Coincident(g133,g94)
    c: Block(g126)
    c: Block(g133)
    c: Coincident(g134,g133)
    c: Coincident(g134,g89)
    c: Vertical(g134)
    c: Horizontal(g135)
    c: Block(g135)
    c: Horizontal(g136)
    c: Equal(g88,g136) = 4.14
    c: Horizontal(g137)
    c: Equal(g136,g137) = 4.14
    c: Block(g137)
    c: Block(g136)
    c: Coincident(g138,g135)
    c: Vertical(g138)
    c: Equal(g90,g138) = 11.88
    c: Coincident(g139,g138)
    c: Horizontal(g139)
    c: Coincident(g140,g139)
    c: Vertical(g140)
    c: Equal(g91,g139) = 4.03
    c: Equal(g92,g140) = 1.9
    c: Coincident(g141,g135)
    c: Vertical(g141)
    c: Vertical(g142)
    c: Coincident(g142,g136)
    c: Equal(g93,g141) = 5.8
    c: Equal(g94,g142) = 5.8
    c: Vertical(g143)
    c: Coincident(g143,g136)
    c: Equal(g95,g143) = 6.9
    c: Coincident(g149,g140)
    c: Equal(g96,g144) = 1
    c: Equal(g144, g145-g148) x4
    c: InternalAlignment(g144-g148 -> g149) x5
    c: InternalAlignment(g150-g158 -> g149) x9
    c: Block(g149)
    c: Block(g159)
    c: Coincident(g168,g141)
    c: Equal(g118,g160) = 1
    c: Equal(g160, g161-g167) x7
    c: Coincident(g168,g143)
    c: InternalAlignment(g160-g167 -> g168) x8
    c: InternalAlignment(g169-g174 -> g168) x6
    c: Coincident(g175,g142)
    c: Block(g168)
    c: Block(g175)
    c: Coincident(g176,g175)
    c: Coincident(g176,g137)
    c: Vertical(g176)
    c: Coincident(g177,g137)
    c: Vertical(g177)
    c: Coincident(g178,g177)
    c: Coincident(g178,g159)
    c: InternalAlignment(g179,g178)
    c: InternalAlignment(g180,g178)
    c: Block(g178)
    c: Vertical(g181)
    c: Coincident(g181,g89)
    c: Block(g5)
    c: Coincident(g182,g1)
    c: Coincident(g182,g5)
    c: Horizontal(g182)
    c: Coincident(g186,g117)
    c: Weight(g183) = 1
    c: Equal(g183,g184)
    c: Equal(g183,g185)
    c: Coincident(g186,g181)
    c: InternalAlignment(g183,g186)
    c: InternalAlignment(g184,g186)
    c: InternalAlignment(g185,g186)
    c: InternalAlignment(g187,g186)
    c: InternalAlignment(g188,g186)
    c: Block(g186)
    c: InternalAlignment(g190,g189)
    c: InternalAlignment(g191,g189)
    c: Block(g189)
    c: InternalAlignment(g193,g192)
    c: InternalAlignment(g194,g192)
    c: Block(g192)
    c: Horizontal(g195)
    c: Block(g195)
    c: Coincident(g196,g195)
    c: Vertical(g196)
    c: Block(g196)
    c: Distance(g195) = 3.71244
    c: Coincident(g197,g196)
    c: Horizontal(g197)
    c: Distance(g197) = 4.1
    c: Coincident(g198,g192)
    c: Coincident(g198,g197)
    c: Vertical(g198)
    c: Block(g198)
    c: Coincident(g199,g192)
    c: Coincident(g199,g195)
    c: Vertical(g199)
    c: Block(g199)
    c: Horizontal(g200)
    c: Block(g200)
    c: Coincident(g201,g200)
    c: Vertical(g201)
    c: Block(g201)
    c: Coincident(g202,g201)
    c: Horizontal(g202)
    c: Block(g202)
    c: Coincident(g203,g202)
    c: Vertical(g203)
    c: Block(g203)
    c: Coincident(g204,g200)
    c: Vertical(g204)
    c: Block(g204)
    c: Coincident(g215,g203)
    c: Weight(g206) = 1
    c: Equal(g206, g207-g214) x8
    c: Coincident(g215,g205)
    c: InternalAlignment(g206-g214 -> g215) x9
    c: InternalAlignment(g216-g222 -> g215) x7
    c: Coincident(g233,g204)
    c: Weight(g223) = 1
    c: Equal(g223, g224-g232) x9
    c: Coincident(g233,g205)
    c: InternalAlignment(g223-g232 -> g233) x10
    c: InternalAlignment(g234-g241 -> g233) x8
    c: Vertical(g205)
    c: Block(g205)
    c: Block(g215)
    c: Block(g233)
    c: Horizontal(g242)
    c: Horizontal(g243)
    c: Block(g242)
    c: Block(g243)
    c: Vertical(g244)
    c: Block(g244)
    c: Coincident(g270,g243)
    c: Weight(g245) = 1
    c: Equal(g245, g246-g269) x24
    c: Coincident(g270,g244)
    c: InternalAlignment(g245-g269 -> g270) x25
    c: InternalAlignment(g271-g293 -> g270) x23
    c: Coincident(g305,g242)
    c: Weight(g294) = 1
    c: Equal(g294, g295-g304) x10
    c: Coincident(g305,g242)
    c: InternalAlignment(g294-g304 -> g305) x11
    c: InternalAlignment(g306-g314 -> g305) x9
    c: Block(g305)
    c: Coincident(g327,g243)
    c: Weight(g315) = 1
    c: Equal(g315, g316-g326) x11
    c: Coincident(g327,g244)
    c: InternalAlignment(g315-g326 -> g327) x12
    c: InternalAlignment(g328-g337 -> g327) x10
    c: Block(g327)
    c: Block(g270)
FEATURE [PartDesign::Body] Body  label="CommodoreLogoAndText"
  Group = -> [Sketch083]
  Origin = -> Origin
FEATURE [Part::Extrusion] Extrude074  label="CommodoreLogoAndText001"
  Base = -> Sketch083
  Dir = (0,0,1)
  DirMode = 2
  FaceMakerClass = Part::FaceMakerBullseye
  LengthFwd = 10
  LengthRev = 0
  Solid = true
  Symmetric = false
FEATURE [Part::FeaturePython] Clone  label="CommodoreLogoAndTextScale"  # Draft clone (typed FeaturePython)
  AttacherType = Attacher::AttachEngine3D
  Fuse = false
  Objects = -> [Extrude074]
  Placement = pos=(111,5.37,-11.6) rot=(0,0,1;0rad)
  Scale = (0.62,0.62,1)
FEATURE [Part::Mirroring] Part__Mirroring  label="CommodoreLogoAndTextScale (Mirror #1)"
  Base = (0,0,0)
  Normal = (1,0,0)
  Placement = pos=(123.576,0,0) rot=(0,0,1;0rad)
  Source = -> Clone
FEATURE [Sketcher::SketchObject] Sketch084
  FullyConstrained = true
  MapMode = 5
  Support = -> [XY_Plane001]
  sketch-geometry (338):
    g0: LineSegment StartX=-151.619 StartY=28.8932 StartZ=0 EndX=-140.819 EndY=28.8932 EndZ=0
    g1: LineSegment StartX=-151.619 StartY=24.0313 StartZ=0 EndX=-151.619 EndY=28.8932 EndZ=0
    g2: LineSegment StartX=-140.819 StartY=17.7713 StartZ=0 EndX=-151.619 EndY=17.7713 EndZ=0
    g3: LineSegment StartX=-151.619 StartY=17.7713 StartZ=0 EndX=-151.619 EndY=22.6313 EndZ=0
    g4: LineSegment StartX=-151.619 StartY=22.6313 StartZ=0 EndX=-145.128 EndY=22.6313 EndZ=0
    g5: LineSegment StartX=-145.128 StartY=24.0313 StartZ=0 EndX=-140.819 EndY=28.8932 EndZ=0
    g6: LineSegment StartX=-145.128 StartY=22.6313 StartZ=0 EndX=-140.819 EndY=17.7713 EndZ=0
    g7: ArcOfCircle CenterX=-155.157 CenterY=23.3323 CenterZ=0 NormalX=0 NormalY=0 NormalZ=1 AngleXU=0 Radius=6.92354 StartAngle=1.03434 EndAngle=5.24885
    g8: ArcOfCircle CenterX=-155.157 CenterY=23.3323 CenterZ=0 NormalX=0 NormalY=0 NormalZ=1 AngleXU=0 Radius=12.6269 StartAngle=1.28675 EndAngle=4.99643
    g9: LineSegment StartX=-151.619 StartY=35.4532 StartZ=0 EndX=-151.619 EndY=29.2832 EndZ=0
    g10: LineSegment StartX=-151.619 StartY=17.3813 StartZ=0 EndX=-151.619 EndY=11.2113 EndZ=0
    g11-g21: Circle x11 (B-spline internal-alignment scaffolding for g22; pole/knot coordinates omitted)
    g22: BSplineCurve PolesCount=11 KnotsCount=9 Degree=3 IsPeriodic=0
    g23-g31: GeomPoint x9 (B-spline internal-alignment scaffolding for g22; pole/knot coordinates omitted)
    g32-g49: Circle x18 (B-spline internal-alignment scaffolding for g50; pole/knot coordinates omitted)
    g50: BSplineCurve PolesCount=18 KnotsCount=16 Degree=3 IsPeriodic=0
    g51-g66: GeomPoint x16 (B-spline internal-alignment scaffolding for g50; pole/knot coordinates omitted)
    g67: LineSegment StartX=-117.124 StartY=30.093 StartZ=0 EndX=-117.603 EndY=26.5272 EndZ=0
    g68: LineSegment StartX=-117.603 StartY=17.8472 StartZ=0 EndX=-117.124 EndY=14.2659 EndZ=0
    g69: Ellipse CenterX=-109.671 CenterY=20.025 CenterZ=0 NormalX=0 NormalY=0 NormalZ=1 MajorRadius=3.34798 MinorRadius=2.71052 AngleXU=-1.56793
    g70: GeomPoint X=-109.666 Y=18.0598 Z=0
    g71: GeomPoint X=-109.677 Y=21.9902 Z=0
    g72: Ellipse CenterX=-109.671 CenterY=20.0123 CenterZ=0 NormalX=0 NormalY=0 NormalZ=1 MajorRadius=6.93002 MinorRadius=6.36273 AngleXU=-3.13976
    g73: GeomPoint X=-112.417 Y=20.0073 Z=0
    g74: GeomPoint X=-106.925 Y=20.0173 Z=0
    g75: Ellipse CenterX=-51.7682 CenterY=20.1463 CenterZ=0 NormalX=0 NormalY=0 NormalZ=1 MajorRadius=3.19279 MinorRadius=2.71052 AngleXU=-1.52774
    g76: GeomPoint X=-51.6955 Y=18.4606 Z=0
    g77: GeomPoint X=-51.8408 Y=21.832 Z=0
    g78: GeomPoint X=-54.5142 Y=20.1413 Z=0
    g79: GeomPoint X=-49.0221 Y=20.1513 Z=0
    g80: Ellipse CenterX=-51.7682 CenterY=20.1463 CenterZ=0 NormalX=0 NormalY=0 NormalZ=1 MajorRadius=6.93002 MinorRadius=6.36273 AngleXU=-3.13976
    g81: Ellipse CenterX=-22.8436 CenterY=20.1783 CenterZ=0 NormalX=0 NormalY=0 NormalZ=1 MajorRadius=3.31512 MinorRadius=2.71052 AngleXU=-1.60214
    g82: GeomPoint X=-22.9034 Y=18.2706 Z=0
    g83: GeomPoint X=-22.7838 Y=22.0861 Z=0
    g84: GeomPoint X=-25.5897 Y=20.1733 Z=0
    g85: GeomPoint X=-20.0976 Y=20.1833 Z=0
    g86: Ellipse CenterX=-22.8436 CenterY=20.1783 CenterZ=0 NormalX=0 NormalY=0 NormalZ=1 MajorRadius=6.93002 MinorRadius=6.36273 AngleXU=-3.13976
    g87: LineSegment StartX=-101.889 StartY=14.1107 StartZ=0 EndX=-97.7455 EndY=14.1107 EndZ=0
    g88: LineSegment StartX=-93.8155 StartY=14.1107 StartZ=0 EndX=-89.6755 EndY=14.1107 EndZ=0
    g89: LineSegment StartX=-85.7455 StartY=14.1107 StartZ=0 EndX=-81.6055 EndY=14.1107 EndZ=0
    g90: LineSegment StartX=-101.889 StartY=14.1107 StartZ=0 EndX=-101.889 EndY=25.9907 EndZ=0
    g91: LineSegment StartX=-101.889 StartY=25.9907 StartZ=0 EndX=-97.8594 EndY=25.9907 EndZ=0
    g92: LineSegment StartX=-97.8594 StartY=25.9907 StartZ=0 EndX=-97.8594 EndY=24.0907 EndZ=0
    g93: LineSegment StartX=-97.7455 StartY=14.1107 StartZ=0 EndX=-97.7455 EndY=19.9107 EndZ=0
    g94: LineSegment StartX=-89.6755 StartY=14.1107 StartZ=0 EndX=-89.6755 EndY=19.9107 EndZ=0
    g95: LineSegment StartX=-93.8155 StartY=14.1107 StartZ=0 EndX=-93.8155 EndY=21.0107 EndZ=0
    g96-g106: Circle x11 (B-spline internal-alignment scaffolding for g107; pole/knot coordinates omitted)
    g107: BSplineCurve PolesCount=11 KnotsCount=9 Degree=3 IsPeriodic=0
    g108-g116: GeomPoint x9 (B-spline internal-alignment scaffolding for g107; pole/knot coordinates omitted)
    g117: BSplineCurve PolesCount=11 KnotsCount=9 Degree=3 IsPeriodic=0
    g118-g125: Circle x8 (B-spline internal-alignment scaffolding for g126; pole/knot coordinates omitted)
    g126: BSplineCurve PolesCount=8 KnotsCount=6 Degree=3 IsPeriodic=0
    g127-g132: GeomPoint x6 (B-spline internal-alignment scaffolding for g126; pole/knot coordinates omitted)
    g133: BSplineCurve PolesCount=8 KnotsCount=6 Degree=3 IsPeriodic=0
    g134: LineSegment StartX=-85.7455 StartY=21.0107 StartZ=0 EndX=-85.7455 EndY=14.1107 EndZ=0
    g135: LineSegment StartX=-80.0879 StartY=14.1107 StartZ=0 EndX=-75.944 EndY=14.1107 EndZ=0
    g136: LineSegment StartX=-72.014 StartY=14.1107 StartZ=0 EndX=-67.874 EndY=14.1107 EndZ=0
    g137: LineSegment StartX=-63.944 StartY=14.1107 StartZ=0 EndX=-59.804 EndY=14.1107 EndZ=0
    g138: LineSegment StartX=-80.0879 StartY=14.1107 StartZ=0 EndX=-80.0879 EndY=25.9907 EndZ=0
    g139: LineSegment StartX=-80.0879 StartY=25.9907 StartZ=0 EndX=-76.0579 EndY=25.9907 EndZ=0
    g140: LineSegment StartX=-76.0579 StartY=25.9907 StartZ=0 EndX=-76.0579 EndY=24.0907 EndZ=0
    g141: LineSegment StartX=-75.944 StartY=14.1107 StartZ=0 EndX=-75.944 EndY=19.9107 EndZ=0
    g142: LineSegment StartX=-67.874 StartY=14.1107 StartZ=0 EndX=-67.874 EndY=19.9107 EndZ=0
    g143: LineSegment StartX=-72.014 StartY=14.1107 StartZ=0 EndX=-72.014 EndY=21.0107 EndZ=0
    g144-g148: Circle x5 (B-spline internal-alignment scaffolding for g149; pole/knot coordinates omitted)
    g149: BSplineCurve PolesCount=11 KnotsCount=9 Degree=3 IsPeriodic=0
    g150-g158: GeomPoint x9 (B-spline internal-alignment scaffolding for g149; pole/knot coordinates omitted)
    g159: BSplineCurve PolesCount=11 KnotsCount=9 Degree=3 IsPeriodic=0
    g160-g167: Circle x8 (B-spline internal-alignment scaffolding for g168; pole/knot coordinates omitted)
    g168: BSplineCurve PolesCount=8 KnotsCount=6 Degree=3 IsPeriodic=0
    g169-g174: GeomPoint x6 (B-spline internal-alignment scaffolding for g168; pole/knot coordinates omitted)
    g175: BSplineCurve PolesCount=8 KnotsCount=6 Degree=3 IsPeriodic=0
    g176: LineSegment StartX=-63.944 StartY=21.0107 StartZ=0 EndX=-63.944 EndY=14.1107 EndZ=0
    g177: LineSegment StartX=-59.804 StartY=14.1107 StartZ=0 EndX=-59.804 EndY=21.5868 EndZ=0
    g178: BSplineCurve PolesCount=4 KnotsCount=2 Degree=3 IsPeriodic=0
    g179: GeomPoint X=-59.804 Y=21.5868 Z=0
    g180: GeomPoint X=-60.2379 Y=24.0907 Z=0
    g181: LineSegment StartX=-81.6055 StartY=14.1107 StartZ=0 EndX=-81.6055 EndY=21.5868 EndZ=0
    g182: LineSegment StartX=-151.619 StartY=24.0313 StartZ=0 EndX=-145.128 EndY=24.0313 EndZ=0
    g183: Circle CenterX=-82.0394 CenterY=24.0907 CenterZ=0 NormalX=0 NormalY=0 NormalZ=1 AngleXU=0 Radius=1
    g184: Circle CenterX=-81.7131 CenterY=23.2736 CenterZ=0 NormalX=0 NormalY=0 NormalZ=1 AngleXU=0 Radius=1
    g185: Circle CenterX=-81.6055 CenterY=21.5868 CenterZ=0 NormalX=0 NormalY=0 NormalZ=1 AngleXU=0 Radius=1
    g186: BSplineCurve PolesCount=3 KnotsCount=2 Degree=2 IsPeriodic=0
    g187: GeomPoint X=-82.0394 Y=24.0907 Z=0
    g188: GeomPoint X=-81.6055 Y=21.5868 Z=0
    g189: Ellipse CenterX=-37.3522 CenterY=19.9515 CenterZ=0 NormalX=0 NormalY=0 NormalZ=1 MajorRadius=2.99755 MinorRadius=2.49 AngleXU=1.5708
    g190: GeomPoint X=-37.3522 Y=21.6203 Z=0
    g191: GeomPoint X=-37.3522 Y=18.2826 Z=0
    g192: ArcOfEllipse CenterX=-38.7647 CenterY=20.06 CenterZ=0 NormalX=0 NormalY=0 NormalZ=1 MajorRadius=6.30025 MinorRadius=5.3849 AngleXU=1.57276 StartAngle=5.50632 EndAngle=10.3035
    g193: GeomPoint X=-38.7711 Y=23.3304 Z=0
    g194: GeomPoint X=-38.7583 Y=16.7895 Z=0
    g195: LineSegment StartX=-34.6109 StartY=14.1107 StartZ=0 EndX=-30.8984 EndY=14.1107 EndZ=0
    g196: LineSegment StartX=-30.8984 StartY=14.1107 StartZ=0 EndX=-30.8984 EndY=31.1784 EndZ=0
    g197: LineSegment StartX=-30.8984 StartY=31.1784 StartZ=0 EndX=-34.9984 EndY=31.1784 EndZ=0
    g198: LineSegment StartX=-34.9984 StartY=24.5602 StartZ=0 EndX=-34.9984 EndY=31.1784 EndZ=0
    g199: LineSegment StartX=-34.6109 StartY=16.0476 StartZ=0 EndX=-34.6109 EndY=14.1107 EndZ=0
    g200: LineSegment StartX=-14.8781 StartY=14.1107 StartZ=0 EndX=-10.5106 EndY=14.1107 EndZ=0
    g201: LineSegment StartX=-14.8781 StartY=14.1107 StartZ=0 EndX=-14.8781 EndY=25.8504 EndZ=0
    g202: LineSegment StartX=-14.8781 StartY=25.8504 StartZ=0 EndX=-10.8534 EndY=25.8504 EndZ=0
    g203: LineSegment StartX=-10.8534 StartY=25.8504 StartZ=0 EndX=-10.8534 EndY=24.0923 EndZ=0
    g204: LineSegment StartX=-10.5106 StartY=14.1107 StartZ=0 EndX=-10.5106 EndY=19.7752 EndZ=0
    g205: LineSegment StartX=-5.96397 StartY=25.9304 StartZ=0 EndX=-5.96397 EndY=22.574 EndZ=0
    g206-g214: Circle x9 (B-spline internal-alignment scaffolding for g215; pole/knot coordinates omitted)
    g215: BSplineCurve PolesCount=9 KnotsCount=7 Degree=3 IsPeriodic=0
    g216-g222: GeomPoint x7 (B-spline internal-alignment scaffolding for g215; pole/knot coordinates omitted)
    g223-g232: Circle x10 (B-spline internal-alignment scaffolding for g233; pole/knot coordinates omitted)
    g233: BSplineCurve PolesCount=10 KnotsCount=8 Degree=3 IsPeriodic=0
    g234-g241: GeomPoint x8 (B-spline internal-alignment scaffolding for g233; pole/knot coordinates omitted)
    g242: LineSegment StartX=-1.58923 StartY=21.0696 StartZ=0 EndX=2.62034 EndY=21.0696 EndZ=0
    g243: LineSegment StartX=-1.55856 StartY=18.7342 StartZ=0 EndX=6.45946 EndY=18.7342 EndZ=0
    g244: LineSegment StartX=5.29231 StartY=17.386 StartZ=0 EndX=5.29231 EndY=14.3674 EndZ=0
    g245-g269: Circle x25 (B-spline internal-alignment scaffolding for g270; pole/knot coordinates omitted)
    g270: BSplineCurve PolesCount=25 KnotsCount=23 Degree=3 IsPeriodic=0
    g271-g293: GeomPoint x23 (B-spline internal-alignment scaffolding for g270; pole/knot coordinates omitted)
    g294-g304: Circle x11 (B-spline internal-alignment scaffolding for g305; pole/knot coordinates omitted)
    g305: BSplineCurve PolesCount=11 KnotsCount=9 Degree=3 IsPeriodic=0
    g306-g314: GeomPoint x9 (B-spline internal-alignment scaffolding for g305; pole/knot coordinates omitted)
    g315-g326: Circle x12 (B-spline internal-alignment scaffolding for g327; pole/knot coordinates omitted)
    g327: BSplineCurve PolesCount=12 KnotsCount=10 Degree=3 IsPeriodic=0
    g328-g337: GeomPoint x10 (B-spline internal-alignment scaffolding for g327; pole/knot coordinates omitted)
  constraints (252):
    c: Coincident(g1,g0)
    c: Horizontal(g0)
    c: Vertical(g1)
    c: Coincident(g2,g3)
    c: Coincident(g3,g4)
    c: Horizontal(g4)
    c: Horizontal(g2)
    c: Vertical(g3)
    c: Block(g1)
    c: Distance(g3) = 4.86
    c: Block(g4)
    c: Distance(g0) = 10.8
    c: Distance(g2) = 10.8
    c: Coincident(g5,g0)
    c: Coincident(g6,g4)
    c: Coincident(g6,g2)
    c: Block(g8)
    c: Block(g7)
    c: Coincident(g9,g8)
    c: Coincident(g9,g7)
    c: Vertical(g9)
    c: Coincident(g10,g7)
    c: Coincident(g10,g8)
    c: Vertical(g10)
    c: Weight(g11) = 1
    c: Equal(g11, g12-g21) x10
    c: InternalAlignment(g11-g21 -> g22) x11
    c: InternalAlignment(g23-g31 -> g22) x9
    c: Block(g22)
    c: Weight(g32) = 1
    c: Equal(g32, g33-g49) x17
    c: InternalAlignment(g32-g49 -> g50) x18
    c: InternalAlignment(g51-g66 -> g50) x16
    c: Block(g50)
    c: Coincident(g67,g50)
    c: Coincident(g67,g22)
    c: Coincident(g68,g22)
    c: Coincident(g68,g50)
    c: InternalAlignment(g70,g69)
    c: InternalAlignment(g71,g69)
    c: Block(g69)
    c: InternalAlignment(g73,g72)
    c: InternalAlignment(g74,g72)
    c: Block(g72)
    c: InternalAlignment(g76,g75)
    c: InternalAlignment(g77,g75)
    c: InternalAlignment(g78,g80)
    c: InternalAlignment(g79,g80)
    c: Block(g80)
    c: Coincident(g75,g80)
    c: Block(g75)
    c: InternalAlignment(g82,g81)
    c: InternalAlignment(g83,g81)
    c: InternalAlignment(g84,g86)
    c: InternalAlignment(g85,g86)
    c: Block(g86)
    c: Coincident(g81,g86)
    c: Block(g81)
    c: Horizontal(g87)
    c: Block(g87)
    c: Horizontal(g88)
    c: Distance(g88) = 4.14
    c: Horizontal(g89)
    c: Equal(g88,g89) = 4.14
    c: Block(g89)
    c: Block(g88)
    c: Coincident(g90,g87)
    c: Vertical(g90)
    c: Distance(g90) = 11.88
    c: Coincident(g91,g90)
    c: Horizontal(g91)
    c: Coincident(g92,g91)
    c: Vertical(g92)
    c: Distance(g91) = 4.03
    c: Distance(g92) = 1.9
    c: Coincident(g93,g87)
    c: Vertical(g93)
    c: Vertical(g94)
    c: Coincident(g94,g88)
    c: Distance(g93) = 5.8
    c: Distance(g94) = 5.8
    c: Vertical(g95)
    c: Coincident(g95,g88)
    c: Distance(g95) = 6.9
    c: Coincident(g107,g92)
    c: Weight(g96) = 1
    c: Equal(g96, g97-g106) x10
    c: InternalAlignment(g96-g106 -> g107) x11
    c: InternalAlignment(g108-g116 -> g107) x9
    c: Block(g107)
    c: Block(g117)
    c: Coincident(g126,g93)
    c: Weight(g118) = 1
    c: Equal(g118, g119-g125) x7
    c: Coincident(g126,g95)
    c: InternalAlignment(g118-g125 -> g126) x8
    c: InternalAlignment(g127-g132 -> g126) x6
    c: Coincident(g133,g94)
    c: Block(g126)
    c: Block(g133)
    c: Coincident(g134,g133)
    c: Coincident(g134,g89)
    c: Vertical(g134)
    c: Horizontal(g135)
    c: Block(g135)
    c: Horizontal(g136)
    c: Equal(g88,g136) = 4.14
    c: Horizontal(g137)
    c: Equal(g136,g137) = 4.14
    c: Block(g137)
    c: Block(g136)
    c: Coincident(g138,g135)
    c: Vertical(g138)
    c: Equal(g90,g138) = 11.88
    c: Coincident(g139,g138)
    c: Horizontal(g139)
    c: Coincident(g140,g139)
    c: Vertical(g140)
    c: Equal(g91,g139) = 4.03
    c: Equal(g92,g140) = 1.9
    c: Coincident(g141,g135)
    c: Vertical(g141)
    c: Vertical(g142)
    c: Coincident(g142,g136)
    c: Equal(g93,g141) = 5.8
    c: Equal(g94,g142) = 5.8
    c: Vertical(g143)
    c: Coincident(g143,g136)
    c: Equal(g95,g143) = 6.9
    c: Coincident(g149,g140)
    c: Equal(g96,g144) = 1
    c: Equal(g144, g145-g148) x4
    c: InternalAlignment(g144-g148 -> g149) x5
    c: InternalAlignment(g150-g158 -> g149) x9
    c: Block(g149)
    c: Block(g159)
    c: Coincident(g168,g141)
    c: Equal(g118,g160) = 1
    c: Equal(g160, g161-g167) x7
    c: Coincident(g168,g143)
    c: InternalAlignment(g160-g167 -> g168) x8
    c: InternalAlignment(g169-g174 -> g168) x6
    c: Coincident(g175,g142)
    c: Block(g168)
    c: Block(g175)
    c: Coincident(g176,g175)
    c: Coincident(g176,g137)
    c: Vertical(g176)
    c: Coincident(g177,g137)
    c: Vertical(g177)
    c: Coincident(g178,g177)
    c: Coincident(g178,g159)
    c: InternalAlignment(g179,g178)
    c: InternalAlignment(g180,g178)
    c: Block(g178)
    c: Vertical(g181)
    c: Coincident(g181,g89)
    c: Block(g5)
    c: Coincident(g182,g1)
    c: Coincident(g182,g5)
    c: Horizontal(g182)
    c: Coincident(g186,g117)
    c: Weight(g183) = 1
    c: Equal(g183,g184)
    c: Equal(g183,g185)
    c: Coincident(g186,g181)
    c: InternalAlignment(g183,g186)
    c: InternalAlignment(g184,g186)
    c: InternalAlignment(g185,g186)
    c: InternalAlignment(g187,g186)
    c: InternalAlignment(g188,g186)
    c: Block(g186)
    c: InternalAlignment(g190,g189)
    c: InternalAlignment(g191,g189)
    c: Block(g189)
    c: InternalAlignment(g193,g192)
    c: InternalAlignment(g194,g192)
    c: Block(g192)
    c: Horizontal(g195)
    c: Block(g195)
    c: Coincident(g196,g195)
    c: Vertical(g196)
    c: Block(g196)
    c: Distance(g195) = 3.71244
    c: Coincident(g197,g196)
    c: Horizontal(g197)
    c: Distance(g197) = 4.1
    c: Coincident(g198,g192)
    c: Coincident(g198,g197)
    c: Vertical(g198)
    c: Block(g198)
    c: Coincident(g199,g192)
    c: Coincident(g199,g195)
    c: Vertical(g199)
    c: Block(g199)
    c: Horizontal(g200)
    c: Block(g200)
    c: Coincident(g201,g200)
    c: Vertical(g201)
    c: Block(g201)
    c: Coincident(g202,g201)
    c: Horizontal(g202)
    c: Block(g202)
    c: Coincident(g203,g202)
    c: Vertical(g203)
    c: Block(g203)
    c: Coincident(g204,g200)
    c: Vertical(g204)
    c: Block(g204)
    c: Coincident(g215,g203)
    c: Weight(g206) = 1
    c: Equal(g206, g207-g214) x8
    c: Coincident(g215,g205)
    c: InternalAlignment(g206-g214 -> g215) x9
    c: InternalAlignment(g216-g222 -> g215) x7
    c: Coincident(g233,g204)
    c: Weight(g223) = 1
    c: Equal(g223, g224-g232) x9
    c: Coincident(g233,g205)
    c: InternalAlignment(g223-g232 -> g233) x10
    c: InternalAlignment(g234-g241 -> g233) x8
    c: Vertical(g205)
    c: Block(g205)
    c: Block(g215)
    c: Block(g233)
    c: Horizontal(g242)
    c: Horizontal(g243)
    c: Block(g242)
    c: Block(g243)
    c: Vertical(g244)
    c: Block(g244)
    c: Coincident(g270,g243)
    c: Weight(g245) = 1
    c: Equal(g245, g246-g269) x24
    c: Coincident(g270,g244)
    c: InternalAlignment(g245-g269 -> g270) x25
    c: InternalAlignment(g271-g293 -> g270) x23
    c: Coincident(g305,g242)
    c: Weight(g294) = 1
    c: Equal(g294, g295-g304) x10
    c: Coincident(g305,g242)
    c: InternalAlignment(g294-g304 -> g305) x11
    c: InternalAlignment(g306-g314 -> g305) x9
    c: Block(g305)
    c: Coincident(g327,g243)
    c: Weight(g315) = 1
    c: Equal(g315, g316-g326) x11
    c: Coincident(g327,g244)
    c: InternalAlignment(g315-g326 -> g327) x12
    c: InternalAlignment(g328-g337 -> g327) x10
    c: Block(g327)
    c: Block(g270)
FEATURE [Part::Extrusion] Extrude075  label="CommodoreLogoAndText002"
  Base = -> Sketch084
  Dir = (0,0,1)
  DirMode = 2
  FaceMakerClass = Part::FaceMakerBullseye
  LengthFwd = 10
  LengthRev = 0
  Solid = true
  Symmetric = false
FEATURE [Part::FeaturePython] Clone001  label="CommodoreLogoAndTextScale001"  # Draft clone (typed FeaturePython)
  AttacherType = Attacher::AttachEngine3D
  Fuse = false
  Objects = -> [Extrude075]
  Placement = pos=(112.566,5.37,73.6) rot=(0,0,1;0rad)
  Scale = (0.62,0.62,1)
FEATURE [Part::Cut] Cut073  label="sideA005"
  Base = -> Extrude002
  Tool = -> Part__Mirroring
FEATURE [Part::Cut] Cut074  label="sideB005"
  Base = -> Extrude028
  Tool = -> Clone001
FEATURE [Sketcher::SketchObject] Sketch085
  FullyConstrained = true
  Placement = pos=(0,0,0) rot=(-1,0,0;4.71239rad)
  sketch-geometry (10):
    g0: LineSegment StartX=0 StartY=0 StartZ=0 EndX=-7 EndY=0 EndZ=0
    g1: LineSegment StartX=-7 StartY=10 StartZ=0 EndX=-6.5 EndY=10 EndZ=0
    g2: LineSegment StartX=0 StartY=10 StartZ=0 EndX=-0.5 EndY=10 EndZ=0
    g3: ArcOfCircle CenterX=-3.5 CenterY=10 CenterZ=0 NormalX=0 NormalY=0 NormalZ=1 AngleXU=0 Radius=3 StartAngle=3.14159 EndAngle=6.28319
    g4: LineSegment StartX=-7 StartY=0 StartZ=0 EndX=-10.5 EndY=0 EndZ=0
    g5: LineSegment StartX=0 StartY=0 StartZ=0 EndX=3.5 EndY=0 EndZ=0
    g6: ArcOfCircle CenterX=-10.5 CenterY=3.5 CenterZ=0 NormalX=0 NormalY=0 NormalZ=1 AngleXU=0 Radius=3.5 StartAngle=4.71239 EndAngle=6.28319
    g7: ArcOfCircle CenterX=3.5 CenterY=3.5 CenterZ=0 NormalX=0 NormalY=0 NormalZ=1 AngleXU=0 Radius=3.5 StartAngle=3.14159 EndAngle=4.71239
    g8: LineSegment StartX=-7 StartY=3.5 StartZ=0 EndX=-7 EndY=10 EndZ=0
    g9: LineSegment StartX=0 StartY=10 StartZ=0 EndX=0 EndY=3.5 EndZ=0
  constraints (26):
    c: Coincident(g0,g-1)
    c: Horizontal(g0)
    c: Distance(g0) = 7
    c: Horizontal(g1)
    c: Distance(g1) = 0.5
    c: Horizontal(g2)
    c: Distance(g2) = 0.5
    c: Coincident(g3,g1)
    c: Coincident(g3,g2)
    c: Block(g3)
    c: Coincident(g4,g0)
    c: Horizontal(g4)
    c: Distance(g4) = 3.5
    c: Coincident(g5,g0)
    c: Distance(g5) = 3.5
    c: Horizontal(g5)
    c: Coincident(g6,g4)
    c: Block(g6)
    c: Coincident(g7,g5)
    c: Block(g7)
    c: Coincident(g8,g6)
    c: Coincident(g8,g1)
    c: Vertical(g8)
    c: Coincident(g9,g2)
    c: Coincident(g9,g7)
    c: Vertical(g9)
FEATURE [Part::Extrusion] Extrude076  label="backRightCasePillarSideBracket"
  Base = -> Sketch085
  Dir = (0,-1,3e-16)
  DirMode = 2
  FaceMakerClass = Part::FaceMakerBullseye
  LengthFwd = 6.7
  LengthRev = 0
  Placement = pos=(16,11.5,0) rot=(0,0,1;0rad)
  Solid = true
  Symmetric = false
FEATURE [Sketcher::SketchObject] Sketch086
  FullyConstrained = true
  Placement = pos=(0,0,0) rot=(1,0,0;1.5708rad)
  sketch-geometry (10):
    g0: LineSegment StartX=0 StartY=0 StartZ=0 EndX=-7 EndY=0 EndZ=0
    g1: LineSegment StartX=-7 StartY=10 StartZ=0 EndX=-6.5 EndY=10 EndZ=0
    g2: LineSegment StartX=0 StartY=10 StartZ=0 EndX=-0.5 EndY=10 EndZ=0
    g3: ArcOfCircle CenterX=-3.5 CenterY=10 CenterZ=0 NormalX=0 NormalY=0 NormalZ=1 AngleXU=0 Radius=3 StartAngle=3.14159 EndAngle=6.28319
    g4: LineSegment StartX=-7 StartY=0 StartZ=0 EndX=-10.5 EndY=0 EndZ=0
    g5: LineSegment StartX=0 StartY=0 StartZ=0 EndX=3.5 EndY=0 EndZ=0
    g6: ArcOfCircle CenterX=-10.5 CenterY=3.5 CenterZ=0 NormalX=0 NormalY=0 NormalZ=1 AngleXU=0 Radius=3.5 StartAngle=4.71239 EndAngle=6.28319
    g7: ArcOfCircle CenterX=3.5 CenterY=3.5 CenterZ=0 NormalX=0 NormalY=0 NormalZ=1 AngleXU=0 Radius=3.5 StartAngle=3.14159 EndAngle=4.71239
    g8: LineSegment StartX=-7 StartY=3.5 StartZ=0 EndX=-7 EndY=10 EndZ=0
    g9: LineSegment StartX=0 StartY=10 StartZ=0 EndX=0 EndY=3.5 EndZ=0
  constraints (26):
    c: Coincident(g0,g-1)
    c: Horizontal(g0)
    c: Distance(g0) = 7
    c: Horizontal(g1)
    c: Distance(g1) = 0.5
    c: Horizontal(g2)
    c: Distance(g2) = 0.5
    c: Coincident(g3,g1)
    c: Coincident(g3,g2)
    c: Block(g3)
    c: Coincident(g4,g0)
    c: Horizontal(g4)
    c: Distance(g4) = 3.5
    c: Coincident(g5,g0)
    c: Distance(g5) = 3.5
    c: Horizontal(g5)
    c: Coincident(g6,g4)
    c: Block(g6)
    c: Coincident(g7,g5)
    c: Block(g7)
    c: Coincident(g8,g6)
    c: Coincident(g8,g1)
    c: Vertical(g8)
    c: Coincident(g9,g2)
    c: Coincident(g9,g7)
    c: Vertical(g9)
FEATURE [Part::Extrusion] Extrude077  label="backLeftCasePillarSideBracket001"
  Base = -> Sketch086
  Dir = (0,-1,3e-16)
  DirMode = 2
  FaceMakerClass = Part::FaceMakerBullseye
  LengthFwd = 6.7
  LengthRev = 0
  Placement = pos=(9,11.5,72) rot=(0,1,0;3.14159rad)
  Solid = true
  Symmetric = false
FEATURE [Sketcher::SketchObject] Sketch087
  FullyConstrained = true
  Placement = pos=(0,0,0) rot=(1,0,0;1.5708rad)
  sketch-geometry (8):
    g0: LineSegment StartX=0 StartY=4e-16 StartZ=0 EndX=-7 EndY=4e-16 EndZ=0
    g1: LineSegment StartX=-7 StartY=4e-16 StartZ=0 EndX=-10.5 EndY=4e-16 EndZ=0
    g2: LineSegment StartX=0 StartY=4e-16 StartZ=0 EndX=3.5 EndY=4e-16 EndZ=0
    g3: ArcOfCircle CenterX=-10.5 CenterY=3.5 CenterZ=0 NormalX=0 NormalY=0 NormalZ=1 AngleXU=0 Radius=3.5 StartAngle=4.71239 EndAngle=6.28319
    g4: ArcOfCircle CenterX=3.5 CenterY=3.5 CenterZ=0 NormalX=0 NormalY=0 NormalZ=1 AngleXU=0 Radius=3.5 StartAngle=3.14159 EndAngle=4.71239
    g5: ArcOfCircle CenterX=-3.5 CenterY=3.5 CenterZ=0 NormalX=0 NormalY=0 NormalZ=1 AngleXU=0 Radius=3 StartAngle=3.14159 EndAngle=6.28319
    g6: LineSegment StartX=-7 StartY=3.5 StartZ=0 EndX=-6.5 EndY=3.5 EndZ=0
    g7: LineSegment StartX=-0.5 StartY=3.5 StartZ=0 EndX=0 EndY=3.5 EndZ=0
  constraints (20):
    c: Coincident(g0,g-1)
    c: Horizontal(g0)
    c: Distance(g0) = 7
    c: Coincident(g1,g0)
    c: Horizontal(g1)
    c: Distance(g1) = 3.5
    c: Coincident(g2,g0)
    c: Distance(g2) = 3.5
    c: Horizontal(g2)
    c: Coincident(g3,g1)
    c: Block(g3)
    c: Coincident(g4,g2)
    c: Block(g4)
    c: Horizontal(g6)
    c: Coincident(g5,g6)
    c: Block(g5)
    c: Coincident(g6,g3)
    c: Coincident(g7,g5)
    c: Coincident(g7,g4)
    c: Horizontal(g7)
FEATURE [Part::Extrusion] Extrude078  label="frontBackLeftCasePillarSideBracket001"
  Base = -> Sketch087
  Dir = (0,-1,2e-16)
  DirMode = 2
  FaceMakerClass = Part::FaceMakerBullseye
  LengthFwd = 6.7
  LengthRev = 0
  Placement = pos=(93,11.5,0) rot=(0,0,1;0rad)
  Solid = true
  Symmetric = false
FEATURE [Sketcher::SketchObject] Sketch088
  FullyConstrained = true
  Placement = pos=(0,0,0) rot=(1,0,0;1.5708rad)
  sketch-geometry (8):
    g0: LineSegment StartX=0 StartY=4e-16 StartZ=0 EndX=-7 EndY=4e-16 EndZ=0
    g1: LineSegment StartX=-7 StartY=4e-16 StartZ=0 EndX=-10.5 EndY=4e-16 EndZ=0
    g2: LineSegment StartX=0 StartY=4e-16 StartZ=0 EndX=3.5 EndY=4e-16 EndZ=0
    g3: ArcOfCircle CenterX=-10.5 CenterY=3.5 CenterZ=0 NormalX=0 NormalY=0 NormalZ=1 AngleXU=0 Radius=3.5 StartAngle=4.71239 EndAngle=6.28319
    g4: ArcOfCircle CenterX=3.5 CenterY=3.5 CenterZ=0 NormalX=0 NormalY=0 NormalZ=1 AngleXU=0 Radius=3.5 StartAngle=3.14159 EndAngle=4.71239
    g5: ArcOfCircle CenterX=-3.5 CenterY=3.5 CenterZ=0 NormalX=0 NormalY=0 NormalZ=1 AngleXU=0 Radius=3 StartAngle=3.14159 EndAngle=6.28319
    g6: LineSegment StartX=-7 StartY=3.5 StartZ=0 EndX=-6.5 EndY=3.5 EndZ=0
    g7: LineSegment StartX=-0.5 StartY=3.5 StartZ=0 EndX=0 EndY=3.5 EndZ=0
  constraints (20):
    c: Coincident(g0,g-1)
    c: Horizontal(g0)
    c: Distance(g0) = 7
    c: Coincident(g1,g0)
    c: Horizontal(g1)
    c: Distance(g1) = 3.5
    c: Coincident(g2,g0)
    c: Distance(g2) = 3.5
    c: Horizontal(g2)
    c: Coincident(g3,g1)
    c: Block(g3)
    c: Coincident(g4,g2)
    c: Block(g4)
    c: Horizontal(g6)
    c: Coincident(g5,g6)
    c: Block(g5)
    c: Coincident(g6,g3)
    c: Coincident(g7,g5)
    c: Coincident(g7,g4)
    c: Horizontal(g7)
FEATURE [Part::Extrusion] Extrude079  label="frontFrontRightCasePillarSideBracket002"
  Base = -> Sketch088
  Dir = (0,-1,2e-16)
  DirMode = 2
  FaceMakerClass = Part::FaceMakerBullseye
  LengthFwd = 2
  LengthRev = 0
  Placement = pos=(106,11.5,72) rot=(0,1,0;3.14159rad)
  Solid = true
  Symmetric = false
FEATURE [Part::Chamfer] Chamfer
  Base = -> Extrude076
  Edges = 1 edges r=3: [Edge19]
FEATURE [Part::Chamfer] Chamfer002
  Base = -> Extrude077
  Edges = 1 edges r=3: [Edge7]
FEATURE [Part::Chamfer] Chamfer003  label="backLeftCasePillarSideBracket002"
  Base = -> Chamfer002
  Edges = 1 edges r=3.8: [Edge29]
FEATURE [Part::Chamfer] Chamfer004  label="backRightCasePillarSideBracket001"
  Base = -> Chamfer
  Edges = 1 edges r=3.8: [Edge24]
FEATURE [Sketcher::SketchObject] Sketch089
  FullyConstrained = true
  Placement = pos=(0,0,0) rot=(1,0,0;1.5708rad)
  sketch-geometry (8):
    g0: LineSegment StartX=0 StartY=4e-16 StartZ=0 EndX=-7 EndY=4e-16 EndZ=0
    g1: LineSegment StartX=-7 StartY=4e-16 StartZ=0 EndX=-10.5 EndY=4e-16 EndZ=0
    g2: LineSegment StartX=0 StartY=4e-16 StartZ=0 EndX=3.5 EndY=4e-16 EndZ=0
    g3: ArcOfCircle CenterX=-10.5 CenterY=3.5 CenterZ=0 NormalX=0 NormalY=0 NormalZ=1 AngleXU=0 Radius=3.5 StartAngle=4.71239 EndAngle=6.28319
    g4: ArcOfCircle CenterX=3.5 CenterY=3.5 CenterZ=0 NormalX=0 NormalY=0 NormalZ=1 AngleXU=0 Radius=3.5 StartAngle=3.14159 EndAngle=4.71239
    g5: ArcOfCircle CenterX=-3.5 CenterY=3.5 CenterZ=0 NormalX=0 NormalY=0 NormalZ=1 AngleXU=0 Radius=3 StartAngle=3.14159 EndAngle=6.28319
    g6: LineSegment StartX=-7 StartY=3.5 StartZ=0 EndX=-6.5 EndY=3.5 EndZ=0
    g7: LineSegment StartX=-0.5 StartY=3.5 StartZ=0 EndX=0 EndY=3.5 EndZ=0
  constraints (20):
    c: Coincident(g0,g-1)
    c: Horizontal(g0)
    c: Distance(g0) = 7
    c: Coincident(g1,g0)
    c: Horizontal(g1)
    c: Distance(g1) = 3.5
    c: Coincident(g2,g0)
    c: Distance(g2) = 3.5
    c: Horizontal(g2)
    c: Coincident(g3,g1)
    c: Block(g3)
    c: Coincident(g4,g2)
    c: Block(g4)
    c: Horizontal(g6)
    c: Coincident(g5,g6)
    c: Block(g5)
    c: Coincident(g6,g3)
    c: Coincident(g7,g5)
    c: Coincident(g7,g4)
    c: Horizontal(g7)
FEATURE [Part::Extrusion] Extrude080  label="frontBackLeftCasePillarSideBracket002"
  Base = -> Sketch089
  Dir = (0,-1,2e-16)
  DirMode = 2
  FaceMakerClass = Part::FaceMakerBullseye
  LengthFwd = 6.7
  LengthRev = 0
  Placement = pos=(86,11.5,72) rot=(0,1,0;3.14159rad)
  Solid = true
  Symmetric = false
FEATURE [Sketcher::SketchObject] Sketch090
  FullyConstrained = true
  Placement = pos=(0,0,0) rot=(1,0,0;1.5708rad)
  sketch-geometry (18):
    g0: LineSegment StartX=-10.5 StartY=0 StartZ=0 EndX=-10.5 EndY=2.5 EndZ=0
    g1: LineSegment StartX=-7.22307 StartY=-2.29385 StartZ=0 EndX=-4.72307 EndY=-2.29385 EndZ=0
    g2: LineSegment StartX=-5.22039 StartY=7.5423 StartZ=0 EndX=-1.94346 EndY=5.24845 EndZ=0
    g3: LineSegment StartX=-10.5 StartY=0 StartZ=0 EndX=-7.22307 EndY=-2.29385 EndZ=0
    g4: LineSegment StartX=-5.78942 StartY=-0.24577 StartZ=0 EndX=-1.94346 EndY=5.24845 EndZ=0
    g5: LineSegment StartX=-5.22039 StartY=7.5423 StartZ=0 EndX=-9.06634 EndY=2.04808 EndZ=0
    g6: Circle CenterX=-10.5 CenterY=2.5 CenterZ=0 NormalX=0 NormalY=0 NormalZ=1 AngleXU=0 Radius=1
    g7: Circle CenterX=-10.5 CenterY=0 CenterZ=0 NormalX=0 NormalY=0 NormalZ=1 AngleXU=0 Radius=1
    g8: Circle CenterX=-9.06634 CenterY=2.04808 CenterZ=0 NormalX=0 NormalY=0 NormalZ=1 AngleXU=0 Radius=1
    g9: BSplineCurve PolesCount=3 KnotsCount=2 Degree=2 IsPeriodic=0
    g10: GeomPoint X=-10.5 Y=2.5 Z=0
    g11: GeomPoint X=-9.06634 Y=2.04808 Z=0
    g12: Circle CenterX=-4.72307 CenterY=-2.29385 CenterZ=0 NormalX=0 NormalY=0 NormalZ=1 AngleXU=0 Radius=1
    g13: Circle CenterX=-7.22307 CenterY=-2.29385 CenterZ=0 NormalX=0 NormalY=0 NormalZ=1 AngleXU=0 Radius=1
    g14: Circle CenterX=-5.78942 CenterY=-0.24577 CenterZ=0 NormalX=0 NormalY=0 NormalZ=1 AngleXU=0 Radius=1
    g15: BSplineCurve PolesCount=3 KnotsCount=2 Degree=2 IsPeriodic=0
    g16: GeomPoint X=-4.72307 Y=-2.29385 Z=0
    g17: GeomPoint X=-5.78942 Y=-0.24577 Z=0
  constraints (36):
    c: Vertical(g0)
    c: Distance(g0) = 2.5
    c: Horizontal(g1)
    c: Distance(g1) = 2.5
    c: Distance(g2) = 4
    c: Block(g1)
    c: Coincident(g3,g1)
    c: Coincident(g4,g2)
    c: Coincident(g5,g2)
    c: Block(g5)
    c: Block(g2)
    c: Block(g4)
    c: Coincident(g9,g0)
    c: Weight(g6) = 1
    c: Equal(g6,g7)
    c: Coincident(g7,g0)
    c: Equal(g6,g8)
    c: Coincident(g9,g5)
    c: InternalAlignment(g6,g9)
    c: InternalAlignment(g7,g9)
    c: InternalAlignment(g8,g9)
    c: InternalAlignment(g10,g9)
    c: InternalAlignment(g11,g9)
    c: Coincident(g15,g1)
    c: Weight(g12) = 1
    c: Equal(g12,g13)
    c: Coincident(g13,g1)
    c: Equal(g12,g14)
    c: Coincident(g15,g4)
    c: InternalAlignment(g12,g15)
    c: InternalAlignment(g13,g15)
    c: InternalAlignment(g14,g15)
    c: InternalAlignment(g16,g15)
    c: InternalAlignment(g17,g15)
    c: Block(g3)
    c: Block(g0)
